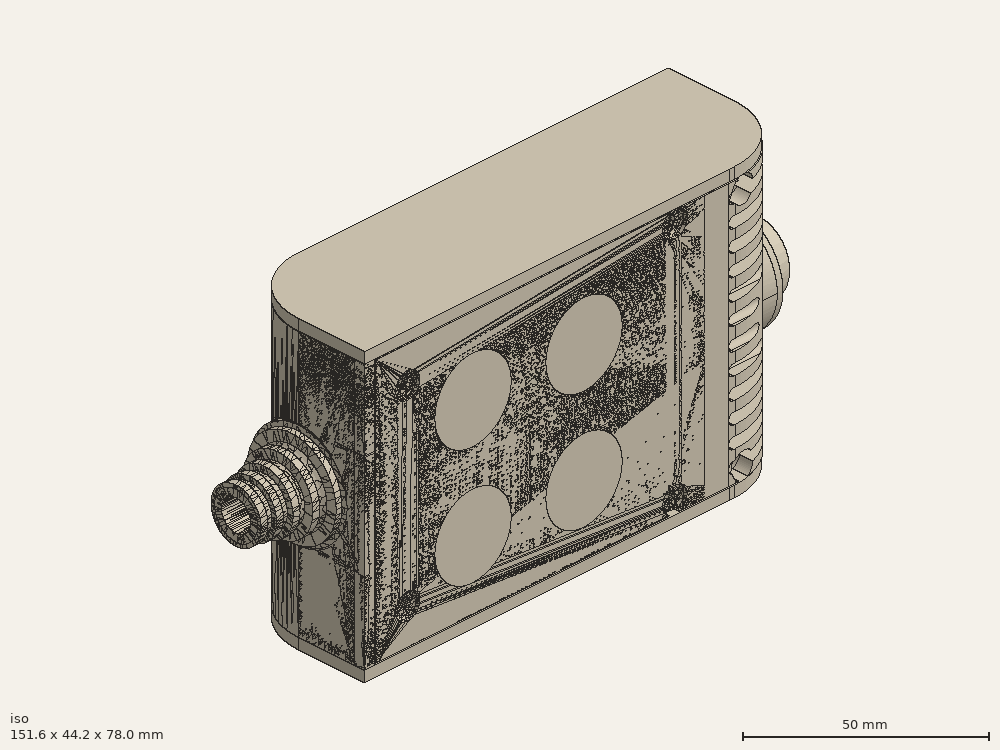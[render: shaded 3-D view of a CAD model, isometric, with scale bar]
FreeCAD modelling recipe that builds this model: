
FCSTD DOCUMENT  (FreeCAD 0.19R0.19.2)
Label: enclosure_190FCStd
License: All rights reserved
LicenseURL: http://en.wikipedia.org/wiki/All_rights_reserved
objects: Part::Revolution×152, Part::MultiFuse×146, Part::Feature×146, Sketcher::SketchObject×84, Part::Cut×70, Part::Cylinder×70, Part::Extrusion×67, Part::Fillet×58, Part::Box×36, App::MeasureDistance×4, PartDesign::Body×2, Image::ImagePlane×1
note: 831 computed .brp shape members not serialized (recipe doc carries the construction recipe); baked Part::Feature solids carry a one-line shape summary decoded from their .brp

FEATURE [Sketcher::SketchObject] Sketch  label="topSketch"
  FullyConstrained = true
  sketch-geometry (20):
    g0: LineSegment StartX=5.21097e-06 StartY=3 StartZ=0 EndX=5.21097e-06 EndY=19 EndZ=0
    g1: ArcOfCircle CenterX=19 CenterY=19 CenterZ=0 NormalX=0 NormalY=0 NormalZ=1 AngleXU=0 Radius=19 StartAngle=1.5708 EndAngle=3.14159
    g2: ArcOfCircle CenterX=19 CenterY=19 CenterZ=0 NormalX=0 NormalY=0 NormalZ=1 AngleXU=0 Radius=16 StartAngle=1.5708 EndAngle=3.14159
    g3: LineSegment StartX=114 StartY=35 StartZ=0 EndX=19 EndY=35 EndZ=0
    g4: LineSegment StartX=5.21097e-06 StartY=3 StartZ=0 EndX=5.21097e-06 EndY=0 EndZ=0
    g5: LineSegment StartX=3 StartY=0 StartZ=0 EndX=5.21097e-06 EndY=0 EndZ=0
    g6: LineSegment StartX=3 StartY=19 StartZ=0 EndX=3 EndY=0 EndZ=0
    g7: LineSegment StartX=19 StartY=38 StartZ=0 EndX=124 EndY=38 EndZ=0
    g8: Circle CenterX=119 CenterY=35 CenterZ=0 NormalX=0 NormalY=0 NormalZ=1 AngleXU=0 Radius=1
    g9: Circle CenterX=121 CenterY=35 CenterZ=0 NormalX=0 NormalY=0 NormalZ=1 AngleXU=0 Radius=1
    g10: Circle CenterX=121 CenterY=33 CenterZ=0 NormalX=0 NormalY=0 NormalZ=1 AngleXU=0 Radius=1
    g11: BSplineCurve PolesCount=3 KnotsCount=2 Degree=2 IsPeriodic=0
    g12: GeomPoint X=119 Y=35 Z=0
    g13: GeomPoint X=121 Y=33 Z=0
    g14: LineSegment StartX=119 StartY=35 StartZ=0 EndX=114 EndY=35 EndZ=0
    g15: ArcOfCircle CenterX=105 CenterY=19 CenterZ=0 NormalX=0 NormalY=0 NormalZ=1 AngleXU=0 Radius=19 StartAngle=5.7297 EndAngle=6.28319
    g16: ArcOfCircle CenterX=105 CenterY=19 CenterZ=0 NormalX=0 NormalY=0 NormalZ=1 AngleXU=0 Radius=16 StartAngle=5.60905 EndAngle=6.28319
    g17: LineSegment StartX=121 StartY=33 StartZ=0 EndX=121 EndY=19 EndZ=0
    g18: LineSegment StartX=124 StartY=38 StartZ=0 EndX=124 EndY=19 EndZ=0
    g19: LineSegment StartX=117.5 StartY=9.01251 StartZ=0 EndX=121.163 EndY=9.0125 EndZ=0
  constraints (46):
    c: Vertical(g0)
    c: Block(g0)
    c: Coincident(g1,g0)
    c: Block(g1)
    c: Coincident(g2,g1)
    c: Block(g2)
    c: Coincident(g3,g2)
    c: Horizontal(g3)
    c: Tangent(g3,g2)
    c: Coincident(g4,g0)
    c: Distance(g4) = 3
    c: Vertical(g4)
    c: Coincident(g5,g4)
    c: Horizontal(g5)
    c: Coincident(g6,g2)
    c: Coincident(g6,g5)
    c: Vertical(g6)
    c: Horizontal(g7)
    c: Distance(g7) = 105
    c: Coincident(g7,g1)
    c: Block(g3)
    c: Weight(g8) = 1
    c: Equal(g8,g9)
    c: Equal(g8,g10)
    c: InternalAlignment(g8,g11)
    c: InternalAlignment(g9,g11)
    c: InternalAlignment(g10,g11)
    c: InternalAlignment(g12,g11)
    c: InternalAlignment(g13,g11)
    c: Block(g11)
    c: Coincident(g14,g11)
    c: Coincident(g14,g3)
    c: Horizontal(g14)
    c: Block(g15)
    c: Coincident(g16,g15)
    c: Block(g16)
    c: Coincident(g17,g11)
    c: Coincident(g17,g16)
    c: Vertical(g17)
    c: Distance(g17) = 14
    c: Coincident(g18,g7)
    c: Coincident(g18,g15)
    c: Vertical(g18)
    c: Distance(g18) = 19
    c: Coincident(g19,g16)
    c: Coincident(g19,g15)
FEATURE [Sketcher::SketchObject] Sketch001  label="bottomSketch"
  FullyConstrained = true
  sketch-geometry (32):
    g0: LineSegment StartX=3.3 StartY=-6.03275e-07 StartZ=0 EndX=98 EndY=-6.03275e-07 EndZ=0
    g1: ArcOfCircle CenterX=98 CenterY=19 CenterZ=0 NormalX=0 NormalY=0 NormalZ=1 AngleXU=0 Radius=19 StartAngle=4.71239 EndAngle=5.71103
    g2: LineSegment StartX=6.3 StartY=8 StartZ=0 EndX=3.3 EndY=8 EndZ=0
    g3: LineSegment StartX=3.3 StartY=8 StartZ=0 EndX=3.3 EndY=-6.03275e-07 EndZ=0
    g4: ArcOfCircle CenterX=8.3 CenterY=5 CenterZ=0 NormalX=0 NormalY=0 NormalZ=1 AngleXU=0 Radius=2 StartAngle=3.14159 EndAngle=4.71239
    g5: LineSegment StartX=6.3 StartY=8 StartZ=0 EndX=6.3 EndY=5 EndZ=0
    g6: ArcOfCircle CenterX=98 CenterY=19 CenterZ=0 NormalX=0 NormalY=0 NormalZ=1 AngleXU=0 Radius=12.7 StartAngle=4.71239 EndAngle=6.28319
    g7: LineSegment StartX=94.7 StartY=3 StartZ=0 EndX=8.3 EndY=3 EndZ=0
    g8-g12: Circle x5 (B-spline internal-alignment scaffolding for g13; pole/knot coordinates omitted)
    g13: BSplineCurve PolesCount=5 KnotsCount=3 Degree=3 IsPeriodic=0
    g14: GeomPoint X=98 Y=6.3 Z=0
    g15: GeomPoint X=96.3938 Y=4.71946 Z=0
    g16: GeomPoint X=94.7 Y=3 Z=0
    g17-g23: Circle x7 (B-spline internal-alignment scaffolding for g24; pole/knot coordinates omitted)
    g24: BSplineCurve PolesCount=7 KnotsCount=5 Degree=3 IsPeriodic=0
    g25-g29: GeomPoint x5 (B-spline internal-alignment scaffolding for g24; pole/knot coordinates omitted)
    g30: ArcOfCircle CenterX=98 CenterY=19 CenterZ=0 NormalX=0 NormalY=0 NormalZ=1 AngleXU=0 Radius=15.7 StartAngle=5.81226 EndAngle=6.28319
    g31: LineSegment StartX=110.7 StartY=19 StartZ=0 EndX=113.7 EndY=19 EndZ=0
  constraints (41):
    c: Horizontal(g0)
    c: Coincident(g1,g0)
    c: Block(g1)
    c: Horizontal(g2)
    c: Distance(g2) = 3
    c: Coincident(g3,g2)
    c: Vertical(g3)
    c: Coincident(g3,g0)
    c: Block(g4)
    c: Block(g2)
    c: Coincident(g5,g2)
    c: Coincident(g5,g4)
    c: Vertical(g5)
    c: Coincident(g6,g1)
    c: Block(g6)
    c: Coincident(g7,g4)
    c: Horizontal(g7)
    c: Block(g0)
    c: Block(g7)
    c: Block(g3)
    c: Coincident(g13,g6)
    c: Weight(g8) = 1
    c: Equal(g8, g9-g12) x4
    c: Coincident(g13,g7)
    c: InternalAlignment(g8-g12 -> g13) x5
    c: InternalAlignment(g14,g13)
    c: InternalAlignment(g15,g13)
    c: InternalAlignment(g16,g13)
    c: Block(g13)
    c: Weight(g17) = 1
    c: Equal(g17, g18-g23) x6
    c: Coincident(g24,g1)
    c: InternalAlignment(g17-g23 -> g24) x7
    c: InternalAlignment(g25-g29 -> g24) x5
    c: Block(g24)
    c: Coincident(g30,g24)
    c: Coincident(g31,g6)
    c: Coincident(g31,g30)
    c: Horizontal(g31)
    c: Block(g31)
    c: Block(g30)
FEATURE [Part::Extrusion] Extrude  label="top"
  Base = -> Sketch
  Dir = (0,0,1)
  DirMode = 2
  FaceMakerClass = Part::FaceMakerBullseye
  LengthFwd = 72
  LengthRev = 0
  Solid = true
  Symmetric = false
FEATURE [Part::Extrusion] Extrude001  label="bottom"
  Base = -> Sketch001
  Dir = (0,0,1)
  DirMode = 2
  FaceMakerClass = Part::FaceMakerBullseye
  LengthFwd = 71.4
  LengthRev = 0
  Placement = pos=(0,0,0.3) rot=(0,0,1;0rad)
  Solid = true
  Symmetric = false
FEATURE [Sketcher::SketchObject] Sketch002  label="topSketch001"
  FullyConstrained = true
  sketch-geometry (8):
    g0: ArcOfCircle CenterX=19 CenterY=19.0975 CenterZ=0 NormalX=0 NormalY=0 NormalZ=1 AngleXU=0 Radius=18.9025 StartAngle=1.5708 EndAngle=3.14674
    g1: LineSegment StartX=0.0977805 StartY=19.0003 StartZ=0 EndX=0.0977805 EndY=0.000251602 EndZ=0
    g2: LineSegment StartX=19 StartY=38 StartZ=0 EndX=124 EndY=38 EndZ=0
    g3: LineSegment StartX=0.0977805 StartY=0.000251602 StartZ=0 EndX=105.098 EndY=0.000251602 EndZ=0
    g4: LineSegment StartX=124 StartY=38 StartZ=0 EndX=125.616 EndY=38 EndZ=0
    g5: LineSegment StartX=105.098 StartY=0.000251602 StartZ=0 EndX=106.713 EndY=0.000251602 EndZ=0
    g6: ArcOfCircle CenterX=106.616 CenterY=19 CenterZ=0 NormalX=0 NormalY=0 NormalZ=1 AngleXU=0 Radius=19 StartAngle=4.71754 EndAngle=6.28319
    g7: LineSegment StartX=125.616 StartY=38 StartZ=0 EndX=125.616 EndY=19 EndZ=0
  constraints (21):
    c: Block(g0)
    c: Coincident(g1,g0)
    c: Vertical(g1)
    c: Horizontal(g2)
    c: Distance(g2) = 105
    c: Coincident(g2,g0)
    c: Distance(g1) = 19
    c: Coincident(g3,g1)
    c: Horizontal(g3)
    c: Distance(g3) = 105
    c: Coincident(g4,g2)
    c: Horizontal(g4)
    c: Distance(g4) = 1.61553
    c: Horizontal(g5)
    c: Equal(g4,g5) = 1.61553
    c: Coincident(g5,g3)
    c: Block(g6)
    c: Coincident(g6,g5)
    c: Coincident(g7,g4)
    c: Coincident(g7,g6)
    c: Vertical(g7)
FEATURE [Part::Extrusion] Extrude002  label="sideA"
  Base = -> Sketch002
  Dir = (0,0,1)
  DirMode = 2
  FaceMakerClass = Part::FaceMakerBullseye
  LengthFwd = 3
  LengthRev = 0
  Placement = pos=(0,0,-3) rot=(0,0,1;0rad)
  Solid = true
  Symmetric = false
FEATURE [Sketcher::SketchObject] Sketch003  label="topSketch002"
  FullyConstrained = true
  sketch-geometry (6):
    g0: LineSegment StartX=19 StartY=38 StartZ=0 EndX=117 EndY=38 EndZ=0
    g1: ArcOfCircle CenterX=19 CenterY=19 CenterZ=0 NormalX=0 NormalY=0 NormalZ=1 AngleXU=0 Radius=19 StartAngle=1.5708 EndAngle=3.14159
    g2: LineSegment StartX=117 StartY=38 StartZ=0 EndX=117 EndY=19 EndZ=0
    g3: LineSegment StartX=98 StartY=1.0161e-12 StartZ=0 EndX=5.22862e-06 EndY=1.0161e-12 EndZ=0
    g4: LineSegment StartX=5.22862e-06 StartY=19 StartZ=0 EndX=5.22862e-06 EndY=1.0161e-12 EndZ=0
    g5: ArcOfCircle CenterX=98 CenterY=19 CenterZ=0 NormalX=0 NormalY=0 NormalZ=1 AngleXU=0 Radius=19 StartAngle=4.71239 EndAngle=6.28319
  constraints (16):
    c: Horizontal(g0)
    c: Distance(g0) = 98
    c: Coincident(g1,g0)
    c: Block(g1)
    c: Coincident(g2,g0)
    c: Vertical(g2)
    c: Distance(g2) = 19
    c: Horizontal(g3)
    c: Coincident(g4,g1)
    c: Vertical(g4)
    c: Coincident(g3,g4)
    c: Block(g3)
    c: Coincident(g5,g2)
    c: Coincident(g5,g3)
    c: Block(g0)
    c: Block(g5)
FEATURE [Sketcher::SketchObject] Sketch004
  FullyConstrained = true
  MapMode = 3
  Placement = pos=(0,0,0) rot=(1,0,0;1.5708rad)
  Support = -> [Extrude]
  sketch-geometry (8):
    g0: Circle CenterX=80.351 CenterY=-67.6202 CenterZ=0 NormalX=0 NormalY=0 NormalZ=1 AngleXU=0 Radius=2
    g1: Circle CenterX=80.351 CenterY=-67.6202 CenterZ=0 NormalX=0 NormalY=0 NormalZ=1 AngleXU=0 Radius=3
    g2: Circle CenterX=80.351 CenterY=-4.92017 CenterZ=0 NormalX=0 NormalY=0 NormalZ=1 AngleXU=0 Radius=2
    g3: Circle CenterX=80.351 CenterY=-4.92017 CenterZ=0 NormalX=0 NormalY=0 NormalZ=1 AngleXU=0 Radius=3
    g4: Circle CenterX=23.851 CenterY=-4.92017 CenterZ=0 NormalX=0 NormalY=0 NormalZ=1 AngleXU=0 Radius=2
    g5: Circle CenterX=23.851 CenterY=-4.92017 CenterZ=0 NormalX=0 NormalY=0 NormalZ=1 AngleXU=0 Radius=3
    g6: Circle CenterX=23.851 CenterY=-67.6202 CenterZ=0 NormalX=0 NormalY=0 NormalZ=1 AngleXU=0 Radius=2
    g7: Circle CenterX=23.851 CenterY=-67.6202 CenterZ=0 NormalX=0 NormalY=0 NormalZ=1 AngleXU=0 Radius=3
  constraints (8):
    c: Block(g3)
    c: Block(g2)
    c: Block(g1)
    c: Block(g0)
    c: Block(g6)
    c: Block(g7)
    c: Block(g4)
    c: Block(g5)
FEATURE [Part::Extrusion] Extrude004
  Base = -> Sketch004
  Dir = (0,-1,2e-16)
  DirMode = 2
  FaceMakerClass = Part::FaceMakerBullseye
  LengthFwd = 6
  LengthRev = 0
  Placement = pos=(0,9,0) rot=(0,0,1;0rad)
  Solid = true
  Symmetric = false
FEATURE [Sketcher::SketchObject] Sketch005
  FullyConstrained = true
  MapMode = 3
  Placement = pos=(0,0,0) rot=(1,0,0;1.5708rad)
  Support = -> [Extrude]
  sketch-geometry (8):
    g0: Circle CenterX=80.351 CenterY=-67.6202 CenterZ=0 NormalX=0 NormalY=0 NormalZ=1 AngleXU=0 Radius=3
    g1: Circle CenterX=80.351 CenterY=-4.92017 CenterZ=0 NormalX=0 NormalY=0 NormalZ=1 AngleXU=0 Radius=3
    g2: Circle CenterX=23.851 CenterY=-4.92017 CenterZ=0 NormalX=0 NormalY=0 NormalZ=1 AngleXU=0 Radius=3
    g3: Circle CenterX=23.851 CenterY=-67.6202 CenterZ=0 NormalX=0 NormalY=0 NormalZ=1 AngleXU=0 Radius=3
    g4: Circle CenterX=23.851 CenterY=-67.6202 CenterZ=0 NormalX=0 NormalY=0 NormalZ=1 AngleXU=0 Radius=5
    g5: Circle CenterX=80.351 CenterY=-67.6202 CenterZ=0 NormalX=0 NormalY=0 NormalZ=1 AngleXU=0 Radius=5
    g6: Circle CenterX=23.851 CenterY=-4.92017 CenterZ=0 NormalX=0 NormalY=0 NormalZ=1 AngleXU=0 Radius=5
    g7: Circle CenterX=80.351 CenterY=-4.92017 CenterZ=0 NormalX=0 NormalY=0 NormalZ=1 AngleXU=0 Radius=5
  constraints (8):
    c: Block(g1)
    c: Block(g0)
    c: Block(g3)
    c: Block(g2)
    c: Block(g5)
    c: Block(g4)
    c: Block(g6)
    c: Block(g7)
FEATURE [Part::Extrusion] Extrude005
  Base = -> Sketch005
  Dir = (0,-1,2e-16)
  DirMode = 2
  FaceMakerClass = Part::FaceMakerBullseye
  LengthFwd = 2
  LengthRev = 0
  Solid = true
  Symmetric = false
FEATURE [Sketcher::SketchObject] Sketch006
  FullyConstrained = true
  MapMode = 3
  Placement = pos=(0,0,0) rot=(1,0,0;1.5708rad)
  sketch-geometry (8):
    g0: Circle CenterX=80.351 CenterY=-67.6202 CenterZ=0 NormalX=0 NormalY=0 NormalZ=1 AngleXU=0 Radius=3
    g1: Circle CenterX=80.351 CenterY=-4.92017 CenterZ=0 NormalX=0 NormalY=0 NormalZ=1 AngleXU=0 Radius=3
    g2: Circle CenterX=23.851 CenterY=-4.92017 CenterZ=0 NormalX=0 NormalY=0 NormalZ=1 AngleXU=0 Radius=3
    g3: Circle CenterX=23.851 CenterY=-67.6202 CenterZ=0 NormalX=0 NormalY=0 NormalZ=1 AngleXU=0 Radius=3
    g4: Circle CenterX=23.851 CenterY=-67.6202 CenterZ=0 NormalX=0 NormalY=0 NormalZ=1 AngleXU=0 Radius=5
    g5: Circle CenterX=80.351 CenterY=-67.6202 CenterZ=0 NormalX=0 NormalY=0 NormalZ=1 AngleXU=0 Radius=5
    g6: Circle CenterX=23.851 CenterY=-4.92017 CenterZ=0 NormalX=0 NormalY=0 NormalZ=1 AngleXU=0 Radius=5
    g7: Circle CenterX=80.351 CenterY=-4.92017 CenterZ=0 NormalX=0 NormalY=0 NormalZ=1 AngleXU=0 Radius=5
  constraints (8):
    c: Block(g1)
    c: Block(g0)
    c: Block(g3)
    c: Block(g2)
    c: Block(g5)
    c: Block(g4)
    c: Block(g6)
    c: Block(g7)
FEATURE [Part::Extrusion] Extrude007
  Base = -> Sketch006
  Dir = (0,-1,2e-16)
  DirMode = 2
  FaceMakerClass = Part::FaceMakerBullseye
  LengthFwd = 2
  LengthRev = 0
  Solid = true
  Symmetric = false
FEATURE [Part::Fillet] Fillet
  Base = -> Extrude007
  Edges = 4 edges r=1.99: [Edge6,Edge12,Edge18,Edge24]
FEATURE [Part::Cut] Cut
  Base = -> Extrude005
  Placement = pos=(0,5,0) rot=(0,0,1;0rad)
  Tool = -> Fillet
FEATURE [Part::MultiFuse] Fusion  label="pCBScrews"
  Placement = pos=(-2.5,0,72.3) rot=(0,0,1;0rad)
  Shapes = -> [Extrude004,Cut]
FEATURE [App::MeasureDistance] Distance  label="Distance: 0.69 mm"
  Distance = 0.685967
  P1 = (24.0138,2.9647,0.3)
  P2 = (23.8901,3,-0.373787)
FEATURE [App::MeasureDistance] Distance001  label="Distance: 0.53 mm"
  Distance = 0.533607
  P1 = (80.2939,3,72.2334)
  P2 = (80.281,2.99661,71.7)
FEATURE [Part::Fillet] Fillet001
  Base = -> Extrude001
  Edges = 1 edges r=2.4: [Edge17]
FEATURE [Part::Fillet] Fillet002  label="bottom001"
  Base = -> Fillet001
  Edges = 1 edges r=2.4: [Edge36]
FEATURE [Part::Fillet] Fillet003  label="top001"
  Base = -> Extrude
  Edges = 1 edges r=2: [Edge1]
FEATURE [Sketcher::SketchObject] Sketch007
  FullyConstrained = true
  sketch-geometry (16):
    g0: LineSegment StartX=4 StartY=0 StartZ=0 EndX=4 EndY=2.4 EndZ=0
    g1: LineSegment StartX=4 StartY=2.4 StartZ=0 EndX=7 EndY=2.4 EndZ=0
    g2: LineSegment StartX=4 StartY=0 StartZ=0 EndX=5.7 EndY=0 EndZ=0
    g3: LineSegment StartX=5.7 StartY=0 StartZ=0 EndX=5.7 EndY=-5.6 EndZ=0
    g4-g8: Circle x5 (B-spline internal-alignment scaffolding for g9; pole/knot coordinates omitted)
    g9: BSplineCurve PolesCount=5 KnotsCount=3 Degree=3 IsPeriodic=0
    g10: GeomPoint X=7 Y=2.4 Z=0
    g11: GeomPoint X=10.4582 Y=-1.55472 Z=0
    g12: GeomPoint X=14 Y=-5.6 Z=0
    g13: LineSegment StartX=14 StartY=-5.6 StartZ=0 EndX=14 EndY=-14.1 EndZ=0
    g14: LineSegment StartX=14 StartY=-14.1 StartZ=0 EndX=6.5 EndY=-14.1 EndZ=0
    g15: LineSegment StartX=5.7 StartY=-5.6 StartZ=0 EndX=6.5 EndY=-14.1 EndZ=0
  constraints (28):
    c: Distance(g0) = 2.4
    c: Vertical(g0)
    c: Block(g0)
    c: Coincident(g1,g0)
    c: Horizontal(g1)
    c: Distance(g1) = 3
    c: Coincident(g2,g0)
    c: Horizontal(g2)
    c: Distance(g2) = 1.7
    c: Coincident(g3,g2)
    c: Vertical(g3)
    c: Distance(g3) = 5.6
    c: Coincident(g9,g1)
    c: Weight(g4) = 1
    c: Equal(g4, g5-g8) x4
    c: InternalAlignment(g4-g8 -> g9) x5
    c: InternalAlignment(g10,g9)
    c: InternalAlignment(g11,g9)
    c: InternalAlignment(g12,g9)
    c: Block(g9)
    c: Coincident(g13,g9)
    c: Vertical(g13)
    c: Distance(g13) = 8.5
    c: Coincident(g14,g13)
    c: Horizontal(g14)
    c: Distance(g14) = 7.5
    c: Coincident(g15,g3)
    c: Coincident(g15,g14)
FEATURE [Part::Feature] Face
  shape: bbox 10 x 16.5 x 2e-07 mm, 1 faces, 0 solids (baked)
FEATURE [Part::Revolution] Revolve  label="plugHousing"
  Angle = 360
  Axis = (0,1,0)
  Base = (0,0,0)
  FaceMakerClass = Part::FaceMakerBullseye
  Placement = pos=(0,0,36.15) rot=(0,0,1;0rad)
  Solid = false
  Source = -> Face
  Symmetric = false
FEATURE [Part::Feature] Face001
  shape: bbox 10 x 16.5 x 2e-07 mm, 1 faces, 0 solids (baked)
FEATURE [Part::Revolution] Revolve001  label="plugHousing001"
  Angle = 360
  Axis = (0,1,0)
  Base = (0,0,0)
  FaceMakerClass = Part::FaceMakerBullseye
  Placement = pos=(0,0,36.15) rot=(0,0,1;0rad)
  Solid = false
  Source = -> Face001
  Symmetric = false
FEATURE [Part::MultiFuse] Fusion001  label="plugHousing002"
  Placement = pos=(0,0,0) rot=(0,0,1;1.5708rad)
  Shapes = -> [Revolve001,Revolve]
FEATURE [Part::Feature] Face002
  shape: bbox 10 x 16.5 x 2e-07 mm, 1 faces, 0 solids (baked)
FEATURE [Part::Revolution] Revolve003  label="plugHousing005"
  Angle = 360
  Axis = (0,1,0)
  Base = (0,0,0)
  FaceMakerClass = Part::FaceMakerBullseye
  Placement = pos=(0,0,36.15) rot=(0,0,1;0rad)
  Solid = false
  Source = -> Face002
  Symmetric = false
FEATURE [Part::Feature] Face003
  shape: bbox 10 x 16.5 x 2e-07 mm, 1 faces, 0 solids (baked)
FEATURE [Part::Revolution] Revolve002  label="plugHousing003"
  Angle = 360
  Axis = (0,1,0)
  Base = (0,0,0)
  FaceMakerClass = Part::FaceMakerBullseye
  Placement = pos=(0,0,36.15) rot=(0,0,1;0rad)
  Solid = false
  Source = -> Face003
  Symmetric = false
FEATURE [Part::MultiFuse] Fusion002  label="plugHousing004"
  Placement = pos=(0,0,0) rot=(0,0,1;1.5708rad)
  Shapes = -> [Revolve002,Revolve003]
FEATURE [Part::MultiFuse] Fusion003  label="plugHousing006"
  Placement = pos=(0,19,0) rot=(0,0,1;3.14159rad)
  Shapes = -> [Fusion002,Fusion001]
FEATURE [Part::Feature] Face004
  shape: bbox 10 x 16.5 x 2e-07 mm, 1 faces, 0 solids (baked)
FEATURE [Part::Revolution] Revolve006  label="plugHousing010"
  Angle = 360
  Axis = (0,1,0)
  Base = (0,0,0)
  FaceMakerClass = Part::FaceMakerBullseye
  Placement = pos=(0,0,36.15) rot=(0,0,1;0rad)
  Solid = false
  Source = -> Face004
  Symmetric = false
FEATURE [Part::Feature] Face005
  shape: bbox 10 x 16.5 x 2e-07 mm, 1 faces, 0 solids (baked)
FEATURE [Part::Revolution] Revolve007  label="plugHousing011"
  Angle = 360
  Axis = (0,1,0)
  Base = (0,0,0)
  FaceMakerClass = Part::FaceMakerBullseye
  Placement = pos=(0,0,36.15) rot=(0,0,1;0rad)
  Solid = false
  Source = -> Face005
  Symmetric = false
FEATURE [Part::Feature] Face006
  shape: bbox 10 x 16.5 x 2e-07 mm, 1 faces, 0 solids (baked)
FEATURE [Part::Revolution] Revolve004  label="plugHousing007"
  Angle = 360
  Axis = (0,1,0)
  Base = (0,0,0)
  FaceMakerClass = Part::FaceMakerBullseye
  Placement = pos=(0,0,36.15) rot=(0,0,1;0rad)
  Solid = false
  Source = -> Face006
  Symmetric = false
FEATURE [Part::MultiFuse] Fusion004  label="plugHousing009"
  Placement = pos=(0,0,0) rot=(0,0,1;1.5708rad)
  Shapes = -> [Revolve004,Revolve007]
FEATURE [Part::Feature] Face007
  shape: bbox 10 x 16.5 x 2e-07 mm, 1 faces, 0 solids (baked)
FEATURE [Part::Revolution] Revolve005  label="plugHousing008"
  Angle = 360
  Axis = (0,1,0)
  Base = (0,0,0)
  FaceMakerClass = Part::FaceMakerBullseye
  Placement = pos=(0,0,36.15) rot=(0,0,1;0rad)
  Solid = false
  Source = -> Face007
  Symmetric = false
FEATURE [Part::MultiFuse] Fusion005  label="plugHousing012"
  Placement = pos=(0,0,0) rot=(0,0,1;1.5708rad)
  Shapes = -> [Revolve006,Revolve005]
FEATURE [Part::MultiFuse] Fusion006  label="plugHousing013"
  Placement = pos=(0,19,0) rot=(0,0,1;3.14159rad)
  Shapes = -> [Fusion005,Fusion004]
FEATURE [Part::MultiFuse] Fusion007  label="plugHousing014"
  Placement = pos=(122.621,0,-0.15) rot=(0,0,1;0rad)
  Shapes = -> [Fusion003,Fusion006]
FEATURE [Part::Cylinder] Cylinder002
  Angle = 360
  AttacherType = Attacher::AttachEngine3D
  Height = 20
  Placement = pos=(0,0,36.15) rot=(0,0,1;0rad)
  Radius = 4
FEATURE [Part::Cylinder] Cylinder003
  Angle = 360
  AttacherType = Attacher::AttachEngine3D
  Height = 10
  Placement = pos=(0,0,36.15) rot=(0,0,1;0rad)
  Radius = 4
FEATURE [Part::MultiFuse] Fusion009  label="removeToCreateHoleForPlugHousing"
  Placement = pos=(70,19,36.15) rot=(0,1,0;1.5708rad)
  Shapes = -> [Cylinder002,Cylinder003]
FEATURE [Part::Cylinder] Cylinder004
  Angle = 360
  AttacherType = Attacher::AttachEngine3D
  Height = 20
  Placement = pos=(0,0,36.15) rot=(0,0,1;0rad)
  Radius = 4
FEATURE [Part::Cylinder] Cylinder005
  Angle = 360
  AttacherType = Attacher::AttachEngine3D
  Height = 10
  Placement = pos=(0,0,36.15) rot=(0,0,1;0rad)
  Radius = 4
FEATURE [Part::MultiFuse] Fusion010  label="removeToCreateHoleForPlugHousing001"
  Placement = pos=(70,19,36.15) rot=(0,1,0;1.5708rad)
  Shapes = -> [Cylinder004,Cylinder005]
FEATURE [Part::Cut] Cut001
  Base = -> Fillet003
  Tool = -> Fusion010
FEATURE [Part::Cut] Cut002  label="Bottom"
  Base = -> Fillet002
  Tool = -> Fusion009
FEATURE [Part::Feature] Face008
  shape: bbox 10 x 16.5 x 2e-07 mm, 1 faces, 0 solids (baked)
FEATURE [Part::Revolution] Revolve011  label="plugHousing021"
  Angle = 360
  Axis = (0,1,0)
  Base = (0,0,0)
  FaceMakerClass = Part::FaceMakerBullseye
  Placement = pos=(0,0,36.15) rot=(0,0,1;0rad)
  Solid = false
  Source = -> Face008
  Symmetric = false
FEATURE [Part::Feature] Face009
  shape: bbox 10 x 16.5 x 2e-07 mm, 1 faces, 0 solids (baked)
FEATURE [Part::Revolution] Revolve012  label="plugHousing022"
  Angle = 360
  Axis = (0,1,0)
  Base = (0,0,0)
  FaceMakerClass = Part::FaceMakerBullseye
  Placement = pos=(0,0,36.15) rot=(0,0,1;0rad)
  Solid = false
  Source = -> Face009
  Symmetric = false
FEATURE [Part::Feature] Face010 .. Face013  x4 (patterned run collapsed; names and placements below)
  shape: bbox 10 x 16.5 x 2e-07 mm, 1 faces, 0 solids (baked)
FEATURE [Part::Revolution] Revolve015  label="plugHousing027"
  Angle = 360
  Axis = (0,1,0)
  Base = (0,0,0)
  FaceMakerClass = Part::FaceMakerBullseye
  Placement = pos=(0,0,36.15) rot=(0,0,1;0rad)
  Solid = false
  Source = -> Face013
  Symmetric = false
FEATURE [Part::Feature] Face014
  shape: bbox 10 x 16.5 x 2e-07 mm, 1 faces, 0 solids (baked)
FEATURE [Part::Feature] Face015
  shape: bbox 10 x 16.5 x 2e-07 mm, 1 faces, 0 solids (baked)
FEATURE [Part::Feature] Face016
  shape: bbox 10 x 16.5 x 2e-07 mm, 1 faces, 0 solids (baked)
FEATURE [Part::Revolution] Revolve019  label="plugHousing033"
  Angle = 360
  Axis = (0,1,0)
  Base = (0,0,0)
  FaceMakerClass = Part::FaceMakerBullseye
  Placement = pos=(0,0,36.15) rot=(0,0,1;0rad)
  Solid = false
  Source = -> Face016
  Symmetric = false
FEATURE [Part::Feature] Face017
  shape: bbox 10 x 16.5 x 2e-07 mm, 1 faces, 0 solids (baked)
FEATURE [Part::Revolution] Revolve020  label="plugHousing034"
  Angle = 360
  Axis = (0,1,0)
  Base = (0,0,0)
  FaceMakerClass = Part::FaceMakerBullseye
  Placement = pos=(0,0,36.15) rot=(0,0,1;0rad)
  Solid = false
  Source = -> Face017
  Symmetric = false
FEATURE [Part::Feature] Face018
  shape: bbox 10 x 16.5 x 2e-07 mm, 1 faces, 0 solids (baked)
FEATURE [Part::Revolution] Revolve016  label="plugHousing030"
  Angle = 360
  Axis = (0,1,0)
  Base = (0,0,0)
  FaceMakerClass = Part::FaceMakerBullseye
  Placement = pos=(0,0,36.15) rot=(0,0,1;0rad)
  Solid = false
  Source = -> Face018
  Symmetric = false
FEATURE [Part::MultiFuse] Fusion020  label="plugHousing038"
  Placement = pos=(0,0,0) rot=(0,0,1;1.5708rad)
  Shapes = -> [Revolve016,Revolve020]
FEATURE [Part::Feature] Face019
  shape: bbox 10 x 16.5 x 2e-07 mm, 1 faces, 0 solids (baked)
FEATURE [Part::Feature] Face020
  shape: bbox 10 x 16.5 x 2e-07 mm, 1 faces, 0 solids (baked)
FEATURE [Part::Revolution] Revolve017  label="plugHousing031"
  Angle = 360
  Axis = (0,1,0)
  Base = (0,0,0)
  FaceMakerClass = Part::FaceMakerBullseye
  Placement = pos=(0,0,36.15) rot=(0,0,1;0rad)
  Solid = false
  Source = -> Face020
  Symmetric = false
FEATURE [Part::MultiFuse] Fusion021  label="plugHousing039"
  Placement = pos=(0,0,0) rot=(0,0,1;1.5708rad)
  Shapes = -> [Revolve019,Revolve017]
FEATURE [Part::MultiFuse] Fusion023  label="plugHousing041"
  Placement = pos=(0,19,0) rot=(0,0,1;3.14159rad)
  Shapes = -> [Fusion021,Fusion020]
FEATURE [Part::Revolution] Revolve022  label="plugHousing043"
  Angle = 360
  Axis = (0,1,0)
  Base = (0,0,0)
  FaceMakerClass = Part::FaceMakerBullseye
  Placement = pos=(0,0,36.15) rot=(0,0,1;0rad)
  Solid = false
  Source = -> Face019
  Symmetric = false
FEATURE [Part::Feature] Face021
  shape: bbox 10 x 16.5 x 2e-07 mm, 1 faces, 0 solids (baked)
FEATURE [Part::Revolution] Revolve023  label="plugHousing044"
  Angle = 360
  Axis = (0,1,0)
  Base = (0,0,0)
  FaceMakerClass = Part::FaceMakerBullseye
  Placement = pos=(0,0,36.15) rot=(0,0,1;0rad)
  Solid = false
  Source = -> Face021
  Symmetric = false
FEATURE [Part::Feature] Face022
  shape: bbox 10 x 16.5 x 2e-07 mm, 1 faces, 0 solids (baked)
FEATURE [Part::Revolution] Revolve018  label="plugHousing032"
  Angle = 360
  Axis = (0,1,0)
  Base = (0,0,0)
  FaceMakerClass = Part::FaceMakerBullseye
  Placement = pos=(0,0,36.15) rot=(0,0,1;0rad)
  Solid = false
  Source = -> Face022
  Symmetric = false
FEATURE [Part::MultiFuse] Fusion022  label="plugHousing040"
  Placement = pos=(0,0,0) rot=(0,0,1;1.5708rad)
  Shapes = -> [Revolve018,Revolve023]
FEATURE [Part::Feature] Face023
  shape: bbox 10 x 16.5 x 2e-07 mm, 1 faces, 0 solids (baked)
FEATURE [Part::Revolution] Revolve021  label="plugHousing035"
  Angle = 360
  Axis = (0,1,0)
  Base = (0,0,0)
  FaceMakerClass = Part::FaceMakerBullseye
  Placement = pos=(0,0,36.15) rot=(0,0,1;0rad)
  Solid = false
  Source = -> Face023
  Symmetric = false
FEATURE [Part::MultiFuse] Fusion018  label="plugHousing036"
  Placement = pos=(0,0,0) rot=(0,0,1;1.5708rad)
  Shapes = -> [Revolve022,Revolve021]
FEATURE [Part::MultiFuse] Fusion019  label="plugHousing037"
  Placement = pos=(0,19,0) rot=(0,0,1;3.14159rad)
  Shapes = -> [Fusion018,Fusion022]
FEATURE [Part::MultiFuse] Fusion024  label="plugHousing042"
  Placement = pos=(122.621,0,-0.15) rot=(0,0,1;0rad)
  Shapes = -> [Fusion023,Fusion019]
FEATURE [Part::Cylinder] Cylinder006
  Angle = 360
  AttacherType = Attacher::AttachEngine3D
  Height = 20
  Placement = pos=(0,0,36.15) rot=(0,0,1;0rad)
  Radius = 14.3
FEATURE [Part::Cylinder] Cylinder007
  Angle = 360
  AttacherType = Attacher::AttachEngine3D
  Height = 10
  Placement = pos=(0,0,36.15) rot=(0,0,1;0rad)
  Radius = 4
FEATURE [Part::MultiFuse] Fusion026  label="removeToCreteHoleForPlugHousing"
  Placement = pos=(70,19,36) rot=(0,1,0;1.5708rad)
  Shapes = -> [Cylinder006,Cylinder007]
FEATURE [Part::Box] Box001  label="Cube001"
  AttacherType = Attacher::AttachEngine3D
  Height = 28
  Length = 3
  Placement = pos=(110.7,19,22) rot=(0,0,1;0rad)
  Width = 15.7
FEATURE [Part::Cut] Cut003  label="top002"
  Base = -> Cut001
  Tool = -> Fusion007
FEATURE [Part::Revolution] Revolve008  label="plugHousing015"
  Angle = 360
  Axis = (0,1,0)
  Base = (0,0,0)
  FaceMakerClass = Part::FaceMakerBullseye
  Placement = pos=(0,0,36.15) rot=(0,0,1;0rad)
  Solid = false
  Source = -> Face010
  Symmetric = false
FEATURE [Part::MultiFuse] Fusion013  label="plugHousing020"
  Placement = pos=(0,0,0) rot=(0,0,1;1.5708rad)
  Shapes = -> [Revolve008,Revolve012]
FEATURE [Part::Cut] Cut004  label="top003"
  Base = -> Cut003
  Placement = pos=(1,0,0) rot=(0,0,1;0rad)
  Tool = -> Fusion026
FEATURE [Part::Cylinder] Cylinder008
  Angle = 360
  AttacherType = Attacher::AttachEngine3D
  Height = 20
  Placement = pos=(0,0,36.15) rot=(0,0,1;0rad)
  Radius = 10.3
FEATURE [Part::Cylinder] Cylinder009
  Angle = 360
  AttacherType = Attacher::AttachEngine3D
  Height = 10
  Placement = pos=(0,0,36.15) rot=(0,0,1;0rad)
  Radius = 4
FEATURE [Part::MultiFuse] Fusion027  label="removeToCreteHoleForPlugHousing001"
  Placement = pos=(70,19,36) rot=(0,1,0;1.5708rad)
  Shapes = -> [Cylinder008,Cylinder009]
FEATURE [Part::Cut] Cut005  label="plugHousingTab"
  Base = -> Box001
  Tool = -> Fusion027
FEATURE [Part::MultiFuse] Fusion028  label="plugHousing045"
  Shapes = -> [Fusion024,Cut005]
FEATURE [Part::Box] Box002  label="Cube002"
  AttacherType = Attacher::AttachEngine3D
  Height = 28.8
  Length = 3
  Placement = pos=(107.3,28,21.6) rot=(0,0,1;0rad)
  Width = 7
FEATURE [Part::Box] Box003  label="Cube003"
  AttacherType = Attacher::AttachEngine3D
  Height = 3
  Length = 6.4
  Placement = pos=(107.3,28,18.6) rot=(0,0,1;0rad)
  Width = 7
FEATURE [Part::Box] Box004  label="Cube004"
  AttacherType = Attacher::AttachEngine3D
  Height = 3
  Length = 6.4
  Placement = pos=(107.3,28,50.4) rot=(0,0,1;0rad)
  Width = 7
FEATURE [Part::MultiFuse] Fusion029  label="plugHousingBracketHolder"
  Shapes = -> [Box004,Box002,Box003]
FEATURE [Part::Cylinder] Cylinder010
  Angle = 360
  AttacherType = Attacher::AttachEngine3D
  Height = 20
  Placement = pos=(0,0,36.15) rot=(0,0,1;0rad)
  Radius = 14.3
FEATURE [Part::Cylinder] Cylinder011
  Angle = 360
  AttacherType = Attacher::AttachEngine3D
  Height = 10
  Placement = pos=(0,0,36.15) rot=(0,0,1;0rad)
  Radius = 4
FEATURE [Part::MultiFuse] Fusion030  label="removeToCreteHoleForPlugHousing002"
  Placement = pos=(70,19,36) rot=(0,1,0;1.5708rad)
  Shapes = -> [Cylinder010,Cylinder011]
FEATURE [Part::Cut] Cut006  label="plugHousingBracketHolder001"
  Base = -> Fusion029
  Tool = -> Fusion030
FEATURE [Part::Cylinder] Cylinder012
  Angle = 360
  AttacherType = Attacher::AttachEngine3D
  Height = 20
  Placement = pos=(0,0,36.15) rot=(0,0,1;0rad)
  Radius = 7
FEATURE [Part::Cylinder] Cylinder013
  Angle = 360
  AttacherType = Attacher::AttachEngine3D
  Height = 10
  Placement = pos=(0,0,36.15) rot=(0,0,1;0rad)
  Radius = 4
FEATURE [Part::MultiFuse] Fusion032  label="removeToCreteHoleForPlugHousing003"
  Placement = pos=(70,19,36) rot=(0,1,0;1.5708rad)
  Shapes = -> [Cylinder012,Cylinder013]
FEATURE [Part::Cut] Cut007  label="bottom002"
  Base = -> Cut002
  Tool = -> Fusion032
FEATURE [Sketcher::SketchObject] Sketch008
  FullyConstrained = true
  sketch-geometry (54):
    g0: LineSegment StartX=-4.2 StartY=0 StartZ=0 EndX=-6.2 EndY=0 EndZ=0
    g1: LineSegment StartX=-14 StartY=-18 StartZ=0 EndX=-14 EndY=-26.5 EndZ=0
    g2: LineSegment StartX=-4.2 StartY=0 StartZ=0 EndX=-4.2 EndY=-13.4877 EndZ=0
    g3: Circle CenterX=-4.2 CenterY=-13.4877 CenterZ=0 NormalX=0 NormalY=0 NormalZ=1 AngleXU=0 Radius=1
    g4: Circle CenterX=-4.2 CenterY=-26.5 CenterZ=0 NormalX=0 NormalY=0 NormalZ=1 AngleXU=0 Radius=1
    g5: Circle CenterX=-8.2 CenterY=-26.5 CenterZ=0 NormalX=0 NormalY=0 NormalZ=1 AngleXU=0 Radius=1
    g6: BSplineCurve PolesCount=3 KnotsCount=2 Degree=2 IsPeriodic=0
    g7: GeomPoint X=-4.2 Y=-13.4877 Z=0
    g8: GeomPoint X=-8.2 Y=-26.5 Z=0
    g9: LineSegment StartX=-14 StartY=-26.5 StartZ=0 EndX=-8.2 EndY=-26.5 EndZ=0
    g10: LineSegment StartX=-10.15 StartY=-12 StartZ=0 EndX=-10.15 EndY=-14 EndZ=0
    g11: LineSegment StartX=-12.8401 StartY=-16 StartZ=0 EndX=-10.1571 EndY=-16 EndZ=0
    g12: LineSegment StartX=-10.15 StartY=-14 StartZ=0 EndX=-8.70761 EndY=-14 EndZ=0
    g13: LineSegment StartX=-12.8401 StartY=-16 StartZ=0 EndX=-12.8401 EndY=-17.6958 EndZ=0
    g14: LineSegment StartX=-10.15 StartY=-12 StartZ=0 EndX=-7.79258 EndY=-12 EndZ=0
    g15: Circle CenterX=-6.2215 CenterY=-2 CenterZ=0 NormalX=0 NormalY=0 NormalZ=1 AngleXU=0 Radius=1
    g16: Circle CenterX=-6.22762 CenterY=-2.58724 CenterZ=0 NormalX=0 NormalY=0 NormalZ=1 AngleXU=0 Radius=1
    g17: Circle CenterX=-6.32538 CenterY=-4 CenterZ=0 NormalX=0 NormalY=0 NormalZ=1 AngleXU=0 Radius=1
    g18: BSplineCurve PolesCount=3 KnotsCount=2 Degree=2 IsPeriodic=0
    g19: GeomPoint X=-6.2215 Y=-2 Z=0
    g20: GeomPoint X=-6.32538 Y=-4 Z=0
    g21: Circle CenterX=-6.48644 CenterY=-5.99526 CenterZ=0 NormalX=0 NormalY=0 NormalZ=1 AngleXU=0 Radius=1
    g22: Circle CenterX=-6.58486 CenterY=-6.99526 CenterZ=0 NormalX=0 NormalY=0 NormalZ=1 AngleXU=0 Radius=1
    g23: Circle CenterX=-6.77343 CenterY=-8 CenterZ=0 NormalX=0 NormalY=0 NormalZ=1 AngleXU=0 Radius=1
    g24: BSplineCurve PolesCount=3 KnotsCount=2 Degree=2 IsPeriodic=0
    g25: GeomPoint X=-6.48644 Y=-5.99526 Z=0
    g26: GeomPoint X=-6.77343 Y=-8 Z=0
    g27: Circle CenterX=-7.19003 CenterY=-10 CenterZ=0 NormalX=0 NormalY=0 NormalZ=1 AngleXU=0 Radius=1
    g28: Circle CenterX=-7.44407 CenterY=-11.0915 CenterZ=0 NormalX=0 NormalY=0 NormalZ=1 AngleXU=0 Radius=1
    g29: Circle CenterX=-7.79258 CenterY=-12 CenterZ=0 NormalX=0 NormalY=0 NormalZ=1 AngleXU=0 Radius=1
    g30: BSplineCurve PolesCount=3 KnotsCount=2 Degree=2 IsPeriodic=0
    g31: GeomPoint X=-7.19003 Y=-10 Z=0
    g32: GeomPoint X=-7.79258 Y=-12 Z=0
    g33: Circle CenterX=-8.70761 CenterY=-14 CenterZ=0 NormalX=0 NormalY=0 NormalZ=1 AngleXU=0 Radius=1
    g34: Circle CenterX=-9.33087 CenterY=-15.1837 CenterZ=0 NormalX=0 NormalY=0 NormalZ=1 AngleXU=0 Radius=1
    g35: Circle CenterX=-10.1571 CenterY=-16 CenterZ=0 NormalX=0 NormalY=0 NormalZ=1 AngleXU=0 Radius=1
    g36: BSplineCurve PolesCount=3 KnotsCount=2 Degree=2 IsPeriodic=0
    g37: GeomPoint X=-8.70761 Y=-14 Z=0
    g38: GeomPoint X=-10.1571 Y=-16 Z=0
    g39: Circle CenterX=-12.8401 CenterY=-17.6958 CenterZ=0 NormalX=0 NormalY=0 NormalZ=1 AngleXU=0 Radius=1
    g40: Circle CenterX=-13.3521 CenterY=-17.9027 CenterZ=0 NormalX=0 NormalY=0 NormalZ=1 AngleXU=0 Radius=1
    g41: Circle CenterX=-14 CenterY=-18 CenterZ=0 NormalX=0 NormalY=0 NormalZ=1 AngleXU=0 Radius=1
    g42: BSplineCurve PolesCount=3 KnotsCount=2 Degree=2 IsPeriodic=0
    g43: GeomPoint X=-12.8401 Y=-17.6958 Z=0
    g44: GeomPoint X=-14 Y=-18 Z=0
    g45: LineSegment StartX=-6.2 StartY=0 StartZ=0 EndX=-7.2 EndY=0 EndZ=0
    g46: LineSegment StartX=-7.2 StartY=0 StartZ=0 EndX=-7.2 EndY=-2 EndZ=0
    g47: LineSegment StartX=-7.2 StartY=-2 StartZ=0 EndX=-6.2215 EndY=-2 EndZ=0
    g48: LineSegment StartX=-6.32538 StartY=-4 StartZ=0 EndX=-7.65538 EndY=-4 EndZ=0
    g49: LineSegment StartX=-7.65538 StartY=-4 StartZ=0 EndX=-7.65538 EndY=-5.99526 EndZ=0
    g50: LineSegment StartX=-7.65538 StartY=-5.99526 StartZ=0 EndX=-6.48644 EndY=-5.99526 EndZ=0
    g51: LineSegment StartX=-6.77343 StartY=-8 StartZ=0 EndX=-8.43343 EndY=-8 EndZ=0
    g52: LineSegment StartX=-8.43343 StartY=-8 StartZ=0 EndX=-8.43343 EndY=-10 EndZ=0
    g53: LineSegment StartX=-8.43343 StartY=-10 StartZ=0 EndX=-7.19003 EndY=-10 EndZ=0
  constraints (112):
    c: Horizontal(g0)
    c: Distance(g0) = 2
    c: Block(g0)
    c: Vertical(g1)
    c: Coincident(g2,g0)
    c: Vertical(g2)
    c: Block(g2)
    c: Coincident(g6,g2)
    c: Weight(g3) = 1
    c: Equal(g3,g4)
    c: Equal(g3,g5)
    c: InternalAlignment(g3,g6)
    c: InternalAlignment(g4,g6)
    c: InternalAlignment(g5,g6)
    c: InternalAlignment(g7,g6)
    c: InternalAlignment(g8,g6)
    c: Block(g6)
    c: Coincident(g9,g1)
    c: Coincident(g9,g6)
    c: Horizontal(g9)
    c: Vertical(g10)
    c: Block(g10)
    c: Horizontal(g11)
    c: Block(g11)
    c: Coincident(g12,g10)
    c: Horizontal(g12)
    c: Block(g12)
    c: Coincident(g13,g11)
    c: Vertical(g13)
    c: Block(g13)
    c: Coincident(g14,g10)
    c: Horizontal(g14)
    c: Block(g14)
    c: Block(g9)
    c: Block(g1)
    c: Weight(g15) = 1
    c: Equal(g15,g16)
    c: Equal(g15,g17)
    c: InternalAlignment(g15,g18)
    c: InternalAlignment(g16,g18)
    c: InternalAlignment(g17,g18)
    c: InternalAlignment(g19,g18)
    c: InternalAlignment(g20,g18)
    c: Weight(g21) = 1
    c: Equal(g21,g22)
    c: Equal(g21,g23)
    c: InternalAlignment(g21,g24)
    c: InternalAlignment(g22,g24)
    c: InternalAlignment(g23,g24)
    c: InternalAlignment(g25,g24)
    c: InternalAlignment(g26,g24)
    c: Weight(g27) = 1
    c: Equal(g27,g28)
    c: Equal(g27,g29)
    c: Coincident(g30,g14)
    c: InternalAlignment(g27,g30)
    c: InternalAlignment(g28,g30)
    c: InternalAlignment(g29,g30)
    c: InternalAlignment(g31,g30)
    c: InternalAlignment(g32,g30)
    c: Coincident(g36,g12)
    c: Weight(g33) = 1
    c: Equal(g33,g34)
    c: Equal(g33,g35)
    c: Coincident(g36,g11)
    c: InternalAlignment(g33,g36)
    c: InternalAlignment(g34,g36)
    c: InternalAlignment(g35,g36)
    c: InternalAlignment(g37,g36)
    c: InternalAlignment(g38,g36)
    c: Coincident(g42,g13)
    c: Weight(g39) = 1
    c: Equal(g39,g40)
    c: Equal(g39,g41)
    c: Coincident(g42,g1)
    c: InternalAlignment(g39,g42)
    c: InternalAlignment(g40,g42)
    c: InternalAlignment(g41,g42)
    c: InternalAlignment(g43,g42)
    c: InternalAlignment(g44,g42)
    c: Block(g18)
    c: Block(g24)
    c: Block(g30)
    c: Block(g36)
    c: Block(g42)
    c: Horizontal(g45)
    c: Coincident(g45,g0)
    c: Vertical(g46)
    c: Coincident(g46,g45)
    c: Coincident(g47,g46)
    c: Coincident(g47,g18)
    c: Horizontal(g47)
    c: Block(g46)
    c: Coincident(g48,g18)
    c: Horizontal(g48)
    c: Distance(g48) = 1.33
    c: Vertical(g49)
    c: Coincident(g49,g48)
    c: Coincident(g50,g49)
    c: Coincident(g50,g24)
    c: Horizontal(g50)
    c: Tangent(g50,g22)
    c: Horizontal(g51)
    c: Coincident(g51,g24)
    c: Block(g51)
    c: Vertical(g52)
    c: Block(g52)
    c: Coincident(g52,g51)
    c: Coincident(g53,g52)
    c: Coincident(g53,g30)
    c: Horizontal(g53)
    c: Distance(g1) = 8.5
FEATURE [Part::Feature] Face024
  shape: bbox 9.8 x 26.5 x 2e-07 mm, 1 faces, 0 solids (baked)
FEATURE [Part::Revolution] Revolve024
  Angle = 360
  Axis = (0,1,0)
  Base = (0,0,0)
  FaceMakerClass = Part::FaceMakerBullseye
  Placement = pos=(0,0,0) rot=(0,0,1;1.5708rad)
  Solid = false
  Source = -> Face024
  Symmetric = false
FEATURE [Part::Feature] Face025
  shape: bbox 9.8 x 26.5 x 2e-07 mm, 1 faces, 0 solids (baked)
FEATURE [Part::Revolution] Revolve025
  Angle = 360
  Axis = (0,1,0)
  Base = (0,0,0)
  FaceMakerClass = Part::FaceMakerBullseye
  Placement = pos=(0,0,0) rot=(0,0,1;1.5708rad)
  Solid = false
  Source = -> Face025
  Symmetric = false
FEATURE [Part::MultiFuse] Fusion033
  Placement = pos=(-18,19,36) rot=(0,0,1;0rad)
  Shapes = -> [Revolve025,Revolve024]
FEATURE [Part::Cylinder] Cylinder014
  Angle = 360
  AttacherType = Attacher::AttachEngine3D
  Height = 20
  Placement = pos=(0,0,36.15) rot=(0,0,1;0rad)
  Radius = 14.3
FEATURE [Part::Cylinder] Cylinder015
  Angle = 360
  AttacherType = Attacher::AttachEngine3D
  Height = 10
  Placement = pos=(0,0,36.15) rot=(0,0,1;0rad)
  Radius = 4
FEATURE [Part::MultiFuse] Fusion034  label="removeToCreteHoleForPlugHousing004"
  Placement = pos=(-42,19,36) rot=(0,1,0;1.5708rad)
  Shapes = -> [Cylinder014,Cylinder015]
FEATURE [Part::Cut] Cut008  label="top004"
  Base = -> Cut004
  Placement = pos=(-1,0,0) rot=(0,0,1;0rad)
  Tool = -> Fusion034
FEATURE [Part::Box] Box005  label="Cube005"
  AttacherType = Attacher::AttachEngine3D
  Height = 28
  Length = 3
  Placement = pos=(110.7,19,22) rot=(0,0,1;0rad)
  Width = 15.7
FEATURE [Part::Cylinder] Cylinder016
  Angle = 360
  AttacherType = Attacher::AttachEngine3D
  Height = 10
  Placement = pos=(0,0,36.15) rot=(0,0,1;0rad)
  Radius = 4
FEATURE [Part::Cylinder] Cylinder017
  Angle = 360
  AttacherType = Attacher::AttachEngine3D
  Height = 20
  Placement = pos=(0,0,36.15) rot=(0,0,1;0rad)
  Radius = 10.3
FEATURE [Part::MultiFuse] Fusion035  label="removeToCreteHoleForPlugHousing005"
  Placement = pos=(70,19,36) rot=(0,1,0;1.5708rad)
  Shapes = -> [Cylinder017,Cylinder016]
FEATURE [Part::Cut] Cut009  label="plugHousingTab001"
  Base = -> Box005
  Placement = pos=(-107.4,-14,0) rot=(0,0,1;0rad)
  Tool = -> Fusion035
FEATURE [Part::Box] Box006  label="Cube006"
  AttacherType = Attacher::AttachEngine3D
  Height = 28
  Length = 3
  Placement = pos=(110.7,19,22) rot=(0,0,1;0rad)
  Width = 15.7
FEATURE [Part::Cylinder] Cylinder018
  Angle = 360
  AttacherType = Attacher::AttachEngine3D
  Height = 10
  Placement = pos=(0,0,36.15) rot=(0,0,1;0rad)
  Radius = 4
FEATURE [Part::Cylinder] Cylinder019
  Angle = 360
  AttacherType = Attacher::AttachEngine3D
  Height = 20
  Placement = pos=(0,0,36.15) rot=(0,0,1;0rad)
  Radius = 10.3
FEATURE [Part::MultiFuse] Fusion036  label="removeToCreteHoleForPlugHousing006"
  Placement = pos=(70,19,36) rot=(0,1,0;1.5708rad)
  Shapes = -> [Cylinder019,Cylinder018]
FEATURE [Part::Cut] Cut010  label="plugHousingTab002"
  Base = -> Box006
  Placement = pos=(-107.4,-14,0) rot=(0,0,1;0rad)
  Tool = -> Fusion036
FEATURE [Part::MultiFuse] Fusion037
  Placement = pos=(9.6,23,0) rot=(0,0,1;3.14159rad)
  Shapes = -> [Cut009,Cut010]
FEATURE [Part::Box] Box  label="Cube"
  AttacherType = Attacher::AttachEngine3D
  Height = 10
  Length = 3
  Placement = pos=(3.3,4,12) rot=(0,0,1;0rad)
  Width = 10
FEATURE [Part::Fillet] Fillet004
  Base = -> Fusion028
  Edges = 1 edges r=2: [Edge25]
FEATURE [Part::Fillet] Fillet005  label="plugHousing046"
  Base = -> Fillet004
  Edges = 1 edges r=2: [Edge8]
FEATURE [Part::Fillet] Fillet006
  Base = -> Box
  Edges = 1 edges r=2: [Edge11]
FEATURE [Part::Box] Box007  label="Cube007"
  AttacherType = Attacher::AttachEngine3D
  Height = 10
  Length = 3
  Placement = pos=(3.3,4,50) rot=(0,0,1;0rad)
  Width = 10
FEATURE [Part::Fillet] Fillet007
  Base = -> Box007
  Edges = 1 edges r=2: [Edge12]
FEATURE [Part::Box] Box008  label="Cube008"
  AttacherType = Attacher::AttachEngine3D
  Height = 28
  Length = 4
  Placement = pos=(5,0,22) rot=(0,0,1;0rad)
  Width = 10
FEATURE [Part::Fillet] Fillet008
  Base = -> Box008
  Edges = 1 edges r=1: [Edge7]
FEATURE [Part::Fillet] Fillet009
  Base = -> Fillet008
  Edges = 1 edges r=2: [Edge5]
FEATURE [Part::Fillet] Fillet010
  Base = -> Fillet009
  Edges = 1 edges r=2: [Edge2]
FEATURE [Sketcher::SketchObject] Sketch009  label="topSketch003"
  FullyConstrained = true
  sketch-geometry (4):
    g0: LineSegment StartX=16.8446 StartY=31.512 StartZ=0 EndX=16.3251 EndY=34.4666 EndZ=0
    g1: ArcOfCircle CenterX=19 CenterY=19.2524 CenterZ=0 NormalX=0 NormalY=0 NormalZ=1 AngleXU=0 Radius=15.4476 StartAngle=1.74483 EndAngle=2.72717
    g2: ArcOfCircle CenterX=19 CenterY=19.2524 CenterZ=0 NormalX=0 NormalY=0 NormalZ=1 AngleXU=0 Radius=12.4476 StartAngle=1.74483 EndAngle=2.73189
    g3: LineSegment StartX=4.86004 StartY=25.4725 StartZ=0 EndX=7.58253 EndY=24.2107 EndZ=0
  constraints (7):
    c: Block(g0)
    c: Coincident(g1,g0)
    c: Coincident(g2,g0)
    c: Coincident(g3,g1)
    c: Coincident(g3,g2)
    c: Block(g1)
    c: Block(g2)
FEATURE [Part::Extrusion] Extrude008
  Base = -> Sketch009
  Dir = (0,0,1)
  DirMode = 2
  FaceMakerClass = Part::FaceMakerBullseye
  LengthFwd = 10
  LengthRev = 0
  Placement = pos=(0,0,31) rot=(0,0,1;0rad)
  Solid = true
  Symmetric = false
FEATURE [Part::Cylinder] Cylinder020
  Angle = 360
  AttacherType = Attacher::AttachEngine3D
  Height = 20
  Placement = pos=(0,0,36.15) rot=(0,0,1;0rad)
  Radius = 8.2
FEATURE [Part::Cylinder] Cylinder021
  Angle = 360
  AttacherType = Attacher::AttachEngine3D
  Height = 10
  Placement = pos=(0,0,36.15) rot=(0,0,1;0rad)
  Radius = 4
FEATURE [Part::MultiFuse] Fusion038  label="removeToCreteHoleForPlugHousing007"
  Placement = pos=(-42,19,36) rot=(0,1,0;1.5708rad)
  Shapes = -> [Cylinder020,Cylinder021]
FEATURE [Part::Cut] Cut011
  Base = -> Extrude008
  Tool = -> Fusion038
FEATURE [Part::Fillet] Fillet011
  Base = -> Cut011
  Edges = 1 edges r=2: [Edge1]
FEATURE [Part::Fillet] Fillet012
  Base = -> Fillet011
  Edges = 1 edges r=2.5: [Edge1]
FEATURE [Part::Fillet] Fillet013
  Base = -> Fillet012
  Edges = 1 edges r=2.5: [Edge2]
FEATURE [Part::Box] Box010  label="Cube010"
  AttacherType = Attacher::AttachEngine3D
  Height = 16
  Length = 8
  Placement = pos=(12.7,31.52,28) rot=(0,0,1;0rad)
  Width = 4
FEATURE [Sketcher::SketchObject] Sketch010  label="topSketch004"
  FullyConstrained = true
  sketch-geometry (4):
    g0: LineSegment StartX=16.8446 StartY=31.512 StartZ=0 EndX=16.3251 EndY=34.4666 EndZ=0
    g1: ArcOfCircle CenterX=19 CenterY=19.2524 CenterZ=0 NormalX=0 NormalY=0 NormalZ=1 AngleXU=0 Radius=15.4476 StartAngle=1.74483 EndAngle=2.72717
    g2: ArcOfCircle CenterX=19 CenterY=19.2524 CenterZ=0 NormalX=0 NormalY=0 NormalZ=1 AngleXU=0 Radius=12.4476 StartAngle=1.74483 EndAngle=2.73189
    g3: LineSegment StartX=4.86004 StartY=25.4725 StartZ=0 EndX=7.58253 EndY=24.2107 EndZ=0
  constraints (7):
    c: Block(g0)
    c: Coincident(g1,g0)
    c: Coincident(g2,g0)
    c: Coincident(g3,g1)
    c: Coincident(g3,g2)
    c: Block(g1)
    c: Block(g2)
FEATURE [Part::Cylinder] Cylinder022
  Angle = 360
  AttacherType = Attacher::AttachEngine3D
  Height = 10
  Placement = pos=(0,0,36.15) rot=(0,0,1;0rad)
  Radius = 4
FEATURE [Sketcher::SketchObject] Sketch011  label="topSketch005"
  FullyConstrained = true
  sketch-geometry (4):
    g0: LineSegment StartX=16.8446 StartY=31.512 StartZ=0 EndX=16.3251 EndY=34.4666 EndZ=0
    g1: ArcOfCircle CenterX=19 CenterY=19.2524 CenterZ=0 NormalX=0 NormalY=0 NormalZ=1 AngleXU=0 Radius=15.4476 StartAngle=1.74483 EndAngle=2.72717
    g2: ArcOfCircle CenterX=19 CenterY=19.2524 CenterZ=0 NormalX=0 NormalY=0 NormalZ=1 AngleXU=0 Radius=12.4476 StartAngle=1.74483 EndAngle=2.73189
    g3: LineSegment StartX=4.86004 StartY=25.4725 StartZ=0 EndX=7.58253 EndY=24.2107 EndZ=0
  constraints (7):
    c: Block(g0)
    c: Coincident(g1,g0)
    c: Coincident(g2,g0)
    c: Coincident(g3,g1)
    c: Coincident(g3,g2)
    c: Block(g1)
    c: Block(g2)
FEATURE [Part::Extrusion] Extrude010
  Base = -> Sketch011
  Dir = (0,0,1)
  DirMode = 2
  FaceMakerClass = Part::FaceMakerBullseye
  LengthFwd = 10.6
  LengthRev = 0
  Placement = pos=(0,0,31) rot=(0,0,1;0rad)
  Solid = true
  Symmetric = false
FEATURE [Part::Cylinder] Cylinder023
  Angle = 360
  AttacherType = Attacher::AttachEngine3D
  Height = 20
  Placement = pos=(0,0,36.15) rot=(0,0,1;0rad)
  Radius = 8.2
FEATURE [Part::MultiFuse] Fusion039  label="removeToCreteHoleForPlugHousing008"
  Placement = pos=(-42,19,36) rot=(0,1,0;1.5708rad)
  Shapes = -> [Cylinder023,Cylinder022]
FEATURE [Part::Cut] Cut012
  Base = -> Extrude010
  Placement = pos=(0,0,-0.3) rot=(0,0,1;0rad)
  Tool = -> Fusion039
FEATURE [Part::Cut] Cut013
  Base = -> Box010
  Tool = -> Cut012
FEATURE [Part::Fillet] Fillet014
  Base = -> Cut013
  Edges = 1 edges r=0.7: [Edge13]
FEATURE [Part::Fillet] Fillet015
  Base = -> Fillet014
  Edges = 1 edges r=0.7: [Edge13]
FEATURE [Part::Fillet] Fillet016
  Base = -> Fillet015
  Edges = 1 edges r=0.7: [Edge16]
FEATURE [Part::Fillet] Fillet017
  Base = -> Fillet016
  Edges = 1 edges r=0.7: [Edge11]
FEATURE [Part::Fillet] Fillet018
  Base = -> Fillet017
  Edges = 1 edges r=0.7: [Edge10]
FEATURE [Part::Fillet] Fillet019
  Base = -> Fillet018
  Edges = 1 edges r=1.2: [Edge5]
FEATURE [Part::Fillet] Fillet020
  Base = -> Fillet019
  Edges = 1 edges r=1.2: [Edge12]
FEATURE [Part::Fillet] Fillet021
  Base = -> Fillet020
  Edges = 1 edges r=2: [Edge1]
  Placement = pos=(0.3,0,0) rot=(0,0,1;0rad)
FEATURE [Part::MultiFuse] Fusion040  label="top005"
  Shapes = -> [Cut008,Fillet021]
FEATURE [Part::MultiFuse] Fusion041  label="wireHolder"
  Shapes = -> [Fusion033,Fillet013]
FEATURE [Part::MultiFuse] Fusion042
  Shapes = -> [Fillet007,Fusion041]
FEATURE [Part::MultiFuse] Fusion043  label="wireHolder001"
  Shapes = -> [Fusion042,Fillet010]
FEATURE [Part::MultiFuse] Fusion044  label="wireHolder002"
  Shapes = -> [Fillet006,Fusion037,Fusion043]
FEATURE [Part::Feature] Face026
  shape: bbox 11 x 6 x 2e-07 mm, 1 faces, 0 solids (baked)
FEATURE [Part::Revolution] Revolve026
  Angle = 360
  Axis = (0,1,0)
  Base = (0,0,0)
  FaceMakerClass = Part::FaceMakerBullseye
  Placement = pos=(30.3,-1,19.7) rot=(0,0,1;0rad)
  Solid = false
  Source = -> Face026
  Symmetric = false
FEATURE [Sketcher::SketchObject] Sketch013  label="topSketch006"
  FullyConstrained = true
  sketch-geometry (13):
    g0: LineSegment StartX=117 StartY=19 StartZ=0 EndX=117 EndY=38 EndZ=0
    g1: ArcOfCircle CenterX=98 CenterY=19 CenterZ=0 NormalX=0 NormalY=0 NormalZ=1 AngleXU=0 Radius=19 StartAngle=5.7297 EndAngle=6.28319
    g2: LineSegment StartX=0 StartY=3 StartZ=0 EndX=0 EndY=19 EndZ=0
    g3: LineSegment StartX=19 StartY=38 StartZ=0 EndX=117 EndY=38 EndZ=0
    g4: ArcOfCircle CenterX=19 CenterY=19 CenterZ=0 NormalX=0 NormalY=0 NormalZ=1 AngleXU=0 Radius=19 StartAngle=1.5708 EndAngle=3.14159
    g5: ArcOfCircle CenterX=19 CenterY=19 CenterZ=0 NormalX=0 NormalY=0 NormalZ=1 AngleXU=0 Radius=16 StartAngle=1.5708 EndAngle=3.14159
    g6: ArcOfCircle CenterX=98 CenterY=19 CenterZ=0 NormalX=0 NormalY=0 NormalZ=1 AngleXU=0 Radius=16 StartAngle=5.60905 EndAngle=6.28319
    g7: LineSegment StartX=114 StartY=19 StartZ=0 EndX=114 EndY=35 EndZ=0
    g8: LineSegment StartX=110.5 StartY=9.01251 StartZ=0 EndX=114.163 EndY=9.01251 EndZ=0
    g9: LineSegment StartX=114 StartY=35 StartZ=0 EndX=19 EndY=35 EndZ=0
    g10: LineSegment StartX=0 StartY=3 StartZ=0 EndX=0 EndY=0 EndZ=0
    g11: LineSegment StartX=3 StartY=0 StartZ=0 EndX=0 EndY=0 EndZ=0
    g12: LineSegment StartX=3 StartY=19 StartZ=0 EndX=3 EndY=0 EndZ=0
  constraints (33):
    c: Vertical(g0)
    c: Distance(g0) = 19
    c: Block(g0)
    c: Coincident(g1,g0)
    c: Block(g1)
    c: Vertical(g2)
    c: Block(g2)
    c: Coincident(g3,g0)
    c: Horizontal(g3)
    c: Distance(g3) = 98
    c: Coincident(g4,g3)
    c: Coincident(g4,g2)
    c: Block(g4)
    c: Coincident(g5,g4)
    c: Coincident(g6,g1)
    c: Block(g6)
    c: Block(g5)
    c: Coincident(g7,g6)
    c: Vertical(g7)
    c: Coincident(g8,g6)
    c: Coincident(g8,g1)
    c: Coincident(g9,g7)
    c: Coincident(g9,g5)
    c: Horizontal(g9)
    c: Tangent(g9,g5)
    c: Coincident(g10,g2)
    c: Distance(g10) = 3
    c: Vertical(g10)
    c: Coincident(g11,g10)
    c: Horizontal(g11)
    c: Coincident(g12,g5)
    c: Coincident(g12,g11)
    c: Vertical(g12)
FEATURE [Part::Extrusion] Extrude011  label="top006"
  Base = -> Sketch013
  Dir = (0,0,1)
  DirMode = 2
  FaceMakerClass = Part::FaceMakerBullseye
  LengthFwd = 72
  LengthRev = 0
  Solid = true
  Symmetric = false
FEATURE [Sketcher::SketchObject] Sketch014
  FullyConstrained = true
  MapMode = 3
  Placement = pos=(0,0,0) rot=(1,0,0;1.5708rad)
  Support = -> [Extrude011]
  sketch-geometry (8):
    g0: Circle CenterX=80.351 CenterY=-67.6202 CenterZ=0 NormalX=0 NormalY=0 NormalZ=1 AngleXU=0 Radius=2
    g1: Circle CenterX=80.351 CenterY=-67.6202 CenterZ=0 NormalX=0 NormalY=0 NormalZ=1 AngleXU=0 Radius=3
    g2: Circle CenterX=80.351 CenterY=-4.92017 CenterZ=0 NormalX=0 NormalY=0 NormalZ=1 AngleXU=0 Radius=2
    g3: Circle CenterX=80.351 CenterY=-4.92017 CenterZ=0 NormalX=0 NormalY=0 NormalZ=1 AngleXU=0 Radius=3
    g4: Circle CenterX=23.851 CenterY=-4.92017 CenterZ=0 NormalX=0 NormalY=0 NormalZ=1 AngleXU=0 Radius=2
    g5: Circle CenterX=23.851 CenterY=-4.92017 CenterZ=0 NormalX=0 NormalY=0 NormalZ=1 AngleXU=0 Radius=3
    g6: Circle CenterX=23.851 CenterY=-67.6202 CenterZ=0 NormalX=0 NormalY=0 NormalZ=1 AngleXU=0 Radius=2
    g7: Circle CenterX=23.851 CenterY=-67.6202 CenterZ=0 NormalX=0 NormalY=0 NormalZ=1 AngleXU=0 Radius=3
  constraints (8):
    c: Block(g3)
    c: Block(g2)
    c: Block(g1)
    c: Block(g0)
    c: Block(g6)
    c: Block(g7)
    c: Block(g4)
    c: Block(g5)
FEATURE [Part::Feature] Face027
  shape: bbox 11 x 6 x 2e-07 mm, 1 faces, 0 solids (baked)
FEATURE [Part::Revolution] Revolve027
  Angle = 360
  Axis = (0,1,0)
  Base = (0,0,0)
  FaceMakerClass = Part::FaceMakerBullseye
  Placement = pos=(30.3,-1,51.7) rot=(0,0,1;0rad)
  Solid = false
  Source = -> Face027
  Symmetric = false
FEATURE [Part::Feature] Face028
  shape: bbox 11 x 6 x 2e-07 mm, 1 faces, 0 solids (baked)
FEATURE [Part::Revolution] Revolve028
  Angle = 360
  Axis = (0,1,0)
  Base = (0,0,0)
  FaceMakerClass = Part::FaceMakerBullseye
  Placement = pos=(62.3,-1,19.7) rot=(0,0,1;0rad)
  Solid = false
  Source = -> Face028
  Symmetric = false
FEATURE [Part::Feature] Face029
  shape: bbox 11 x 6 x 2e-07 mm, 1 faces, 0 solids (baked)
FEATURE [Part::Revolution] Revolve029
  Angle = 360
  Axis = (0,1,0)
  Base = (0,0,0)
  FaceMakerClass = Part::FaceMakerBullseye
  Placement = pos=(62.3,-1,51.7) rot=(0,0,1;0rad)
  Solid = false
  Source = -> Face029
  Symmetric = false
FEATURE [Part::Feature] Wire
  shape: bbox 11 x 5.2 x 2e-07 mm, 0 faces, 0 solids (baked)
FEATURE [Part::Revolution] Revolve030
  Angle = 360
  Axis = (0,1,0)
  Base = (0,0,0)
  FaceMakerClass = Part::FaceMakerBullseye
  Placement = pos=(30.3,38,19.7) rot=(0,0,1;0rad)
  Solid = true
  Source = -> Wire
  Symmetric = false
FEATURE [Part::Feature] Wire001
  shape: bbox 11 x 5.2 x 2e-07 mm, 0 faces, 0 solids (baked)
FEATURE [Part::Revolution] Revolve031
  Angle = 360
  Axis = (0,1,0)
  Base = (0,0,0)
  FaceMakerClass = Part::FaceMakerBullseye
  Placement = pos=(30.3,38,51.7) rot=(0,0,1;0rad)
  Solid = true
  Source = -> Wire001
  Symmetric = false
FEATURE [Part::Feature] Wire002
  shape: bbox 11 x 5.2 x 2e-07 mm, 0 faces, 0 solids (baked)
FEATURE [Part::Revolution] Revolve032
  Angle = 360
  Axis = (0,1,0)
  Base = (0,0,0)
  FaceMakerClass = Part::FaceMakerBullseye
  Placement = pos=(62.3,38,51.7) rot=(0,0,1;0rad)
  Solid = true
  Source = -> Wire002
  Symmetric = false
FEATURE [Part::Feature] Wire003
  shape: bbox 11 x 5.2 x 2e-07 mm, 0 faces, 0 solids (baked)
FEATURE [Part::Revolution] Revolve033
  Angle = 360
  Axis = (0,1,0)
  Base = (0,0,0)
  FaceMakerClass = Part::FaceMakerBullseye
  Placement = pos=(62.3,38,19.7) rot=(0,0,1;0rad)
  Solid = true
  Source = -> Wire003
  Symmetric = false
FEATURE [Part::MultiFuse] Fusion045  label="altRandScrewHousing"
  Shapes = -> [Revolve029,Revolve027,Revolve028,Revolve026]
FEATURE [Part::MultiFuse] Fusion046  label="fanScrewHousing"
  Shapes = -> [Revolve033,Revolve032,Revolve031,Revolve030]
FEATURE [Sketcher::SketchObject] Sketch015
  FullyConstrained = true
  sketch-geometry (17):
    g0: Circle CenterX=-3.5 CenterY=23.5 CenterZ=0 NormalX=0 NormalY=0 NormalZ=1 AngleXU=0 Radius=1
    g1: Circle CenterX=-1 CenterY=15.25 CenterZ=0 NormalX=0 NormalY=0 NormalZ=1 AngleXU=0 Radius=1
    g2: Circle CenterX=-3.5 CenterY=7 CenterZ=0 NormalX=0 NormalY=0 NormalZ=1 AngleXU=0 Radius=1
    g3: BSplineCurve PolesCount=3 KnotsCount=2 Degree=2 IsPeriodic=0
    g4: GeomPoint X=-3.5 Y=23.5 Z=0
    g5: GeomPoint X=-3.5 Y=7 Z=0
    g6: Circle CenterX=-4.8 CenterY=30.5 CenterZ=0 NormalX=0 NormalY=0 NormalZ=1 AngleXU=0 Radius=1
    g7: Circle CenterX=-3.5 CenterY=30.5 CenterZ=0 NormalX=0 NormalY=0 NormalZ=1 AngleXU=0 Radius=1
    g8: Circle CenterX=-3.5 CenterY=29.2 CenterZ=0 NormalX=0 NormalY=0 NormalZ=1 AngleXU=0 Radius=1
    g9: BSplineCurve PolesCount=3 KnotsCount=2 Degree=2 IsPeriodic=0
    g10: GeomPoint X=-4.8 Y=30.5 Z=0
    g11: GeomPoint X=-3.5 Y=29.2 Z=0
    g12: LineSegment StartX=-3.5 StartY=29.2 StartZ=0 EndX=-3.5 EndY=23.5 EndZ=0
    g13: LineSegment StartX=-4.8 StartY=30.5 StartZ=0 EndX=0 EndY=30.5 EndZ=0
    g14: LineSegment StartX=-3.5 StartY=0.3 StartZ=0 EndX=0 EndY=0.3 EndZ=0
    g15: LineSegment StartX=-3.5 StartY=0.3 StartZ=0 EndX=-3.5 EndY=7 EndZ=0
    g16: LineSegment StartX=0 StartY=0.3 StartZ=0 EndX=0 EndY=30.5 EndZ=0
  constraints (33):
    c: Weight(g0) = 1
    c: Equal(g0,g1)
    c: Equal(g0,g2)
    c: InternalAlignment(g0,g3)
    c: InternalAlignment(g1,g3)
    c: InternalAlignment(g2,g3)
    c: InternalAlignment(g4,g3)
    c: InternalAlignment(g5,g3)
    c: Block(g3)
    c: Weight(g6) = 1
    c: Equal(g6,g7)
    c: Equal(g6,g8)
    c: InternalAlignment(g6,g9)
    c: InternalAlignment(g7,g9)
    c: InternalAlignment(g8,g9)
    c: InternalAlignment(g10,g9)
    c: InternalAlignment(g11,g9)
    c: Block(g9)
    c: Coincident(g12,g9)
    c: Coincident(g12,g3)
    c: Vertical(g12)
    c: Coincident(g13,g9)
    c: Horizontal(g13)
    c: Distance(g13) = 4.8
    c: Horizontal(g14)
    c: Block(g14)
    c: Coincident(g15,g14)
    c: Coincident(g15,g3)
    c: Vertical(g15)
    c: Coincident(g16,g14)
    c: Coincident(g16,g13)
    c: Vertical(g16)
    c: Tangent(g16,g1)
FEATURE [Sketcher::SketchObject] Sketch016
  FullyConstrained = true
  sketch-geometry (16):
    g0: Circle CenterX=-3.5 CenterY=23.5 CenterZ=0 NormalX=0 NormalY=0 NormalZ=1 AngleXU=0 Radius=1
    g1: Circle CenterX=-1 CenterY=15.25 CenterZ=0 NormalX=0 NormalY=0 NormalZ=1 AngleXU=0 Radius=1
    g2: Circle CenterX=-3.5 CenterY=7 CenterZ=0 NormalX=0 NormalY=0 NormalZ=1 AngleXU=0 Radius=1
    g3: BSplineCurve PolesCount=3 KnotsCount=2 Degree=2 IsPeriodic=0
    g4: GeomPoint X=-3.5 Y=23.5 Z=0
    g5: GeomPoint X=-3.5 Y=7 Z=0
    g6: LineSegment StartX=-3.5 StartY=28.2 StartZ=0 EndX=-3.5 EndY=23.5 EndZ=0
    g7: LineSegment StartX=0 StartY=29.5 StartZ=0 EndX=0 EndY=30 EndZ=0
    g8: LineSegment StartX=-3.5 StartY=28.2 StartZ=0 EndX=-3.5 EndY=30 EndZ=0
    g9: LineSegment StartX=0 StartY=30 StartZ=0 EndX=0 EndY=30.5 EndZ=0
    g10: LineSegment StartX=0 StartY=30.5 StartZ=0 EndX=-3.5 EndY=30.5 EndZ=0
    g11: LineSegment StartX=-3.5 StartY=30.5 StartZ=0 EndX=-3.5 EndY=30 EndZ=0
    g12: LineSegment StartX=0 StartY=29.5 StartZ=0 EndX=0 EndY=5 EndZ=0
    g13: LineSegment StartX=-3.5 StartY=0.3 StartZ=0 EndX=-3.5 EndY=7 EndZ=0
    g14: LineSegment StartX=-3.5 StartY=0.3 StartZ=0 EndX=0 EndY=0.3 EndZ=0
    g15: LineSegment StartX=0 StartY=5 StartZ=0 EndX=0 EndY=0.3 EndZ=0
  constraints (39):
    c: Weight(g0) = 1
    c: Equal(g0,g1)
    c: Equal(g0,g2)
    c: InternalAlignment(g0,g3)
    c: InternalAlignment(g1,g3)
    c: InternalAlignment(g2,g3)
    c: InternalAlignment(g4,g3)
    c: InternalAlignment(g5,g3)
    c: Block(g3)
    c: Coincident(g6,g3)
    c: Vertical(g6)
    c: Vertical(g7)
    c: Distance(g7) = 0.5
    c: Coincident(g8,g6)
    c: Vertical(g8)
    c: Block(g6)
    c: Block(g7)
    c: Vertical(g9)
    c: Equal(g7,g9) = 0.5
    c: Block(g9)
    c: Coincident(g9,g7)
    c: Horizontal(g10)
    c: Coincident(g10,g9)
    c: Coincident(g11,g10)
    c: Coincident(g11,g8)
    c: Vertical(g11)
    c: Block(g11)
    c: Coincident(g12,g7)
    c: Vertical(g12)
    c: Coincident(g13,g3)
    c: Vertical(g13)
    c: Distance(g13) = 6.7
    c: Coincident(g14,g13)
    c: Horizontal(g14)
    c: Block(g14)
    c: Coincident(g15,g12)
    c: Coincident(g15,g14)
    c: Vertical(g15)
    c: Block(g15)
FEATURE [Sketcher::SketchObject] Sketch017
  FullyConstrained = true
  sketch-geometry (11):
    g0: LineSegment StartX=-3.5 StartY=1e-16 StartZ=0 EndX=-1.6 EndY=1e-16 EndZ=0
    g1: LineSegment StartX=-1.6 StartY=1e-16 StartZ=0 EndX=-1.6 EndY=1.5 EndZ=0
    g2: LineSegment StartX=-3.5 StartY=1.5 StartZ=0 EndX=-1.6 EndY=1.5 EndZ=0
    g3: LineSegment StartX=-3.5 StartY=1e-16 StartZ=0 EndX=-4.8 EndY=1e-16 EndZ=0
    g4: Circle CenterX=-3.5 CenterY=1.3 CenterZ=0 NormalX=0 NormalY=0 NormalZ=1 AngleXU=0 Radius=1
    g5: Circle CenterX=-3.5 CenterY=1e-16 CenterZ=0 NormalX=0 NormalY=0 NormalZ=1 AngleXU=0 Radius=1
    g6: Circle CenterX=-4.8 CenterY=1e-16 CenterZ=0 NormalX=0 NormalY=0 NormalZ=1 AngleXU=0 Radius=1
    g7: BSplineCurve PolesCount=3 KnotsCount=2 Degree=2 IsPeriodic=0
    g8: GeomPoint X=-3.5 Y=1.3 Z=0
    g9: GeomPoint X=-4.8 Y=1e-16 Z=0
    g10: LineSegment StartX=-3.5 StartY=1.3 StartZ=0 EndX=-3.5 EndY=1.5 EndZ=0
  constraints (24):
    c: Horizontal(g0)
    c: Distance(g0) = 1.9
    c: Block(g0)
    c: Coincident(g1,g0)
    c: Vertical(g1)
    c: Coincident(g2,g1)
    c: Horizontal(g2)
    c: Coincident(g3,g0)
    c: Horizontal(g3)
    c: Distance(g3) = 1.3
    c: Weight(g4) = 1
    c: Equal(g4,g5)
    c: Coincident(g5,g0)
    c: Equal(g4,g6)
    c: Coincident(g7,g3)
    c: InternalAlignment(g4,g7)
    c: InternalAlignment(g5,g7)
    c: InternalAlignment(g6,g7)
    c: InternalAlignment(g8,g7)
    c: InternalAlignment(g9,g7)
    c: Coincident(g10,g7)
    c: Coincident(g10,g2)
    c: Vertical(g10)
    c: Block(g10)
FEATURE [Part::Feature] Face035
  shape: bbox 3.2 x 1.5 x 2e-07 mm, 1 faces, 0 solids (baked)
FEATURE [Part::Revolution] Revolve039  label="backCaseScrewRetainer"
  Angle = 360
  Axis = (0,1,0)
  Base = (0,0,0)
  FaceMakerClass = Part::FaceMakerBullseye
  Placement = pos=(12.5,3,62) rot=(0,0,1;0rad)
  Solid = false
  Source = -> Face035
  Symmetric = false
FEATURE [Part::Feature] Face036
  shape: bbox 3.2 x 1.5 x 2e-07 mm, 1 faces, 0 solids (baked)
FEATURE [Part::Feature] Face039
  shape: bbox 4.8 x 30.2 x 2e-07 mm, 1 faces, 0 solids (baked)
FEATURE [Part::Revolution] Revolve043  label="frontCaseScrewPost002"
  Angle = 360
  Axis = (0,1,0)
  Base = (0,0,0)
  FaceMakerClass = Part::FaceMakerBullseye
  Placement = pos=(89.5,4.5,3.5) rot=(0,0,1;0rad)
  Solid = false
  Source = -> Face039
  Symmetric = false
FEATURE [Part::Feature] Face042
  shape: bbox 4.8 x 30.2 x 2e-07 mm, 1 faces, 0 solids (baked)
FEATURE [Part::Revolution] Revolve046  label="frontCaseScrewPost003"
  Angle = 360
  Axis = (0,1,0)
  Base = (0,0,0)
  FaceMakerClass = Part::FaceMakerBullseye
  Placement = pos=(89.5,4.5,68.5) rot=(0,0,1;0rad)
  Solid = false
  Source = -> Face042
  Symmetric = false
FEATURE [Part::Feature] Face043
  shape: bbox 3.2 x 1.5 x 2e-07 mm, 1 faces, 0 solids (baked)
FEATURE [Part::Revolution] Revolve047  label="frontCaseScrewRetainer002"
  Angle = 360
  Axis = (0,1,0)
  Base = (0,0,0)
  FaceMakerClass = Part::FaceMakerBullseye
  Placement = pos=(89.5,3,68.5) rot=(0,0,1;0rad)
  Solid = false
  Source = -> Face043
  Symmetric = false
FEATURE [Part::Feature] Face044
  shape: bbox 3.2 x 1.5 x 2e-07 mm, 1 faces, 0 solids (baked)
FEATURE [Part::Revolution] Revolve048  label="frontCaseScrewRetainer003"
  Angle = 360
  Axis = (0,1,0)
  Base = (0,0,0)
  FaceMakerClass = Part::FaceMakerBullseye
  Placement = pos=(89.5,3,3.5) rot=(0,0,1;0rad)
  Solid = false
  Source = -> Face044
  Symmetric = false
FEATURE [App::MeasureDistance] Distance002  label="Distance: 1.67 mm"
  Distance = 1.66921
  P1 = (99.2361,4.7524,71.7)
  P2 = (99.2347,6.42161,71.7)
FEATURE [Sketcher::SketchObject] Sketch018
  FullyConstrained = true
  sketch-geometry (7):
    g0: LineSegment StartX=0 StartY=0 StartZ=0 EndX=0 EndY=6 EndZ=0
    g1: Circle CenterX=0 CenterY=0 CenterZ=0 NormalX=0 NormalY=0 NormalZ=1 AngleXU=0 Radius=1
    g2: Circle CenterX=8 CenterY=6 CenterZ=0 NormalX=0 NormalY=0 NormalZ=1 AngleXU=0 Radius=1
    g3: BSplineCurve PolesCount=3 KnotsCount=2 Degree=2 IsPeriodic=0
    g4: GeomPoint X=0 Y=0 Z=0
    g5: GeomPoint X=8 Y=6 Z=0
    g6: LineSegment StartX=0 StartY=6 StartZ=0 EndX=8 EndY=6 EndZ=0
  constraints (14):
    c: Coincident(g0,g-1)
    c: Distance(g0) = 6
    c: Vertical(g0)
    c: Coincident(g3,g0)
    c: Weight(g1) = 1
    c: Equal(g1,g2)
    c: InternalAlignment(g1,g3)
    c: InternalAlignment(g2,g3)
    c: InternalAlignment(g4,g3)
    c: InternalAlignment(g5,g3)
    c: Block(g3)
    c: Coincident(g6,g0)
    c: Coincident(g6,g3)
    c: Horizontal(g6)
FEATURE [Part::Extrusion] Extrude012  label="caseScrewPillarBracket"
  Base = -> Sketch018
  Dir = (0,0,1)
  DirMode = 2
  FaceMakerClass = Part::FaceMakerBullseye
  LengthFwd = 2.4
  LengthRev = 0
  Placement = pos=(15.76,29,8.8) rot=(0,1,0;0rad)
  Solid = true
  Symmetric = false
FEATURE [Sketcher::SketchObject] Sketch019
  FullyConstrained = true
  sketch-geometry (7):
    g0: LineSegment StartX=0 StartY=0 StartZ=0 EndX=0 EndY=6 EndZ=0
    g1: Circle CenterX=0 CenterY=0 CenterZ=0 NormalX=0 NormalY=0 NormalZ=1 AngleXU=0 Radius=1
    g2: Circle CenterX=8 CenterY=6 CenterZ=0 NormalX=0 NormalY=0 NormalZ=1 AngleXU=0 Radius=1
    g3: BSplineCurve PolesCount=3 KnotsCount=2 Degree=2 IsPeriodic=0
    g4: GeomPoint X=0 Y=0 Z=0
    g5: GeomPoint X=8 Y=6 Z=0
    g6: LineSegment StartX=0 StartY=6 StartZ=0 EndX=8 EndY=6 EndZ=0
  constraints (14):
    c: Coincident(g0,g-1)
    c: Distance(g0) = 6
    c: Vertical(g0)
    c: Coincident(g3,g0)
    c: Weight(g1) = 1
    c: Equal(g1,g2)
    c: InternalAlignment(g1,g3)
    c: InternalAlignment(g2,g3)
    c: InternalAlignment(g4,g3)
    c: InternalAlignment(g5,g3)
    c: Block(g3)
    c: Coincident(g6,g0)
    c: Coincident(g6,g3)
    c: Horizontal(g6)
FEATURE [Part::Extrusion] Extrude013  label="caseScrewPillarBracket001"
  Base = -> Sketch019
  Dir = (0,0,1)
  DirMode = 2
  FaceMakerClass = Part::FaceMakerBullseye
  LengthFwd = 2.4
  LengthRev = 0
  Placement = pos=(15.76,29,60.8) rot=(0,0,1;0rad)
  Solid = true
  Symmetric = false
FEATURE [Sketcher::SketchObject] Sketch020
  FullyConstrained = true
  sketch-geometry (7):
    g0: LineSegment StartX=0 StartY=0 StartZ=0 EndX=0 EndY=6 EndZ=0
    g1: Circle CenterX=0 CenterY=0 CenterZ=0 NormalX=0 NormalY=0 NormalZ=1 AngleXU=0 Radius=1
    g2: Circle CenterX=8 CenterY=6 CenterZ=0 NormalX=0 NormalY=0 NormalZ=1 AngleXU=0 Radius=1
    g3: BSplineCurve PolesCount=3 KnotsCount=2 Degree=2 IsPeriodic=0
    g4: GeomPoint X=0 Y=0 Z=0
    g5: GeomPoint X=8 Y=6 Z=0
    g6: LineSegment StartX=0 StartY=6 StartZ=0 EndX=8 EndY=6 EndZ=0
  constraints (14):
    c: Coincident(g0,g-1)
    c: Distance(g0) = 6
    c: Vertical(g0)
    c: Coincident(g3,g0)
    c: Weight(g1) = 1
    c: Equal(g1,g2)
    c: InternalAlignment(g1,g3)
    c: InternalAlignment(g2,g3)
    c: InternalAlignment(g4,g3)
    c: InternalAlignment(g5,g3)
    c: Block(g3)
    c: Coincident(g6,g0)
    c: Coincident(g6,g3)
    c: Horizontal(g6)
FEATURE [Part::Extrusion] Extrude014  label="caseScrewPillarBracket002"
  Base = -> Sketch020
  Dir = (0,0,1)
  DirMode = 2
  FaceMakerClass = Part::FaceMakerBullseye
  LengthFwd = 2.4
  LengthRev = 0
  Placement = pos=(13.7,29,13.26) rot=(0,-1,0;1.5708rad)
  Solid = true
  Symmetric = false
FEATURE [Sketcher::SketchObject] Sketch021
  FullyConstrained = true
  sketch-geometry (7):
    g0: LineSegment StartX=0 StartY=0 StartZ=0 EndX=0 EndY=6 EndZ=0
    g1: Circle CenterX=0 CenterY=0 CenterZ=0 NormalX=0 NormalY=0 NormalZ=1 AngleXU=0 Radius=1
    g2: Circle CenterX=8 CenterY=6 CenterZ=0 NormalX=0 NormalY=0 NormalZ=1 AngleXU=0 Radius=1
    g3: BSplineCurve PolesCount=3 KnotsCount=2 Degree=2 IsPeriodic=0
    g4: GeomPoint X=0 Y=0 Z=0
    g5: GeomPoint X=8 Y=6 Z=0
    g6: LineSegment StartX=0 StartY=6 StartZ=0 EndX=8 EndY=6 EndZ=0
  constraints (14):
    c: Coincident(g0,g-1)
    c: Distance(g0) = 6
    c: Vertical(g0)
    c: Coincident(g3,g0)
    c: Weight(g1) = 1
    c: Equal(g1,g2)
    c: InternalAlignment(g1,g3)
    c: InternalAlignment(g2,g3)
    c: InternalAlignment(g4,g3)
    c: InternalAlignment(g5,g3)
    c: Block(g3)
    c: Coincident(g6,g0)
    c: Coincident(g6,g3)
    c: Horizontal(g6)
FEATURE [Part::Extrusion] Extrude015  label="caseScrewPillarBracket003"
  Base = -> Sketch021
  Dir = (0,0,1)
  DirMode = 2
  FaceMakerClass = Part::FaceMakerBullseye
  LengthFwd = 2.4
  LengthRev = 0
  Placement = pos=(11.3,29,58.74) rot=(0,1,0;1.5708rad)
  Solid = true
  Symmetric = false
FEATURE [Sketcher::SketchObject] Sketch022
  FullyConstrained = true
  sketch-geometry (7):
    g0: LineSegment StartX=0 StartY=0 StartZ=0 EndX=0 EndY=6 EndZ=0
    g1: Circle CenterX=0 CenterY=0 CenterZ=0 NormalX=0 NormalY=0 NormalZ=1 AngleXU=0 Radius=1
    g2: Circle CenterX=8 CenterY=6 CenterZ=0 NormalX=0 NormalY=0 NormalZ=1 AngleXU=0 Radius=1
    g3: BSplineCurve PolesCount=3 KnotsCount=2 Degree=2 IsPeriodic=0
    g4: GeomPoint X=0 Y=0 Z=0
    g5: GeomPoint X=8 Y=6 Z=0
    g6: LineSegment StartX=0 StartY=6 StartZ=0 EndX=8 EndY=6 EndZ=0
  constraints (14):
    c: Coincident(g0,g-1)
    c: Distance(g0) = 6
    c: Vertical(g0)
    c: Coincident(g3,g0)
    c: Weight(g1) = 1
    c: Equal(g1,g2)
    c: InternalAlignment(g1,g3)
    c: InternalAlignment(g2,g3)
    c: InternalAlignment(g4,g3)
    c: InternalAlignment(g5,g3)
    c: Block(g3)
    c: Coincident(g6,g0)
    c: Coincident(g6,g3)
    c: Horizontal(g6)
FEATURE [Part::Extrusion] Extrude016  label="caseScrewPillarBracket004"
  Base = -> Sketch022
  Dir = (0,0,1)
  DirMode = 2
  FaceMakerClass = Part::FaceMakerBullseye
  LengthFwd = 2.4
  LengthRev = 0
  Placement = pos=(88.3,29,65.23) rot=(0,1,0;1.5708rad)
  Solid = true
  Symmetric = false
FEATURE [Sketcher::SketchObject] Sketch023
  FullyConstrained = true
  sketch-geometry (7):
    g0: LineSegment StartX=0 StartY=0 StartZ=0 EndX=0 EndY=6 EndZ=0
    g1: Circle CenterX=0 CenterY=0 CenterZ=0 NormalX=0 NormalY=0 NormalZ=1 AngleXU=0 Radius=1
    g2: Circle CenterX=8 CenterY=6 CenterZ=0 NormalX=0 NormalY=0 NormalZ=1 AngleXU=0 Radius=1
    g3: BSplineCurve PolesCount=3 KnotsCount=2 Degree=2 IsPeriodic=0
    g4: GeomPoint X=0 Y=0 Z=0
    g5: GeomPoint X=8 Y=6 Z=0
    g6: LineSegment StartX=0 StartY=6 StartZ=0 EndX=8 EndY=6 EndZ=0
  constraints (14):
    c: Coincident(g0,g-1)
    c: Distance(g0) = 6
    c: Vertical(g0)
    c: Coincident(g3,g0)
    c: Weight(g1) = 1
    c: Equal(g1,g2)
    c: InternalAlignment(g1,g3)
    c: InternalAlignment(g2,g3)
    c: InternalAlignment(g4,g3)
    c: InternalAlignment(g5,g3)
    c: Block(g3)
    c: Coincident(g6,g0)
    c: Coincident(g6,g3)
    c: Horizontal(g6)
FEATURE [Part::Extrusion] Extrude017  label="caseScrewPillarBracket005"
  Base = -> Sketch023
  Dir = (0,0,1)
  DirMode = 2
  FaceMakerClass = Part::FaceMakerBullseye
  LengthFwd = 2.4
  LengthRev = 0
  Placement = pos=(90.7,29,6.77) rot=(0,-1,0;1.5708rad)
  Solid = true
  Symmetric = false
FEATURE [Sketcher::SketchObject] Sketch024
  FullyConstrained = true
  sketch-geometry (7):
    g0: LineSegment StartX=0 StartY=0 StartZ=0 EndX=0 EndY=6 EndZ=0
    g1: Circle CenterX=0 CenterY=0 CenterZ=0 NormalX=0 NormalY=0 NormalZ=1 AngleXU=0 Radius=1
    g2: Circle CenterX=8 CenterY=6 CenterZ=0 NormalX=0 NormalY=0 NormalZ=1 AngleXU=0 Radius=1
    g3: BSplineCurve PolesCount=3 KnotsCount=2 Degree=2 IsPeriodic=0
    g4: GeomPoint X=0 Y=0 Z=0
    g5: GeomPoint X=8 Y=6 Z=0
    g6: LineSegment StartX=0 StartY=6 StartZ=0 EndX=8 EndY=6 EndZ=0
  constraints (14):
    c: Coincident(g0,g-1)
    c: Distance(g0) = 6
    c: Vertical(g0)
    c: Coincident(g3,g0)
    c: Weight(g1) = 1
    c: Equal(g1,g2)
    c: InternalAlignment(g1,g3)
    c: InternalAlignment(g2,g3)
    c: InternalAlignment(g4,g3)
    c: InternalAlignment(g5,g3)
    c: Block(g3)
    c: Coincident(g6,g0)
    c: Coincident(g6,g3)
    c: Horizontal(g6)
FEATURE [Part::Extrusion] Extrude018  label="caseScrewPillarBracket006"
  Base = -> Sketch024
  Dir = (0,0,1)
  DirMode = 2
  FaceMakerClass = Part::FaceMakerBullseye
  LengthFwd = 2.4
  LengthRev = 0
  Placement = pos=(103.7,29,6.77) rot=(0,-1,0;1.5708rad)
  Solid = true
  Symmetric = false
FEATURE [Sketcher::SketchObject] Sketch025
  FullyConstrained = true
  sketch-geometry (7):
    g0: LineSegment StartX=0 StartY=0 StartZ=0 EndX=0 EndY=6 EndZ=0
    g1: Circle CenterX=0 CenterY=0 CenterZ=0 NormalX=0 NormalY=0 NormalZ=1 AngleXU=0 Radius=1
    g2: Circle CenterX=8 CenterY=6 CenterZ=0 NormalX=0 NormalY=0 NormalZ=1 AngleXU=0 Radius=1
    g3: BSplineCurve PolesCount=3 KnotsCount=2 Degree=2 IsPeriodic=0
    g4: GeomPoint X=0 Y=0 Z=0
    g5: GeomPoint X=8 Y=6 Z=0
    g6: LineSegment StartX=0 StartY=6 StartZ=0 EndX=8 EndY=6 EndZ=0
  constraints (14):
    c: Coincident(g0,g-1)
    c: Distance(g0) = 6
    c: Vertical(g0)
    c: Coincident(g3,g0)
    c: Weight(g1) = 1
    c: Equal(g1,g2)
    c: InternalAlignment(g1,g3)
    c: InternalAlignment(g2,g3)
    c: InternalAlignment(g4,g3)
    c: InternalAlignment(g5,g3)
    c: Block(g3)
    c: Coincident(g6,g0)
    c: Coincident(g6,g3)
    c: Horizontal(g6)
FEATURE [Part::Extrusion] Extrude019  label="caseScrewPillarBracket007"
  Base = -> Sketch025
  Dir = (0,0,1)
  DirMode = 2
  FaceMakerClass = Part::FaceMakerBullseye
  LengthFwd = 2.4
  LengthRev = 0
  Placement = pos=(101.3,29,65.23) rot=(0,1,0;1.5708rad)
  Solid = true
  Symmetric = false
FEATURE [Part::Box] Box011  label="frontCaseScrewPillarBracket"
  AttacherType = Attacher::AttachEngine3D
  Height = 2.4
  Length = 16
  Placement = pos=(87,28,2.3) rot=(0,0,1;0rad)
  Width = 7
FEATURE [Part::Box] Box012  label="frontCaseScrewPillarBracket001"
  AttacherType = Attacher::AttachEngine3D
  Height = 2.4
  Length = 16
  Placement = pos=(87,28,67.3) rot=(0,0,1;0rad)
  Width = 7
FEATURE [Sketcher::SketchObject] Sketch026
  FullyConstrained = true
  sketch-geometry (17):
    g0: Circle CenterX=-3.5 CenterY=23.5 CenterZ=0 NormalX=0 NormalY=0 NormalZ=1 AngleXU=0 Radius=1
    g1: Circle CenterX=-1 CenterY=15.25 CenterZ=0 NormalX=0 NormalY=0 NormalZ=1 AngleXU=0 Radius=1
    g2: Circle CenterX=-3.5 CenterY=7 CenterZ=0 NormalX=0 NormalY=0 NormalZ=1 AngleXU=0 Radius=1
    g3: BSplineCurve PolesCount=3 KnotsCount=2 Degree=2 IsPeriodic=0
    g4: GeomPoint X=-3.5 Y=23.5 Z=0
    g5: GeomPoint X=-3.5 Y=7 Z=0
    g6: Circle CenterX=-4.8 CenterY=30.5 CenterZ=0 NormalX=0 NormalY=0 NormalZ=1 AngleXU=0 Radius=1
    g7: Circle CenterX=-3.5 CenterY=30.5 CenterZ=0 NormalX=0 NormalY=0 NormalZ=1 AngleXU=0 Radius=1
    g8: Circle CenterX=-3.5 CenterY=29.2 CenterZ=0 NormalX=0 NormalY=0 NormalZ=1 AngleXU=0 Radius=1
    g9: BSplineCurve PolesCount=3 KnotsCount=2 Degree=2 IsPeriodic=0
    g10: GeomPoint X=-4.8 Y=30.5 Z=0
    g11: GeomPoint X=-3.5 Y=29.2 Z=0
    g12: LineSegment StartX=-3.5 StartY=29.2 StartZ=0 EndX=-3.5 EndY=23.5 EndZ=0
    g13: LineSegment StartX=-4.8 StartY=30.5 StartZ=0 EndX=0 EndY=30.5 EndZ=0
    g14: LineSegment StartX=-3.5 StartY=5 StartZ=0 EndX=-3.5 EndY=7 EndZ=0
    g15: LineSegment StartX=0 StartY=5 StartZ=0 EndX=0 EndY=30.5 EndZ=0
    g16: LineSegment StartX=-3.5 StartY=5 StartZ=0 EndX=0 EndY=5 EndZ=0
  constraints (33):
    c: Weight(g0) = 1
    c: Equal(g0,g1)
    c: Equal(g0,g2)
    c: InternalAlignment(g0,g3)
    c: InternalAlignment(g1,g3)
    c: InternalAlignment(g2,g3)
    c: InternalAlignment(g4,g3)
    c: InternalAlignment(g5,g3)
    c: Block(g3)
    c: Weight(g6) = 1
    c: Equal(g6,g7)
    c: Equal(g6,g8)
    c: InternalAlignment(g6,g9)
    c: InternalAlignment(g7,g9)
    c: InternalAlignment(g8,g9)
    c: InternalAlignment(g10,g9)
    c: InternalAlignment(g11,g9)
    c: Block(g9)
    c: Coincident(g12,g9)
    c: Coincident(g12,g3)
    c: Vertical(g12)
    c: Coincident(g13,g9)
    c: Horizontal(g13)
    c: Distance(g13) = 4.8
    c: Coincident(g14,g3)
    c: Vertical(g14)
    c: Coincident(g15,g13)
    c: Vertical(g15)
    c: Tangent(g15,g1)
    c: Distance(g14) = 2
    c: Coincident(g16,g14)
    c: Horizontal(g16)
    c: Coincident(g15,g16)
FEATURE [Part::Feature] Face050
  shape: bbox 4.8 x 25.5 x 2e-07 mm, 1 faces, 0 solids (baked)
FEATURE [Part::Revolution] Revolve054  label="moreFrontCaseScrewPost001"
  Angle = 360
  Axis = (0,1,0)
  Base = (0,0,0)
  FaceMakerClass = Part::FaceMakerBullseye
  Placement = pos=(102.5,4.5,3.5) rot=(0,0,1;0rad)
  Solid = false
  Source = -> Face050
  Symmetric = false
FEATURE [Part::Feature] Face051
  shape: bbox 4.8 x 25.5 x 2e-07 mm, 1 faces, 0 solids (baked)
FEATURE [Part::Revolution] Revolve055  label="moreFrontCaseScrewPost002"
  Angle = 360
  Axis = (0,1,0)
  Base = (0,0,0)
  FaceMakerClass = Part::FaceMakerBullseye
  Placement = pos=(102.5,4.5,68.5) rot=(0,0,1;0rad)
  Solid = false
  Source = -> Face051
  Symmetric = false
FEATURE [Sketcher::SketchObject] Sketch027
  FullyConstrained = true
  sketch-geometry (10):
    g0: LineSegment StartX=-1.6 StartY=4.7 StartZ=0 EndX=-1.6 EndY=1.7 EndZ=0
    g1: LineSegment StartX=-3.5 StartY=4.7 StartZ=0 EndX=-1.6 EndY=4.7 EndZ=0
    g2: LineSegment StartX=-1.6 StartY=1.7 StartZ=0 EndX=-1.6 EndY=1.5 EndZ=0
    g3: LineSegment StartX=-1.6 StartY=1.5 StartZ=0 EndX=-5.2 EndY=1.5 EndZ=0
    g4: Circle CenterX=-3.5 CenterY=4.7 CenterZ=0 NormalX=0 NormalY=0 NormalZ=1 AngleXU=0 Radius=1
    g5: Circle CenterX=-3.59627 CenterY=2.99743 CenterZ=0 NormalX=0 NormalY=0 NormalZ=1 AngleXU=0 Radius=1
    g6: Circle CenterX=-5.2 CenterY=1.5 CenterZ=0 NormalX=0 NormalY=0 NormalZ=1 AngleXU=0 Radius=1
    g7: BSplineCurve PolesCount=3 KnotsCount=2 Degree=2 IsPeriodic=0
    g8: GeomPoint X=-3.5 Y=4.7 Z=0
    g9: GeomPoint X=-5.2 Y=1.5 Z=0
  constraints (23):
    c: Vertical(g0)
    c: Distance(g0) = 3
    c: Coincident(g1,g0)
    c: Horizontal(g1)
    c: Block(g0)
    c: Block(g1)
    c: Coincident(g2,g0)
    c: Vertical(g2)
    c: Distance(g2) = 0.2
    c: Coincident(g3,g2)
    c: Horizontal(g3)
    c: Block(g3)
    c: Coincident(g7,g1)
    c: Weight(g4) = 1
    c: Equal(g4,g5)
    c: Equal(g4,g6)
    c: Coincident(g7,g3)
    c: InternalAlignment(g4,g7)
    c: InternalAlignment(g5,g7)
    c: InternalAlignment(g6,g7)
    c: InternalAlignment(g8,g7)
    c: InternalAlignment(g9,g7)
    c: Block(g7)
FEATURE [Sketcher::SketchObject] Sketch028
  FullyConstrained = true
  sketch-geometry (18):
    g0: LineSegment StartX=0 StartY=3e-16 StartZ=0 EndX=0 EndY=1.7 EndZ=0
    g1: LineSegment StartX=-3.5 StartY=0 StartZ=0 EndX=-3.5 EndY=0.9 EndZ=0
    g2: Circle CenterX=-2.7 CenterY=1.7 CenterZ=0 NormalX=0 NormalY=0 NormalZ=1 AngleXU=0 Radius=1
    g3: Circle CenterX=-3.5 CenterY=1.7 CenterZ=0 NormalX=0 NormalY=0 NormalZ=1 AngleXU=0 Radius=1
    g4: Circle CenterX=-3.5 CenterY=0.9 CenterZ=0 NormalX=0 NormalY=0 NormalZ=1 AngleXU=0 Radius=1
    g5: BSplineCurve PolesCount=3 KnotsCount=2 Degree=2 IsPeriodic=0
    g6: GeomPoint X=-2.7 Y=1.7 Z=0
    g7: GeomPoint X=-3.5 Y=0.9 Z=0
    g8: LineSegment StartX=-3.5 StartY=0 StartZ=0 EndX=-3.5 EndY=-7 EndZ=0
    g9: LineSegment StartX=0 StartY=3e-16 StartZ=0 EndX=0 EndY=-7 EndZ=0
    g10: LineSegment StartX=-3.5 StartY=-7 StartZ=0 EndX=0 EndY=-7 EndZ=0
    g11: LineSegment StartX=-2.7 StartY=1.7 StartZ=0 EndX=-1.6 EndY=1.7 EndZ=0
    g12: LineSegment StartX=0 StartY=1.7 StartZ=0 EndX=0 EndY=4.5 EndZ=0
    g13: LineSegment StartX=0 StartY=4.5 StartZ=0 EndX=0 EndY=10.8 EndZ=0
    g14: LineSegment StartX=0 StartY=10.8 StartZ=0 EndX=-2 EndY=10.8 EndZ=0
    g15: LineSegment StartX=-1.6 StartY=4.7 StartZ=0 EndX=-1.6 EndY=1.7 EndZ=0
    g16: LineSegment StartX=-1.6 StartY=4.7 StartZ=0 EndX=-2 EndY=4.7 EndZ=0
    g17: LineSegment StartX=-2 StartY=4.7 StartZ=0 EndX=-2 EndY=10.8 EndZ=0
  constraints (44):
    c: Vertical(g0)
    c: Vertical(g1)
    c: Distance(g1) = 0.9
    c: Block(g0)
    c: Distance(g0) = 1.7
    c: Weight(g2) = 1
    c: Equal(g2,g3)
    c: Equal(g2,g4)
    c: Coincident(g5,g1)
    c: InternalAlignment(g2,g5)
    c: InternalAlignment(g3,g5)
    c: InternalAlignment(g4,g5)
    c: InternalAlignment(g6,g5)
    c: InternalAlignment(g7,g5)
    c: Block(g5)
    c: Coincident(g8,g1)
    c: Vertical(g8)
    c: Distance(g8) = 7
    c: Vertical(g9)
    c: Equal(g8,g9) = 7
    c: Coincident(g9,g0)
    c: Coincident(g10,g8)
    c: Coincident(g10,g9)
    c: Horizontal(g10)
    c: Coincident(g11,g5)
    c: Horizontal(g11)
    c: Coincident(g12,g0)
    c: Vertical(g12)
    c: Distance(g12) = 2.8
    c: Coincident(g13,g12)
    c: Vertical(g13)
    c: Distance(g13) = 6.3
    c: Coincident(g14,g13)
    c: Horizontal(g14)
    c: Distance(g14) = 2
    c: Vertical(g15)
    c: Distance(g15) = 3
    c: Block(g11)
    c: Coincident(g15,g11)
    c: Coincident(g16,g15)
    c: Horizontal(g16)
    c: Coincident(g17,g16)
    c: Coincident(g17,g14)
    c: Vertical(g17)
FEATURE [Part::Revolution] Revolve040  label="backCaseScrewRetainer001"
  Angle = 360
  Axis = (0,1,0)
  Base = (0,0,0)
  FaceMakerClass = Part::FaceMakerBullseye
  Placement = pos=(12.5,3,10) rot=(0,0,1;0rad)
  Solid = false
  Source = -> Face036
  Symmetric = false
FEATURE [Part::Feature] Face055
  shape: bbox 3.5 x 30.2 x 2e-07 mm, 1 faces, 0 solids (baked)
FEATURE [Part::Revolution] Revolve059  label="backCaseScrewPost"
  Angle = 360
  Axis = (0,1,0)
  Base = (0,0,0)
  FaceMakerClass = Part::FaceMakerBullseye
  Placement = pos=(12.5,4.5,10) rot=(0,0,1;0rad)
  Solid = false
  Source = -> Face055
  Symmetric = false
FEATURE [Part::Feature] Face056
  shape: bbox 3.5 x 30.2 x 2e-07 mm, 1 faces, 0 solids (baked)
FEATURE [Part::Revolution] Revolve060  label="backCaseScrewPost001"
  Angle = 360
  Axis = (0,1,0)
  Base = (0,0,0)
  FaceMakerClass = Part::FaceMakerBullseye
  Placement = pos=(12.5,4.5,62) rot=(0,0,1;0rad)
  Solid = false
  Source = -> Face056
  Symmetric = false
FEATURE [Part::Feature] Face057
  shape: bbox 3.5 x 17.8 x 2e-07 mm, 1 faces, 0 solids (baked)
FEATURE [Part::Revolution] Revolve061  label="removeToCreateScrewAndThreadedInsertHole"
  Angle = 360
  Axis = (0,1,0)
  Base = (0,0,0)
  FaceMakerClass = Part::FaceMakerBullseye
  Placement = pos=(12.5,0,10) rot=(0,0,1;0rad)
  Solid = false
  Source = -> Face057
  Symmetric = false
FEATURE [Part::Feature] Face058
  shape: bbox 3.5 x 17.8 x 2e-07 mm, 1 faces, 0 solids (baked)
FEATURE [Part::Revolution] Revolve062  label="removeToCreateScrewAndThreadedInsertHole001"
  Angle = 360
  Axis = (0,1,0)
  Base = (0,0,0)
  FaceMakerClass = Part::FaceMakerBullseye
  Placement = pos=(12.5,0,62) rot=(0,0,1;0rad)
  Solid = false
  Source = -> Face058
  Symmetric = false
FEATURE [Part::Feature] Face059
  shape: bbox 3.5 x 17.8 x 2e-07 mm, 1 faces, 0 solids (baked)
FEATURE [Part::Revolution] Revolve063  label="removeToCreateScrewAndThreadedInsertHole002"
  Angle = 360
  Axis = (0,1,0)
  Base = (0,0,0)
  FaceMakerClass = Part::FaceMakerBullseye
  Placement = pos=(89.5,0,68.5) rot=(0,0,1;0rad)
  Solid = false
  Source = -> Face059
  Symmetric = false
FEATURE [Part::Feature] Face060
  shape: bbox 3.5 x 17.8 x 2e-07 mm, 1 faces, 0 solids (baked)
FEATURE [Part::Revolution] Revolve064  label="removeToCreateScrewAndThreadedInsertHole003"
  Angle = 360
  Axis = (0,1,0)
  Base = (0,0,0)
  FaceMakerClass = Part::FaceMakerBullseye
  Placement = pos=(89.5,0,3.5) rot=(0,0,1;0rad)
  Solid = false
  Source = -> Face060
  Symmetric = false
FEATURE [Part::Feature] Face061
  shape: bbox 3.5 x 17.8 x 2e-07 mm, 1 faces, 0 solids (baked)
FEATURE [Part::Revolution] Revolve065  label="removeToCreateScrewAndThreadedInsertHole004"
  Angle = 360
  Axis = (0,1,0)
  Base = (0,0,0)
  FaceMakerClass = Part::FaceMakerBullseye
  Placement = pos=(102.5,4.7,3.5) rot=(0,0,1;0rad)
  Solid = false
  Source = -> Face061
  Symmetric = false
FEATURE [Part::Feature] Face062
  shape: bbox 3.5 x 17.8 x 2e-07 mm, 1 faces, 0 solids (baked)
FEATURE [Part::Revolution] Revolve066  label="removeToCreateScrewAndThreadedInsertHole005"
  Angle = 360
  Axis = (0,1,0)
  Base = (0,0,0)
  FaceMakerClass = Part::FaceMakerBullseye
  Placement = pos=(102.5,4.7,68.5) rot=(0,0,1;0rad)
  Solid = false
  Source = -> Face062
  Symmetric = false
FEATURE [Part::MultiFuse] Fusion047  label="makeHoles"
  Shapes = -> [Revolve066,Revolve065,Revolve064,Revolve063,Revolve062,Revolve061]
FEATURE [Part::Feature] Face063
  shape: bbox 3.6 x 3.2 x 2e-07 mm, 1 faces, 0 solids (baked)
FEATURE [Part::Revolution] Revolve067  label="moreFrontCaseScrewRetainer002"
  Angle = 360
  Axis = (0,1,0)
  Base = (0,0,0)
  FaceMakerClass = Part::FaceMakerBullseye
  Placement = pos=(102.5,4.5,68.5) rot=(0,0,1;0rad)
  Solid = false
  Source = -> Face063
  Symmetric = false
FEATURE [Part::Feature] Face064
  shape: bbox 3.6 x 3.2 x 2e-07 mm, 1 faces, 0 solids (baked)
FEATURE [Part::Revolution] Revolve068  label="moreFrontCaseScrewRetainer003"
  Angle = 360
  Axis = (0,1,0)
  Base = (0,0,0)
  FaceMakerClass = Part::FaceMakerBullseye
  Placement = pos=(102.5,4.5,3.5) rot=(0,0,1;0rad)
  Solid = false
  Source = -> Face064
  Symmetric = false
FEATURE [Part::Feature] Face065
  shape: bbox 3.5 x 17.8 x 2e-07 mm, 1 faces, 0 solids (baked)
FEATURE [Part::Revolution] Revolve069  label="removeToCreateScrewAndThreadedInsertHole006"
  Angle = 360
  Axis = (0,1,0)
  Base = (0,0,0)
  FaceMakerClass = Part::FaceMakerBullseye
  Placement = pos=(12.5,0,10) rot=(0,0,1;0rad)
  Solid = false
  Source = -> Face065
  Symmetric = false
FEATURE [Part::Feature] Face066
  shape: bbox 3.5 x 17.8 x 2e-07 mm, 1 faces, 0 solids (baked)
FEATURE [Part::Revolution] Revolve070  label="removeToCreateScrewAndThreadedInsertHole007"
  Angle = 360
  Axis = (0,1,0)
  Base = (0,0,0)
  FaceMakerClass = Part::FaceMakerBullseye
  Placement = pos=(12.5,0,62) rot=(0,0,1;0rad)
  Solid = false
  Source = -> Face066
  Symmetric = false
FEATURE [Part::Feature] Face067
  shape: bbox 3.5 x 17.8 x 2e-07 mm, 1 faces, 0 solids (baked)
FEATURE [Part::Revolution] Revolve071  label="removeToCreateScrewAndThreadedInsertHole008"
  Angle = 360
  Axis = (0,1,0)
  Base = (0,0,0)
  FaceMakerClass = Part::FaceMakerBullseye
  Placement = pos=(89.5,0,68.5) rot=(0,0,1;0rad)
  Solid = false
  Source = -> Face067
  Symmetric = false
FEATURE [Part::Feature] Face068
  shape: bbox 3.5 x 17.8 x 2e-07 mm, 1 faces, 0 solids (baked)
FEATURE [Part::Revolution] Revolve072  label="removeToCreateScrewAndThreadedInsertHole009"
  Angle = 360
  Axis = (0,1,0)
  Base = (0,0,0)
  FaceMakerClass = Part::FaceMakerBullseye
  Placement = pos=(89.5,0,3.5) rot=(0,0,1;0rad)
  Solid = false
  Source = -> Face068
  Symmetric = false
FEATURE [Part::Feature] Face069
  shape: bbox 3.5 x 17.8 x 2e-07 mm, 1 faces, 0 solids (baked)
FEATURE [Part::Feature] Face070
  shape: bbox 3.5 x 17.8 x 2e-07 mm, 1 faces, 0 solids (baked)
FEATURE [Part::Revolution] Revolve073  label="removeToCreateScrewAndThreadedInsertHole010"
  Angle = 360
  Axis = (0,1,0)
  Base = (0,0,0)
  FaceMakerClass = Part::FaceMakerBullseye
  Placement = pos=(102.5,4.7,3.5) rot=(0,0,1;0rad)
  Solid = false
  Source = -> Face069
  Symmetric = false
FEATURE [Part::Revolution] Revolve074  label="removeToCreateScrewAndThreadedInsertHole011"
  Angle = 360
  Axis = (0,1,0)
  Base = (0,0,0)
  FaceMakerClass = Part::FaceMakerBullseye
  Placement = pos=(102.5,4.7,68.5) rot=(0,0,1;0rad)
  Solid = false
  Source = -> Face070
  Symmetric = false
FEATURE [Part::MultiFuse] Fusion048  label="makeHoles001"
  Shapes = -> [Revolve074,Revolve073,Revolve072,Revolve071,Revolve070,Revolve069]
FEATURE [Part::MultiFuse] Fusion049  label="caseScrewRetainers"
  Shapes = -> [Revolve067,Revolve068,Revolve048,Revolve047,Revolve039,Revolve040]
FEATURE [Part::Cut] Cut015  label="caseScrewRetainers001"
  Base = -> Fusion049
  Tool = -> Fusion048
FEATURE [Part::MultiFuse] Fusion050  label="casePillars"
  Shapes = -> [Revolve055,Revolve054,Revolve043,Revolve046,Revolve059,Revolve060]
FEATURE [Part::Feature] Face071 .. Face076  x6 (patterned run collapsed; names and placements below)
  shape: bbox 3.5 x 17.8 x 2e-07 mm, 1 faces, 0 solids (baked)
FEATURE [Part::Revolution] Revolve075  label="removeToCreateScrewAndThreadedInsertHole012"
  Angle = 360
  Axis = (0,1,0)
  Base = (0,0,0)
  FaceMakerClass = Part::FaceMakerBullseye
  Placement = pos=(12.5,0,10) rot=(0,0,1;0rad)
  Solid = false
  Source = -> Face071
  Symmetric = false
FEATURE [Part::Revolution] Revolve076  label="removeToCreateScrewAndThreadedInsertHole013"
  Angle = 360
  Axis = (0,1,0)
  Base = (0,0,0)
  FaceMakerClass = Part::FaceMakerBullseye
  Placement = pos=(12.5,0,62) rot=(0,0,1;0rad)
  Solid = false
  Source = -> Face072
  Symmetric = false
FEATURE [Part::Revolution] Revolve077  label="removeToCreateScrewAndThreadedInsertHole014"
  Angle = 360
  Axis = (0,1,0)
  Base = (0,0,0)
  FaceMakerClass = Part::FaceMakerBullseye
  Placement = pos=(89.5,0,68.5) rot=(0,0,1;0rad)
  Solid = false
  Source = -> Face073
  Symmetric = false
FEATURE [Part::Revolution] Revolve078  label="removeToCreateScrewAndThreadedInsertHole015"
  Angle = 360
  Axis = (0,1,0)
  Base = (0,0,0)
  FaceMakerClass = Part::FaceMakerBullseye
  Placement = pos=(89.5,0,3.5) rot=(0,0,1;0rad)
  Solid = false
  Source = -> Face074
  Symmetric = false
FEATURE [Part::Revolution] Revolve079  label="removeToCreateScrewAndThreadedInsertHole016"
  Angle = 360
  Axis = (0,1,0)
  Base = (0,0,0)
  FaceMakerClass = Part::FaceMakerBullseye
  Placement = pos=(102.5,4.7,3.5) rot=(0,0,1;0rad)
  Solid = false
  Source = -> Face075
  Symmetric = false
FEATURE [Part::Revolution] Revolve080  label="removeToCreateScrewAndThreadedInsertHole017"
  Angle = 360
  Axis = (0,1,0)
  Base = (0,0,0)
  FaceMakerClass = Part::FaceMakerBullseye
  Placement = pos=(102.5,4.7,68.5) rot=(0,0,1;0rad)
  Solid = false
  Source = -> Face076
  Symmetric = false
FEATURE [Part::MultiFuse] Fusion051  label="makeHoles002"
  Shapes = -> [Revolve080,Revolve079,Revolve078,Revolve077,Revolve076,Revolve075]
FEATURE [Part::Cut] Cut016  label="caesPillars"
  Base = -> Fusion050
  Tool = -> Fusion051
FEATURE [Part::Revolution] Revolve009  label="plugHousing016"
  Angle = 360
  Axis = (0,1,0)
  Base = (0,0,0)
  FaceMakerClass = Part::FaceMakerBullseye
  Placement = pos=(0,0,36.15) rot=(0,0,1;0rad)
  Solid = false
  Source = -> Face012
  Symmetric = false
FEATURE [Part::MultiFuse] Fusion014  label="plugHousing023"
  Placement = pos=(0,0,0) rot=(0,0,1;1.5708rad)
  Shapes = -> [Revolve011,Revolve009]
FEATURE [Part::Revolution] Revolve010  label="plugHousing017"
  Angle = 360
  Axis = (0,1,0)
  Base = (0,0,0)
  FaceMakerClass = Part::FaceMakerBullseye
  Placement = pos=(0,0,36.15) rot=(0,0,1;0rad)
  Solid = false
  Source = -> Face014
  Symmetric = false
FEATURE [Part::MultiFuse] Fusion015  label="plugHousing024"
  Placement = pos=(0,0,0) rot=(0,0,1;1.5708rad)
  Shapes = -> [Revolve010,Revolve015]
FEATURE [Part::Revolution] Revolve014  label="plugHousing026"
  Angle = 360
  Axis = (0,1,0)
  Base = (0,0,0)
  FaceMakerClass = Part::FaceMakerBullseye
  Placement = pos=(0,0,36.15) rot=(0,0,1;0rad)
  Solid = false
  Source = -> Face011
  Symmetric = false
FEATURE [Part::Revolution] Revolve013  label="plugHousing025"
  Angle = 360
  Axis = (0,1,0)
  Base = (0,0,0)
  FaceMakerClass = Part::FaceMakerBullseye
  Placement = pos=(0,0,36.15) rot=(0,0,1;0rad)
  Solid = false
  Source = -> Face015
  Symmetric = false
FEATURE [Part::MultiFuse] Fusion016  label="plugHousing028"
  Placement = pos=(0,19,0) rot=(0,0,1;3.14159rad)
  Shapes = -> [Fusion014,Fusion013]
FEATURE [Part::MultiFuse] Fusion011  label="plugHousing018"
  Placement = pos=(0,0,0) rot=(0,0,1;1.5708rad)
  Shapes = -> [Revolve014,Revolve013]
FEATURE [Part::MultiFuse] Fusion012  label="plugHousing019"
  Placement = pos=(0,19,0) rot=(0,0,1;3.14159rad)
  Shapes = -> [Fusion011,Fusion015]
FEATURE [Part::MultiFuse] Fusion017  label="plugHousing029"
  Placement = pos=(122.621,0,-0.15) rot=(0,0,1;0rad)
  Shapes = -> [Fusion016,Fusion012]
FEATURE [Part::MultiFuse] Fusion052  label="casePillarRetainers"
  Shapes = -> [Extrude012,Extrude013,Extrude014,Extrude015,Extrude016,Extrude017,Extrude018,Extrude019,Box011,Box012]
FEATURE [Part::Feature] Face077
  shape: bbox 3.5 x 17.8 x 2e-07 mm, 1 faces, 0 solids (baked)
FEATURE [Part::Revolution] Revolve081  label="removeToCreateScrewAndThreadedInsertHole018"
  Angle = 360
  Axis = (0,1,0)
  Base = (0,0,0)
  FaceMakerClass = Part::FaceMakerBullseye
  Placement = pos=(62.3,30.3,19.7) rot=(0,0,1;0rad)
  Solid = false
  Source = -> Face077
  Symmetric = false
FEATURE [Part::Feature] Face078
  shape: bbox 3.5 x 17.8 x 2e-07 mm, 1 faces, 0 solids (baked)
FEATURE [Part::Revolution] Revolve082  label="removeToCreateScrewAndThreadedInsertHole019"
  Angle = 360
  Axis = (0,1,0)
  Base = (0,0,0)
  FaceMakerClass = Part::FaceMakerBullseye
  Placement = pos=(62.3,30.3,51.7) rot=(0,0,1;0rad)
  Solid = false
  Source = -> Face078
  Symmetric = false
FEATURE [Part::Feature] Face079
  shape: bbox 3.5 x 17.8 x 2e-07 mm, 1 faces, 0 solids (baked)
FEATURE [Part::Revolution] Revolve083  label="removeToCreateScrewAndThreadedInsertHole020"
  Angle = 360
  Axis = (0,1,0)
  Base = (0,0,0)
  FaceMakerClass = Part::FaceMakerBullseye
  Placement = pos=(30.3,30.3,19.7) rot=(0,0,1;0rad)
  Solid = false
  Source = -> Face079
  Symmetric = false
FEATURE [Part::Feature] Face080
  shape: bbox 3.5 x 17.8 x 2e-07 mm, 1 faces, 0 solids (baked)
FEATURE [Part::Revolution] Revolve084  label="removeToCreateScrewAndThreadedInsertHole021"
  Angle = 360
  Axis = (0,1,0)
  Base = (0,0,0)
  FaceMakerClass = Part::FaceMakerBullseye
  Placement = pos=(30.3,30.3,51.7) rot=(0,0,1;0rad)
  Solid = false
  Source = -> Face080
  Symmetric = false
FEATURE [Part::MultiFuse] Fusion053  label="createThreadedInsertHolesForFan"
  Shapes = -> [Revolve081,Revolve082,Revolve083,Revolve084]
FEATURE [Part::Cut] Cut017  label="fanScrewHousing001"
  Base = -> Fusion046
  Tool = -> Fusion053
FEATURE [Part::Feature] Face081
  shape: bbox 3.5 x 17.8 x 2e-07 mm, 1 faces, 0 solids (baked)
FEATURE [Part::Revolution] Revolve085  label="removeToCreateScrewAndThreadedInsertHole022"
  Angle = 360
  Axis = (0,1,0)
  Base = (0,0,0)
  FaceMakerClass = Part::FaceMakerBullseye
  Placement = pos=(62.3,30.3,19.7) rot=(0,0,1;0rad)
  Solid = false
  Source = -> Face081
  Symmetric = false
FEATURE [Part::Feature] Face082
  shape: bbox 3.5 x 17.8 x 2e-07 mm, 1 faces, 0 solids (baked)
FEATURE [Part::Revolution] Revolve086  label="removeToCreateScrewAndThreadedInsertHole023"
  Angle = 360
  Axis = (0,1,0)
  Base = (0,0,0)
  FaceMakerClass = Part::FaceMakerBullseye
  Placement = pos=(62.3,30.3,51.7) rot=(0,0,1;0rad)
  Solid = false
  Source = -> Face082
  Symmetric = false
FEATURE [Part::Feature] Face083
  shape: bbox 3.5 x 17.8 x 2e-07 mm, 1 faces, 0 solids (baked)
FEATURE [Part::Revolution] Revolve087  label="removeToCreateScrewAndThreadedInsertHole024"
  Angle = 360
  Axis = (0,1,0)
  Base = (0,0,0)
  FaceMakerClass = Part::FaceMakerBullseye
  Placement = pos=(30.3,30.3,19.7) rot=(0,0,1;0rad)
  Solid = false
  Source = -> Face083
  Symmetric = false
FEATURE [Part::Feature] Face084
  shape: bbox 3.5 x 17.8 x 2e-07 mm, 1 faces, 0 solids (baked)
FEATURE [Part::Revolution] Revolve088  label="removeToCreateScrewAndThreadedInsertHole025"
  Angle = 360
  Axis = (0,1,0)
  Base = (0,0,0)
  FaceMakerClass = Part::FaceMakerBullseye
  Placement = pos=(30.3,30.3,51.7) rot=(0,0,1;0rad)
  Solid = false
  Source = -> Face084
  Symmetric = false
FEATURE [Part::MultiFuse] Fusion054  label="createThreadedInsertHolesForFan001"
  Shapes = -> [Revolve085,Revolve086,Revolve087,Revolve088]
FEATURE [Part::Cut] Cut018  label="top007"
  Base = -> Fusion040
  Tool = -> Fusion054
FEATURE [Sketcher::SketchObject] Sketch029
  FullyConstrained = false
  Placement = pos=(0,0,0) rot=(1,0,0;1.5708rad)
  sketch-geometry (24):
    g0: ArcOfCircle CenterX=-4 CenterY=-10.5 CenterZ=0 NormalX=0 NormalY=0 NormalZ=1 AngleXU=0 Radius=1.5 StartAngle=6e-16 EndAngle=3.14159
    g1: ArcOfCircle CenterX=-34.2 CenterY=-10.5 CenterZ=0 NormalX=0 NormalY=0 NormalZ=1 AngleXU=0 Radius=1.5 StartAngle=0 EndAngle=3.14159
    g2: ArcOfCircle CenterX=-34.2 CenterY=-27.7 CenterZ=0 NormalX=0 NormalY=0 NormalZ=1 AngleXU=0 Radius=1.5 StartAngle=3.14159 EndAngle=6.28319
    g3: ArcOfCircle CenterX=-4 CenterY=-27.7 CenterZ=0 NormalX=0 NormalY=0 NormalZ=1 AngleXU=0 Radius=1.5 StartAngle=3.1416 EndAngle=6.28319
    g4: ArcOfCircle CenterX=-10 CenterY=-4.3 CenterZ=0 NormalX=0 NormalY=0 NormalZ=1 AngleXU=0 Radius=1.5 StartAngle=2e-16 EndAngle=3.14159
    g5: ArcOfCircle CenterX=-16.1 CenterY=-1.8 CenterZ=0 NormalX=0 NormalY=0 NormalZ=1 AngleXU=0 Radius=1.5 StartAngle=5e-16 EndAngle=3.14159
    g6: ArcOfCircle CenterX=-22.1 CenterY=-1.8 CenterZ=0 NormalX=0 NormalY=0 NormalZ=1 AngleXU=0 Radius=1.5 StartAngle=5e-16 EndAngle=3.14159
    g7: ArcOfCircle CenterX=-28.2 CenterY=-4.3 CenterZ=0 NormalX=0 NormalY=0 NormalZ=1 AngleXU=0 Radius=1.5 StartAngle=2e-16 EndAngle=3.14159
    g8: ArcOfCircle CenterX=-10 CenterY=-33.9 CenterZ=0 NormalX=0 NormalY=0 NormalZ=1 AngleXU=0 Radius=1.5 StartAngle=3.14159 EndAngle=6.28319
    g9: ArcOfCircle CenterX=-16.1 CenterY=-36.4 CenterZ=0 NormalX=0 NormalY=0 NormalZ=1 AngleXU=0 Radius=1.5 StartAngle=3.14159 EndAngle=6.28319
    g10: ArcOfCircle CenterX=-22.1 CenterY=-36.4 CenterZ=0 NormalX=0 NormalY=0 NormalZ=1 AngleXU=0 Radius=1.5 StartAngle=3.14159 EndAngle=6.28319
    g11: ArcOfCircle CenterX=-28.2 CenterY=-33.9 CenterZ=0 NormalX=0 NormalY=0 NormalZ=1 AngleXU=0 Radius=1.5 StartAngle=3.14159 EndAngle=6.28319
    g12: LineSegment StartX=-35.7 StartY=-10.5 StartZ=0 EndX=-35.7 EndY=-27.7 EndZ=0
    g13: LineSegment StartX=-32.7 StartY=-10.5 StartZ=0 EndX=-32.7 EndY=-27.7 EndZ=0
    g14: LineSegment StartX=-29.7 StartY=-33.9 StartZ=0 EndX=-29.7 EndY=-4.3 EndZ=0
    g15: LineSegment StartX=-26.7 StartY=-33.9 StartZ=0 EndX=-26.7 EndY=-4.3 EndZ=0
    g16: LineSegment StartX=-2.5 StartY=-10.5 StartZ=0 EndX=-2.5 EndY=-27.7 EndZ=0
    g17: LineSegment StartX=-8.5 StartY=-4.3 StartZ=0 EndX=-8.5 EndY=-33.9 EndZ=0
    g18: LineSegment StartX=-5.5 StartY=-10.5 StartZ=0 EndX=-5.5 EndY=-27.7 EndZ=0
    g19: LineSegment StartX=-11.5 StartY=-4.3 StartZ=0 EndX=-11.5 EndY=-33.9 EndZ=0
    g20: LineSegment StartX=-14.6 StartY=-1.8 StartZ=0 EndX=-14.6 EndY=-36.4 EndZ=0
    g21: LineSegment StartX=-17.6 StartY=-1.8 StartZ=0 EndX=-17.6 EndY=-36.4 EndZ=0
    g22: LineSegment StartX=-20.6 StartY=-36.4 StartZ=0 EndX=-20.6 EndY=-1.8 EndZ=0
    g23: LineSegment StartX=-23.6 StartY=-1.8 StartZ=0 EndX=-23.6 EndY=-36.4 EndZ=0
  constraints (48):
    c: Block(g0)
    c: Block(g1)
    c: Block(g2)
    c: Block(g3)
    c: Block(g4)
    c: Block(g5)
    c: Block(g6)
    c: Block(g7)
    c: Block(g8)
    c: Block(g9)
    c: Block(g10)
    c: Block(g11)
    c: Coincident(g12,g1)
    c: Coincident(g12,g2)
    c: Vertical(g12)
    c: Coincident(g13,g1)
    c: Coincident(g13,g2)
    c: Vertical(g13)
    c: Coincident(g14,g11)
    c: Coincident(g14,g7)
    c: Vertical(g14)
    c: Coincident(g15,g11)
    c: Coincident(g15,g7)
    c: Vertical(g15)
    c: Coincident(g16,g0)
    c: Coincident(g16,g3)
    c: Vertical(g16)
    c: Coincident(g17,g4)
    c: Coincident(g17,g8)
    c: Vertical(g17)
    c: Coincident(g18,g0)
    c: Coincident(g18,g3)
    c: Vertical(g18)
    c: Coincident(g19,g4)
    c: Coincident(g19,g8)
    c: Vertical(g19)
    c: Coincident(g20,g5)
    c: Coincident(g20,g9)
    c: Vertical(g20)
    c: Coincident(g21,g5)
    c: Coincident(g21,g9)
    c: Vertical(g21)
    c: Coincident(g22,g10)
    c: Coincident(g22,g6)
    c: Vertical(g22)
    c: Coincident(g23,g6)
    c: Coincident(g23,g10)
    c: Vertical(g23)
FEATURE [Part::Extrusion] Extrude020  label="removeToCreateFanGrillHoles"
  Base = -> Sketch029
  Dir = (0,-1,6e-16)
  DirMode = 2
  FaceMakerClass = Part::FaceMakerBullseye
  LengthFwd = 10
  LengthRev = 0
  Placement = pos=(65.4,44,54.82) rot=(0,0,1;0rad)
  Solid = true
  Symmetric = false
FEATURE [Part::MultiFuse] Fusion055  label="top008"
  Shapes = -> [Cut017,Cut018]
FEATURE [Part::Cut] Cut019  label="top009"
  Base = -> Fusion055
  Tool = -> Extrude020
FEATURE [App::MeasureDistance] Distance003  label="Distance: 71.95 mm"
  Distance = 71.9513
  P1 = (117,38,72)
  P2 = (117,38,0.0487319)
FEATURE [Sketcher::SketchObject] Sketch030
  FullyConstrained = true
  Placement = pos=(117,19,0) rot=(0.57735,0.57735,0.57735;2.0944rad)
  sketch-geometry (48):
    g0: LineSegment StartX=-49.19 StartY=69.25 StartZ=0 EndX=-49.19 EndY=66.25 EndZ=0
    g1: LineSegment StartX=-49.19 StartY=63.5 StartZ=0 EndX=-49.19 EndY=60.5 EndZ=0
    g2: LineSegment StartX=-49.19 StartY=57.75 StartZ=0 EndX=-49.19 EndY=54.75 EndZ=0
    g3: LineSegment StartX=-49.19 StartY=52 StartZ=0 EndX=-49.19 EndY=49 EndZ=0
    g4: LineSegment StartX=-49.19 StartY=46.25 StartZ=0 EndX=-49.19 EndY=43.25 EndZ=0
    g5: LineSegment StartX=-49.19 StartY=40.5 StartZ=0 EndX=-49.19 EndY=37.5 EndZ=0
    g6: LineSegment StartX=-49.19 StartY=34.5 StartZ=0 EndX=-49.19 EndY=31.5 EndZ=0
    g7: LineSegment StartX=-49.19 StartY=28.75 StartZ=0 EndX=-49.19 EndY=25.75 EndZ=0
    g8: LineSegment StartX=-49.19 StartY=23 StartZ=0 EndX=-49.19 EndY=20 EndZ=0
    g9: LineSegment StartX=-49.19 StartY=17.25 StartZ=0 EndX=-49.19 EndY=14.25 EndZ=0
    g10: LineSegment StartX=-49.19 StartY=11.5 StartZ=0 EndX=-49.19 EndY=8.5 EndZ=0
    g11: LineSegment StartX=-49.19 StartY=5.75 StartZ=0 EndX=-49.19 EndY=2.75 EndZ=0
    g12: ArcOfCircle CenterX=-1.5 CenterY=67.75 CenterZ=0 NormalX=0 NormalY=0 NormalZ=1 AngleXU=0 Radius=1.5 StartAngle=4.71239 EndAngle=7.85398
    g13: ArcOfCircle CenterX=-1.5 CenterY=62 CenterZ=0 NormalX=0 NormalY=0 NormalZ=1 AngleXU=0 Radius=1.5 StartAngle=4.71239 EndAngle=7.85398
    g14: ArcOfCircle CenterX=-1.5 CenterY=56.25 CenterZ=0 NormalX=0 NormalY=0 NormalZ=1 AngleXU=0 Radius=1.5 StartAngle=4.71239 EndAngle=7.85398
    g15: ArcOfCircle CenterX=-11.49 CenterY=50.5 CenterZ=0 NormalX=0 NormalY=0 NormalZ=1 AngleXU=0 Radius=1.5 StartAngle=4.71239 EndAngle=7.85398
    g16: ArcOfCircle CenterX=-16.28 CenterY=44.75 CenterZ=0 NormalX=0 NormalY=0 NormalZ=1 AngleXU=0 Radius=1.5 StartAngle=4.71239 EndAngle=7.85398
    g17: ArcOfCircle CenterX=-18.2337 CenterY=39 CenterZ=0 NormalX=0 NormalY=0 NormalZ=1 AngleXU=0 Radius=1.5 StartAngle=4.71485 EndAngle=7.85398
    g18: ArcOfCircle CenterX=-16.2837 CenterY=27.25 CenterZ=0 NormalX=0 NormalY=0 NormalZ=1 AngleXU=0 Radius=1.5 StartAngle=4.71485 EndAngle=7.85398
    g19: ArcOfCircle CenterX=-18.2337 CenterY=33 CenterZ=0 NormalX=0 NormalY=0 NormalZ=1 AngleXU=0 Radius=1.5 StartAngle=4.71485 EndAngle=7.85398
    g20: ArcOfCircle CenterX=-11.49 CenterY=21.5 CenterZ=0 NormalX=0 NormalY=0 NormalZ=1 AngleXU=0 Radius=1.5 StartAngle=4.71239 EndAngle=7.85398
    g21: ArcOfCircle CenterX=-1.5 CenterY=4.25 CenterZ=0 NormalX=0 NormalY=0 NormalZ=1 AngleXU=0 Radius=1.5 StartAngle=4.71239 EndAngle=7.85398
    g22: ArcOfCircle CenterX=-1.5 CenterY=10 CenterZ=0 NormalX=0 NormalY=0 NormalZ=1 AngleXU=0 Radius=1.5 StartAngle=4.71239 EndAngle=7.85398
    g23: ArcOfCircle CenterX=-1.5 CenterY=15.75 CenterZ=0 NormalX=0 NormalY=0 NormalZ=1 AngleXU=0 Radius=1.5 StartAngle=4.71239 EndAngle=7.85398
    g24: LineSegment StartX=-49.19 StartY=69.25 StartZ=0 EndX=-1.5 EndY=69.25 EndZ=0
    g25: LineSegment StartX=-49.19 StartY=66.25 StartZ=0 EndX=-1.5 EndY=66.25 EndZ=0
    g26: LineSegment StartX=-49.19 StartY=63.5 StartZ=0 EndX=-1.5 EndY=63.5 EndZ=0
    g27: LineSegment StartX=-49.19 StartY=60.5 StartZ=0 EndX=-1.5 EndY=60.5 EndZ=0
    g28: LineSegment StartX=-49.19 StartY=57.75 StartZ=0 EndX=-1.5 EndY=57.75 EndZ=0
    g29: LineSegment StartX=-49.19 StartY=54.75 StartZ=0 EndX=-1.5 EndY=54.75 EndZ=0
    g30: LineSegment StartX=-49.19 StartY=52 StartZ=0 EndX=-11.49 EndY=52 EndZ=0
    g31: LineSegment StartX=-49.19 StartY=49 StartZ=0 EndX=-11.49 EndY=49 EndZ=0
    g32: LineSegment StartX=-49.19 StartY=46.25 StartZ=0 EndX=-16.28 EndY=46.25 EndZ=0
    g33: LineSegment StartX=-49.19 StartY=43.25 StartZ=0 EndX=-16.28 EndY=43.25 EndZ=0
    g34: LineSegment StartX=-49.19 StartY=40.5 StartZ=0 EndX=-18.2337 EndY=40.5 EndZ=0
    g35: LineSegment StartX=-49.19 StartY=37.5 StartZ=0 EndX=-18.23 EndY=37.5 EndZ=0
    g36: LineSegment StartX=-49.19 StartY=34.5 StartZ=0 EndX=-18.2337 EndY=34.5 EndZ=0
    g37: LineSegment StartX=-49.19 StartY=31.5 StartZ=0 EndX=-18.23 EndY=31.5 EndZ=0
    g38: LineSegment StartX=-49.19 StartY=28.75 StartZ=0 EndX=-16.2837 EndY=28.75 EndZ=0
    g39: LineSegment StartX=-49.19 StartY=25.75 StartZ=0 EndX=-16.28 EndY=25.75 EndZ=0
    g40: LineSegment StartX=-49.19 StartY=23 StartZ=0 EndX=-11.49 EndY=23 EndZ=0
    g41: LineSegment StartX=-49.19 StartY=20 StartZ=0 EndX=-11.49 EndY=20 EndZ=0
    g42: LineSegment StartX=-49.19 StartY=17.25 StartZ=0 EndX=-1.5 EndY=17.25 EndZ=0
    g43: LineSegment StartX=-49.19 StartY=14.25 StartZ=0 EndX=-1.5 EndY=14.25 EndZ=0
    g44: LineSegment StartX=-49.19 StartY=11.5 StartZ=0 EndX=-1.5 EndY=11.5 EndZ=0
    g45: LineSegment StartX=-49.19 StartY=8.5 StartZ=0 EndX=-1.5 EndY=8.5 EndZ=0
    g46: LineSegment StartX=-49.19 StartY=5.75 StartZ=0 EndX=-1.5 EndY=5.75 EndZ=0
    g47: LineSegment StartX=-49.19 StartY=2.75 StartZ=0 EndX=-1.5 EndY=2.75 EndZ=0
  constraints (120):
    c: Vertical(g0)
    c: Distance(g0) = 3
    c: Block(g0)
    c: Vertical(g1)
    c: Distance(g1) = 3
    c: Vertical(g2)
    c: Equal(g0,g2) = 3
    c: Block(g2)
    c: Vertical(g3)
    c: Equal(g1,g3) = 3
    c: Vertical(g4)
    c: Equal(g0,g4) = 3
    c: Block(g4)
    c: Vertical(g5)
    c: Equal(g1,g5) = 3
    c: Vertical(g6)
    c: Equal(g0,g6) = 3
    c: Block(g6)
    c: Vertical(g7)
    c: Equal(g1,g7) = 3
    c: Vertical(g8)
    c: Equal(g0,g8) = 3
    c: Block(g8)
    c: Vertical(g9)
    c: Equal(g1,g9) = 3
    c: Vertical(g10)
    c: Equal(g0,g10) = 3
    c: Block(g10)
    c: Vertical(g11)
    c: Equal(g1,g11) = 3
    c: Block(g12)
    c: Block(g13)
    c: Block(g14)
    c: Block(g15)
    c: Block(g16)
    c: Block(g17)
    c: Block(g18)
    c: Block(g19)
    c: Block(g20)
    c: Block(g21)
    c: Block(g22)
    c: Block(g23)
    c: Block(g11)
    c: Block(g9)
    c: Block(g7)
    c: Block(g5)
    c: Block(g3)
    c: Block(g1)
    c: Coincident(g24,g0)
    c: Coincident(g24,g12)
    c: Horizontal(g24)
    c: Coincident(g25,g0)
    c: Coincident(g25,g12)
    c: Horizontal(g25)
    c: Coincident(g26,g1)
    c: Coincident(g26,g13)
    c: Horizontal(g26)
    c: Coincident(g27,g1)
    c: Coincident(g27,g13)
    c: Horizontal(g27)
    c: Coincident(g28,g2)
    c: Coincident(g28,g14)
    c: Horizontal(g28)
    c: Coincident(g29,g2)
    c: Coincident(g29,g14)
    c: Horizontal(g29)
    c: Coincident(g30,g3)
    c: Coincident(g30,g15)
    c: Horizontal(g30)
    c: Coincident(g31,g3)
    c: Coincident(g31,g15)
    c: Horizontal(g31)
    c: Coincident(g32,g4)
    c: Coincident(g32,g16)
    c: Horizontal(g32)
    c: Coincident(g33,g4)
    c: Coincident(g33,g16)
    c: Horizontal(g33)
    c: Coincident(g34,g5)
    c: Coincident(g34,g17)
    c: Horizontal(g34)
    c: Coincident(g35,g5)
    c: Coincident(g35,g17)
    c: Horizontal(g35)
    c: Coincident(g36,g6)
    c: Coincident(g36,g19)
    c: Horizontal(g36)
    c: Coincident(g37,g6)
    c: Coincident(g37,g19)
    c: Horizontal(g37)
    c: Coincident(g38,g7)
    c: Coincident(g38,g18)
    c: Horizontal(g38)
    c: Coincident(g39,g7)
    c: Coincident(g39,g18)
    c: Horizontal(g39)
    c: Coincident(g40,g8)
    c: Coincident(g40,g20)
    c: Horizontal(g40)
    c: Coincident(g41,g8)
    c: Coincident(g41,g20)
    c: Horizontal(g41)
    c: Coincident(g42,g9)
    c: Coincident(g42,g23)
    c: Horizontal(g42)
    c: Coincident(g43,g9)
    c: Coincident(g43,g23)
    c: Horizontal(g43)
    c: Coincident(g44,g10)
    c: Coincident(g44,g22)
    c: Horizontal(g44)
    c: Coincident(g45,g10)
    c: Coincident(g45,g22)
    c: Horizontal(g45)
    c: Coincident(g46,g11)
    c: Coincident(g46,g21)
    c: Horizontal(g46)
    c: Coincident(g47,g11)
    c: Coincident(g47,g21)
    c: Horizontal(g47)
FEATURE [Sketcher::SketchObject] Sketch031
  FullyConstrained = true
  Placement = pos=(117,19,0) rot=(0.57735,0.57735,0.57735;2.0944rad)
  sketch-geometry (24):
    g0: ArcOfCircle CenterX=-49.19 CenterY=67.75 CenterZ=0 NormalX=0 NormalY=0 NormalZ=1 AngleXU=0 Radius=1.5 StartAngle=1.5708 EndAngle=4.71239
    g1: ArcOfCircle CenterX=-49.19 CenterY=62 CenterZ=0 NormalX=0 NormalY=0 NormalZ=1 AngleXU=0 Radius=1.5 StartAngle=1.5708 EndAngle=4.71239
    g2: ArcOfCircle CenterX=-49.19 CenterY=56.25 CenterZ=0 NormalX=0 NormalY=0 NormalZ=1 AngleXU=0 Radius=1.5 StartAngle=1.5708 EndAngle=4.71239
    g3: ArcOfCircle CenterX=-49.19 CenterY=50.5 CenterZ=0 NormalX=0 NormalY=0 NormalZ=1 AngleXU=0 Radius=1.5 StartAngle=1.5708 EndAngle=4.71239
    g4: ArcOfCircle CenterX=-49.19 CenterY=44.75 CenterZ=0 NormalX=0 NormalY=0 NormalZ=1 AngleXU=0 Radius=1.5 StartAngle=1.5708 EndAngle=4.71239
    g5: ArcOfCircle CenterX=-49.19 CenterY=39 CenterZ=0 NormalX=0 NormalY=0 NormalZ=1 AngleXU=0 Radius=1.5 StartAngle=1.5708 EndAngle=4.71239
    g6: ArcOfCircle CenterX=-49.19 CenterY=33 CenterZ=0 NormalX=0 NormalY=0 NormalZ=1 AngleXU=0 Radius=1.5 StartAngle=1.5708 EndAngle=4.71239
    g7: ArcOfCircle CenterX=-49.19 CenterY=27.25 CenterZ=0 NormalX=0 NormalY=0 NormalZ=1 AngleXU=0 Radius=1.5 StartAngle=1.5708 EndAngle=4.71239
    g8: ArcOfCircle CenterX=-49.19 CenterY=21.5 CenterZ=0 NormalX=0 NormalY=0 NormalZ=1 AngleXU=0 Radius=1.5 StartAngle=1.5708 EndAngle=4.71239
    g9: ArcOfCircle CenterX=-49.19 CenterY=15.75 CenterZ=0 NormalX=0 NormalY=0 NormalZ=1 AngleXU=0 Radius=1.5 StartAngle=1.5708 EndAngle=4.71239
    g10: ArcOfCircle CenterX=-49.19 CenterY=10 CenterZ=0 NormalX=0 NormalY=0 NormalZ=1 AngleXU=0 Radius=1.5 StartAngle=1.5708 EndAngle=4.71239
    g11: ArcOfCircle CenterX=-49.19 CenterY=4.25 CenterZ=0 NormalX=0 NormalY=0 NormalZ=1 AngleXU=0 Radius=1.5 StartAngle=1.5708 EndAngle=4.71239
    g12: LineSegment StartX=-49.19 StartY=69.25 StartZ=0 EndX=-49.19 EndY=66.25 EndZ=0
    g13: LineSegment StartX=-49.19 StartY=63.5 StartZ=0 EndX=-49.19 EndY=60.5 EndZ=0
    g14: LineSegment StartX=-49.19 StartY=57.75 StartZ=0 EndX=-49.19 EndY=54.75 EndZ=0
    g15: LineSegment StartX=-49.19 StartY=52 StartZ=0 EndX=-49.19 EndY=49 EndZ=0
    g16: LineSegment StartX=-49.19 StartY=46.25 StartZ=0 EndX=-49.19 EndY=43.25 EndZ=0
    g17: LineSegment StartX=-49.19 StartY=40.5 StartZ=0 EndX=-49.19 EndY=37.5 EndZ=0
    g18: LineSegment StartX=-49.19 StartY=34.5 StartZ=0 EndX=-49.19 EndY=31.5 EndZ=0
    g19: LineSegment StartX=-49.19 StartY=28.75 StartZ=0 EndX=-49.19 EndY=25.75 EndZ=0
    g20: LineSegment StartX=-49.19 StartY=23 StartZ=0 EndX=-49.19 EndY=20 EndZ=0
    g21: LineSegment StartX=-49.19 StartY=17.25 StartZ=0 EndX=-49.19 EndY=14.25 EndZ=0
    g22: LineSegment StartX=-49.19 StartY=11.5 StartZ=0 EndX=-49.19 EndY=8.5 EndZ=0
    g23: LineSegment StartX=-49.19 StartY=5.75 StartZ=0 EndX=-49.19 EndY=2.75 EndZ=0
  constraints (48):
    c: Block(g0)
    c: Block(g1)
    c: Block(g2)
    c: Block(g3)
    c: Block(g4)
    c: Block(g5)
    c: Block(g6)
    c: Block(g7)
    c: Block(g8)
    c: Block(g9)
    c: Block(g10)
    c: Block(g11)
    c: Coincident(g12,g0)
    c: Coincident(g12,g0)
    c: Vertical(g12)
    c: Vertical(g13)
    c: Coincident(g13,g1)
    c: Vertical(g14)
    c: Coincident(g14,g2)
    c: Vertical(g15)
    c: Coincident(g15,g3)
    c: Vertical(g16)
    c: Coincident(g16,g4)
    c: Vertical(g17)
    c: Coincident(g17,g5)
    c: Vertical(g18)
    c: Coincident(g18,g6)
    c: Vertical(g19)
    c: Coincident(g19,g7)
    c: Vertical(g20)
    c: Coincident(g20,g8)
    c: Vertical(g21)
    c: Coincident(g21,g9)
    c: Vertical(g22)
    c: Coincident(g22,g10)
    c: Vertical(g23)
    c: Coincident(g23,g11)
    c: Block(g23)
    c: Block(g22)
    c: Block(g21)
    c: Block(g20)
    c: Block(g13)
    c: Block(g14)
    c: Block(g15)
    c: Block(g16)
    c: Block(g17)
    c: Block(g18)
    c: Block(g19)
FEATURE [Part::Extrusion] Extrude022
  Base = -> Sketch030
  Dir = (1,-2e-16,2e-16)
  DirMode = 2
  FaceMakerClass = Part::FaceMakerBullseye
  LengthFwd = 19
  LengthRev = 0
  Placement = pos=(-19,0,0) rot=(0,0,1;0rad)
  Solid = true
  Symmetric = false
FEATURE [Part::Fillet] Fillet022
  Base = -> Extrude022
  Edges = 24 edges r=1.49: [Edge6,Edge11,Edge18,Edge23,Edge30,Edge35,Edge42,Edge47,Edge54,Edge59,Edge66,Edge71,Edge78,Edge83,Edge90,Edge95,Edge102,Edge107,Edge114,Edge119,Edge126,Edge131,Edge138,Edge143]
FEATURE [Part::Cut] Cut020  label="top010"
  Base = -> Cut019
  Tool = -> Fillet022
FEATURE [Sketcher::SketchObject] Sketch032
  FullyConstrained = true
  Placement = pos=(117,19,0) rot=(0.57735,0.57735,0.57735;2.0944rad)
  sketch-geometry (48):
    g0: LineSegment StartX=-49.19 StartY=69.25 StartZ=0 EndX=-49.19 EndY=66.25 EndZ=0
    g1: LineSegment StartX=-49.19 StartY=63.5 StartZ=0 EndX=-49.19 EndY=60.5 EndZ=0
    g2: LineSegment StartX=-49.19 StartY=57.75 StartZ=0 EndX=-49.19 EndY=54.75 EndZ=0
    g3: LineSegment StartX=-49.19 StartY=52 StartZ=0 EndX=-49.19 EndY=49 EndZ=0
    g4: LineSegment StartX=-49.19 StartY=46.25 StartZ=0 EndX=-49.19 EndY=43.25 EndZ=0
    g5: LineSegment StartX=-49.19 StartY=40.5 StartZ=0 EndX=-49.19 EndY=37.5 EndZ=0
    g6: LineSegment StartX=-49.19 StartY=34.5 StartZ=0 EndX=-49.19 EndY=31.5 EndZ=0
    g7: LineSegment StartX=-49.19 StartY=28.75 StartZ=0 EndX=-49.19 EndY=25.75 EndZ=0
    g8: LineSegment StartX=-49.19 StartY=23 StartZ=0 EndX=-49.19 EndY=20 EndZ=0
    g9: LineSegment StartX=-49.19 StartY=17.25 StartZ=0 EndX=-49.19 EndY=14.25 EndZ=0
    g10: LineSegment StartX=-49.19 StartY=11.5 StartZ=0 EndX=-49.19 EndY=8.5 EndZ=0
    g11: LineSegment StartX=-49.19 StartY=5.75 StartZ=0 EndX=-49.19 EndY=2.75 EndZ=0
    g12: ArcOfCircle CenterX=-1.5 CenterY=67.75 CenterZ=0 NormalX=0 NormalY=0 NormalZ=1 AngleXU=0 Radius=1.5 StartAngle=4.71239 EndAngle=7.85398
    g13: ArcOfCircle CenterX=-1.5 CenterY=62 CenterZ=0 NormalX=0 NormalY=0 NormalZ=1 AngleXU=0 Radius=1.5 StartAngle=4.71239 EndAngle=7.85398
    g14: ArcOfCircle CenterX=-1.5 CenterY=56.25 CenterZ=0 NormalX=0 NormalY=0 NormalZ=1 AngleXU=0 Radius=1.5 StartAngle=4.71239 EndAngle=7.85398
    g15: ArcOfCircle CenterX=-11.49 CenterY=50.5 CenterZ=0 NormalX=0 NormalY=0 NormalZ=1 AngleXU=0 Radius=1.5 StartAngle=4.71239 EndAngle=7.85398
    g16: ArcOfCircle CenterX=-16.28 CenterY=44.75 CenterZ=0 NormalX=0 NormalY=0 NormalZ=1 AngleXU=0 Radius=1.5 StartAngle=4.71239 EndAngle=7.85398
    g17: ArcOfCircle CenterX=-18.2337 CenterY=39 CenterZ=0 NormalX=0 NormalY=0 NormalZ=1 AngleXU=0 Radius=1.5 StartAngle=4.71485 EndAngle=7.85398
    g18: ArcOfCircle CenterX=-16.2837 CenterY=27.25 CenterZ=0 NormalX=0 NormalY=0 NormalZ=1 AngleXU=0 Radius=1.5 StartAngle=4.71485 EndAngle=7.85398
    g19: ArcOfCircle CenterX=-18.2337 CenterY=33 CenterZ=0 NormalX=0 NormalY=0 NormalZ=1 AngleXU=0 Radius=1.5 StartAngle=4.71485 EndAngle=7.85398
    g20: ArcOfCircle CenterX=-11.49 CenterY=21.5 CenterZ=0 NormalX=0 NormalY=0 NormalZ=1 AngleXU=0 Radius=1.5 StartAngle=4.71239 EndAngle=7.85398
    g21: ArcOfCircle CenterX=-1.5 CenterY=4.25 CenterZ=0 NormalX=0 NormalY=0 NormalZ=1 AngleXU=0 Radius=1.5 StartAngle=4.71239 EndAngle=7.85398
    g22: ArcOfCircle CenterX=-1.5 CenterY=10 CenterZ=0 NormalX=0 NormalY=0 NormalZ=1 AngleXU=0 Radius=1.5 StartAngle=4.71239 EndAngle=7.85398
    g23: ArcOfCircle CenterX=-1.5 CenterY=15.75 CenterZ=0 NormalX=0 NormalY=0 NormalZ=1 AngleXU=0 Radius=1.5 StartAngle=4.71239 EndAngle=7.85398
    g24: LineSegment StartX=-49.19 StartY=69.25 StartZ=0 EndX=-1.5 EndY=69.25 EndZ=0
    g25: LineSegment StartX=-49.19 StartY=66.25 StartZ=0 EndX=-1.5 EndY=66.25 EndZ=0
    g26: LineSegment StartX=-49.19 StartY=63.5 StartZ=0 EndX=-1.5 EndY=63.5 EndZ=0
    g27: LineSegment StartX=-49.19 StartY=60.5 StartZ=0 EndX=-1.5 EndY=60.5 EndZ=0
    g28: LineSegment StartX=-49.19 StartY=57.75 StartZ=0 EndX=-1.5 EndY=57.75 EndZ=0
    g29: LineSegment StartX=-49.19 StartY=54.75 StartZ=0 EndX=-1.5 EndY=54.75 EndZ=0
    g30: LineSegment StartX=-49.19 StartY=52 StartZ=0 EndX=-11.49 EndY=52 EndZ=0
    g31: LineSegment StartX=-49.19 StartY=49 StartZ=0 EndX=-11.49 EndY=49 EndZ=0
    g32: LineSegment StartX=-49.19 StartY=46.25 StartZ=0 EndX=-16.28 EndY=46.25 EndZ=0
    g33: LineSegment StartX=-49.19 StartY=43.25 StartZ=0 EndX=-16.28 EndY=43.25 EndZ=0
    g34: LineSegment StartX=-49.19 StartY=40.5 StartZ=0 EndX=-18.2337 EndY=40.5 EndZ=0
    g35: LineSegment StartX=-49.19 StartY=37.5 StartZ=0 EndX=-18.23 EndY=37.5 EndZ=0
    g36: LineSegment StartX=-49.19 StartY=34.5 StartZ=0 EndX=-18.2337 EndY=34.5 EndZ=0
    g37: LineSegment StartX=-49.19 StartY=31.5 StartZ=0 EndX=-18.23 EndY=31.5 EndZ=0
    g38: LineSegment StartX=-49.19 StartY=28.75 StartZ=0 EndX=-16.2837 EndY=28.75 EndZ=0
    g39: LineSegment StartX=-49.19 StartY=25.75 StartZ=0 EndX=-16.28 EndY=25.75 EndZ=0
    g40: LineSegment StartX=-49.19 StartY=23 StartZ=0 EndX=-11.49 EndY=23 EndZ=0
    g41: LineSegment StartX=-49.19 StartY=20 StartZ=0 EndX=-11.49 EndY=20 EndZ=0
    g42: LineSegment StartX=-49.19 StartY=17.25 StartZ=0 EndX=-1.5 EndY=17.25 EndZ=0
    g43: LineSegment StartX=-49.19 StartY=14.25 StartZ=0 EndX=-1.5 EndY=14.25 EndZ=0
    g44: LineSegment StartX=-49.19 StartY=11.5 StartZ=0 EndX=-1.5 EndY=11.5 EndZ=0
    g45: LineSegment StartX=-49.19 StartY=8.5 StartZ=0 EndX=-1.5 EndY=8.5 EndZ=0
    g46: LineSegment StartX=-49.19 StartY=5.75 StartZ=0 EndX=-1.5 EndY=5.75 EndZ=0
    g47: LineSegment StartX=-49.19 StartY=2.75 StartZ=0 EndX=-1.5 EndY=2.75 EndZ=0
  constraints (120):
    c: Vertical(g0)
    c: Distance(g0) = 3
    c: Block(g0)
    c: Vertical(g1)
    c: Distance(g1) = 3
    c: Vertical(g2)
    c: Equal(g0,g2) = 3
    c: Block(g2)
    c: Vertical(g3)
    c: Equal(g1,g3) = 3
    c: Vertical(g4)
    c: Equal(g0,g4) = 3
    c: Block(g4)
    c: Vertical(g5)
    c: Equal(g1,g5) = 3
    c: Vertical(g6)
    c: Equal(g0,g6) = 3
    c: Block(g6)
    c: Vertical(g7)
    c: Equal(g1,g7) = 3
    c: Vertical(g8)
    c: Equal(g0,g8) = 3
    c: Block(g8)
    c: Vertical(g9)
    c: Equal(g1,g9) = 3
    c: Vertical(g10)
    c: Equal(g0,g10) = 3
    c: Block(g10)
    c: Vertical(g11)
    c: Equal(g1,g11) = 3
    c: Block(g12)
    c: Block(g13)
    c: Block(g14)
    c: Block(g15)
    c: Block(g16)
    c: Block(g17)
    c: Block(g18)
    c: Block(g19)
    c: Block(g20)
    c: Block(g21)
    c: Block(g22)
    c: Block(g23)
    c: Block(g11)
    c: Block(g9)
    c: Block(g7)
    c: Block(g5)
    c: Block(g3)
    c: Block(g1)
    c: Coincident(g24,g0)
    c: Coincident(g24,g12)
    c: Horizontal(g24)
    c: Coincident(g25,g0)
    c: Coincident(g25,g12)
    c: Horizontal(g25)
    c: Coincident(g26,g1)
    c: Coincident(g26,g13)
    c: Horizontal(g26)
    c: Coincident(g27,g1)
    c: Coincident(g27,g13)
    c: Horizontal(g27)
    c: Coincident(g28,g2)
    c: Coincident(g28,g14)
    c: Horizontal(g28)
    c: Coincident(g29,g2)
    c: Coincident(g29,g14)
    c: Horizontal(g29)
    c: Coincident(g30,g3)
    c: Coincident(g30,g15)
    c: Horizontal(g30)
    c: Coincident(g31,g3)
    c: Coincident(g31,g15)
    c: Horizontal(g31)
    c: Coincident(g32,g4)
    c: Coincident(g32,g16)
    c: Horizontal(g32)
    c: Coincident(g33,g4)
    c: Coincident(g33,g16)
    c: Horizontal(g33)
    c: Coincident(g34,g5)
    c: Coincident(g34,g17)
    c: Horizontal(g34)
    c: Coincident(g35,g5)
    c: Coincident(g35,g17)
    c: Horizontal(g35)
    c: Coincident(g36,g6)
    c: Coincident(g36,g19)
    c: Horizontal(g36)
    c: Coincident(g37,g6)
    c: Coincident(g37,g19)
    c: Horizontal(g37)
    c: Coincident(g38,g7)
    c: Coincident(g38,g18)
    c: Horizontal(g38)
    c: Coincident(g39,g7)
    c: Coincident(g39,g18)
    c: Horizontal(g39)
    c: Coincident(g40,g8)
    c: Coincident(g40,g20)
    c: Horizontal(g40)
    c: Coincident(g41,g8)
    c: Coincident(g41,g20)
    c: Horizontal(g41)
    c: Coincident(g42,g9)
    c: Coincident(g42,g23)
    c: Horizontal(g42)
    c: Coincident(g43,g9)
    c: Coincident(g43,g23)
    c: Horizontal(g43)
    c: Coincident(g44,g10)
    c: Coincident(g44,g22)
    c: Horizontal(g44)
    c: Coincident(g45,g10)
    c: Coincident(g45,g22)
    c: Horizontal(g45)
    c: Coincident(g46,g11)
    c: Coincident(g46,g21)
    c: Horizontal(g46)
    c: Coincident(g47,g11)
    c: Coincident(g47,g21)
    c: Horizontal(g47)
FEATURE [Part::Extrusion] Extrude023
  Base = -> Sketch032
  Dir = (1,-2e-16,2e-16)
  DirMode = 2
  FaceMakerClass = Part::FaceMakerBullseye
  LengthFwd = 19
  LengthRev = 0
  Placement = pos=(-19,0,0) rot=(0,0,1;0rad)
  Solid = true
  Symmetric = false
FEATURE [Part::Fillet] Fillet023
  Base = -> Extrude023
  Edges = <same value as first occurrence — deduplicated (x6 in doc)>
  Placement = pos=(0,0.05,0) rot=(0,0,1;0rad)
FEATURE [Part::Cut] Cut014  label="bottom003"
  Base = -> Cut007
  Tool = -> Fusion047
FEATURE [Part::Cut] Cut021  label="bottom004"
  Base = -> Cut014
  Tool = -> Fillet023
FEATURE [Sketcher::SketchObject] Sketch033
  FullyConstrained = true
  Placement = pos=(117,19,0) rot=(0.57735,0.57735,0.57735;2.0944rad)
  sketch-geometry (8):
    g0: LineSegment StartX=-49.19 StartY=69.25 StartZ=0 EndX=-49.19 EndY=66.25 EndZ=0
    g1: LineSegment StartX=-49.19 StartY=5.75 StartZ=0 EndX=-49.19 EndY=2.75 EndZ=0
    g2: ArcOfCircle CenterX=-1.5 CenterY=67.75 CenterZ=0 NormalX=0 NormalY=0 NormalZ=1 AngleXU=0 Radius=1.5 StartAngle=4.71239 EndAngle=7.85398
    g3: ArcOfCircle CenterX=-1.5 CenterY=4.25 CenterZ=0 NormalX=0 NormalY=0 NormalZ=1 AngleXU=0 Radius=1.5 StartAngle=4.71239 EndAngle=7.85398
    g4: LineSegment StartX=-49.19 StartY=69.25 StartZ=0 EndX=-1.5 EndY=69.25 EndZ=0
    g5: LineSegment StartX=-49.19 StartY=66.25 StartZ=0 EndX=-1.5 EndY=66.25 EndZ=0
    g6: LineSegment StartX=-49.19 StartY=5.75 StartZ=0 EndX=-1.5 EndY=5.75 EndZ=0
    g7: LineSegment StartX=-49.19 StartY=2.75 StartZ=0 EndX=-1.5 EndY=2.75 EndZ=0
  constraints (19):
    c: Vertical(g0)
    c: Distance(g0) = 3
    c: Block(g0)
    c: Vertical(g1)
    c: Block(g2)
    c: Block(g3)
    c: Block(g1)
    c: Coincident(g4,g0)
    c: Coincident(g4,g2)
    c: Horizontal(g4)
    c: Coincident(g5,g0)
    c: Coincident(g5,g2)
    c: Horizontal(g5)
    c: Coincident(g6,g1)
    c: Coincident(g6,g3)
    c: Horizontal(g6)
    c: Coincident(g7,g1)
    c: Coincident(g7,g3)
    c: Horizontal(g7)
FEATURE [Sketcher::SketchObject] Sketch034
  FullyConstrained = true
  Placement = pos=(117,19,0) rot=(0.57735,0.57735,0.57735;2.0944rad)
  sketch-geometry (8):
    g0: LineSegment StartX=-49.19 StartY=63.5 StartZ=0 EndX=-49.19 EndY=60.5 EndZ=0
    g1: LineSegment StartX=-49.19 StartY=11.5 StartZ=0 EndX=-49.19 EndY=8.5 EndZ=0
    g2: ArcOfCircle CenterX=-1.5 CenterY=62 CenterZ=0 NormalX=0 NormalY=0 NormalZ=1 AngleXU=0 Radius=1.5 StartAngle=4.71239 EndAngle=7.85398
    g3: ArcOfCircle CenterX=-1.5 CenterY=10 CenterZ=0 NormalX=0 NormalY=0 NormalZ=1 AngleXU=0 Radius=1.5 StartAngle=4.71239 EndAngle=7.85398
    g4: LineSegment StartX=-49.19 StartY=63.5 StartZ=0 EndX=-1.5 EndY=63.5 EndZ=0
    g5: LineSegment StartX=-49.19 StartY=60.5 StartZ=0 EndX=-1.5 EndY=60.5 EndZ=0
    g6: LineSegment StartX=-49.19 StartY=11.5 StartZ=0 EndX=-1.5 EndY=11.5 EndZ=0
    g7: LineSegment StartX=-49.19 StartY=8.5 StartZ=0 EndX=-1.5 EndY=8.5 EndZ=0
  constraints (19):
    c: Vertical(g0)
    c: Distance(g0) = 3
    c: Vertical(g1)
    c: Block(g1)
    c: Block(g2)
    c: Block(g3)
    c: Block(g0)
    c: Coincident(g4,g0)
    c: Coincident(g4,g2)
    c: Horizontal(g4)
    c: Coincident(g5,g0)
    c: Coincident(g5,g2)
    c: Horizontal(g5)
    c: Coincident(g6,g1)
    c: Coincident(g6,g3)
    c: Horizontal(g6)
    c: Coincident(g7,g1)
    c: Coincident(g7,g3)
    c: Horizontal(g7)
FEATURE [Part::Extrusion] Extrude024
  Base = -> Sketch033
  Dir = (1,0,0)
  DirMode = 2
  FaceMakerClass = Part::FaceMakerBullseye
  LengthFwd = 10
  LengthRev = 0
  Solid = true
  Symmetric = false
FEATURE [Part::Extrusion] Extrude025
  Base = -> Sketch034
  Dir = (1,0,0)
  DirMode = 2
  FaceMakerClass = Part::FaceMakerBullseye
  LengthFwd = 10
  LengthRev = 0
  Solid = true
  Symmetric = false
FEATURE [Part::Fillet] Fillet024  label="removeFromtMoreFrontCaseScrewRetainers"
  Base = -> Extrude024
  Edges = 4 edges r=1.49: [Edge6,Edge11,Edge18,Edge23]
  Placement = pos=(-11,0,0) rot=(0,0,1;0rad)
FEATURE [Part::Fillet] Fillet025  label="removeFromtMoreFrontCaseScrewRetainers001"
  Base = -> Extrude025
  Edges = 4 edges r=1.49: [Edge6,Edge11,Edge18,Edge23]
  Placement = pos=(-19,0,0) rot=(0,0,1;0rad)
FEATURE [Part::Cut] Cut022
  Base = -> Cut015
  Tool = -> Fillet025
FEATURE [Part::Cut] Cut023  label="screwRetainers"
  Base = -> Cut022
  Tool = -> Fillet024
FEATURE [Part::MultiFuse] Fusion056  label="bottom005"
  Shapes = -> [Fusion044,Cut021]
FEATURE [Part::MultiFuse] Fusion057  label="casePillars001"
  Shapes = -> [Cut016,Fusion052]
FEATURE [Part::MultiFuse] Fusion058  label="bottom006"
  Shapes = -> [Fusion056,Cut023]
FEATURE [Part::MultiFuse] Fusion059  label="bottom007"
  Shapes = -> [Fusion058,Fillet005]
FEATURE [Part::MultiFuse] Fusion060  label="bottom008"
  Shapes = -> [Fusion059,Fusion]
FEATURE [Part::MultiFuse] Fusion061  label="top011"
  Shapes = -> [Cut006,Cut020]
FEATURE [Part::MultiFuse] Fusion062  label="top012"
  Shapes = -> [Fusion057,Fusion061]
FEATURE [Sketcher::SketchObject] Sketch035  label="topSketch007"
  FullyConstrained = true
  sketch-geometry (6):
    g0: LineSegment StartX=19 StartY=38 StartZ=0 EndX=117 EndY=38 EndZ=0
    g1: ArcOfCircle CenterX=19 CenterY=19 CenterZ=0 NormalX=0 NormalY=0 NormalZ=1 AngleXU=0 Radius=19 StartAngle=1.5708 EndAngle=3.14159
    g2: LineSegment StartX=117 StartY=38 StartZ=0 EndX=117 EndY=19 EndZ=0
    g3: LineSegment StartX=98 StartY=1.0161e-12 StartZ=0 EndX=5.22862e-06 EndY=1.0161e-12 EndZ=0
    g4: LineSegment StartX=5.22862e-06 StartY=19 StartZ=0 EndX=5.22862e-06 EndY=1.0161e-12 EndZ=0
    g5: ArcOfCircle CenterX=98 CenterY=19 CenterZ=0 NormalX=0 NormalY=0 NormalZ=1 AngleXU=0 Radius=19 StartAngle=4.71239 EndAngle=6.28319
  constraints (16):
    c: Horizontal(g0)
    c: Distance(g0) = 98
    c: Coincident(g1,g0)
    c: Block(g1)
    c: Coincident(g2,g0)
    c: Vertical(g2)
    c: Distance(g2) = 19
    c: Horizontal(g3)
    c: Coincident(g4,g1)
    c: Vertical(g4)
    c: Coincident(g3,g4)
    c: Block(g3)
    c: Coincident(g5,g2)
    c: Coincident(g5,g3)
    c: Block(g0)
    c: Block(g5)
FEATURE [Part::Extrusion] Extrude026  label="sideA001"
  Base = -> Sketch035
  Dir = (0,0,1)
  DirMode = 2
  FaceMakerClass = Part::FaceMakerBullseye
  LengthFwd = 3
  LengthRev = 0
  Placement = pos=(0,0,-2.7) rot=(0,0,1;0rad)
  Solid = true
  Symmetric = false
FEATURE [Sketcher::SketchObject] Sketch036  label="topSketch008"
  FullyConstrained = true
  sketch-geometry (6):
    g0: LineSegment StartX=19 StartY=38 StartZ=0 EndX=117 EndY=38 EndZ=0
    g1: ArcOfCircle CenterX=19 CenterY=19 CenterZ=0 NormalX=0 NormalY=0 NormalZ=1 AngleXU=0 Radius=19 StartAngle=1.5708 EndAngle=3.14159
    g2: LineSegment StartX=117 StartY=38 StartZ=0 EndX=117 EndY=19 EndZ=0
    g3: LineSegment StartX=98 StartY=1.0161e-12 StartZ=0 EndX=5.22862e-06 EndY=1.0161e-12 EndZ=0
    g4: LineSegment StartX=5.22862e-06 StartY=19 StartZ=0 EndX=5.22862e-06 EndY=1.0161e-12 EndZ=0
    g5: ArcOfCircle CenterX=98 CenterY=19 CenterZ=0 NormalX=0 NormalY=0 NormalZ=1 AngleXU=0 Radius=19 StartAngle=4.71239 EndAngle=6.28319
  constraints (16):
    c: Horizontal(g0)
    c: Distance(g0) = 98
    c: Coincident(g1,g0)
    c: Block(g1)
    c: Coincident(g2,g0)
    c: Vertical(g2)
    c: Distance(g2) = 19
    c: Horizontal(g3)
    c: Coincident(g4,g1)
    c: Vertical(g4)
    c: Coincident(g3,g4)
    c: Block(g3)
    c: Coincident(g5,g2)
    c: Coincident(g5,g3)
    c: Block(g0)
    c: Block(g5)
FEATURE [Part::Extrusion] Extrude027  label="sideB001"
  Base = -> Sketch036
  Dir = (0,0,1)
  DirMode = 2
  FaceMakerClass = Part::FaceMakerBullseye
  LengthFwd = 3
  LengthRev = 0
  Placement = pos=(0,0,71.7) rot=(0,0,1;0rad)
  Solid = true
  Symmetric = false
FEATURE [Part::MultiFuse] Fusion064  label="removeFromBottom"
  Shapes = -> [Extrude026,Extrude027]
FEATURE [Part::Cut] Cut024  label="bottom009"
  Base = -> Fusion060
  Tool = -> Fusion064
FEATURE [Sketcher::SketchObject] Sketch037  label="topSketch009"
  FullyConstrained = true
  sketch-geometry (8):
    g0: ArcOfCircle CenterX=19 CenterY=19.1201 CenterZ=0 NormalX=0 NormalY=0 NormalZ=1 AngleXU=0 Radius=18.8799 StartAngle=1.5708 EndAngle=3.14793
    g1: LineSegment StartX=0.120501 StartY=19.0004 StartZ=0 EndX=0.120501 EndY=0.000382114 EndZ=0
    g2: LineSegment StartX=19 StartY=38 StartZ=0 EndX=124 EndY=38 EndZ=0
    g3: LineSegment StartX=0.120501 StartY=0.000382114 StartZ=0 EndX=105.121 EndY=0.000382114 EndZ=0
    g4: LineSegment StartX=124 StartY=38 StartZ=0 EndX=125.616 EndY=38 EndZ=0
    g5: LineSegment StartX=105.121 StartY=0.000382114 StartZ=0 EndX=106.736 EndY=0.000382114 EndZ=0
    g6: ArcOfCircle CenterX=106.616 CenterY=19 CenterZ=0 NormalX=0 NormalY=0 NormalZ=1 AngleXU=0 Radius=19 StartAngle=4.71873 EndAngle=6.28319
    g7: LineSegment StartX=125.616 StartY=38 StartZ=0 EndX=125.616 EndY=19 EndZ=0
  constraints (21):
    c: Block(g0)
    c: Coincident(g1,g0)
    c: Vertical(g1)
    c: Horizontal(g2)
    c: Distance(g2) = 105
    c: Coincident(g2,g0)
    c: Distance(g1) = 19
    c: Coincident(g3,g1)
    c: Horizontal(g3)
    c: Distance(g3) = 105
    c: Coincident(g4,g2)
    c: Horizontal(g4)
    c: Distance(g4) = 1.61553
    c: Horizontal(g5)
    c: Equal(g4,g5) = 1.61553
    c: Coincident(g5,g3)
    c: Block(g6)
    c: Coincident(g6,g5)
    c: Coincident(g7,g4)
    c: Coincident(g7,g6)
    c: Vertical(g7)
FEATURE [Part::Extrusion] Extrude028  label="sideB"
  Base = -> Sketch037
  Dir = (0,0,1)
  DirMode = 2
  FaceMakerClass = Part::FaceMakerBullseye
  LengthFwd = 3
  LengthRev = 0
  Placement = pos=(0,0,72) rot=(0,0,1;0rad)
  Solid = true
  Symmetric = false
FEATURE [Sketcher::SketchObject] Sketch038  label="topSketch010"
  FullyConstrained = true
  sketch-geometry (22):
    g0: LineSegment StartX=5.21097e-06 StartY=3 StartZ=0 EndX=5.21097e-06 EndY=19 EndZ=0
    g1: ArcOfCircle CenterX=19 CenterY=19 CenterZ=0 NormalX=0 NormalY=0 NormalZ=1 AngleXU=0 Radius=19 StartAngle=1.5708 EndAngle=3.14159
    g2: ArcOfCircle CenterX=19 CenterY=19 CenterZ=0 NormalX=0 NormalY=0 NormalZ=1 AngleXU=0 Radius=16 StartAngle=1.5708 EndAngle=3.14159
    g3: LineSegment StartX=114 StartY=35 StartZ=0 EndX=19 EndY=35 EndZ=0
    g4: LineSegment StartX=5.21097e-06 StartY=3 StartZ=0 EndX=5.21097e-06 EndY=0 EndZ=0
    g5: LineSegment StartX=3 StartY=0 StartZ=0 EndX=5.21097e-06 EndY=0 EndZ=0
    g6: LineSegment StartX=3 StartY=19 StartZ=0 EndX=3 EndY=0 EndZ=0
    g7: LineSegment StartX=19 StartY=38 StartZ=0 EndX=124 EndY=38 EndZ=0
    g8: Circle CenterX=119 CenterY=35 CenterZ=0 NormalX=0 NormalY=0 NormalZ=1 AngleXU=0 Radius=1
    g9: Circle CenterX=121 CenterY=35 CenterZ=0 NormalX=0 NormalY=0 NormalZ=1 AngleXU=0 Radius=1
    g10: Circle CenterX=121 CenterY=33 CenterZ=0 NormalX=0 NormalY=0 NormalZ=1 AngleXU=0 Radius=1
    g11: BSplineCurve PolesCount=3 KnotsCount=2 Degree=2 IsPeriodic=0
    g12: GeomPoint X=119 Y=35 Z=0
    g13: GeomPoint X=121 Y=33 Z=0
    g14: LineSegment StartX=119 StartY=35 StartZ=0 EndX=114 EndY=35 EndZ=0
    g15: ArcOfCircle CenterX=105 CenterY=19 CenterZ=0 NormalX=0 NormalY=0 NormalZ=1 AngleXU=0 Radius=16 StartAngle=5.60905 EndAngle=6.28319
    g16: LineSegment StartX=121 StartY=33 StartZ=0 EndX=121 EndY=19 EndZ=0
    g17: LineSegment StartX=117.5 StartY=9.01251 StartZ=0 EndX=121.163 EndY=9.0125 EndZ=0
    g18: ArcOfCircle CenterX=105 CenterY=19 CenterZ=0 NormalX=0 NormalY=0 NormalZ=1 AngleXU=0 Radius=20.6155 StartAngle=5.7297 EndAngle=6.28319
    g19: LineSegment StartX=121.163 StartY=9.0125 StartZ=0 EndX=122.538 EndY=8.16329 EndZ=0
    g20: LineSegment StartX=124 StartY=38 StartZ=0 EndX=125.616 EndY=38 EndZ=0
    g21: LineSegment StartX=125.616 StartY=19 StartZ=0 EndX=125.616 EndY=38 EndZ=0
  constraints (49):
    c: Vertical(g0)
    c: Block(g0)
    c: Coincident(g1,g0)
    c: Block(g1)
    c: Coincident(g2,g1)
    c: Block(g2)
    c: Coincident(g3,g2)
    c: Horizontal(g3)
    c: Tangent(g3,g2)
    c: Coincident(g4,g0)
    c: Distance(g4) = 3
    c: Vertical(g4)
    c: Coincident(g5,g4)
    c: Horizontal(g5)
    c: Coincident(g6,g2)
    c: Coincident(g6,g5)
    c: Vertical(g6)
    c: Horizontal(g7)
    c: Distance(g7) = 105
    c: Coincident(g7,g1)
    c: Block(g3)
    c: Weight(g8) = 1
    c: Equal(g8,g9)
    c: Equal(g8,g10)
    c: InternalAlignment(g8,g11)
    c: InternalAlignment(g9,g11)
    c: InternalAlignment(g10,g11)
    c: InternalAlignment(g12,g11)
    c: InternalAlignment(g13,g11)
    c: Block(g11)
    c: Coincident(g14,g11)
    c: Coincident(g14,g3)
    c: Horizontal(g14)
    c: Block(g15)
    c: Coincident(g16,g11)
    c: Coincident(g16,g15)
    c: Vertical(g16)
    c: Distance(g16) = 14
    c: Coincident(g17,g15)
    c: Block(g18)
    c: Coincident(g19,g18)
    c: Coincident(g20,g7)
    c: Horizontal(g20)
    c: Vertical(g21)
    c: Coincident(g20,g21)
    c: Block(g20)
    c: Block(g21)
    c: Block(g19)
    c: Block(g17)
FEATURE [Part::Extrusion] Extrude029
  Base = -> Sketch038
  Dir = (0,0,1)
  DirMode = 2
  FaceMakerClass = Part::FaceMakerBullseye
  LengthFwd = 72
  LengthRev = 0
  Solid = true
  Symmetric = false
FEATURE [Part::Feature] Face085
  shape: bbox 4.8 x 25.5 x 2e-07 mm, 1 faces, 0 solids (baked)
FEATURE [Part::Revolution] Revolve089  label="moreFrontCaseScrewPost003"
  Angle = 360
  Axis = (0,1,0)
  Base = (0,0,0)
  FaceMakerClass = Part::FaceMakerBullseye
  Placement = pos=(109.5,4.5,3.5) rot=(0,0,1;0rad)
  Solid = false
  Source = -> Face085
  Symmetric = false
FEATURE [Part::Feature] Face086
  shape: bbox 4.8 x 25.5 x 2e-07 mm, 1 faces, 0 solids (baked)
FEATURE [Part::Revolution] Revolve090  label="moreFrontCaseScrewPost004"
  Angle = 360
  Axis = (0,1,0)
  Base = (0,0,0)
  FaceMakerClass = Part::FaceMakerBullseye
  Placement = pos=(109.5,4.5,68.5) rot=(0,0,1;0rad)
  Solid = false
  Source = -> Face086
  Symmetric = false
FEATURE [Part::Fillet] Fillet026  label="top013"
  Base = -> Extrude029
  Edges = 1 edges r=2: [Edge35]
FEATURE [Sketcher::SketchObject] Sketch039
  FullyConstrained = true
  sketch-geometry (7):
    g0: LineSegment StartX=0 StartY=0 StartZ=0 EndX=0 EndY=6 EndZ=0
    g1: Circle CenterX=0 CenterY=0 CenterZ=0 NormalX=0 NormalY=0 NormalZ=1 AngleXU=0 Radius=1
    g2: Circle CenterX=8 CenterY=6 CenterZ=0 NormalX=0 NormalY=0 NormalZ=1 AngleXU=0 Radius=1
    g3: BSplineCurve PolesCount=3 KnotsCount=2 Degree=2 IsPeriodic=0
    g4: GeomPoint X=0 Y=0 Z=0
    g5: GeomPoint X=8 Y=6 Z=0
    g6: LineSegment StartX=0 StartY=6 StartZ=0 EndX=8 EndY=6 EndZ=0
  constraints (14):
    c: Coincident(g0,g-1)
    c: Distance(g0) = 6
    c: Vertical(g0)
    c: Coincident(g3,g0)
    c: Weight(g1) = 1
    c: Equal(g1,g2)
    c: InternalAlignment(g1,g3)
    c: InternalAlignment(g2,g3)
    c: InternalAlignment(g4,g3)
    c: InternalAlignment(g5,g3)
    c: Block(g3)
    c: Coincident(g6,g0)
    c: Coincident(g6,g3)
    c: Horizontal(g6)
FEATURE [Sketcher::SketchObject] Sketch040
  FullyConstrained = true
  sketch-geometry (7):
    g0: LineSegment StartX=0 StartY=0 StartZ=0 EndX=0 EndY=6 EndZ=0
    g1: Circle CenterX=0 CenterY=0 CenterZ=0 NormalX=0 NormalY=0 NormalZ=1 AngleXU=0 Radius=1
    g2: Circle CenterX=8 CenterY=6 CenterZ=0 NormalX=0 NormalY=0 NormalZ=1 AngleXU=0 Radius=1
    g3: BSplineCurve PolesCount=3 KnotsCount=2 Degree=2 IsPeriodic=0
    g4: GeomPoint X=0 Y=0 Z=0
    g5: GeomPoint X=8 Y=6 Z=0
    g6: LineSegment StartX=0 StartY=6 StartZ=0 EndX=8 EndY=6 EndZ=0
  constraints (14):
    c: Coincident(g0,g-1)
    c: Distance(g0) = 6
    c: Vertical(g0)
    c: Coincident(g3,g0)
    c: Weight(g1) = 1
    c: Equal(g1,g2)
    c: InternalAlignment(g1,g3)
    c: InternalAlignment(g2,g3)
    c: InternalAlignment(g4,g3)
    c: InternalAlignment(g5,g3)
    c: Block(g3)
    c: Coincident(g6,g0)
    c: Coincident(g6,g3)
    c: Horizontal(g6)
FEATURE [Sketcher::SketchObject] Sketch041
  FullyConstrained = true
  sketch-geometry (7):
    g0: LineSegment StartX=0 StartY=0 StartZ=0 EndX=0 EndY=6 EndZ=0
    g1: Circle CenterX=0 CenterY=0 CenterZ=0 NormalX=0 NormalY=0 NormalZ=1 AngleXU=0 Radius=1
    g2: Circle CenterX=8 CenterY=6 CenterZ=0 NormalX=0 NormalY=0 NormalZ=1 AngleXU=0 Radius=1
    g3: BSplineCurve PolesCount=3 KnotsCount=2 Degree=2 IsPeriodic=0
    g4: GeomPoint X=0 Y=0 Z=0
    g5: GeomPoint X=8 Y=6 Z=0
    g6: LineSegment StartX=0 StartY=6 StartZ=0 EndX=8 EndY=6 EndZ=0
  constraints (14):
    c: Coincident(g0,g-1)
    c: Distance(g0) = 6
    c: Vertical(g0)
    c: Coincident(g3,g0)
    c: Weight(g1) = 1
    c: Equal(g1,g2)
    c: InternalAlignment(g1,g3)
    c: InternalAlignment(g2,g3)
    c: InternalAlignment(g4,g3)
    c: InternalAlignment(g5,g3)
    c: Block(g3)
    c: Coincident(g6,g0)
    c: Coincident(g6,g3)
    c: Horizontal(g6)
FEATURE [Sketcher::SketchObject] Sketch042
  FullyConstrained = true
  sketch-geometry (7):
    g0: LineSegment StartX=0 StartY=0 StartZ=0 EndX=0 EndY=6 EndZ=0
    g1: Circle CenterX=0 CenterY=0 CenterZ=0 NormalX=0 NormalY=0 NormalZ=1 AngleXU=0 Radius=1
    g2: Circle CenterX=8 CenterY=6 CenterZ=0 NormalX=0 NormalY=0 NormalZ=1 AngleXU=0 Radius=1
    g3: BSplineCurve PolesCount=3 KnotsCount=2 Degree=2 IsPeriodic=0
    g4: GeomPoint X=0 Y=0 Z=0
    g5: GeomPoint X=8 Y=6 Z=0
    g6: LineSegment StartX=0 StartY=6 StartZ=0 EndX=8 EndY=6 EndZ=0
  constraints (14):
    c: Coincident(g0,g-1)
    c: Distance(g0) = 6
    c: Vertical(g0)
    c: Coincident(g3,g0)
    c: Weight(g1) = 1
    c: Equal(g1,g2)
    c: InternalAlignment(g1,g3)
    c: InternalAlignment(g2,g3)
    c: InternalAlignment(g4,g3)
    c: InternalAlignment(g5,g3)
    c: Block(g3)
    c: Coincident(g6,g0)
    c: Coincident(g6,g3)
    c: Horizontal(g6)
FEATURE [Part::Extrusion] Extrude030  label="caseScrewPillarBracket008"
  Base = -> Sketch039
  Dir = (0,0,1)
  DirMode = 2
  FaceMakerClass = Part::FaceMakerBullseye
  LengthFwd = 2.4
  LengthRev = 0
  Placement = pos=(15.76,29,8.8) rot=(0,1,0;0rad)
  Solid = true
  Symmetric = false
FEATURE [Part::Extrusion] Extrude031  label="caseScrewPillarBracket009"
  Base = -> Sketch040
  Dir = (0,0,1)
  DirMode = 2
  FaceMakerClass = Part::FaceMakerBullseye
  LengthFwd = 2.4
  LengthRev = 0
  Placement = pos=(15.76,29,60.8) rot=(0,0,1;0rad)
  Solid = true
  Symmetric = false
FEATURE [Part::Extrusion] Extrude032  label="caseScrewPillarBracket010"
  Base = -> Sketch041
  Dir = (0,0,1)
  DirMode = 2
  FaceMakerClass = Part::FaceMakerBullseye
  LengthFwd = 2.4
  LengthRev = 0
  Placement = pos=(13.7,29,13.26) rot=(0,-1,0;1.5708rad)
  Solid = true
  Symmetric = false
FEATURE [Part::Extrusion] Extrude033  label="caseScrewPillarBracket011"
  Base = -> Sketch042
  Dir = (0,0,1)
  DirMode = 2
  FaceMakerClass = Part::FaceMakerBullseye
  LengthFwd = 2.4
  LengthRev = 0
  Placement = pos=(11.3,29,58.74) rot=(0,1,0;1.5708rad)
  Solid = true
  Symmetric = false
FEATURE [Sketcher::SketchObject] Sketch043
  FullyConstrained = true
  sketch-geometry (7):
    g0: LineSegment StartX=0 StartY=0 StartZ=0 EndX=0 EndY=6 EndZ=0
    g1: Circle CenterX=0 CenterY=0 CenterZ=0 NormalX=0 NormalY=0 NormalZ=1 AngleXU=0 Radius=1
    g2: Circle CenterX=8 CenterY=6 CenterZ=0 NormalX=0 NormalY=0 NormalZ=1 AngleXU=0 Radius=1
    g3: BSplineCurve PolesCount=3 KnotsCount=2 Degree=2 IsPeriodic=0
    g4: GeomPoint X=0 Y=0 Z=0
    g5: GeomPoint X=8 Y=6 Z=0
    g6: LineSegment StartX=0 StartY=6 StartZ=0 EndX=8 EndY=6 EndZ=0
  constraints (14):
    c: Coincident(g0,g-1)
    c: Distance(g0) = 6
    c: Vertical(g0)
    c: Coincident(g3,g0)
    c: Weight(g1) = 1
    c: Equal(g1,g2)
    c: InternalAlignment(g1,g3)
    c: InternalAlignment(g2,g3)
    c: InternalAlignment(g4,g3)
    c: InternalAlignment(g5,g3)
    c: Block(g3)
    c: Coincident(g6,g0)
    c: Coincident(g6,g3)
    c: Horizontal(g6)
FEATURE [Part::Extrusion] Extrude034  label="caseScrewPillarBracket012"
  Base = -> Sketch043
  Dir = (0,0,1)
  DirMode = 2
  FaceMakerClass = Part::FaceMakerBullseye
  LengthFwd = 2.4
  LengthRev = 0
  Placement = pos=(88.3,29,65.23) rot=(0,1,0;1.5708rad)
  Solid = true
  Symmetric = false
FEATURE [Sketcher::SketchObject] Sketch044
  FullyConstrained = true
  sketch-geometry (7):
    g0: LineSegment StartX=0 StartY=0 StartZ=0 EndX=0 EndY=6 EndZ=0
    g1: Circle CenterX=0 CenterY=0 CenterZ=0 NormalX=0 NormalY=0 NormalZ=1 AngleXU=0 Radius=1
    g2: Circle CenterX=8 CenterY=6 CenterZ=0 NormalX=0 NormalY=0 NormalZ=1 AngleXU=0 Radius=1
    g3: BSplineCurve PolesCount=3 KnotsCount=2 Degree=2 IsPeriodic=0
    g4: GeomPoint X=0 Y=0 Z=0
    g5: GeomPoint X=8 Y=6 Z=0
    g6: LineSegment StartX=0 StartY=6 StartZ=0 EndX=8 EndY=6 EndZ=0
  constraints (14):
    c: Coincident(g0,g-1)
    c: Distance(g0) = 6
    c: Vertical(g0)
    c: Coincident(g3,g0)
    c: Weight(g1) = 1
    c: Equal(g1,g2)
    c: InternalAlignment(g1,g3)
    c: InternalAlignment(g2,g3)
    c: InternalAlignment(g4,g3)
    c: InternalAlignment(g5,g3)
    c: Block(g3)
    c: Coincident(g6,g0)
    c: Coincident(g6,g3)
    c: Horizontal(g6)
FEATURE [Part::Extrusion] Extrude035  label="caseScrewPillarBracket013"
  Base = -> Sketch044
  Dir = (0,0,1)
  DirMode = 2
  FaceMakerClass = Part::FaceMakerBullseye
  LengthFwd = 2.4
  LengthRev = 0
  Placement = pos=(90.7,29,6.77) rot=(0,-1,0;1.5708rad)
  Solid = true
  Symmetric = false
FEATURE [Sketcher::SketchObject] Sketch045
  FullyConstrained = true
  sketch-geometry (7):
    g0: LineSegment StartX=0 StartY=0 StartZ=0 EndX=0 EndY=6 EndZ=0
    g1: Circle CenterX=0 CenterY=0 CenterZ=0 NormalX=0 NormalY=0 NormalZ=1 AngleXU=0 Radius=1
    g2: Circle CenterX=8 CenterY=6 CenterZ=0 NormalX=0 NormalY=0 NormalZ=1 AngleXU=0 Radius=1
    g3: BSplineCurve PolesCount=3 KnotsCount=2 Degree=2 IsPeriodic=0
    g4: GeomPoint X=0 Y=0 Z=0
    g5: GeomPoint X=8 Y=6 Z=0
    g6: LineSegment StartX=0 StartY=6 StartZ=0 EndX=8 EndY=6 EndZ=0
  constraints (14):
    c: Coincident(g0,g-1)
    c: Distance(g0) = 6
    c: Vertical(g0)
    c: Coincident(g3,g0)
    c: Weight(g1) = 1
    c: Equal(g1,g2)
    c: InternalAlignment(g1,g3)
    c: InternalAlignment(g2,g3)
    c: InternalAlignment(g4,g3)
    c: InternalAlignment(g5,g3)
    c: Block(g3)
    c: Coincident(g6,g0)
    c: Coincident(g6,g3)
    c: Horizontal(g6)
FEATURE [Sketcher::SketchObject] Sketch046
  FullyConstrained = true
  sketch-geometry (7):
    g0: LineSegment StartX=0 StartY=0 StartZ=0 EndX=0 EndY=6 EndZ=0
    g1: Circle CenterX=0 CenterY=0 CenterZ=0 NormalX=0 NormalY=0 NormalZ=1 AngleXU=0 Radius=1
    g2: Circle CenterX=8 CenterY=6 CenterZ=0 NormalX=0 NormalY=0 NormalZ=1 AngleXU=0 Radius=1
    g3: BSplineCurve PolesCount=3 KnotsCount=2 Degree=2 IsPeriodic=0
    g4: GeomPoint X=0 Y=0 Z=0
    g5: GeomPoint X=8 Y=6 Z=0
    g6: LineSegment StartX=0 StartY=6 StartZ=0 EndX=8 EndY=6 EndZ=0
  constraints (14):
    c: Coincident(g0,g-1)
    c: Distance(g0) = 6
    c: Vertical(g0)
    c: Coincident(g3,g0)
    c: Weight(g1) = 1
    c: Equal(g1,g2)
    c: InternalAlignment(g1,g3)
    c: InternalAlignment(g2,g3)
    c: InternalAlignment(g4,g3)
    c: InternalAlignment(g5,g3)
    c: Block(g3)
    c: Coincident(g6,g0)
    c: Coincident(g6,g3)
    c: Horizontal(g6)
FEATURE [Part::Extrusion] Extrude036  label="caseScrewPillarBracket014"
  Base = -> Sketch045
  Dir = (0,0,1)
  DirMode = 2
  FaceMakerClass = Part::FaceMakerBullseye
  LengthFwd = 2.4
  LengthRev = 0
  Placement = pos=(110.7,29,6.77) rot=(0,-1,0;1.5708rad)
  Solid = true
  Symmetric = false
FEATURE [Part::Extrusion] Extrude037  label="caseScrewPillarBracket015"
  Base = -> Sketch046
  Dir = (0,0,1)
  DirMode = 2
  FaceMakerClass = Part::FaceMakerBullseye
  LengthFwd = 2.4
  LengthRev = 0
  Placement = pos=(108.3,29,65.23) rot=(0,1,0;1.5708rad)
  Solid = true
  Symmetric = false
FEATURE [Part::Box] Box013  label="frontCaseScrewPillarBracket002"
  AttacherType = Attacher::AttachEngine3D
  Height = 2.4
  Length = 22
  Placement = pos=(87,28,2.3) rot=(0,0,1;0rad)
  Width = 7
FEATURE [Part::Box] Box014  label="frontCaseScrewPillarBracket003"
  AttacherType = Attacher::AttachEngine3D
  Height = 2.4
  Length = 22
  Placement = pos=(87,28,67.3) rot=(0,0,1;0rad)
  Width = 7
FEATURE [Part::Feature] Face087
  shape: bbox 4.8 x 30.2 x 2e-07 mm, 1 faces, 0 solids (baked)
FEATURE [Part::Revolution] Revolve091  label="frontCaseScrewPost004"
  Angle = 360
  Axis = (0,1,0)
  Base = (0,0,0)
  FaceMakerClass = Part::FaceMakerBullseye
  Placement = pos=(89.5,4.5,3.5) rot=(0,0,1;0rad)
  Solid = false
  Source = -> Face087
  Symmetric = false
FEATURE [Part::Feature] Face088
  shape: bbox 4.8 x 30.2 x 2e-07 mm, 1 faces, 0 solids (baked)
FEATURE [Part::Revolution] Revolve092  label="frontCaseScrewPost005"
  Angle = 360
  Axis = (0,1,0)
  Base = (0,0,0)
  FaceMakerClass = Part::FaceMakerBullseye
  Placement = pos=(89.5,4.5,68.5) rot=(0,0,1;0rad)
  Solid = false
  Source = -> Face088
  Symmetric = false
FEATURE [Part::Feature] Face089
  shape: bbox 3.5 x 30.2 x 2e-07 mm, 1 faces, 0 solids (baked)
FEATURE [Part::Revolution] Revolve093  label="backCaseScrewPost002"
  Angle = 360
  Axis = (0,1,0)
  Base = (0,0,0)
  FaceMakerClass = Part::FaceMakerBullseye
  Placement = pos=(12.5,4.5,10) rot=(0,0,1;0rad)
  Solid = false
  Source = -> Face089
  Symmetric = false
FEATURE [Part::Feature] Face090
  shape: bbox 3.5 x 30.2 x 2e-07 mm, 1 faces, 0 solids (baked)
FEATURE [Part::Revolution] Revolve094  label="backCaseScrewPost003"
  Angle = 360
  Axis = (0,1,0)
  Base = (0,0,0)
  FaceMakerClass = Part::FaceMakerBullseye
  Placement = pos=(12.5,4.5,62) rot=(0,0,1;0rad)
  Solid = false
  Source = -> Face090
  Symmetric = false
FEATURE [Part::Box] Box015  label="Cube011"
  AttacherType = Attacher::AttachEngine3D
  Height = 28.8
  Length = 3
  Placement = pos=(107.3,28,21.6) rot=(0,0,1;0rad)
  Width = 7
FEATURE [Part::Box] Box016  label="Cube012"
  AttacherType = Attacher::AttachEngine3D
  Height = 3
  Length = 7.4
  Placement = pos=(107.3,28,18.6) rot=(0,0,1;0rad)
  Width = 7
FEATURE [Part::Box] Box017  label="Cube013"
  AttacherType = Attacher::AttachEngine3D
  Height = 3
  Length = 7.4
  Placement = pos=(107.3,28,50.4) rot=(0,0,1;0rad)
  Width = 7
FEATURE [Part::Cylinder] Cylinder024
  Angle = 360
  AttacherType = Attacher::AttachEngine3D
  Height = 20
  Placement = pos=(0,0,36.15) rot=(0,0,1;0rad)
  Radius = 14.3
FEATURE [Part::Cylinder] Cylinder025
  Angle = 360
  AttacherType = Attacher::AttachEngine3D
  Height = 10
  Placement = pos=(0,0,36.15) rot=(0,0,1;0rad)
  Radius = 4
FEATURE [Part::MultiFuse] Fusion066  label="removeToCreteHoleForPlugHousing009"
  Placement = pos=(70,19,36) rot=(0,1,0;1.5708rad)
  Shapes = -> [Cylinder024,Cylinder025]
FEATURE [Part::MultiFuse] Fusion065  label="plugHousingBracketHolder002"
  Shapes = -> [Box017,Box015,Box016]
FEATURE [Part::Cut] Cut025  label="plugHousingBracketHolder003"
  Base = -> Fusion065
  Placement = pos=(7,0,0) rot=(0,0,1;0rad)
  Tool = -> Fusion066
FEATURE [Sketcher::SketchObject] Sketch047
  FullyConstrained = false
  Placement = pos=(0,0,0) rot=(1,0,0;1.5708rad)
  sketch-geometry (24):
    g0: ArcOfCircle CenterX=-4 CenterY=-10.5 CenterZ=0 NormalX=0 NormalY=0 NormalZ=1 AngleXU=0 Radius=1.5 StartAngle=6e-16 EndAngle=3.14159
    g1: ArcOfCircle CenterX=-34.2 CenterY=-10.5 CenterZ=0 NormalX=0 NormalY=0 NormalZ=1 AngleXU=0 Radius=1.5 StartAngle=0 EndAngle=3.14159
    g2: ArcOfCircle CenterX=-34.2 CenterY=-27.7 CenterZ=0 NormalX=0 NormalY=0 NormalZ=1 AngleXU=0 Radius=1.5 StartAngle=3.14159 EndAngle=6.28319
    g3: ArcOfCircle CenterX=-4 CenterY=-27.7 CenterZ=0 NormalX=0 NormalY=0 NormalZ=1 AngleXU=0 Radius=1.5 StartAngle=3.1416 EndAngle=6.28319
    g4: ArcOfCircle CenterX=-10 CenterY=-4.3 CenterZ=0 NormalX=0 NormalY=0 NormalZ=1 AngleXU=0 Radius=1.5 StartAngle=2e-16 EndAngle=3.14159
    g5: ArcOfCircle CenterX=-16.1 CenterY=-1.8 CenterZ=0 NormalX=0 NormalY=0 NormalZ=1 AngleXU=0 Radius=1.5 StartAngle=5e-16 EndAngle=3.14159
    g6: ArcOfCircle CenterX=-22.1 CenterY=-1.8 CenterZ=0 NormalX=0 NormalY=0 NormalZ=1 AngleXU=0 Radius=1.5 StartAngle=5e-16 EndAngle=3.14159
    g7: ArcOfCircle CenterX=-28.2 CenterY=-4.3 CenterZ=0 NormalX=0 NormalY=0 NormalZ=1 AngleXU=0 Radius=1.5 StartAngle=2e-16 EndAngle=3.14159
    g8: ArcOfCircle CenterX=-10 CenterY=-33.9 CenterZ=0 NormalX=0 NormalY=0 NormalZ=1 AngleXU=0 Radius=1.5 StartAngle=3.14159 EndAngle=6.28319
    g9: ArcOfCircle CenterX=-16.1 CenterY=-36.4 CenterZ=0 NormalX=0 NormalY=0 NormalZ=1 AngleXU=0 Radius=1.5 StartAngle=3.14159 EndAngle=6.28319
    g10: ArcOfCircle CenterX=-22.1 CenterY=-36.4 CenterZ=0 NormalX=0 NormalY=0 NormalZ=1 AngleXU=0 Radius=1.5 StartAngle=3.14159 EndAngle=6.28319
    g11: ArcOfCircle CenterX=-28.2 CenterY=-33.9 CenterZ=0 NormalX=0 NormalY=0 NormalZ=1 AngleXU=0 Radius=1.5 StartAngle=3.14159 EndAngle=6.28319
    g12: LineSegment StartX=-35.7 StartY=-10.5 StartZ=0 EndX=-35.7 EndY=-27.7 EndZ=0
    g13: LineSegment StartX=-32.7 StartY=-10.5 StartZ=0 EndX=-32.7 EndY=-27.7 EndZ=0
    g14: LineSegment StartX=-29.7 StartY=-33.9 StartZ=0 EndX=-29.7 EndY=-4.3 EndZ=0
    g15: LineSegment StartX=-26.7 StartY=-33.9 StartZ=0 EndX=-26.7 EndY=-4.3 EndZ=0
    g16: LineSegment StartX=-2.5 StartY=-10.5 StartZ=0 EndX=-2.5 EndY=-27.7 EndZ=0
    g17: LineSegment StartX=-8.5 StartY=-4.3 StartZ=0 EndX=-8.5 EndY=-33.9 EndZ=0
    g18: LineSegment StartX=-5.5 StartY=-10.5 StartZ=0 EndX=-5.5 EndY=-27.7 EndZ=0
    g19: LineSegment StartX=-11.5 StartY=-4.3 StartZ=0 EndX=-11.5 EndY=-33.9 EndZ=0
    g20: LineSegment StartX=-14.6 StartY=-1.8 StartZ=0 EndX=-14.6 EndY=-36.4 EndZ=0
    g21: LineSegment StartX=-17.6 StartY=-1.8 StartZ=0 EndX=-17.6 EndY=-36.4 EndZ=0
    g22: LineSegment StartX=-20.6 StartY=-36.4 StartZ=0 EndX=-20.6 EndY=-1.8 EndZ=0
    g23: LineSegment StartX=-23.6 StartY=-1.8 StartZ=0 EndX=-23.6 EndY=-36.4 EndZ=0
  constraints (48):
    c: Block(g0)
    c: Block(g1)
    c: Block(g2)
    c: Block(g3)
    c: Block(g4)
    c: Block(g5)
    c: Block(g6)
    c: Block(g7)
    c: Block(g8)
    c: Block(g9)
    c: Block(g10)
    c: Block(g11)
    c: Coincident(g12,g1)
    c: Coincident(g12,g2)
    c: Vertical(g12)
    c: Coincident(g13,g1)
    c: Coincident(g13,g2)
    c: Vertical(g13)
    c: Coincident(g14,g11)
    c: Coincident(g14,g7)
    c: Vertical(g14)
    c: Coincident(g15,g11)
    c: Coincident(g15,g7)
    c: Vertical(g15)
    c: Coincident(g16,g0)
    c: Coincident(g16,g3)
    c: Vertical(g16)
    c: Coincident(g17,g4)
    c: Coincident(g17,g8)
    c: Vertical(g17)
    c: Coincident(g18,g0)
    c: Coincident(g18,g3)
    c: Vertical(g18)
    c: Coincident(g19,g4)
    c: Coincident(g19,g8)
    c: Vertical(g19)
    c: Coincident(g20,g5)
    c: Coincident(g20,g9)
    c: Vertical(g20)
    c: Coincident(g21,g5)
    c: Coincident(g21,g9)
    c: Vertical(g21)
    c: Coincident(g22,g10)
    c: Coincident(g22,g6)
    c: Vertical(g22)
    c: Coincident(g23,g6)
    c: Coincident(g23,g10)
    c: Vertical(g23)
FEATURE [Part::Extrusion] Extrude038  label="removeToCreateFanGrillHoles001"
  Base = -> Sketch047
  Dir = (0,-1,6e-16)
  DirMode = 2
  FaceMakerClass = Part::FaceMakerBullseye
  LengthFwd = 10
  LengthRev = 0
  Placement = pos=(65.4,44,54.82) rot=(0,0,1;0rad)
  Solid = true
  Symmetric = false
FEATURE [Part::Feature] Wire004
  shape: bbox 11 x 5.2 x 2e-07 mm, 0 faces, 0 solids (baked)
FEATURE [Part::Revolution] Revolve095
  Angle = 360
  Axis = (0,1,0)
  Base = (0,0,0)
  FaceMakerClass = Part::FaceMakerBullseye
  Placement = pos=(30.3,38,19.7) rot=(0,0,1;0rad)
  Solid = true
  Source = -> Wire004
  Symmetric = false
FEATURE [Part::Feature] Wire005
  shape: bbox 11 x 5.2 x 2e-07 mm, 0 faces, 0 solids (baked)
FEATURE [Part::Revolution] Revolve096
  Angle = 360
  Axis = (0,1,0)
  Base = (0,0,0)
  FaceMakerClass = Part::FaceMakerBullseye
  Placement = pos=(30.3,38,51.7) rot=(0,0,1;0rad)
  Solid = true
  Source = -> Wire005
  Symmetric = false
FEATURE [Part::Feature] Wire006
  shape: bbox 11 x 5.2 x 2e-07 mm, 0 faces, 0 solids (baked)
FEATURE [Part::Revolution] Revolve097
  Angle = 360
  Axis = (0,1,0)
  Base = (0,0,0)
  FaceMakerClass = Part::FaceMakerBullseye
  Placement = pos=(62.3,38,51.7) rot=(0,0,1;0rad)
  Solid = true
  Source = -> Wire006
  Symmetric = false
FEATURE [Part::Feature] Wire007
  shape: bbox 11 x 5.2 x 2e-07 mm, 0 faces, 0 solids (baked)
FEATURE [Part::Revolution] Revolve098
  Angle = 360
  Axis = (0,1,0)
  Base = (0,0,0)
  FaceMakerClass = Part::FaceMakerBullseye
  Placement = pos=(62.3,38,19.7) rot=(0,0,1;0rad)
  Solid = true
  Source = -> Wire007
  Symmetric = false
FEATURE [Part::MultiFuse] Fusion067  label="fanScrewHousing002"
  Shapes = -> [Revolve098,Revolve097,Revolve096,Revolve095]
FEATURE [Part::Feature] Face091 .. Face094  x4 (patterned run collapsed; names and placements below)
  shape: bbox 3.5 x 17.8 x 2e-07 mm, 1 faces, 0 solids (baked)
FEATURE [Part::Revolution] Revolve099  label="removeToCreateScrewAndThreadedInsertHole026"
  Angle = 360
  Axis = (0,1,0)
  Base = (0,0,0)
  FaceMakerClass = Part::FaceMakerBullseye
  Placement = pos=(62.3,30.3,19.7) rot=(0,0,1;0rad)
  Solid = false
  Source = -> Face091
  Symmetric = false
FEATURE [Part::Revolution] Revolve100  label="removeToCreateScrewAndThreadedInsertHole027"
  Angle = 360
  Axis = (0,1,0)
  Base = (0,0,0)
  FaceMakerClass = Part::FaceMakerBullseye
  Placement = pos=(62.3,30.3,51.7) rot=(0,0,1;0rad)
  Solid = false
  Source = -> Face092
  Symmetric = false
FEATURE [Part::Revolution] Revolve101  label="removeToCreateScrewAndThreadedInsertHole028"
  Angle = 360
  Axis = (0,1,0)
  Base = (0,0,0)
  FaceMakerClass = Part::FaceMakerBullseye
  Placement = pos=(30.3,30.3,19.7) rot=(0,0,1;0rad)
  Solid = false
  Source = -> Face093
  Symmetric = false
FEATURE [Part::Revolution] Revolve102  label="removeToCreateScrewAndThreadedInsertHole029"
  Angle = 360
  Axis = (0,1,0)
  Base = (0,0,0)
  FaceMakerClass = Part::FaceMakerBullseye
  Placement = pos=(30.3,30.3,51.7) rot=(0,0,1;0rad)
  Solid = false
  Source = -> Face094
  Symmetric = false
FEATURE [Part::MultiFuse] Fusion068  label="createThreadedInsertHolesForFan002"
  Shapes = -> [Revolve099,Revolve100,Revolve101,Revolve102]
FEATURE [Part::Cut] Cut026  label="fanScrewHousing003"
  Base = -> Fusion067
  Tool = -> Fusion068
FEATURE [Sketcher::SketchObject] Sketch048
  FullyConstrained = false
  Placement = pos=(0,0,0) rot=(1,0,0;1.5708rad)
  sketch-geometry (24):
    g0: ArcOfCircle CenterX=-4 CenterY=-10.5 CenterZ=0 NormalX=0 NormalY=0 NormalZ=1 AngleXU=0 Radius=1.5 StartAngle=6e-16 EndAngle=3.14159
    g1: ArcOfCircle CenterX=-34.2 CenterY=-10.5 CenterZ=0 NormalX=0 NormalY=0 NormalZ=1 AngleXU=0 Radius=1.5 StartAngle=0 EndAngle=3.14159
    g2: ArcOfCircle CenterX=-34.2 CenterY=-27.7 CenterZ=0 NormalX=0 NormalY=0 NormalZ=1 AngleXU=0 Radius=1.5 StartAngle=3.14159 EndAngle=6.28319
    g3: ArcOfCircle CenterX=-4 CenterY=-27.7 CenterZ=0 NormalX=0 NormalY=0 NormalZ=1 AngleXU=0 Radius=1.5 StartAngle=3.1416 EndAngle=6.28319
    g4: ArcOfCircle CenterX=-10 CenterY=-4.3 CenterZ=0 NormalX=0 NormalY=0 NormalZ=1 AngleXU=0 Radius=1.5 StartAngle=2e-16 EndAngle=3.14159
    g5: ArcOfCircle CenterX=-16.1 CenterY=-1.8 CenterZ=0 NormalX=0 NormalY=0 NormalZ=1 AngleXU=0 Radius=1.5 StartAngle=5e-16 EndAngle=3.14159
    g6: ArcOfCircle CenterX=-22.1 CenterY=-1.8 CenterZ=0 NormalX=0 NormalY=0 NormalZ=1 AngleXU=0 Radius=1.5 StartAngle=5e-16 EndAngle=3.14159
    g7: ArcOfCircle CenterX=-28.2 CenterY=-4.3 CenterZ=0 NormalX=0 NormalY=0 NormalZ=1 AngleXU=0 Radius=1.5 StartAngle=2e-16 EndAngle=3.14159
    g8: ArcOfCircle CenterX=-10 CenterY=-33.9 CenterZ=0 NormalX=0 NormalY=0 NormalZ=1 AngleXU=0 Radius=1.5 StartAngle=3.14159 EndAngle=6.28319
    g9: ArcOfCircle CenterX=-16.1 CenterY=-36.4 CenterZ=0 NormalX=0 NormalY=0 NormalZ=1 AngleXU=0 Radius=1.5 StartAngle=3.14159 EndAngle=6.28319
    g10: ArcOfCircle CenterX=-22.1 CenterY=-36.4 CenterZ=0 NormalX=0 NormalY=0 NormalZ=1 AngleXU=0 Radius=1.5 StartAngle=3.14159 EndAngle=6.28319
    g11: ArcOfCircle CenterX=-28.2 CenterY=-33.9 CenterZ=0 NormalX=0 NormalY=0 NormalZ=1 AngleXU=0 Radius=1.5 StartAngle=3.14159 EndAngle=6.28319
    g12: LineSegment StartX=-35.7 StartY=-10.5 StartZ=0 EndX=-35.7 EndY=-27.7 EndZ=0
    g13: LineSegment StartX=-32.7 StartY=-10.5 StartZ=0 EndX=-32.7 EndY=-27.7 EndZ=0
    g14: LineSegment StartX=-29.7 StartY=-33.9 StartZ=0 EndX=-29.7 EndY=-4.3 EndZ=0
    g15: LineSegment StartX=-26.7 StartY=-33.9 StartZ=0 EndX=-26.7 EndY=-4.3 EndZ=0
    g16: LineSegment StartX=-2.5 StartY=-10.5 StartZ=0 EndX=-2.5 EndY=-27.7 EndZ=0
    g17: LineSegment StartX=-8.5 StartY=-4.3 StartZ=0 EndX=-8.5 EndY=-33.9 EndZ=0
    g18: LineSegment StartX=-5.5 StartY=-10.5 StartZ=0 EndX=-5.5 EndY=-27.7 EndZ=0
    g19: LineSegment StartX=-11.5 StartY=-4.3 StartZ=0 EndX=-11.5 EndY=-33.9 EndZ=0
    g20: LineSegment StartX=-14.6 StartY=-1.8 StartZ=0 EndX=-14.6 EndY=-36.4 EndZ=0
    g21: LineSegment StartX=-17.6 StartY=-1.8 StartZ=0 EndX=-17.6 EndY=-36.4 EndZ=0
    g22: LineSegment StartX=-20.6 StartY=-36.4 StartZ=0 EndX=-20.6 EndY=-1.8 EndZ=0
    g23: LineSegment StartX=-23.6 StartY=-1.8 StartZ=0 EndX=-23.6 EndY=-36.4 EndZ=0
  constraints (48):
    c: Block(g0)
    c: Block(g1)
    c: Block(g2)
    c: Block(g3)
    c: Block(g4)
    c: Block(g5)
    c: Block(g6)
    c: Block(g7)
    c: Block(g8)
    c: Block(g9)
    c: Block(g10)
    c: Block(g11)
    c: Coincident(g12,g1)
    c: Coincident(g12,g2)
    c: Vertical(g12)
    c: Coincident(g13,g1)
    c: Coincident(g13,g2)
    c: Vertical(g13)
    c: Coincident(g14,g11)
    c: Coincident(g14,g7)
    c: Vertical(g14)
    c: Coincident(g15,g11)
    c: Coincident(g15,g7)
    c: Vertical(g15)
    c: Coincident(g16,g0)
    c: Coincident(g16,g3)
    c: Vertical(g16)
    c: Coincident(g17,g4)
    c: Coincident(g17,g8)
    c: Vertical(g17)
    c: Coincident(g18,g0)
    c: Coincident(g18,g3)
    c: Vertical(g18)
    c: Coincident(g19,g4)
    c: Coincident(g19,g8)
    c: Vertical(g19)
    c: Coincident(g20,g5)
    c: Coincident(g20,g9)
    c: Vertical(g20)
    c: Coincident(g21,g5)
    c: Coincident(g21,g9)
    c: Vertical(g21)
    c: Coincident(g22,g10)
    c: Coincident(g22,g6)
    c: Vertical(g22)
    c: Coincident(g23,g6)
    c: Coincident(g23,g10)
    c: Vertical(g23)
FEATURE [Part::Extrusion] Extrude039  label="removeToCreateFanGrillHoles002"
  Base = -> Sketch048
  Dir = (0,-1,6e-16)
  DirMode = 2
  FaceMakerClass = Part::FaceMakerBullseye
  LengthFwd = 10
  LengthRev = 0
  Placement = pos=(65.4,44,54.82) rot=(0,0,1;0rad)
  Solid = true
  Symmetric = false
FEATURE [Part::Cut] Cut027  label="fanScrewHousing004"
  Base = -> Cut026
  Tool = -> Extrude038
FEATURE [Part::Cut] Cut028  label="top014"
  Base = -> Fillet026
  Tool = -> Extrude039
FEATURE [Part::Feature] Face095 .. Face098  x4 (patterned run collapsed; names and placements below)
  shape: bbox 3.5 x 17.8 x 2e-07 mm, 1 faces, 0 solids (baked)
FEATURE [Part::Revolution] Revolve103  label="removeToCreateScrewAndThreadedInsertHole030"
  Angle = 360
  Axis = (0,1,0)
  Base = (0,0,0)
  FaceMakerClass = Part::FaceMakerBullseye
  Placement = pos=(62.3,30.3,19.7) rot=(0,0,1;0rad)
  Solid = false
  Source = -> Face095
  Symmetric = false
FEATURE [Part::Revolution] Revolve104  label="removeToCreateScrewAndThreadedInsertHole031"
  Angle = 360
  Axis = (0,1,0)
  Base = (0,0,0)
  FaceMakerClass = Part::FaceMakerBullseye
  Placement = pos=(62.3,30.3,51.7) rot=(0,0,1;0rad)
  Solid = false
  Source = -> Face096
  Symmetric = false
FEATURE [Part::Revolution] Revolve105  label="removeToCreateScrewAndThreadedInsertHole032"
  Angle = 360
  Axis = (0,1,0)
  Base = (0,0,0)
  FaceMakerClass = Part::FaceMakerBullseye
  Placement = pos=(30.3,30.3,19.7) rot=(0,0,1;0rad)
  Solid = false
  Source = -> Face097
  Symmetric = false
FEATURE [Part::Revolution] Revolve106  label="removeToCreateScrewAndThreadedInsertHole033"
  Angle = 360
  Axis = (0,1,0)
  Base = (0,0,0)
  FaceMakerClass = Part::FaceMakerBullseye
  Placement = pos=(30.3,30.3,51.7) rot=(0,0,1;0rad)
  Solid = false
  Source = -> Face098
  Symmetric = false
FEATURE [Part::MultiFuse] Fusion069  label="createThreadedInsertHolesForFan003"
  Shapes = -> [Revolve103,Revolve104,Revolve105,Revolve106]
FEATURE [Part::Cut] Cut029  label="top015"
  Base = -> Cut028
  Tool = -> Fusion054
FEATURE [Part::Cut] Cut030  label="fanScrewHousing005"
  Base = -> Cut027
  Tool = -> Fusion069
FEATURE [Part::Cylinder] Cylinder026  label="removeToCreteHoleForPlugHousing010"
  Angle = 360
  AttacherType = Attacher::AttachEngine3D
  Height = 20
  Placement = pos=(-2,19,36) rot=(0,1,0;1.5708rad)
  Radius = 14.3
FEATURE [Part::Box] Box018  label="removeToCreteHoleForPlugHousing011"
  AttacherType = Attacher::AttachEngine3D
  Height = 28.6
  Length = 10
  Placement = pos=(-2,0,21.7) rot=(0,0,1;0rad)
  Width = 19
FEATURE [Part::Box] Box019  label="wireHolderBottomCaseBit"
  AttacherType = Attacher::AttachEngine3D
  Height = 28
  Length = 3
  Placement = pos=(0,0,22) rot=(0,0,1;0rad)
  Width = 21
FEATURE [Part::Cylinder] Cylinder027  label="removeToCreteHoleForPlugHousing012"
  Angle = 360
  AttacherType = Attacher::AttachEngine3D
  Height = 20
  Placement = pos=(-2,19,36) rot=(0,1,0;1.5708rad)
  Radius = 14.3
FEATURE [Part::Cut] Cut031  label="wireHolderBottomCaseBit001"
  Base = -> Box019
  Tool = -> Cylinder027
FEATURE [Part::MultiFuse] Fusion070  label="removeToCreteHoleForPlugHousing013"
  Shapes = -> [Box018,Cylinder026]
FEATURE [Part::Cut] Cut032  label="top016"
  Base = -> Cut029
  Tool = -> Fusion070
FEATURE [Part::Cylinder] Cylinder028
  Angle = 360
  AttacherType = Attacher::AttachEngine3D
  Height = 20
  Placement = pos=(0,0,36.15) rot=(0,0,1;0rad)
  Radius = 14.3
FEATURE [Part::Cylinder] Cylinder029
  Angle = 360
  AttacherType = Attacher::AttachEngine3D
  Height = 10
  Placement = pos=(0,0,36.15) rot=(0,0,1;0rad)
  Radius = 4
FEATURE [Part::MultiFuse] Fusion071  label="removeToCreteHoleForPlugHousing014"
  Placement = pos=(70,19,36) rot=(0,1,0;1.5708rad)
  Shapes = -> [Cylinder028,Cylinder029]
FEATURE [Sketcher::SketchObject] Sketch049  label="topSketch011"
  FullyConstrained = true
  sketch-geometry (4):
    g0: ArcOfCircle CenterX=105 CenterY=19 CenterZ=0 NormalX=0 NormalY=0 NormalZ=1 AngleXU=0 Radius=20.6155 StartAngle=5.54125 EndAngle=6.28319
    g1: ArcOfCircle CenterX=105 CenterY=19 CenterZ=0 NormalX=0 NormalY=0 NormalZ=1 AngleXU=0 Radius=13 StartAngle=5.54125 EndAngle=6.28319
    g2: LineSegment StartX=118 StartY=19 StartZ=0 EndX=125.616 EndY=19 EndZ=0
    g3: LineSegment StartX=114.583 StartY=10.2157 StartZ=0 EndX=120.197 EndY=5.06982 EndZ=0
  constraints (7):
    c: Block(g0)
    c: Block(g1)
    c: Coincident(g2,g1)
    c: Coincident(g2,g0)
    c: Horizontal(g2)
    c: Coincident(g3,g1)
    c: Coincident(g3,g0)
FEATURE [Part::Box] Box020  label="removeToCreteHoleForPlugHousing015"
  AttacherType = Attacher::AttachEngine3D
  Height = 28.6
  Length = 20
  Placement = pos=(106.15,0,21.7) rot=(0,0,1;0rad)
  Width = 19
FEATURE [Part::MultiFuse] Fusion072  label="removeToCreteHoleForPlugHousing016"
  Shapes = -> [Box020,Fusion071]
FEATURE [Part::Cut] Cut033  label="removeToCreteHoleForPlugHousing017"
  Base = -> Cut032
  Tool = -> Fusion072
FEATURE [Part::Cylinder] Cylinder030
  Angle = 360
  AttacherType = Attacher::AttachEngine3D
  Height = 20
  Placement = pos=(0,0,36.15) rot=(0,0,1;0rad)
  Radius = 14.3
FEATURE [Part::Cylinder] Cylinder031
  Angle = 360
  AttacherType = Attacher::AttachEngine3D
  Height = 10
  Placement = pos=(0,0,36.15) rot=(0,0,1;0rad)
  Radius = 4
FEATURE [Part::Box] Box021  label="removeToCreteHoleForPlugHousing019"
  AttacherType = Attacher::AttachEngine3D
  Height = 28.6
  Length = 20
  Placement = pos=(106.15,0,21.7) rot=(0,0,1;0rad)
  Width = 19
FEATURE [Part::MultiFuse] Fusion074  label="removeToCreteHoleForPlugHousing020"
  Placement = pos=(70,19,36) rot=(0,1,0;1.5708rad)
  Shapes = -> [Cylinder030,Cylinder031]
FEATURE [Part::MultiFuse] Fusion073  label="removeToCreteHoleForPlugHousing018"
  Placement = pos=(0,0,28.3) rot=(0,0,1;0rad)
  Shapes = -> [Box021,Fusion074]
FEATURE [Part::Cylinder] Cylinder032
  Angle = 360
  AttacherType = Attacher::AttachEngine3D
  Height = 20
  Placement = pos=(0,0,36.15) rot=(0,0,1;0rad)
  Radius = 14.3
FEATURE [Part::Cylinder] Cylinder033
  Angle = 360
  AttacherType = Attacher::AttachEngine3D
  Height = 10
  Placement = pos=(0,0,36.15) rot=(0,0,1;0rad)
  Radius = 4
FEATURE [Part::Box] Box022  label="removeToCreteHoleForPlugHousing021"
  AttacherType = Attacher::AttachEngine3D
  Height = 28.6
  Length = 20
  Placement = pos=(106.15,0,21.7) rot=(0,0,1;0rad)
  Width = 19
FEATURE [Part::MultiFuse] Fusion076  label="removeToCreteHoleForPlugHousing023"
  Placement = pos=(70,19,36) rot=(0,1,0;1.5708rad)
  Shapes = -> [Cylinder032,Cylinder033]
FEATURE [Part::MultiFuse] Fusion075  label="removeToCreteHoleForPlugHousing022"
  Placement = pos=(0,0,-28.3) rot=(0,0,1;0rad)
  Shapes = -> [Box022,Fusion076]
FEATURE [Part::MultiFuse] Fusion077  label="removeToCreatePlugHousingBottomBit"
  Shapes = -> [Fusion075,Fusion073]
FEATURE [Part::Cylinder] Cylinder034
  Angle = 360
  AttacherType = Attacher::AttachEngine3D
  Height = 20
  Placement = pos=(0,0,36.15) rot=(0,0,1;0rad)
  Radius = 14
FEATURE [Part::Cylinder] Cylinder035
  Angle = 360
  AttacherType = Attacher::AttachEngine3D
  Height = 10
  Placement = pos=(0,0,36.15) rot=(0,0,1;0rad)
  Radius = 4
FEATURE [Part::MultiFuse] Fusion078  label="removeToCreteHoleForPlugHousing024"
  Placement = pos=(70,19,36) rot=(0,1,0;1.5708rad)
  Shapes = -> [Cylinder034,Cylinder035]
FEATURE [Part::MultiFuse] Fusion079  label="removeToCreatePlugHousingBottomBit001"
  Shapes = -> [Fusion078,Fusion077]
FEATURE [Part::Extrusion] Extrude040  label="bottomPlugHousingBit"
  Base = -> Sketch049
  Dir = (0,0,1)
  DirMode = 2
  FaceMakerClass = Part::FaceMakerBullseye
  LengthFwd = 72
  LengthRev = 0
  Solid = true
  Symmetric = false
FEATURE [Part::Cut] Cut034  label="bottomPlugHousingBit001"
  Base = -> Extrude040
  Placement = pos=(-0.09,0,0) rot=(0,0,1;0rad)
  Tool = -> Fusion079
FEATURE [Part::Box] Box023  label="Cube014"
  AttacherType = Attacher::AttachEngine3D
  Height = 16
  Length = 8
  Placement = pos=(12.7,31.52,28) rot=(0,0,1;0rad)
  Width = 4
FEATURE [Part::Cylinder] Cylinder036
  Angle = 360
  AttacherType = Attacher::AttachEngine3D
  Height = 10
  Placement = pos=(0,0,36.15) rot=(0,0,1;0rad)
  Radius = 4
FEATURE [Part::Cylinder] Cylinder037
  Angle = 360
  AttacherType = Attacher::AttachEngine3D
  Height = 20
  Placement = pos=(0,0,36.15) rot=(0,0,1;0rad)
  Radius = 8.2
FEATURE [Part::MultiFuse] Fusion080  label="removeToCreteHoleForPlugHousing025"
  Placement = pos=(-42,19,36) rot=(0,1,0;1.5708rad)
  Shapes = -> [Cylinder037,Cylinder036]
FEATURE [Sketcher::SketchObject] Sketch050  label="topSketch012"
  FullyConstrained = true
  sketch-geometry (4):
    g0: LineSegment StartX=16.8446 StartY=31.512 StartZ=0 EndX=16.3251 EndY=34.4666 EndZ=0
    g1: ArcOfCircle CenterX=19 CenterY=19.2524 CenterZ=0 NormalX=0 NormalY=0 NormalZ=1 AngleXU=0 Radius=15.4476 StartAngle=1.74483 EndAngle=2.72717
    g2: ArcOfCircle CenterX=19 CenterY=19.2524 CenterZ=0 NormalX=0 NormalY=0 NormalZ=1 AngleXU=0 Radius=12.4476 StartAngle=1.74483 EndAngle=2.73189
    g3: LineSegment StartX=4.86004 StartY=25.4725 StartZ=0 EndX=7.58253 EndY=24.2107 EndZ=0
  constraints (7):
    c: Block(g0)
    c: Coincident(g1,g0)
    c: Coincident(g2,g0)
    c: Coincident(g3,g1)
    c: Coincident(g3,g2)
    c: Block(g1)
    c: Block(g2)
FEATURE [Part::Extrusion] Extrude041
  Base = -> Sketch050
  Dir = (0,0,1)
  DirMode = 2
  FaceMakerClass = Part::FaceMakerBullseye
  LengthFwd = 10.6
  LengthRev = 0
  Placement = pos=(0,0,31) rot=(0,0,1;0rad)
  Solid = true
  Symmetric = false
FEATURE [Part::Cut] Cut035
  Base = -> Extrude041
  Placement = pos=(0,0,-0.3) rot=(0,0,1;0rad)
  Tool = -> Fusion080
FEATURE [Part::Cut] Cut036
  Base = -> Box023
  Tool = -> Cut035
FEATURE [Part::Fillet] Fillet027
  Base = -> Cut036
  Edges = 1 edges r=0.7: [Edge13]
FEATURE [Part::Fillet] Fillet028
  Base = -> Fillet027
  Edges = 1 edges r=0.7: [Edge13]
FEATURE [Part::Fillet] Fillet029
  Base = -> Fillet028
  Edges = 1 edges r=0.7: [Edge16]
FEATURE [Part::Fillet] Fillet030
  Base = -> Fillet029
  Edges = 1 edges r=0.7: [Edge11]
FEATURE [Part::Fillet] Fillet031
  Base = -> Fillet030
  Edges = 1 edges r=0.7: [Edge10]
FEATURE [Part::Fillet] Fillet032
  Base = -> Fillet031
  Edges = 1 edges r=1.2: [Edge5]
FEATURE [Part::Fillet] Fillet033
  Base = -> Fillet032
  Edges = 1 edges r=1.2: [Edge12]
FEATURE [Part::Fillet] Fillet034  label="wireHousingRetainer"
  Base = -> Fillet033
  Edges = 1 edges r=2: [Edge1]
  Placement = pos=(0.3,0,0) rot=(0,0,1;0rad)
FEATURE [Part::Feature] Face099
  shape: bbox 3.5 x 17.8 x 2e-07 mm, 1 faces, 0 solids (baked)
FEATURE [Part::Revolution] Revolve107  label="removeToCreateScrewAndThreadedInsertHole034"
  Angle = 360
  Axis = (0,1,0)
  Base = (0,0,0)
  FaceMakerClass = Part::FaceMakerBullseye
  Placement = pos=(12.5,0,10) rot=(0,0,1;0rad)
  Solid = false
  Source = -> Face099
  Symmetric = false
FEATURE [Part::Feature] Face100
  shape: bbox 3.5 x 17.8 x 2e-07 mm, 1 faces, 0 solids (baked)
FEATURE [Part::Revolution] Revolve108  label="removeToCreateScrewAndThreadedInsertHole035"
  Angle = 360
  Axis = (0,1,0)
  Base = (0,0,0)
  FaceMakerClass = Part::FaceMakerBullseye
  Placement = pos=(12.5,0,62) rot=(0,0,1;0rad)
  Solid = false
  Source = -> Face100
  Symmetric = false
FEATURE [Part::Feature] Face101
  shape: bbox 3.5 x 17.8 x 2e-07 mm, 1 faces, 0 solids (baked)
FEATURE [Part::Revolution] Revolve109  label="removeToCreateScrewAndThreadedInsertHole036"
  Angle = 360
  Axis = (0,1,0)
  Base = (0,0,0)
  FaceMakerClass = Part::FaceMakerBullseye
  Placement = pos=(89.5,0,68.5) rot=(0,0,1;0rad)
  Solid = false
  Source = -> Face101
  Symmetric = false
FEATURE [Part::Feature] Face102
  shape: bbox 3.5 x 17.8 x 2e-07 mm, 1 faces, 0 solids (baked)
FEATURE [Part::Revolution] Revolve110  label="removeToCreateScrewAndThreadedInsertHole037"
  Angle = 360
  Axis = (0,1,0)
  Base = (0,0,0)
  FaceMakerClass = Part::FaceMakerBullseye
  Placement = pos=(89.5,0,3.5) rot=(0,0,1;0rad)
  Solid = false
  Source = -> Face102
  Symmetric = false
FEATURE [Part::Feature] Face103
  shape: bbox 3.5 x 17.8 x 2e-07 mm, 1 faces, 0 solids (baked)
FEATURE [Part::Revolution] Revolve111  label="removeToCreateScrewAndThreadedInsertHole038"
  Angle = 360
  Axis = (0,1,0)
  Base = (0,0,0)
  FaceMakerClass = Part::FaceMakerBullseye
  Placement = pos=(109.5,4.7,3.5) rot=(0,0,1;0rad)
  Solid = false
  Source = -> Face103
  Symmetric = false
FEATURE [Part::Feature] Face104
  shape: bbox 3.5 x 17.8 x 2e-07 mm, 1 faces, 0 solids (baked)
FEATURE [Part::Revolution] Revolve112  label="removeToCreateScrewAndThreadedInsertHole039"
  Angle = 360
  Axis = (0,1,0)
  Base = (0,0,0)
  FaceMakerClass = Part::FaceMakerBullseye
  Placement = pos=(109.5,4.7,68.5) rot=(0,0,1;0rad)
  Solid = false
  Source = -> Face104
  Symmetric = false
FEATURE [Part::MultiFuse] Fusion081  label="removeToCreateScrewAndThreadedInsertHole040"
  Shapes = -> [Revolve107,Revolve108,Revolve109,Revolve110,Revolve111,Revolve112]
FEATURE [Part::MultiFuse] Fusion082  label="casePillars002"
  Shapes = -> [Revolve094,Revolve092,Revolve090,Revolve089,Revolve091,Revolve093]
FEATURE [Part::Cut] Cut037  label="casePillars003"
  Base = -> Fusion082
  Tool = -> Fusion081
FEATURE [Sketcher::SketchObject] Sketch051
  FullyConstrained = true
  Placement = pos=(117,19,0) rot=(0.57735,0.57735,0.57735;2.0944rad)
  sketch-geometry (48):
    g0: LineSegment StartX=-49.19 StartY=69.25 StartZ=0 EndX=-49.19 EndY=66.25 EndZ=0
    g1: LineSegment StartX=-49.19 StartY=63.5 StartZ=0 EndX=-49.19 EndY=60.5 EndZ=0
    g2: LineSegment StartX=-49.19 StartY=57.75 StartZ=0 EndX=-49.19 EndY=54.75 EndZ=0
    g3: LineSegment StartX=-49.19 StartY=52 StartZ=0 EndX=-49.19 EndY=49 EndZ=0
    g4: LineSegment StartX=-49.19 StartY=46.25 StartZ=0 EndX=-49.19 EndY=43.25 EndZ=0
    g5: LineSegment StartX=-49.19 StartY=40.5 StartZ=0 EndX=-49.19 EndY=37.5 EndZ=0
    g6: LineSegment StartX=-49.19 StartY=34.5 StartZ=0 EndX=-49.19 EndY=31.5 EndZ=0
    g7: LineSegment StartX=-49.19 StartY=28.75 StartZ=0 EndX=-49.19 EndY=25.75 EndZ=0
    g8: LineSegment StartX=-49.19 StartY=23 StartZ=0 EndX=-49.19 EndY=20 EndZ=0
    g9: LineSegment StartX=-49.19 StartY=17.25 StartZ=0 EndX=-49.19 EndY=14.25 EndZ=0
    g10: LineSegment StartX=-49.19 StartY=11.5 StartZ=0 EndX=-49.19 EndY=8.5 EndZ=0
    g11: LineSegment StartX=-49.19 StartY=5.75 StartZ=0 EndX=-49.19 EndY=2.75 EndZ=0
    g12: ArcOfCircle CenterX=-1.5 CenterY=67.75 CenterZ=0 NormalX=0 NormalY=0 NormalZ=1 AngleXU=0 Radius=1.5 StartAngle=4.71239 EndAngle=7.85398
    g13: ArcOfCircle CenterX=-1.5 CenterY=62 CenterZ=0 NormalX=0 NormalY=0 NormalZ=1 AngleXU=0 Radius=1.5 StartAngle=4.71239 EndAngle=7.85398
    g14: ArcOfCircle CenterX=-1.5 CenterY=56.25 CenterZ=0 NormalX=0 NormalY=0 NormalZ=1 AngleXU=0 Radius=1.5 StartAngle=4.71239 EndAngle=7.85398
    g15: ArcOfCircle CenterX=-11.49 CenterY=50.5 CenterZ=0 NormalX=0 NormalY=0 NormalZ=1 AngleXU=0 Radius=1.5 StartAngle=4.71239 EndAngle=7.85398
    g16: ArcOfCircle CenterX=-16.28 CenterY=44.75 CenterZ=0 NormalX=0 NormalY=0 NormalZ=1 AngleXU=0 Radius=1.5 StartAngle=4.71239 EndAngle=7.85398
    g17: ArcOfCircle CenterX=-18.2337 CenterY=39 CenterZ=0 NormalX=0 NormalY=0 NormalZ=1 AngleXU=0 Radius=1.5 StartAngle=4.71485 EndAngle=7.85398
    g18: ArcOfCircle CenterX=-16.2837 CenterY=27.25 CenterZ=0 NormalX=0 NormalY=0 NormalZ=1 AngleXU=0 Radius=1.5 StartAngle=4.71485 EndAngle=7.85398
    g19: ArcOfCircle CenterX=-18.2337 CenterY=33 CenterZ=0 NormalX=0 NormalY=0 NormalZ=1 AngleXU=0 Radius=1.5 StartAngle=4.71485 EndAngle=7.85398
    g20: ArcOfCircle CenterX=-11.49 CenterY=21.5 CenterZ=0 NormalX=0 NormalY=0 NormalZ=1 AngleXU=0 Radius=1.5 StartAngle=4.71239 EndAngle=7.85398
    g21: ArcOfCircle CenterX=-1.5 CenterY=4.25 CenterZ=0 NormalX=0 NormalY=0 NormalZ=1 AngleXU=0 Radius=1.5 StartAngle=4.71239 EndAngle=7.85398
    g22: ArcOfCircle CenterX=-1.5 CenterY=10 CenterZ=0 NormalX=0 NormalY=0 NormalZ=1 AngleXU=0 Radius=1.5 StartAngle=4.71239 EndAngle=7.85398
    g23: ArcOfCircle CenterX=-1.5 CenterY=15.75 CenterZ=0 NormalX=0 NormalY=0 NormalZ=1 AngleXU=0 Radius=1.5 StartAngle=4.71239 EndAngle=7.85398
    g24: LineSegment StartX=-49.19 StartY=69.25 StartZ=0 EndX=-1.5 EndY=69.25 EndZ=0
    g25: LineSegment StartX=-49.19 StartY=66.25 StartZ=0 EndX=-1.5 EndY=66.25 EndZ=0
    g26: LineSegment StartX=-49.19 StartY=63.5 StartZ=0 EndX=-1.5 EndY=63.5 EndZ=0
    g27: LineSegment StartX=-49.19 StartY=60.5 StartZ=0 EndX=-1.5 EndY=60.5 EndZ=0
    g28: LineSegment StartX=-49.19 StartY=57.75 StartZ=0 EndX=-1.5 EndY=57.75 EndZ=0
    g29: LineSegment StartX=-49.19 StartY=54.75 StartZ=0 EndX=-1.5 EndY=54.75 EndZ=0
    g30: LineSegment StartX=-49.19 StartY=52 StartZ=0 EndX=-11.49 EndY=52 EndZ=0
    g31: LineSegment StartX=-49.19 StartY=49 StartZ=0 EndX=-11.49 EndY=49 EndZ=0
    g32: LineSegment StartX=-49.19 StartY=46.25 StartZ=0 EndX=-16.28 EndY=46.25 EndZ=0
    g33: LineSegment StartX=-49.19 StartY=43.25 StartZ=0 EndX=-16.28 EndY=43.25 EndZ=0
    g34: LineSegment StartX=-49.19 StartY=40.5 StartZ=0 EndX=-18.2337 EndY=40.5 EndZ=0
    g35: LineSegment StartX=-49.19 StartY=37.5 StartZ=0 EndX=-18.23 EndY=37.5 EndZ=0
    g36: LineSegment StartX=-49.19 StartY=34.5 StartZ=0 EndX=-18.2337 EndY=34.5 EndZ=0
    g37: LineSegment StartX=-49.19 StartY=31.5 StartZ=0 EndX=-18.23 EndY=31.5 EndZ=0
    g38: LineSegment StartX=-49.19 StartY=28.75 StartZ=0 EndX=-16.2837 EndY=28.75 EndZ=0
    g39: LineSegment StartX=-49.19 StartY=25.75 StartZ=0 EndX=-16.28 EndY=25.75 EndZ=0
    g40: LineSegment StartX=-49.19 StartY=23 StartZ=0 EndX=-11.49 EndY=23 EndZ=0
    g41: LineSegment StartX=-49.19 StartY=20 StartZ=0 EndX=-11.49 EndY=20 EndZ=0
    g42: LineSegment StartX=-49.19 StartY=17.25 StartZ=0 EndX=-1.5 EndY=17.25 EndZ=0
    g43: LineSegment StartX=-49.19 StartY=14.25 StartZ=0 EndX=-1.5 EndY=14.25 EndZ=0
    g44: LineSegment StartX=-49.19 StartY=11.5 StartZ=0 EndX=-1.5 EndY=11.5 EndZ=0
    g45: LineSegment StartX=-49.19 StartY=8.5 StartZ=0 EndX=-1.5 EndY=8.5 EndZ=0
    g46: LineSegment StartX=-49.19 StartY=5.75 StartZ=0 EndX=-1.5 EndY=5.75 EndZ=0
    g47: LineSegment StartX=-49.19 StartY=2.75 StartZ=0 EndX=-1.5 EndY=2.75 EndZ=0
  constraints (120):
    c: Vertical(g0)
    c: Distance(g0) = 3
    c: Block(g0)
    c: Vertical(g1)
    c: Distance(g1) = 3
    c: Vertical(g2)
    c: Equal(g0,g2) = 3
    c: Block(g2)
    c: Vertical(g3)
    c: Equal(g1,g3) = 3
    c: Vertical(g4)
    c: Equal(g0,g4) = 3
    c: Block(g4)
    c: Vertical(g5)
    c: Equal(g1,g5) = 3
    c: Vertical(g6)
    c: Equal(g0,g6) = 3
    c: Block(g6)
    c: Vertical(g7)
    c: Equal(g1,g7) = 3
    c: Vertical(g8)
    c: Equal(g0,g8) = 3
    c: Block(g8)
    c: Vertical(g9)
    c: Equal(g1,g9) = 3
    c: Vertical(g10)
    c: Equal(g0,g10) = 3
    c: Block(g10)
    c: Vertical(g11)
    c: Equal(g1,g11) = 3
    c: Block(g12)
    c: Block(g13)
    c: Block(g14)
    c: Block(g15)
    c: Block(g16)
    c: Block(g17)
    c: Block(g18)
    c: Block(g19)
    c: Block(g20)
    c: Block(g21)
    c: Block(g22)
    c: Block(g23)
    c: Block(g11)
    c: Block(g9)
    c: Block(g7)
    c: Block(g5)
    c: Block(g3)
    c: Block(g1)
    c: Coincident(g24,g0)
    c: Coincident(g24,g12)
    c: Horizontal(g24)
    c: Coincident(g25,g0)
    c: Coincident(g25,g12)
    c: Horizontal(g25)
    c: Coincident(g26,g1)
    c: Coincident(g26,g13)
    c: Horizontal(g26)
    c: Coincident(g27,g1)
    c: Coincident(g27,g13)
    c: Horizontal(g27)
    c: Coincident(g28,g2)
    c: Coincident(g28,g14)
    c: Horizontal(g28)
    c: Coincident(g29,g2)
    c: Coincident(g29,g14)
    c: Horizontal(g29)
    c: Coincident(g30,g3)
    c: Coincident(g30,g15)
    c: Horizontal(g30)
    c: Coincident(g31,g3)
    c: Coincident(g31,g15)
    c: Horizontal(g31)
    c: Coincident(g32,g4)
    c: Coincident(g32,g16)
    c: Horizontal(g32)
    c: Coincident(g33,g4)
    c: Coincident(g33,g16)
    c: Horizontal(g33)
    c: Coincident(g34,g5)
    c: Coincident(g34,g17)
    c: Horizontal(g34)
    c: Coincident(g35,g5)
    c: Coincident(g35,g17)
    c: Horizontal(g35)
    c: Coincident(g36,g6)
    c: Coincident(g36,g19)
    c: Horizontal(g36)
    c: Coincident(g37,g6)
    c: Coincident(g37,g19)
    c: Horizontal(g37)
    c: Coincident(g38,g7)
    c: Coincident(g38,g18)
    c: Horizontal(g38)
    c: Coincident(g39,g7)
    c: Coincident(g39,g18)
    c: Horizontal(g39)
    c: Coincident(g40,g8)
    c: Coincident(g40,g20)
    c: Horizontal(g40)
    c: Coincident(g41,g8)
    c: Coincident(g41,g20)
    c: Horizontal(g41)
    c: Coincident(g42,g9)
    c: Coincident(g42,g23)
    c: Horizontal(g42)
    c: Coincident(g43,g9)
    c: Coincident(g43,g23)
    c: Horizontal(g43)
    c: Coincident(g44,g10)
    c: Coincident(g44,g22)
    c: Horizontal(g44)
    c: Coincident(g45,g10)
    c: Coincident(g45,g22)
    c: Horizontal(g45)
    c: Coincident(g46,g11)
    c: Coincident(g46,g21)
    c: Horizontal(g46)
    c: Coincident(g47,g11)
    c: Coincident(g47,g21)
    c: Horizontal(g47)
FEATURE [Part::Extrusion] Extrude042
  Base = -> Sketch051
  Dir = (1,-2e-16,2e-16)
  DirMode = 2
  FaceMakerClass = Part::FaceMakerBullseye
  LengthFwd = 19
  LengthRev = 0
  Placement = pos=(-19,0,0) rot=(0,0,1;0rad)
  Solid = true
  Symmetric = false
FEATURE [Part::Fillet] Fillet035  label="removeToCreateVentalationHoles"
  Base = -> Extrude042
  Edges = <same value as first occurrence — deduplicated (x6 in doc)>
  Placement = pos=(7,0,0) rot=(0,0,1;0rad)
FEATURE [Part::Cut] Cut038  label="top017"
  Base = -> Cut033
  Tool = -> Fillet035
FEATURE [Sketcher::SketchObject] Sketch052  label="bottomSketch001"
  FullyConstrained = true
  sketch-geometry (45):
    g0: LineSegment StartX=6.29999 StartY=8 StartZ=0 EndX=3.29999 EndY=8 EndZ=0
    g1: LineSegment StartX=3.29999 StartY=8 StartZ=0 EndX=3.29999 EndY=-6.03275e-07 EndZ=0
    g2: ArcOfCircle CenterX=8.29999 CenterY=5 CenterZ=0 NormalX=0 NormalY=0 NormalZ=1 AngleXU=0 Radius=2 StartAngle=3.14159 EndAngle=4.71239
    g3: LineSegment StartX=6.29999 StartY=8 StartZ=0 EndX=6.29999 EndY=5 EndZ=0
    g4: ArcOfCircle CenterX=105 CenterY=19 CenterZ=0 NormalX=0 NormalY=0 NormalZ=1 AngleXU=0 Radius=12.7 StartAngle=4.71239 EndAngle=5.94289
    g5-g11: Circle x7 (B-spline internal-alignment scaffolding for g12; pole/knot coordinates omitted)
    g12: BSplineCurve PolesCount=7 KnotsCount=5 Degree=3 IsPeriodic=0
    g13-g17: GeomPoint x5 (B-spline internal-alignment scaffolding for g12; pole/knot coordinates omitted)
    g18: ArcOfCircle CenterX=105 CenterY=19 CenterZ=0 NormalX=0 NormalY=0 NormalZ=1 AngleXU=0 Radius=15.7 StartAngle=5.81226 EndAngle=6.28319
    g19: BSplineCurve PolesCount=5 KnotsCount=3 Degree=3 IsPeriodic=0
    g20: LineSegment StartX=8.29999 StartY=3 StartZ=0 EndX=101.7 EndY=3 EndZ=0
    g21: LineSegment StartX=3.29999 StartY=-6.03275e-07 StartZ=0 EndX=105 EndY=-6.03275e-07 EndZ=0
    g22: LineSegment StartX=120.974 StartY=8.71251 StartZ=0 EndX=122.332 EndY=7.83778 EndZ=0
    g23: LineSegment StartX=105 StartY=-6.03274e-07 StartZ=0 EndX=113 EndY=-6.03274e-07 EndZ=0
    g24: ArcOfCircle CenterX=105 CenterY=19 CenterZ=0 NormalX=0 NormalY=0 NormalZ=1 AngleXU=0 Radius=20.6155 StartAngle=5.11091 EndAngle=5.71103
    g25: ArcOfCircle CenterX=117.7 CenterY=19 CenterZ=0 NormalX=0 NormalY=0 NormalZ=1 AngleXU=0 Radius=3 StartAngle=1.2e-15 EndAngle=2.10468
    g26: Circle CenterX=116.345 CenterY=16.3232 CenterZ=0 NormalX=0 NormalY=0 NormalZ=1 AngleXU=0 Radius=1
    g27: Circle CenterX=117.24 CenterY=15.7584 CenterZ=0 NormalX=0 NormalY=0 NormalZ=1 AngleXU=0 Radius=1
    g28: Circle CenterX=116.972 CenterY=14.7612 CenterZ=0 NormalX=0 NormalY=0 NormalZ=1 AngleXU=0 Radius=1
    g29: BSplineCurve PolesCount=3 KnotsCount=2 Degree=2 IsPeriodic=0
    g30: GeomPoint X=116.345 Y=16.3232 Z=0
    g31: GeomPoint X=116.972 Y=14.7612 Z=0
    g32: Circle CenterX=115.828 CenterY=17.157 CenterZ=0 NormalX=0 NormalY=0 NormalZ=1 AngleXU=0 Radius=1
    g33: Circle CenterX=115.841 CenterY=16.639 CenterZ=0 NormalX=0 NormalY=0 NormalZ=1 AngleXU=0 Radius=1
    g34: Circle CenterX=116.345 CenterY=16.3232 CenterZ=0 NormalX=0 NormalY=0 NormalZ=1 AngleXU=0 Radius=1
    g35: BSplineCurve PolesCount=3 KnotsCount=2 Degree=2 IsPeriodic=0
    g36: GeomPoint X=115.828 Y=17.157 Z=0
    g37: GeomPoint X=116.345 Y=16.3232 Z=0
    g38: LineSegment StartX=115.828 StartY=17.157 StartZ=0 EndX=115.828 EndY=20.8307 EndZ=0
    g39: Circle CenterX=115.828 CenterY=20.8307 CenterZ=0 NormalX=0 NormalY=0 NormalZ=1 AngleXU=0 Radius=1
    g40: Circle CenterX=115.831 CenterY=21.3396 CenterZ=0 NormalX=0 NormalY=0 NormalZ=1 AngleXU=0 Radius=1
    g41: Circle CenterX=116.173 CenterY=21.5825 CenterZ=0 NormalX=0 NormalY=0 NormalZ=1 AngleXU=0 Radius=1
    g42: BSplineCurve PolesCount=3 KnotsCount=2 Degree=2 IsPeriodic=0
    g43: GeomPoint X=115.828 Y=20.8307 Z=0
    g44: GeomPoint X=116.173 Y=21.5825 Z=0
  constraints (70):
    c: Horizontal(g0)
    c: Distance(g0) = 3
    c: Coincident(g1,g0)
    c: Vertical(g1)
    c: Block(g2)
    c: Block(g0)
    c: Coincident(g3,g0)
    c: Coincident(g3,g2)
    c: Vertical(g3)
    c: Block(g1)
    c: Block(g4)
    c: Coincident(g19,g4)
    c: Block(g19)
    c: Equal(g5, g6-g11) x6
    c: InternalAlignment(g5-g11 -> g12) x7
    c: InternalAlignment(g13-g17 -> g12) x5
    c: Block(g12)
    c: Coincident(g18,g12)
    c: Block(g18)
    c: Coincident(g20,g2)
    c: Coincident(g20,g19)
    c: Horizontal(g20)
    c: Distance(g20) = 93.4
    c: Coincident(g21,g1)
    c: Horizontal(g21)
    c: Distance(g21) = 101.7
    c: Horizontal(g23)
    c: Distance(g23) = 8
    c: Coincident(g24,g23)
    c: Block(g23)
    c: Coincident(g22,g24)
    c: Block(g24)
    c: Block(g22)
    c: Distance(g22) = 1.61553
    c: Coincident(g25,g18)
    c: Block(g25)
    c: Weight(g26) = 1
    c: Equal(g26,g27)
    c: Equal(g26,g28)
    c: Coincident(g29,g4)
    c: InternalAlignment(g26,g29)
    c: InternalAlignment(g27,g29)
    c: InternalAlignment(g28,g29)
    c: InternalAlignment(g30,g29)
    c: InternalAlignment(g31,g29)
    c: Block(g29)
    c: Weight(g32) = 1
    c: Equal(g32,g33)
    c: Equal(g32,g34)
    c: Coincident(g35,g29)
    c: InternalAlignment(g32,g35)
    c: InternalAlignment(g33,g35)
    c: InternalAlignment(g34,g35)
    c: InternalAlignment(g36,g35)
    c: InternalAlignment(g37,g35)
    c: Block(g35)
    c: Coincident(g38,g35)
    c: Vertical(g38)
    c: Block(g38)
    c: Coincident(g42,g38)
    c: Weight(g39) = 1
    c: Equal(g39,g40)
    c: Equal(g39,g41)
    c: Coincident(g42,g25)
    c: InternalAlignment(g39,g42)
    c: InternalAlignment(g40,g42)
    c: InternalAlignment(g41,g42)
    c: InternalAlignment(g43,g42)
    c: InternalAlignment(g44,g42)
    c: Block(g42)
FEATURE [Part::Extrusion] Extrude043  label="bottom010"
  Base = -> Sketch052
  Dir = (0,0,1)
  DirMode = 2
  FaceMakerClass = Part::FaceMakerBullseye
  LengthFwd = 71.4
  LengthRev = 0
  Placement = pos=(0,0,0.3) rot=(0,0,1;0rad)
  Solid = true
  Symmetric = false
FEATURE [Sketcher::SketchObject] Sketch053  label="topSketch013"
  FullyConstrained = true
  sketch-geometry (22):
    g0: LineSegment StartX=5.21097e-06 StartY=3 StartZ=0 EndX=5.21097e-06 EndY=19 EndZ=0
    g1: ArcOfCircle CenterX=19 CenterY=19 CenterZ=0 NormalX=0 NormalY=0 NormalZ=1 AngleXU=0 Radius=19 StartAngle=1.5708 EndAngle=3.14159
    g2: ArcOfCircle CenterX=19 CenterY=19 CenterZ=0 NormalX=0 NormalY=0 NormalZ=1 AngleXU=0 Radius=16 StartAngle=1.5708 EndAngle=3.14159
    g3: LineSegment StartX=114 StartY=35 StartZ=0 EndX=19 EndY=35 EndZ=0
    g4: LineSegment StartX=5.21097e-06 StartY=3 StartZ=0 EndX=5.21097e-06 EndY=0 EndZ=0
    g5: LineSegment StartX=3 StartY=0 StartZ=0 EndX=5.21097e-06 EndY=0 EndZ=0
    g6: LineSegment StartX=3 StartY=19 StartZ=0 EndX=3 EndY=0 EndZ=0
    g7: LineSegment StartX=19 StartY=38 StartZ=0 EndX=124 EndY=38 EndZ=0
    g8: Circle CenterX=119 CenterY=35 CenterZ=0 NormalX=0 NormalY=0 NormalZ=1 AngleXU=0 Radius=1
    g9: Circle CenterX=121 CenterY=35 CenterZ=0 NormalX=0 NormalY=0 NormalZ=1 AngleXU=0 Radius=1
    g10: Circle CenterX=121 CenterY=33 CenterZ=0 NormalX=0 NormalY=0 NormalZ=1 AngleXU=0 Radius=1
    g11: BSplineCurve PolesCount=3 KnotsCount=2 Degree=2 IsPeriodic=0
    g12: GeomPoint X=119 Y=35 Z=0
    g13: GeomPoint X=121 Y=33 Z=0
    g14: LineSegment StartX=119 StartY=35 StartZ=0 EndX=114 EndY=35 EndZ=0
    g15: ArcOfCircle CenterX=105 CenterY=19 CenterZ=0 NormalX=0 NormalY=0 NormalZ=1 AngleXU=0 Radius=16 StartAngle=5.60905 EndAngle=6.28319
    g16: LineSegment StartX=121 StartY=33 StartZ=0 EndX=121 EndY=19 EndZ=0
    g17: LineSegment StartX=117.5 StartY=9.01251 StartZ=0 EndX=121.163 EndY=9.0125 EndZ=0
    g18: ArcOfCircle CenterX=105 CenterY=19 CenterZ=0 NormalX=0 NormalY=0 NormalZ=1 AngleXU=0 Radius=20.6155 StartAngle=5.7297 EndAngle=6.28319
    g19: LineSegment StartX=121.163 StartY=9.0125 StartZ=0 EndX=122.538 EndY=8.16329 EndZ=0
    g20: LineSegment StartX=124 StartY=38 StartZ=0 EndX=125.616 EndY=38 EndZ=0
    g21: LineSegment StartX=125.616 StartY=19 StartZ=0 EndX=125.616 EndY=38 EndZ=0
  constraints (50):
    c: Vertical(g0)
    c: Block(g0)
    c: Coincident(g1,g0)
    c: Block(g1)
    c: Coincident(g2,g1)
    c: Block(g2)
    c: Coincident(g3,g2)
    c: Horizontal(g3)
    c: Tangent(g3,g2)
    c: Coincident(g4,g0)
    c: Distance(g4) = 3
    c: Vertical(g4)
    c: Coincident(g5,g4)
    c: Horizontal(g5)
    c: Coincident(g6,g2)
    c: Coincident(g6,g5)
    c: Vertical(g6)
    c: Horizontal(g7)
    c: Distance(g7) = 105
    c: Coincident(g7,g1)
    c: Block(g3)
    c: Weight(g8) = 1
    c: Equal(g8,g9)
    c: Equal(g8,g10)
    c: InternalAlignment(g8,g11)
    c: InternalAlignment(g9,g11)
    c: InternalAlignment(g10,g11)
    c: InternalAlignment(g12,g11)
    c: InternalAlignment(g13,g11)
    c: Block(g11)
    c: Coincident(g14,g11)
    c: Coincident(g14,g3)
    c: Horizontal(g14)
    c: Block(g15)
    c: Coincident(g16,g11)
    c: Coincident(g16,g15)
    c: Vertical(g16)
    c: Distance(g16) = 14
    c: Coincident(g17,g15)
    c: Block(g18)
    c: Coincident(g19,g18)
    c: Coincident(g20,g7)
    c: Horizontal(g20)
    c: Vertical(g21)
    c: Coincident(g20,g21)
    c: Block(g20)
    c: Block(g21)
    c: Block(g19)
    c: Block(g17)
    c: Distance(g20) = 1.61553
FEATURE [Part::Extrusion] Extrude044
  Base = -> Sketch053
  Dir = (0,0,1)
  DirMode = 2
  FaceMakerClass = Part::FaceMakerBullseye
  LengthFwd = 72
  LengthRev = 0
  Solid = true
  Symmetric = false
FEATURE [Part::Fillet] Fillet036  label="top018"
  Base = -> Extrude044
  Edges = 1 edges r=2: [Edge41]
FEATURE [Sketcher::SketchObject] Sketch054
  FullyConstrained = false
  Placement = pos=(0,0,0) rot=(1,0,0;1.5708rad)
  sketch-geometry (24):
    g0: ArcOfCircle CenterX=-4 CenterY=-10.5 CenterZ=0 NormalX=0 NormalY=0 NormalZ=1 AngleXU=0 Radius=1.5 StartAngle=6e-16 EndAngle=3.14159
    g1: ArcOfCircle CenterX=-34.2 CenterY=-10.5 CenterZ=0 NormalX=0 NormalY=0 NormalZ=1 AngleXU=0 Radius=1.5 StartAngle=0 EndAngle=3.14159
    g2: ArcOfCircle CenterX=-34.2 CenterY=-27.7 CenterZ=0 NormalX=0 NormalY=0 NormalZ=1 AngleXU=0 Radius=1.5 StartAngle=3.14159 EndAngle=6.28319
    g3: ArcOfCircle CenterX=-4 CenterY=-27.7 CenterZ=0 NormalX=0 NormalY=0 NormalZ=1 AngleXU=0 Radius=1.5 StartAngle=3.1416 EndAngle=6.28319
    g4: ArcOfCircle CenterX=-10 CenterY=-4.3 CenterZ=0 NormalX=0 NormalY=0 NormalZ=1 AngleXU=0 Radius=1.5 StartAngle=2e-16 EndAngle=3.14159
    g5: ArcOfCircle CenterX=-16.1 CenterY=-1.8 CenterZ=0 NormalX=0 NormalY=0 NormalZ=1 AngleXU=0 Radius=1.5 StartAngle=5e-16 EndAngle=3.14159
    g6: ArcOfCircle CenterX=-22.1 CenterY=-1.8 CenterZ=0 NormalX=0 NormalY=0 NormalZ=1 AngleXU=0 Radius=1.5 StartAngle=5e-16 EndAngle=3.14159
    g7: ArcOfCircle CenterX=-28.2 CenterY=-4.3 CenterZ=0 NormalX=0 NormalY=0 NormalZ=1 AngleXU=0 Radius=1.5 StartAngle=2e-16 EndAngle=3.14159
    g8: ArcOfCircle CenterX=-10 CenterY=-33.9 CenterZ=0 NormalX=0 NormalY=0 NormalZ=1 AngleXU=0 Radius=1.5 StartAngle=3.14159 EndAngle=6.28319
    g9: ArcOfCircle CenterX=-16.1 CenterY=-36.4 CenterZ=0 NormalX=0 NormalY=0 NormalZ=1 AngleXU=0 Radius=1.5 StartAngle=3.14159 EndAngle=6.28319
    g10: ArcOfCircle CenterX=-22.1 CenterY=-36.4 CenterZ=0 NormalX=0 NormalY=0 NormalZ=1 AngleXU=0 Radius=1.5 StartAngle=3.14159 EndAngle=6.28319
    g11: ArcOfCircle CenterX=-28.2 CenterY=-33.9 CenterZ=0 NormalX=0 NormalY=0 NormalZ=1 AngleXU=0 Radius=1.5 StartAngle=3.14159 EndAngle=6.28319
    g12: LineSegment StartX=-35.7 StartY=-10.5 StartZ=0 EndX=-35.7 EndY=-27.7 EndZ=0
    g13: LineSegment StartX=-32.7 StartY=-10.5 StartZ=0 EndX=-32.7 EndY=-27.7 EndZ=0
    g14: LineSegment StartX=-29.7 StartY=-33.9 StartZ=0 EndX=-29.7 EndY=-4.3 EndZ=0
    g15: LineSegment StartX=-26.7 StartY=-33.9 StartZ=0 EndX=-26.7 EndY=-4.3 EndZ=0
    g16: LineSegment StartX=-2.5 StartY=-10.5 StartZ=0 EndX=-2.5 EndY=-27.7 EndZ=0
    g17: LineSegment StartX=-8.5 StartY=-4.3 StartZ=0 EndX=-8.5 EndY=-33.9 EndZ=0
    g18: LineSegment StartX=-5.5 StartY=-10.5 StartZ=0 EndX=-5.5 EndY=-27.7 EndZ=0
    g19: LineSegment StartX=-11.5 StartY=-4.3 StartZ=0 EndX=-11.5 EndY=-33.9 EndZ=0
    g20: LineSegment StartX=-14.6 StartY=-1.8 StartZ=0 EndX=-14.6 EndY=-36.4 EndZ=0
    g21: LineSegment StartX=-17.6 StartY=-1.8 StartZ=0 EndX=-17.6 EndY=-36.4 EndZ=0
    g22: LineSegment StartX=-20.6 StartY=-36.4 StartZ=0 EndX=-20.6 EndY=-1.8 EndZ=0
    g23: LineSegment StartX=-23.6 StartY=-1.8 StartZ=0 EndX=-23.6 EndY=-36.4 EndZ=0
  constraints (48):
    c: Block(g0)
    c: Block(g1)
    c: Block(g2)
    c: Block(g3)
    c: Block(g4)
    c: Block(g5)
    c: Block(g6)
    c: Block(g7)
    c: Block(g8)
    c: Block(g9)
    c: Block(g10)
    c: Block(g11)
    c: Coincident(g12,g1)
    c: Coincident(g12,g2)
    c: Vertical(g12)
    c: Coincident(g13,g1)
    c: Coincident(g13,g2)
    c: Vertical(g13)
    c: Coincident(g14,g11)
    c: Coincident(g14,g7)
    c: Vertical(g14)
    c: Coincident(g15,g11)
    c: Coincident(g15,g7)
    c: Vertical(g15)
    c: Coincident(g16,g0)
    c: Coincident(g16,g3)
    c: Vertical(g16)
    c: Coincident(g17,g4)
    c: Coincident(g17,g8)
    c: Vertical(g17)
    c: Coincident(g18,g0)
    c: Coincident(g18,g3)
    c: Vertical(g18)
    c: Coincident(g19,g4)
    c: Coincident(g19,g8)
    c: Vertical(g19)
    c: Coincident(g20,g5)
    c: Coincident(g20,g9)
    c: Vertical(g20)
    c: Coincident(g21,g5)
    c: Coincident(g21,g9)
    c: Vertical(g21)
    c: Coincident(g22,g10)
    c: Coincident(g22,g6)
    c: Vertical(g22)
    c: Coincident(g23,g6)
    c: Coincident(g23,g10)
    c: Vertical(g23)
FEATURE [Part::Extrusion] Extrude045  label="removeToCreateFanGrillHoles003"
  Base = -> Sketch054
  Dir = (0,-1,6e-16)
  DirMode = 2
  FaceMakerClass = Part::FaceMakerBullseye
  LengthFwd = 10
  LengthRev = 0
  Placement = pos=(65.4,44,54.82) rot=(0,0,1;0rad)
  Solid = true
  Symmetric = false
FEATURE [Part::Feature] Face105 .. Face108  x4 (patterned run collapsed; names and placements below)
  shape: bbox 3.5 x 17.8 x 2e-07 mm, 1 faces, 0 solids (baked)
FEATURE [Part::Revolution] Revolve113  label="removeToCreateScrewAndThreadedInsertHole041"
  Angle = 360
  Axis = (0,1,0)
  Base = (0,0,0)
  FaceMakerClass = Part::FaceMakerBullseye
  Placement = pos=(62.3,30.3,19.7) rot=(0,0,1;0rad)
  Solid = false
  Source = -> Face105
  Symmetric = false
FEATURE [Part::Revolution] Revolve114  label="removeToCreateScrewAndThreadedInsertHole042"
  Angle = 360
  Axis = (0,1,0)
  Base = (0,0,0)
  FaceMakerClass = Part::FaceMakerBullseye
  Placement = pos=(62.3,30.3,51.7) rot=(0,0,1;0rad)
  Solid = false
  Source = -> Face106
  Symmetric = false
FEATURE [Part::Revolution] Revolve115  label="removeToCreateScrewAndThreadedInsertHole043"
  Angle = 360
  Axis = (0,1,0)
  Base = (0,0,0)
  FaceMakerClass = Part::FaceMakerBullseye
  Placement = pos=(30.3,30.3,19.7) rot=(0,0,1;0rad)
  Solid = false
  Source = -> Face107
  Symmetric = false
FEATURE [Part::Revolution] Revolve116  label="removeToCreateScrewAndThreadedInsertHole044"
  Angle = 360
  Axis = (0,1,0)
  Base = (0,0,0)
  FaceMakerClass = Part::FaceMakerBullseye
  Placement = pos=(30.3,30.3,51.7) rot=(0,0,1;0rad)
  Solid = false
  Source = -> Face108
  Symmetric = false
FEATURE [Part::MultiFuse] Fusion083  label="createThreadedInsertHolesForFan004"
  Shapes = -> [Revolve113,Revolve114,Revolve115,Revolve116]
FEATURE [Part::Box] Box024  label="removeToCreteHoleForPlugHousing026"
  AttacherType = Attacher::AttachEngine3D
  Height = 28.6
  Length = 10
  Placement = pos=(-2,0,21.7) rot=(0,0,1;0rad)
  Width = 19
FEATURE [Part::Cylinder] Cylinder038  label="removeToCreteHoleForPlugHousing027"
  Angle = 360
  AttacherType = Attacher::AttachEngine3D
  Height = 20
  Placement = pos=(-2,19,36) rot=(0,1,0;1.5708rad)
  Radius = 14.3
FEATURE [Part::MultiFuse] Fusion084  label="removeToCreteHoleForPlugHousing028"
  Shapes = -> [Box024,Cylinder038]
FEATURE [Part::Cylinder] Cylinder039
  Angle = 360
  AttacherType = Attacher::AttachEngine3D
  Height = 20
  Placement = pos=(0,0,36.15) rot=(0,0,1;0rad)
  Radius = 14.3
FEATURE [Part::Cylinder] Cylinder040
  Angle = 360
  AttacherType = Attacher::AttachEngine3D
  Height = 10
  Placement = pos=(0,0,36.15) rot=(0,0,1;0rad)
  Radius = 4
FEATURE [Part::Box] Box025  label="removeToCreteHoleForPlugHousing030"
  AttacherType = Attacher::AttachEngine3D
  Height = 28.6
  Length = 20
  Placement = pos=(106.15,0,21.7) rot=(0,0,1;0rad)
  Width = 19
FEATURE [Part::MultiFuse] Fusion086  label="removeToCreteHoleForPlugHousing031"
  Placement = pos=(70,19,36) rot=(0,1,0;1.5708rad)
  Shapes = -> [Cylinder039,Cylinder040]
FEATURE [Part::MultiFuse] Fusion085  label="removeToCreteHoleForPlugHousing029"
  Shapes = -> [Box025,Fusion086]
FEATURE [Sketcher::SketchObject] Sketch055
  FullyConstrained = true
  Placement = pos=(117,19,0) rot=(0.57735,0.57735,0.57735;2.0944rad)
  sketch-geometry (48):
    g0: LineSegment StartX=-49.19 StartY=69.25 StartZ=0 EndX=-49.19 EndY=66.25 EndZ=0
    g1: LineSegment StartX=-49.19 StartY=63.5 StartZ=0 EndX=-49.19 EndY=60.5 EndZ=0
    g2: LineSegment StartX=-49.19 StartY=57.75 StartZ=0 EndX=-49.19 EndY=54.75 EndZ=0
    g3: LineSegment StartX=-49.19 StartY=52 StartZ=0 EndX=-49.19 EndY=49 EndZ=0
    g4: LineSegment StartX=-49.19 StartY=46.25 StartZ=0 EndX=-49.19 EndY=43.25 EndZ=0
    g5: LineSegment StartX=-49.19 StartY=40.5 StartZ=0 EndX=-49.19 EndY=37.5 EndZ=0
    g6: LineSegment StartX=-49.19 StartY=34.5 StartZ=0 EndX=-49.19 EndY=31.5 EndZ=0
    g7: LineSegment StartX=-49.19 StartY=28.75 StartZ=0 EndX=-49.19 EndY=25.75 EndZ=0
    g8: LineSegment StartX=-49.19 StartY=23 StartZ=0 EndX=-49.19 EndY=20 EndZ=0
    g9: LineSegment StartX=-49.19 StartY=17.25 StartZ=0 EndX=-49.19 EndY=14.25 EndZ=0
    g10: LineSegment StartX=-49.19 StartY=11.5 StartZ=0 EndX=-49.19 EndY=8.5 EndZ=0
    g11: LineSegment StartX=-49.19 StartY=5.75 StartZ=0 EndX=-49.19 EndY=2.75 EndZ=0
    g12: ArcOfCircle CenterX=-1.5 CenterY=67.75 CenterZ=0 NormalX=0 NormalY=0 NormalZ=1 AngleXU=0 Radius=1.5 StartAngle=4.71239 EndAngle=7.85398
    g13: ArcOfCircle CenterX=-1.5 CenterY=62 CenterZ=0 NormalX=0 NormalY=0 NormalZ=1 AngleXU=0 Radius=1.5 StartAngle=4.71239 EndAngle=7.85398
    g14: ArcOfCircle CenterX=-1.5 CenterY=56.25 CenterZ=0 NormalX=0 NormalY=0 NormalZ=1 AngleXU=0 Radius=1.5 StartAngle=4.71239 EndAngle=7.85398
    g15: ArcOfCircle CenterX=-11.49 CenterY=50.5 CenterZ=0 NormalX=0 NormalY=0 NormalZ=1 AngleXU=0 Radius=1.5 StartAngle=4.71239 EndAngle=7.85398
    g16: ArcOfCircle CenterX=-16.28 CenterY=44.75 CenterZ=0 NormalX=0 NormalY=0 NormalZ=1 AngleXU=0 Radius=1.5 StartAngle=4.71239 EndAngle=7.85398
    g17: ArcOfCircle CenterX=-18.2337 CenterY=39 CenterZ=0 NormalX=0 NormalY=0 NormalZ=1 AngleXU=0 Radius=1.5 StartAngle=4.71485 EndAngle=7.85398
    g18: ArcOfCircle CenterX=-16.2837 CenterY=27.25 CenterZ=0 NormalX=0 NormalY=0 NormalZ=1 AngleXU=0 Radius=1.5 StartAngle=4.71485 EndAngle=7.85398
    g19: ArcOfCircle CenterX=-18.2337 CenterY=33 CenterZ=0 NormalX=0 NormalY=0 NormalZ=1 AngleXU=0 Radius=1.5 StartAngle=4.71485 EndAngle=7.85398
    g20: ArcOfCircle CenterX=-11.49 CenterY=21.5 CenterZ=0 NormalX=0 NormalY=0 NormalZ=1 AngleXU=0 Radius=1.5 StartAngle=4.71239 EndAngle=7.85398
    g21: ArcOfCircle CenterX=-1.5 CenterY=4.25 CenterZ=0 NormalX=0 NormalY=0 NormalZ=1 AngleXU=0 Radius=1.5 StartAngle=4.71239 EndAngle=7.85398
    g22: ArcOfCircle CenterX=-1.5 CenterY=10 CenterZ=0 NormalX=0 NormalY=0 NormalZ=1 AngleXU=0 Radius=1.5 StartAngle=4.71239 EndAngle=7.85398
    g23: ArcOfCircle CenterX=-1.5 CenterY=15.75 CenterZ=0 NormalX=0 NormalY=0 NormalZ=1 AngleXU=0 Radius=1.5 StartAngle=4.71239 EndAngle=7.85398
    g24: LineSegment StartX=-49.19 StartY=69.25 StartZ=0 EndX=-1.5 EndY=69.25 EndZ=0
    g25: LineSegment StartX=-49.19 StartY=66.25 StartZ=0 EndX=-1.5 EndY=66.25 EndZ=0
    g26: LineSegment StartX=-49.19 StartY=63.5 StartZ=0 EndX=-1.5 EndY=63.5 EndZ=0
    g27: LineSegment StartX=-49.19 StartY=60.5 StartZ=0 EndX=-1.5 EndY=60.5 EndZ=0
    g28: LineSegment StartX=-49.19 StartY=57.75 StartZ=0 EndX=-1.5 EndY=57.75 EndZ=0
    g29: LineSegment StartX=-49.19 StartY=54.75 StartZ=0 EndX=-1.5 EndY=54.75 EndZ=0
    g30: LineSegment StartX=-49.19 StartY=52 StartZ=0 EndX=-11.49 EndY=52 EndZ=0
    g31: LineSegment StartX=-49.19 StartY=49 StartZ=0 EndX=-11.49 EndY=49 EndZ=0
    g32: LineSegment StartX=-49.19 StartY=46.25 StartZ=0 EndX=-16.28 EndY=46.25 EndZ=0
    g33: LineSegment StartX=-49.19 StartY=43.25 StartZ=0 EndX=-16.28 EndY=43.25 EndZ=0
    g34: LineSegment StartX=-49.19 StartY=40.5 StartZ=0 EndX=-18.2337 EndY=40.5 EndZ=0
    g35: LineSegment StartX=-49.19 StartY=37.5 StartZ=0 EndX=-18.23 EndY=37.5 EndZ=0
    g36: LineSegment StartX=-49.19 StartY=34.5 StartZ=0 EndX=-18.2337 EndY=34.5 EndZ=0
    g37: LineSegment StartX=-49.19 StartY=31.5 StartZ=0 EndX=-18.23 EndY=31.5 EndZ=0
    g38: LineSegment StartX=-49.19 StartY=28.75 StartZ=0 EndX=-16.2837 EndY=28.75 EndZ=0
    g39: LineSegment StartX=-49.19 StartY=25.75 StartZ=0 EndX=-16.28 EndY=25.75 EndZ=0
    g40: LineSegment StartX=-49.19 StartY=23 StartZ=0 EndX=-11.49 EndY=23 EndZ=0
    g41: LineSegment StartX=-49.19 StartY=20 StartZ=0 EndX=-11.49 EndY=20 EndZ=0
    g42: LineSegment StartX=-49.19 StartY=17.25 StartZ=0 EndX=-1.5 EndY=17.25 EndZ=0
    g43: LineSegment StartX=-49.19 StartY=14.25 StartZ=0 EndX=-1.5 EndY=14.25 EndZ=0
    g44: LineSegment StartX=-49.19 StartY=11.5 StartZ=0 EndX=-1.5 EndY=11.5 EndZ=0
    g45: LineSegment StartX=-49.19 StartY=8.5 StartZ=0 EndX=-1.5 EndY=8.5 EndZ=0
    g46: LineSegment StartX=-49.19 StartY=5.75 StartZ=0 EndX=-1.5 EndY=5.75 EndZ=0
    g47: LineSegment StartX=-49.19 StartY=2.75 StartZ=0 EndX=-1.5 EndY=2.75 EndZ=0
  constraints (120):
    c: Vertical(g0)
    c: Distance(g0) = 3
    c: Block(g0)
    c: Vertical(g1)
    c: Distance(g1) = 3
    c: Vertical(g2)
    c: Equal(g0,g2) = 3
    c: Block(g2)
    c: Vertical(g3)
    c: Equal(g1,g3) = 3
    c: Vertical(g4)
    c: Equal(g0,g4) = 3
    c: Block(g4)
    c: Vertical(g5)
    c: Equal(g1,g5) = 3
    c: Vertical(g6)
    c: Equal(g0,g6) = 3
    c: Block(g6)
    c: Vertical(g7)
    c: Equal(g1,g7) = 3
    c: Vertical(g8)
    c: Equal(g0,g8) = 3
    c: Block(g8)
    c: Vertical(g9)
    c: Equal(g1,g9) = 3
    c: Vertical(g10)
    c: Equal(g0,g10) = 3
    c: Block(g10)
    c: Vertical(g11)
    c: Equal(g1,g11) = 3
    c: Block(g12)
    c: Block(g13)
    c: Block(g14)
    c: Block(g15)
    c: Block(g16)
    c: Block(g17)
    c: Block(g18)
    c: Block(g19)
    c: Block(g20)
    c: Block(g21)
    c: Block(g22)
    c: Block(g23)
    c: Block(g11)
    c: Block(g9)
    c: Block(g7)
    c: Block(g5)
    c: Block(g3)
    c: Block(g1)
    c: Coincident(g24,g0)
    c: Coincident(g24,g12)
    c: Horizontal(g24)
    c: Coincident(g25,g0)
    c: Coincident(g25,g12)
    c: Horizontal(g25)
    c: Coincident(g26,g1)
    c: Coincident(g26,g13)
    c: Horizontal(g26)
    c: Coincident(g27,g1)
    c: Coincident(g27,g13)
    c: Horizontal(g27)
    c: Coincident(g28,g2)
    c: Coincident(g28,g14)
    c: Horizontal(g28)
    c: Coincident(g29,g2)
    c: Coincident(g29,g14)
    c: Horizontal(g29)
    c: Coincident(g30,g3)
    c: Coincident(g30,g15)
    c: Horizontal(g30)
    c: Coincident(g31,g3)
    c: Coincident(g31,g15)
    c: Horizontal(g31)
    c: Coincident(g32,g4)
    c: Coincident(g32,g16)
    c: Horizontal(g32)
    c: Coincident(g33,g4)
    c: Coincident(g33,g16)
    c: Horizontal(g33)
    c: Coincident(g34,g5)
    c: Coincident(g34,g17)
    c: Horizontal(g34)
    c: Coincident(g35,g5)
    c: Coincident(g35,g17)
    c: Horizontal(g35)
    c: Coincident(g36,g6)
    c: Coincident(g36,g19)
    c: Horizontal(g36)
    c: Coincident(g37,g6)
    c: Coincident(g37,g19)
    c: Horizontal(g37)
    c: Coincident(g38,g7)
    c: Coincident(g38,g18)
    c: Horizontal(g38)
    c: Coincident(g39,g7)
    c: Coincident(g39,g18)
    c: Horizontal(g39)
    c: Coincident(g40,g8)
    c: Coincident(g40,g20)
    c: Horizontal(g40)
    c: Coincident(g41,g8)
    c: Coincident(g41,g20)
    c: Horizontal(g41)
    c: Coincident(g42,g9)
    c: Coincident(g42,g23)
    c: Horizontal(g42)
    c: Coincident(g43,g9)
    c: Coincident(g43,g23)
    c: Horizontal(g43)
    c: Coincident(g44,g10)
    c: Coincident(g44,g22)
    c: Horizontal(g44)
    c: Coincident(g45,g10)
    c: Coincident(g45,g22)
    c: Horizontal(g45)
    c: Coincident(g46,g11)
    c: Coincident(g46,g21)
    c: Horizontal(g46)
    c: Coincident(g47,g11)
    c: Coincident(g47,g21)
    c: Horizontal(g47)
FEATURE [Part::Extrusion] Extrude046
  Base = -> Sketch055
  Dir = (1,0,0)
  DirMode = 2
  FaceMakerClass = Part::FaceMakerBullseye
  LengthFwd = 23
  LengthRev = 0
  Placement = pos=(-19,0,0) rot=(0,0,1;0rad)
  Solid = true
  Symmetric = false
FEATURE [Part::Fillet] Fillet038  label="removeToCreateVentalationHoles001"
  Base = -> Extrude046
  Edges = <same value as first occurrence — deduplicated (x6 in doc)>
  Placement = pos=(7,0,0) rot=(0,0,1;0rad)
FEATURE [Sketcher::SketchObject] Sketch056  label="topSketch014"
  FullyConstrained = true
  sketch-geometry (22):
    g0: LineSegment StartX=5.21097e-06 StartY=3 StartZ=0 EndX=5.21097e-06 EndY=19 EndZ=0
    g1: ArcOfCircle CenterX=19 CenterY=19 CenterZ=0 NormalX=0 NormalY=0 NormalZ=1 AngleXU=0 Radius=19 StartAngle=1.5708 EndAngle=3.14159
    g2: ArcOfCircle CenterX=19 CenterY=19 CenterZ=0 NormalX=0 NormalY=0 NormalZ=1 AngleXU=0 Radius=16 StartAngle=1.5708 EndAngle=3.14159
    g3: LineSegment StartX=114 StartY=35 StartZ=0 EndX=19 EndY=35 EndZ=0
    g4: LineSegment StartX=5.21097e-06 StartY=3 StartZ=0 EndX=5.21097e-06 EndY=0 EndZ=0
    g5: LineSegment StartX=3 StartY=0 StartZ=0 EndX=5.21097e-06 EndY=0 EndZ=0
    g6: LineSegment StartX=3 StartY=19 StartZ=0 EndX=3 EndY=0 EndZ=0
    g7: LineSegment StartX=19 StartY=38 StartZ=0 EndX=124 EndY=38 EndZ=0
    g8: Circle CenterX=119 CenterY=35 CenterZ=0 NormalX=0 NormalY=0 NormalZ=1 AngleXU=0 Radius=1
    g9: Circle CenterX=121 CenterY=35 CenterZ=0 NormalX=0 NormalY=0 NormalZ=1 AngleXU=0 Radius=1
    g10: Circle CenterX=121 CenterY=33 CenterZ=0 NormalX=0 NormalY=0 NormalZ=1 AngleXU=0 Radius=1
    g11: BSplineCurve PolesCount=3 KnotsCount=2 Degree=2 IsPeriodic=0
    g12: GeomPoint X=119 Y=35 Z=0
    g13: GeomPoint X=121 Y=33 Z=0
    g14: LineSegment StartX=119 StartY=35 StartZ=0 EndX=114 EndY=35 EndZ=0
    g15: ArcOfCircle CenterX=105 CenterY=19 CenterZ=0 NormalX=0 NormalY=0 NormalZ=1 AngleXU=0 Radius=16 StartAngle=5.60905 EndAngle=6.28319
    g16: LineSegment StartX=121 StartY=33 StartZ=0 EndX=121 EndY=19 EndZ=0
    g17: LineSegment StartX=117.5 StartY=9.01251 StartZ=0 EndX=121.163 EndY=9.0125 EndZ=0
    g18: ArcOfCircle CenterX=105 CenterY=19 CenterZ=0 NormalX=0 NormalY=0 NormalZ=1 AngleXU=0 Radius=20.6155 StartAngle=5.7297 EndAngle=6.28319
    g19: LineSegment StartX=121.163 StartY=9.0125 StartZ=0 EndX=122.538 EndY=8.16329 EndZ=0
    g20: LineSegment StartX=124 StartY=38 StartZ=0 EndX=125.616 EndY=38 EndZ=0
    g21: LineSegment StartX=125.616 StartY=19 StartZ=0 EndX=125.616 EndY=38 EndZ=0
  constraints (49):
    c: Vertical(g0)
    c: Block(g0)
    c: Coincident(g1,g0)
    c: Block(g1)
    c: Coincident(g2,g1)
    c: Block(g2)
    c: Coincident(g3,g2)
    c: Horizontal(g3)
    c: Tangent(g3,g2)
    c: Coincident(g4,g0)
    c: Distance(g4) = 3
    c: Vertical(g4)
    c: Coincident(g5,g4)
    c: Horizontal(g5)
    c: Coincident(g6,g2)
    c: Coincident(g6,g5)
    c: Vertical(g6)
    c: Horizontal(g7)
    c: Distance(g7) = 105
    c: Coincident(g7,g1)
    c: Block(g3)
    c: Weight(g8) = 1
    c: Equal(g8,g9)
    c: Equal(g8,g10)
    c: InternalAlignment(g8,g11)
    c: InternalAlignment(g9,g11)
    c: InternalAlignment(g10,g11)
    c: InternalAlignment(g12,g11)
    c: InternalAlignment(g13,g11)
    c: Block(g11)
    c: Coincident(g14,g11)
    c: Coincident(g14,g3)
    c: Horizontal(g14)
    c: Block(g15)
    c: Coincident(g16,g11)
    c: Coincident(g16,g15)
    c: Vertical(g16)
    c: Distance(g16) = 14
    c: Coincident(g17,g15)
    c: Block(g18)
    c: Coincident(g19,g18)
    c: Coincident(g20,g7)
    c: Horizontal(g20)
    c: Vertical(g21)
    c: Coincident(g20,g21)
    c: Block(g20)
    c: Block(g21)
    c: Block(g19)
    c: Block(g17)
FEATURE [Part::Box] Box026  label="removeToCreteHoleForPlugHousing032"
  AttacherType = Attacher::AttachEngine3D
  Height = 28.6
  Length = 10
  Placement = pos=(-2,0,21.7) rot=(0,0,1;0rad)
  Width = 19
FEATURE [Part::Feature] Face109 .. Face112  x4 (patterned run collapsed; names and placements below)
  shape: bbox 3.5 x 17.8 x 2e-07 mm, 1 faces, 0 solids (baked)
FEATURE [Part::Revolution] Revolve117  label="removeToCreateScrewAndThreadedInsertHole045"
  Angle = 360
  Axis = (0,1,0)
  Base = (0,0,0)
  FaceMakerClass = Part::FaceMakerBullseye
  Placement = pos=(62.3,30.3,19.7) rot=(0,0,1;0rad)
  Solid = false
  Source = -> Face109
  Symmetric = false
FEATURE [Part::Revolution] Revolve118  label="removeToCreateScrewAndThreadedInsertHole046"
  Angle = 360
  Axis = (0,1,0)
  Base = (0,0,0)
  FaceMakerClass = Part::FaceMakerBullseye
  Placement = pos=(62.3,30.3,51.7) rot=(0,0,1;0rad)
  Solid = false
  Source = -> Face110
  Symmetric = false
FEATURE [Part::Revolution] Revolve119  label="removeToCreateScrewAndThreadedInsertHole047"
  Angle = 360
  Axis = (0,1,0)
  Base = (0,0,0)
  FaceMakerClass = Part::FaceMakerBullseye
  Placement = pos=(30.3,30.3,19.7) rot=(0,0,1;0rad)
  Solid = false
  Source = -> Face111
  Symmetric = false
FEATURE [Part::Revolution] Revolve120  label="removeToCreateScrewAndThreadedInsertHole048"
  Angle = 360
  Axis = (0,1,0)
  Base = (0,0,0)
  FaceMakerClass = Part::FaceMakerBullseye
  Placement = pos=(30.3,30.3,51.7) rot=(0,0,1;0rad)
  Solid = false
  Source = -> Face112
  Symmetric = false
FEATURE [Part::MultiFuse] Fusion087  label="createThreadedInsertHolesForFan005"
  Shapes = -> [Revolve117,Revolve118,Revolve119,Revolve120]
FEATURE [Part::Extrusion] Extrude047
  Base = -> Sketch056
  Dir = (0,0,1)
  DirMode = 2
  FaceMakerClass = Part::FaceMakerBullseye
  LengthFwd = 72
  LengthRev = 0
  Solid = true
  Symmetric = false
FEATURE [Part::Fillet] Fillet039  label="top019"
  Base = -> Extrude047
  Edges = 1 edges r=2: [Edge35]
FEATURE [Sketcher::SketchObject] Sketch057
  FullyConstrained = false
  Placement = pos=(0,0,0) rot=(1,0,0;1.5708rad)
  sketch-geometry (24):
    g0: ArcOfCircle CenterX=-4 CenterY=-10.5 CenterZ=0 NormalX=0 NormalY=0 NormalZ=1 AngleXU=0 Radius=1.5 StartAngle=6e-16 EndAngle=3.14159
    g1: ArcOfCircle CenterX=-34.2 CenterY=-10.5 CenterZ=0 NormalX=0 NormalY=0 NormalZ=1 AngleXU=0 Radius=1.5 StartAngle=0 EndAngle=3.14159
    g2: ArcOfCircle CenterX=-34.2 CenterY=-27.7 CenterZ=0 NormalX=0 NormalY=0 NormalZ=1 AngleXU=0 Radius=1.5 StartAngle=3.14159 EndAngle=6.28319
    g3: ArcOfCircle CenterX=-4 CenterY=-27.7 CenterZ=0 NormalX=0 NormalY=0 NormalZ=1 AngleXU=0 Radius=1.5 StartAngle=3.1416 EndAngle=6.28319
    g4: ArcOfCircle CenterX=-10 CenterY=-4.3 CenterZ=0 NormalX=0 NormalY=0 NormalZ=1 AngleXU=0 Radius=1.5 StartAngle=2e-16 EndAngle=3.14159
    g5: ArcOfCircle CenterX=-16.1 CenterY=-1.8 CenterZ=0 NormalX=0 NormalY=0 NormalZ=1 AngleXU=0 Radius=1.5 StartAngle=5e-16 EndAngle=3.14159
    g6: ArcOfCircle CenterX=-22.1 CenterY=-1.8 CenterZ=0 NormalX=0 NormalY=0 NormalZ=1 AngleXU=0 Radius=1.5 StartAngle=5e-16 EndAngle=3.14159
    g7: ArcOfCircle CenterX=-28.2 CenterY=-4.3 CenterZ=0 NormalX=0 NormalY=0 NormalZ=1 AngleXU=0 Radius=1.5 StartAngle=2e-16 EndAngle=3.14159
    g8: ArcOfCircle CenterX=-10 CenterY=-33.9 CenterZ=0 NormalX=0 NormalY=0 NormalZ=1 AngleXU=0 Radius=1.5 StartAngle=3.14159 EndAngle=6.28319
    g9: ArcOfCircle CenterX=-16.1 CenterY=-36.4 CenterZ=0 NormalX=0 NormalY=0 NormalZ=1 AngleXU=0 Radius=1.5 StartAngle=3.14159 EndAngle=6.28319
    g10: ArcOfCircle CenterX=-22.1 CenterY=-36.4 CenterZ=0 NormalX=0 NormalY=0 NormalZ=1 AngleXU=0 Radius=1.5 StartAngle=3.14159 EndAngle=6.28319
    g11: ArcOfCircle CenterX=-28.2 CenterY=-33.9 CenterZ=0 NormalX=0 NormalY=0 NormalZ=1 AngleXU=0 Radius=1.5 StartAngle=3.14159 EndAngle=6.28319
    g12: LineSegment StartX=-35.7 StartY=-10.5 StartZ=0 EndX=-35.7 EndY=-27.7 EndZ=0
    g13: LineSegment StartX=-32.7 StartY=-10.5 StartZ=0 EndX=-32.7 EndY=-27.7 EndZ=0
    g14: LineSegment StartX=-29.7 StartY=-33.9 StartZ=0 EndX=-29.7 EndY=-4.3 EndZ=0
    g15: LineSegment StartX=-26.7 StartY=-33.9 StartZ=0 EndX=-26.7 EndY=-4.3 EndZ=0
    g16: LineSegment StartX=-2.5 StartY=-10.5 StartZ=0 EndX=-2.5 EndY=-27.7 EndZ=0
    g17: LineSegment StartX=-8.5 StartY=-4.3 StartZ=0 EndX=-8.5 EndY=-33.9 EndZ=0
    g18: LineSegment StartX=-5.5 StartY=-10.5 StartZ=0 EndX=-5.5 EndY=-27.7 EndZ=0
    g19: LineSegment StartX=-11.5 StartY=-4.3 StartZ=0 EndX=-11.5 EndY=-33.9 EndZ=0
    g20: LineSegment StartX=-14.6 StartY=-1.8 StartZ=0 EndX=-14.6 EndY=-36.4 EndZ=0
    g21: LineSegment StartX=-17.6 StartY=-1.8 StartZ=0 EndX=-17.6 EndY=-36.4 EndZ=0
    g22: LineSegment StartX=-20.6 StartY=-36.4 StartZ=0 EndX=-20.6 EndY=-1.8 EndZ=0
    g23: LineSegment StartX=-23.6 StartY=-1.8 StartZ=0 EndX=-23.6 EndY=-36.4 EndZ=0
  constraints (48):
    c: Block(g0)
    c: Block(g1)
    c: Block(g2)
    c: Block(g3)
    c: Block(g4)
    c: Block(g5)
    c: Block(g6)
    c: Block(g7)
    c: Block(g8)
    c: Block(g9)
    c: Block(g10)
    c: Block(g11)
    c: Coincident(g12,g1)
    c: Coincident(g12,g2)
    c: Vertical(g12)
    c: Coincident(g13,g1)
    c: Coincident(g13,g2)
    c: Vertical(g13)
    c: Coincident(g14,g11)
    c: Coincident(g14,g7)
    c: Vertical(g14)
    c: Coincident(g15,g11)
    c: Coincident(g15,g7)
    c: Vertical(g15)
    c: Coincident(g16,g0)
    c: Coincident(g16,g3)
    c: Vertical(g16)
    c: Coincident(g17,g4)
    c: Coincident(g17,g8)
    c: Vertical(g17)
    c: Coincident(g18,g0)
    c: Coincident(g18,g3)
    c: Vertical(g18)
    c: Coincident(g19,g4)
    c: Coincident(g19,g8)
    c: Vertical(g19)
    c: Coincident(g20,g5)
    c: Coincident(g20,g9)
    c: Vertical(g20)
    c: Coincident(g21,g5)
    c: Coincident(g21,g9)
    c: Vertical(g21)
    c: Coincident(g22,g10)
    c: Coincident(g22,g6)
    c: Vertical(g22)
    c: Coincident(g23,g6)
    c: Coincident(g23,g10)
    c: Vertical(g23)
FEATURE [Part::Extrusion] Extrude048  label="removeToCreateFanGrillHoles004"
  Base = -> Sketch057
  Dir = (0,-1,6e-16)
  DirMode = 2
  FaceMakerClass = Part::FaceMakerBullseye
  LengthFwd = 10
  LengthRev = 0
  Placement = pos=(65.4,44,54.82) rot=(0,0,1;0rad)
  Solid = true
  Symmetric = false
FEATURE [Part::Cut] Cut040  label="top021"
  Base = -> Fillet039
  Tool = -> Extrude048
FEATURE [Part::Cylinder] Cylinder041  label="removeToCreteHoleForPlugHousing034"
  Angle = 360
  AttacherType = Attacher::AttachEngine3D
  Height = 20
  Placement = pos=(-2,19,36) rot=(0,1,0;1.5708rad)
  Radius = 14.3
FEATURE [Part::MultiFuse] Fusion089  label="removeToCreteHoleForPlugHousing035"
  Shapes = -> [Box026,Cylinder041]
FEATURE [Part::Cylinder] Cylinder042
  Angle = 360
  AttacherType = Attacher::AttachEngine3D
  Height = 20
  Placement = pos=(0,0,36.15) rot=(0,0,1;0rad)
  Radius = 14.3
FEATURE [Part::Cylinder] Cylinder043
  Angle = 360
  AttacherType = Attacher::AttachEngine3D
  Height = 10
  Placement = pos=(0,0,36.15) rot=(0,0,1;0rad)
  Radius = 4
FEATURE [Part::Box] Box027  label="removeToCreteHoleForPlugHousing036"
  AttacherType = Attacher::AttachEngine3D
  Height = 28.6
  Length = 20
  Placement = pos=(106.15,0,21.7) rot=(0,0,1;0rad)
  Width = 19
FEATURE [Part::Cut] Cut041  label="top022"
  Base = -> Cut040
  Tool = -> Fusion087
FEATURE [Part::Cut] Cut039  label="top020"
  Base = -> Cut041
  Tool = -> Fusion089
FEATURE [Part::MultiFuse] Fusion090  label="removeToCreteHoleForPlugHousing037"
  Placement = pos=(70,19,36) rot=(0,1,0;1.5708rad)
  Shapes = -> [Cylinder042,Cylinder043]
FEATURE [Part::MultiFuse] Fusion088  label="removeToCreteHoleForPlugHousing033"
  Shapes = -> [Box027,Fusion090]
FEATURE [Part::Cut] Cut042  label="removeToCreteHoleForPlugHousing038"
  Base = -> Cut039
  Tool = -> Fusion088
FEATURE [Part::MultiFuse] Fusion091  label="removeFromTop"
  Shapes = -> [Fillet038,Fusion085,Fusion084,Fusion083,Extrude045]
FEATURE [Part::Cut] Cut043  label="REAL TOP ====="
  Base = -> Fillet036
  Tool = -> Fusion091
FEATURE [Part::MultiFuse] Fusion092  label="caseScrewPillarBracket016"
  Shapes = -> [Extrude030,Extrude031,Extrude032,Extrude033,Extrude034,Extrude035,Extrude036,Extrude037,Box013,Box014]
FEATURE [Sketcher::SketchObject] Sketch058  label="topSketch015"
  FullyConstrained = true
  sketch-geometry (20):
    g0: LineSegment StartX=5.21097e-06 StartY=3 StartZ=0 EndX=5.21097e-06 EndY=19 EndZ=0
    g1: ArcOfCircle CenterX=19 CenterY=19 CenterZ=0 NormalX=0 NormalY=0 NormalZ=1 AngleXU=0 Radius=19 StartAngle=1.5708 EndAngle=3.14159
    g2: ArcOfCircle CenterX=19 CenterY=19 CenterZ=0 NormalX=0 NormalY=0 NormalZ=1 AngleXU=0 Radius=16 StartAngle=1.5708 EndAngle=3.14159
    g3: LineSegment StartX=114 StartY=35 StartZ=0 EndX=19 EndY=35 EndZ=0
    g4: LineSegment StartX=5.21097e-06 StartY=3 StartZ=0 EndX=5.21097e-06 EndY=0 EndZ=0
    g5: LineSegment StartX=3 StartY=0 StartZ=0 EndX=5.21097e-06 EndY=0 EndZ=0
    g6: LineSegment StartX=3 StartY=19 StartZ=0 EndX=3 EndY=0 EndZ=0
    g7: LineSegment StartX=19 StartY=38 StartZ=0 EndX=124 EndY=38 EndZ=0
    g8: Circle CenterX=119 CenterY=35 CenterZ=0 NormalX=0 NormalY=0 NormalZ=1 AngleXU=0 Radius=1
    g9: Circle CenterX=121 CenterY=35 CenterZ=0 NormalX=0 NormalY=0 NormalZ=1 AngleXU=0 Radius=1
    g10: Circle CenterX=121 CenterY=33 CenterZ=0 NormalX=0 NormalY=0 NormalZ=1 AngleXU=0 Radius=1
    g11: BSplineCurve PolesCount=3 KnotsCount=2 Degree=2 IsPeriodic=0
    g12: GeomPoint X=119 Y=35 Z=0
    g13: GeomPoint X=121 Y=33 Z=0
    g14: LineSegment StartX=119 StartY=35 StartZ=0 EndX=114 EndY=35 EndZ=0
    g15: ArcOfCircle CenterX=105 CenterY=19 CenterZ=0 NormalX=0 NormalY=0 NormalZ=1 AngleXU=0 Radius=19 StartAngle=5.7297 EndAngle=6.28319
    g16: ArcOfCircle CenterX=105 CenterY=19 CenterZ=0 NormalX=0 NormalY=0 NormalZ=1 AngleXU=0 Radius=16 StartAngle=5.60905 EndAngle=6.28319
    g17: LineSegment StartX=121 StartY=33 StartZ=0 EndX=121 EndY=19 EndZ=0
    g18: LineSegment StartX=124 StartY=38 StartZ=0 EndX=124 EndY=19 EndZ=0
    g19: LineSegment StartX=117.5 StartY=9.01251 StartZ=0 EndX=121.163 EndY=9.0125 EndZ=0
  constraints (46):
    c: Vertical(g0)
    c: Block(g0)
    c: Coincident(g1,g0)
    c: Block(g1)
    c: Coincident(g2,g1)
    c: Block(g2)
    c: Coincident(g3,g2)
    c: Horizontal(g3)
    c: Tangent(g3,g2)
    c: Coincident(g4,g0)
    c: Distance(g4) = 3
    c: Vertical(g4)
    c: Coincident(g5,g4)
    c: Horizontal(g5)
    c: Coincident(g6,g2)
    c: Coincident(g6,g5)
    c: Vertical(g6)
    c: Horizontal(g7)
    c: Distance(g7) = 105
    c: Coincident(g7,g1)
    c: Block(g3)
    c: Weight(g8) = 1
    c: Equal(g8,g9)
    c: Equal(g8,g10)
    c: InternalAlignment(g8,g11)
    c: InternalAlignment(g9,g11)
    c: InternalAlignment(g10,g11)
    c: InternalAlignment(g12,g11)
    c: InternalAlignment(g13,g11)
    c: Block(g11)
    c: Coincident(g14,g11)
    c: Coincident(g14,g3)
    c: Horizontal(g14)
    c: Block(g15)
    c: Coincident(g16,g15)
    c: Block(g16)
    c: Coincident(g17,g11)
    c: Coincident(g17,g16)
    c: Vertical(g17)
    c: Distance(g17) = 14
    c: Coincident(g18,g7)
    c: Coincident(g18,g15)
    c: Vertical(g18)
    c: Distance(g18) = 19
    c: Coincident(g19,g16)
    c: Coincident(g19,g15)
FEATURE [Part::Extrusion] Extrude049  label="top023"
  Base = -> Sketch058
  Dir = (0,0,1)
  DirMode = 2
  FaceMakerClass = Part::FaceMakerBullseye
  LengthFwd = 72
  LengthRev = 0
  Solid = true
  Symmetric = false
FEATURE [Sketcher::SketchObject] Sketch059
  FullyConstrained = true
  MapMode = 3
  Placement = pos=(0,0,0) rot=(1,0,0;1.5708rad)
  Support = -> [Extrude049]
  sketch-geometry (8):
    g0: Circle CenterX=80.351 CenterY=-67.6202 CenterZ=0 NormalX=0 NormalY=0 NormalZ=1 AngleXU=0 Radius=2
    g1: Circle CenterX=80.351 CenterY=-67.6202 CenterZ=0 NormalX=0 NormalY=0 NormalZ=1 AngleXU=0 Radius=3
    g2: Circle CenterX=80.351 CenterY=-4.92017 CenterZ=0 NormalX=0 NormalY=0 NormalZ=1 AngleXU=0 Radius=2
    g3: Circle CenterX=80.351 CenterY=-4.92017 CenterZ=0 NormalX=0 NormalY=0 NormalZ=1 AngleXU=0 Radius=3
    g4: Circle CenterX=23.851 CenterY=-4.92017 CenterZ=0 NormalX=0 NormalY=0 NormalZ=1 AngleXU=0 Radius=2
    g5: Circle CenterX=23.851 CenterY=-4.92017 CenterZ=0 NormalX=0 NormalY=0 NormalZ=1 AngleXU=0 Radius=3
    g6: Circle CenterX=23.851 CenterY=-67.6202 CenterZ=0 NormalX=0 NormalY=0 NormalZ=1 AngleXU=0 Radius=2
    g7: Circle CenterX=23.851 CenterY=-67.6202 CenterZ=0 NormalX=0 NormalY=0 NormalZ=1 AngleXU=0 Radius=3
  constraints (8):
    c: Block(g3)
    c: Block(g2)
    c: Block(g1)
    c: Block(g0)
    c: Block(g6)
    c: Block(g7)
    c: Block(g4)
    c: Block(g5)
FEATURE [Sketcher::SketchObject] Sketch060
  FullyConstrained = true
  MapMode = 3
  Placement = pos=(0,0,0) rot=(1,0,0;1.5708rad)
  Support = -> [Extrude049]
  sketch-geometry (8):
    g0: Circle CenterX=80.351 CenterY=-67.6202 CenterZ=0 NormalX=0 NormalY=0 NormalZ=1 AngleXU=0 Radius=3
    g1: Circle CenterX=80.351 CenterY=-4.92017 CenterZ=0 NormalX=0 NormalY=0 NormalZ=1 AngleXU=0 Radius=3
    g2: Circle CenterX=23.851 CenterY=-4.92017 CenterZ=0 NormalX=0 NormalY=0 NormalZ=1 AngleXU=0 Radius=3
    g3: Circle CenterX=23.851 CenterY=-67.6202 CenterZ=0 NormalX=0 NormalY=0 NormalZ=1 AngleXU=0 Radius=3
    g4: Circle CenterX=23.851 CenterY=-67.6202 CenterZ=0 NormalX=0 NormalY=0 NormalZ=1 AngleXU=0 Radius=5
    g5: Circle CenterX=80.351 CenterY=-67.6202 CenterZ=0 NormalX=0 NormalY=0 NormalZ=1 AngleXU=0 Radius=5
    g6: Circle CenterX=23.851 CenterY=-4.92017 CenterZ=0 NormalX=0 NormalY=0 NormalZ=1 AngleXU=0 Radius=5
    g7: Circle CenterX=80.351 CenterY=-4.92017 CenterZ=0 NormalX=0 NormalY=0 NormalZ=1 AngleXU=0 Radius=5
  constraints (8):
    c: Block(g1)
    c: Block(g0)
    c: Block(g3)
    c: Block(g2)
    c: Block(g5)
    c: Block(g4)
    c: Block(g6)
    c: Block(g7)
FEATURE [Sketcher::SketchObject] Sketch061
  FullyConstrained = true
  MapMode = 3
  Placement = pos=(0,0,0) rot=(1,0,0;1.5708rad)
  sketch-geometry (8):
    g0: Circle CenterX=80.351 CenterY=-67.6202 CenterZ=0 NormalX=0 NormalY=0 NormalZ=1 AngleXU=0 Radius=3
    g1: Circle CenterX=80.351 CenterY=-4.92017 CenterZ=0 NormalX=0 NormalY=0 NormalZ=1 AngleXU=0 Radius=3
    g2: Circle CenterX=23.851 CenterY=-4.92017 CenterZ=0 NormalX=0 NormalY=0 NormalZ=1 AngleXU=0 Radius=3
    g3: Circle CenterX=23.851 CenterY=-67.6202 CenterZ=0 NormalX=0 NormalY=0 NormalZ=1 AngleXU=0 Radius=3
    g4: Circle CenterX=23.851 CenterY=-67.6202 CenterZ=0 NormalX=0 NormalY=0 NormalZ=1 AngleXU=0 Radius=5
    g5: Circle CenterX=80.351 CenterY=-67.6202 CenterZ=0 NormalX=0 NormalY=0 NormalZ=1 AngleXU=0 Radius=5
    g6: Circle CenterX=23.851 CenterY=-4.92017 CenterZ=0 NormalX=0 NormalY=0 NormalZ=1 AngleXU=0 Radius=5
    g7: Circle CenterX=80.351 CenterY=-4.92017 CenterZ=0 NormalX=0 NormalY=0 NormalZ=1 AngleXU=0 Radius=5
  constraints (8):
    c: Block(g1)
    c: Block(g0)
    c: Block(g3)
    c: Block(g2)
    c: Block(g5)
    c: Block(g4)
    c: Block(g6)
    c: Block(g7)
FEATURE [Sketcher::SketchObject] Sketch062  label="topSketch016"
  FullyConstrained = true
  sketch-geometry (20):
    g0: LineSegment StartX=5.21097e-06 StartY=3 StartZ=0 EndX=5.21097e-06 EndY=19 EndZ=0
    g1: ArcOfCircle CenterX=19 CenterY=19 CenterZ=0 NormalX=0 NormalY=0 NormalZ=1 AngleXU=0 Radius=19 StartAngle=1.5708 EndAngle=3.14159
    g2: ArcOfCircle CenterX=19 CenterY=19 CenterZ=0 NormalX=0 NormalY=0 NormalZ=1 AngleXU=0 Radius=16 StartAngle=1.5708 EndAngle=3.14159
    g3: LineSegment StartX=114 StartY=35 StartZ=0 EndX=19 EndY=35 EndZ=0
    g4: LineSegment StartX=5.21097e-06 StartY=3 StartZ=0 EndX=5.21097e-06 EndY=0 EndZ=0
    g5: LineSegment StartX=3 StartY=0 StartZ=0 EndX=5.21097e-06 EndY=0 EndZ=0
    g6: LineSegment StartX=3 StartY=19 StartZ=0 EndX=3 EndY=0 EndZ=0
    g7: LineSegment StartX=19 StartY=38 StartZ=0 EndX=124 EndY=38 EndZ=0
    g8: Circle CenterX=119 CenterY=35 CenterZ=0 NormalX=0 NormalY=0 NormalZ=1 AngleXU=0 Radius=1
    g9: Circle CenterX=121 CenterY=35 CenterZ=0 NormalX=0 NormalY=0 NormalZ=1 AngleXU=0 Radius=1
    g10: Circle CenterX=121 CenterY=33 CenterZ=0 NormalX=0 NormalY=0 NormalZ=1 AngleXU=0 Radius=1
    g11: BSplineCurve PolesCount=3 KnotsCount=2 Degree=2 IsPeriodic=0
    g12: GeomPoint X=119 Y=35 Z=0
    g13: GeomPoint X=121 Y=33 Z=0
    g14: LineSegment StartX=119 StartY=35 StartZ=0 EndX=114 EndY=35 EndZ=0
    g15: ArcOfCircle CenterX=105 CenterY=19 CenterZ=0 NormalX=0 NormalY=0 NormalZ=1 AngleXU=0 Radius=19 StartAngle=5.7297 EndAngle=6.28319
    g16: ArcOfCircle CenterX=105 CenterY=19 CenterZ=0 NormalX=0 NormalY=0 NormalZ=1 AngleXU=0 Radius=16 StartAngle=5.60905 EndAngle=6.28319
    g17: LineSegment StartX=121 StartY=33 StartZ=0 EndX=121 EndY=19 EndZ=0
    g18: LineSegment StartX=124 StartY=38 StartZ=0 EndX=124 EndY=19 EndZ=0
    g19: LineSegment StartX=117.5 StartY=9.01251 StartZ=0 EndX=121.163 EndY=9.0125 EndZ=0
  constraints (46):
    c: Vertical(g0)
    c: Block(g0)
    c: Coincident(g1,g0)
    c: Block(g1)
    c: Coincident(g2,g1)
    c: Block(g2)
    c: Coincident(g3,g2)
    c: Horizontal(g3)
    c: Tangent(g3,g2)
    c: Coincident(g4,g0)
    c: Distance(g4) = 3
    c: Vertical(g4)
    c: Coincident(g5,g4)
    c: Horizontal(g5)
    c: Coincident(g6,g2)
    c: Coincident(g6,g5)
    c: Vertical(g6)
    c: Horizontal(g7)
    c: Distance(g7) = 105
    c: Coincident(g7,g1)
    c: Block(g3)
    c: Weight(g8) = 1
    c: Equal(g8,g9)
    c: Equal(g8,g10)
    c: InternalAlignment(g8,g11)
    c: InternalAlignment(g9,g11)
    c: InternalAlignment(g10,g11)
    c: InternalAlignment(g12,g11)
    c: InternalAlignment(g13,g11)
    c: Block(g11)
    c: Coincident(g14,g11)
    c: Coincident(g14,g3)
    c: Horizontal(g14)
    c: Block(g15)
    c: Coincident(g16,g15)
    c: Block(g16)
    c: Coincident(g17,g11)
    c: Coincident(g17,g16)
    c: Vertical(g17)
    c: Distance(g17) = 14
    c: Coincident(g18,g7)
    c: Coincident(g18,g15)
    c: Vertical(g18)
    c: Distance(g18) = 19
    c: Coincident(g19,g16)
    c: Coincident(g19,g15)
FEATURE [Part::Extrusion] Extrude053  label="top024"
  Base = -> Sketch062
  Dir = (0,0,1)
  DirMode = 2
  FaceMakerClass = Part::FaceMakerBullseye
  LengthFwd = 72
  LengthRev = 0
  Solid = true
  Symmetric = false
FEATURE [Sketcher::SketchObject] Sketch063
  FullyConstrained = true
  MapMode = 3
  Placement = pos=(0,0,0) rot=(1,0,0;1.5708rad)
  Support = -> [Extrude053]
  sketch-geometry (8):
    g0: Circle CenterX=80.351 CenterY=-67.6202 CenterZ=0 NormalX=0 NormalY=0 NormalZ=1 AngleXU=0 Radius=2
    g1: Circle CenterX=80.351 CenterY=-67.6202 CenterZ=0 NormalX=0 NormalY=0 NormalZ=1 AngleXU=0 Radius=3
    g2: Circle CenterX=80.351 CenterY=-4.92017 CenterZ=0 NormalX=0 NormalY=0 NormalZ=1 AngleXU=0 Radius=2
    g3: Circle CenterX=80.351 CenterY=-4.92017 CenterZ=0 NormalX=0 NormalY=0 NormalZ=1 AngleXU=0 Radius=3
    g4: Circle CenterX=23.851 CenterY=-4.92017 CenterZ=0 NormalX=0 NormalY=0 NormalZ=1 AngleXU=0 Radius=2
    g5: Circle CenterX=23.851 CenterY=-4.92017 CenterZ=0 NormalX=0 NormalY=0 NormalZ=1 AngleXU=0 Radius=3
    g6: Circle CenterX=23.851 CenterY=-67.6202 CenterZ=0 NormalX=0 NormalY=0 NormalZ=1 AngleXU=0 Radius=2
    g7: Circle CenterX=23.851 CenterY=-67.6202 CenterZ=0 NormalX=0 NormalY=0 NormalZ=1 AngleXU=0 Radius=3
  constraints (8):
    c: Block(g3)
    c: Block(g2)
    c: Block(g1)
    c: Block(g0)
    c: Block(g6)
    c: Block(g7)
    c: Block(g4)
    c: Block(g5)
FEATURE [Part::Extrusion] Extrude054
  Base = -> Sketch063
  Dir = (0,-1,2e-16)
  DirMode = 2
  FaceMakerClass = Part::FaceMakerBullseye
  LengthFwd = 6
  LengthRev = 0
  Placement = pos=(0,9,0) rot=(0,0,1;0rad)
  Solid = true
  Symmetric = false
FEATURE [Sketcher::SketchObject] Sketch064  label="topSketch017"
  FullyConstrained = true
  sketch-geometry (20):
    g0: LineSegment StartX=5.21097e-06 StartY=3 StartZ=0 EndX=5.21097e-06 EndY=19 EndZ=0
    g1: ArcOfCircle CenterX=19 CenterY=19 CenterZ=0 NormalX=0 NormalY=0 NormalZ=1 AngleXU=0 Radius=19 StartAngle=1.5708 EndAngle=3.14159
    g2: ArcOfCircle CenterX=19 CenterY=19 CenterZ=0 NormalX=0 NormalY=0 NormalZ=1 AngleXU=0 Radius=16 StartAngle=1.5708 EndAngle=3.14159
    g3: LineSegment StartX=114 StartY=35 StartZ=0 EndX=19 EndY=35 EndZ=0
    g4: LineSegment StartX=5.21097e-06 StartY=3 StartZ=0 EndX=5.21097e-06 EndY=0 EndZ=0
    g5: LineSegment StartX=3 StartY=0 StartZ=0 EndX=5.21097e-06 EndY=0 EndZ=0
    g6: LineSegment StartX=3 StartY=19 StartZ=0 EndX=3 EndY=0 EndZ=0
    g7: LineSegment StartX=19 StartY=38 StartZ=0 EndX=124 EndY=38 EndZ=0
    g8: Circle CenterX=119 CenterY=35 CenterZ=0 NormalX=0 NormalY=0 NormalZ=1 AngleXU=0 Radius=1
    g9: Circle CenterX=121 CenterY=35 CenterZ=0 NormalX=0 NormalY=0 NormalZ=1 AngleXU=0 Radius=1
    g10: Circle CenterX=121 CenterY=33 CenterZ=0 NormalX=0 NormalY=0 NormalZ=1 AngleXU=0 Radius=1
    g11: BSplineCurve PolesCount=3 KnotsCount=2 Degree=2 IsPeriodic=0
    g12: GeomPoint X=119 Y=35 Z=0
    g13: GeomPoint X=121 Y=33 Z=0
    g14: LineSegment StartX=119 StartY=35 StartZ=0 EndX=114 EndY=35 EndZ=0
    g15: ArcOfCircle CenterX=105 CenterY=19 CenterZ=0 NormalX=0 NormalY=0 NormalZ=1 AngleXU=0 Radius=19 StartAngle=5.7297 EndAngle=6.28319
    g16: ArcOfCircle CenterX=105 CenterY=19 CenterZ=0 NormalX=0 NormalY=0 NormalZ=1 AngleXU=0 Radius=16 StartAngle=5.60905 EndAngle=6.28319
    g17: LineSegment StartX=121 StartY=33 StartZ=0 EndX=121 EndY=19 EndZ=0
    g18: LineSegment StartX=124 StartY=38 StartZ=0 EndX=124 EndY=19 EndZ=0
    g19: LineSegment StartX=117.5 StartY=9.01251 StartZ=0 EndX=121.163 EndY=9.0125 EndZ=0
  constraints (46):
    c: Vertical(g0)
    c: Block(g0)
    c: Coincident(g1,g0)
    c: Block(g1)
    c: Coincident(g2,g1)
    c: Block(g2)
    c: Coincident(g3,g2)
    c: Horizontal(g3)
    c: Tangent(g3,g2)
    c: Coincident(g4,g0)
    c: Distance(g4) = 3
    c: Vertical(g4)
    c: Coincident(g5,g4)
    c: Horizontal(g5)
    c: Coincident(g6,g2)
    c: Coincident(g6,g5)
    c: Vertical(g6)
    c: Horizontal(g7)
    c: Distance(g7) = 105
    c: Coincident(g7,g1)
    c: Block(g3)
    c: Weight(g8) = 1
    c: Equal(g8,g9)
    c: Equal(g8,g10)
    c: InternalAlignment(g8,g11)
    c: InternalAlignment(g9,g11)
    c: InternalAlignment(g10,g11)
    c: InternalAlignment(g12,g11)
    c: InternalAlignment(g13,g11)
    c: Block(g11)
    c: Coincident(g14,g11)
    c: Coincident(g14,g3)
    c: Horizontal(g14)
    c: Block(g15)
    c: Coincident(g16,g15)
    c: Block(g16)
    c: Coincident(g17,g11)
    c: Coincident(g17,g16)
    c: Vertical(g17)
    c: Distance(g17) = 14
    c: Coincident(g18,g7)
    c: Coincident(g18,g15)
    c: Vertical(g18)
    c: Distance(g18) = 19
    c: Coincident(g19,g16)
    c: Coincident(g19,g15)
FEATURE [Sketcher::SketchObject] Sketch065
  FullyConstrained = true
  MapMode = 3
  Placement = pos=(0,0,0) rot=(1,0,0;1.5708rad)
  sketch-geometry (8):
    g0: Circle CenterX=80.351 CenterY=-67.6202 CenterZ=0 NormalX=0 NormalY=0 NormalZ=1 AngleXU=0 Radius=3
    g1: Circle CenterX=80.351 CenterY=-4.92017 CenterZ=0 NormalX=0 NormalY=0 NormalZ=1 AngleXU=0 Radius=3
    g2: Circle CenterX=23.851 CenterY=-4.92017 CenterZ=0 NormalX=0 NormalY=0 NormalZ=1 AngleXU=0 Radius=3
    g3: Circle CenterX=23.851 CenterY=-67.6202 CenterZ=0 NormalX=0 NormalY=0 NormalZ=1 AngleXU=0 Radius=3
    g4: Circle CenterX=23.851 CenterY=-67.6202 CenterZ=0 NormalX=0 NormalY=0 NormalZ=1 AngleXU=0 Radius=5
    g5: Circle CenterX=80.351 CenterY=-67.6202 CenterZ=0 NormalX=0 NormalY=0 NormalZ=1 AngleXU=0 Radius=5
    g6: Circle CenterX=23.851 CenterY=-4.92017 CenterZ=0 NormalX=0 NormalY=0 NormalZ=1 AngleXU=0 Radius=5
    g7: Circle CenterX=80.351 CenterY=-4.92017 CenterZ=0 NormalX=0 NormalY=0 NormalZ=1 AngleXU=0 Radius=5
  constraints (8):
    c: Block(g1)
    c: Block(g0)
    c: Block(g3)
    c: Block(g2)
    c: Block(g5)
    c: Block(g4)
    c: Block(g6)
    c: Block(g7)
FEATURE [Part::Extrusion] Extrude056
  Base = -> Sketch065
  Dir = (0,-1,2e-16)
  DirMode = 2
  FaceMakerClass = Part::FaceMakerBullseye
  LengthFwd = 2
  LengthRev = 0
  Solid = true
  Symmetric = false
FEATURE [Part::Extrusion] Extrude057  label="top025"
  Base = -> Sketch064
  Dir = (0,0,1)
  DirMode = 2
  FaceMakerClass = Part::FaceMakerBullseye
  LengthFwd = 72
  LengthRev = 0
  Solid = true
  Symmetric = false
FEATURE [Sketcher::SketchObject] Sketch066
  FullyConstrained = true
  MapMode = 3
  Placement = pos=(0,0,0) rot=(1,0,0;1.5708rad)
  Support = -> [Extrude057]
  sketch-geometry (8):
    g0: Circle CenterX=80.351 CenterY=-67.6202 CenterZ=0 NormalX=0 NormalY=0 NormalZ=1 AngleXU=0 Radius=3
    g1: Circle CenterX=80.351 CenterY=-4.92017 CenterZ=0 NormalX=0 NormalY=0 NormalZ=1 AngleXU=0 Radius=3
    g2: Circle CenterX=23.851 CenterY=-4.92017 CenterZ=0 NormalX=0 NormalY=0 NormalZ=1 AngleXU=0 Radius=3
    g3: Circle CenterX=23.851 CenterY=-67.6202 CenterZ=0 NormalX=0 NormalY=0 NormalZ=1 AngleXU=0 Radius=3
    g4: Circle CenterX=23.851 CenterY=-67.6202 CenterZ=0 NormalX=0 NormalY=0 NormalZ=1 AngleXU=0 Radius=5
    g5: Circle CenterX=80.351 CenterY=-67.6202 CenterZ=0 NormalX=0 NormalY=0 NormalZ=1 AngleXU=0 Radius=5
    g6: Circle CenterX=23.851 CenterY=-4.92017 CenterZ=0 NormalX=0 NormalY=0 NormalZ=1 AngleXU=0 Radius=5
    g7: Circle CenterX=80.351 CenterY=-4.92017 CenterZ=0 NormalX=0 NormalY=0 NormalZ=1 AngleXU=0 Radius=5
  constraints (8):
    c: Block(g1)
    c: Block(g0)
    c: Block(g3)
    c: Block(g2)
    c: Block(g5)
    c: Block(g4)
    c: Block(g6)
    c: Block(g7)
FEATURE [Part::Extrusion] Extrude055
  Base = -> Sketch066
  Dir = (0,-1,2e-16)
  DirMode = 2
  FaceMakerClass = Part::FaceMakerBullseye
  LengthFwd = 2
  LengthRev = 0
  Solid = true
  Symmetric = false
FEATURE [Part::Fillet] Fillet041
  Base = -> Extrude056
  Edges = 4 edges r=1.99: [Edge6,Edge12,Edge18,Edge24]
FEATURE [Part::Cut] Cut045
  Base = -> Extrude055
  Placement = pos=(0,6,0) rot=(0,0,1;0rad)
  Tool = -> Fillet041
FEATURE [Part::MultiFuse] Fusion095  label="pcbScrewPillars"
  Placement = pos=(-3.2,-1,72.3) rot=(0,0,1;0rad)
  Shapes = -> [Cut045,Extrude054]
FEATURE [Part::Feature] Face113
  shape: bbox 3.2 x 1.5 x 2e-07 mm, 1 faces, 0 solids (baked)
FEATURE [Part::Revolution] Revolve121  label="backCaseScrewRetainer002"
  Angle = 360
  Axis = (0,1,0)
  Base = (0,0,0)
  FaceMakerClass = Part::FaceMakerBullseye
  Placement = pos=(12.5,3,62) rot=(0,0,1;0rad)
  Solid = false
  Source = -> Face113
  Symmetric = false
FEATURE [Part::Feature] Face114
  shape: bbox 3.2 x 1.5 x 2e-07 mm, 1 faces, 0 solids (baked)
FEATURE [Part::Feature] Face115
  shape: bbox 3.2 x 1.5 x 2e-07 mm, 1 faces, 0 solids (baked)
FEATURE [Part::Feature] Face116
  shape: bbox 3.2 x 1.5 x 2e-07 mm, 1 faces, 0 solids (baked)
FEATURE [Part::Revolution] Revolve122  label="frontCaseScrewRetainer004"
  Angle = 360
  Axis = (0,1,0)
  Base = (0,0,0)
  FaceMakerClass = Part::FaceMakerBullseye
  Placement = pos=(89.5,3,68.5) rot=(0,0,1;0rad)
  Solid = false
  Source = -> Face115
  Symmetric = false
FEATURE [Part::Revolution] Revolve123  label="frontCaseScrewRetainer005"
  Angle = 360
  Axis = (0,1,0)
  Base = (0,0,0)
  FaceMakerClass = Part::FaceMakerBullseye
  Placement = pos=(89.5,3,3.5) rot=(0,0,1;0rad)
  Solid = false
  Source = -> Face116
  Symmetric = false
FEATURE [Part::Revolution] Revolve124  label="backCaseScrewRetainer003"
  Angle = 360
  Axis = (0,1,0)
  Base = (0,0,0)
  FaceMakerClass = Part::FaceMakerBullseye
  Placement = pos=(12.5,3,10) rot=(0,0,1;0rad)
  Solid = false
  Source = -> Face114
  Symmetric = false
FEATURE [Part::Feature] Face117
  shape: bbox 3.6 x 3.2 x 2e-07 mm, 1 faces, 0 solids (baked)
FEATURE [Part::Revolution] Revolve125  label="moreFrontCaseScrewRetainer004"
  Angle = 360
  Axis = (0,1,0)
  Base = (0,0,0)
  FaceMakerClass = Part::FaceMakerBullseye
  Placement = pos=(109.5,4.5,68.5) rot=(0,0,1;0rad)
  Solid = false
  Source = -> Face117
  Symmetric = false
FEATURE [Part::Feature] Face118
  shape: bbox 3.6 x 3.2 x 2e-07 mm, 1 faces, 0 solids (baked)
FEATURE [Part::Revolution] Revolve126  label="moreFrontCaseScrewRetainer005"
  Angle = 360
  Axis = (0,1,0)
  Base = (0,0,0)
  FaceMakerClass = Part::FaceMakerBullseye
  Placement = pos=(109.5,4.5,3.5) rot=(0,0,1;0rad)
  Solid = false
  Source = -> Face118
  Symmetric = false
FEATURE [Part::MultiFuse] Fusion096  label="screwRetainers001"
  Shapes = -> [Revolve126,Revolve125,Revolve124,Revolve123,Revolve122,Revolve121]
FEATURE [Part::Feature] Face119
  shape: bbox 10 x 16.5 x 2e-07 mm, 1 faces, 0 solids (baked)
FEATURE [Part::Revolution] Revolve130  label="plugHousing050"
  Angle = 360
  Axis = (0,1,0)
  Base = (0,0,0)
  FaceMakerClass = Part::FaceMakerBullseye
  Placement = pos=(0,0,36.15) rot=(0,0,1;0rad)
  Solid = false
  Source = -> Face119
  Symmetric = false
FEATURE [Part::Feature] Face120
  shape: bbox 10 x 16.5 x 2e-07 mm, 1 faces, 0 solids (baked)
FEATURE [Part::Feature] Face121
  shape: bbox 10 x 16.5 x 2e-07 mm, 1 faces, 0 solids (baked)
FEATURE [Part::Revolution] Revolve127  label="plugHousing047"
  Angle = 360
  Axis = (0,1,0)
  Base = (0,0,0)
  FaceMakerClass = Part::FaceMakerBullseye
  Placement = pos=(0,0,36.15) rot=(0,0,1;0rad)
  Solid = false
  Source = -> Face121
  Symmetric = false
FEATURE [Part::Feature] Face122
  shape: bbox 10 x 16.5 x 2e-07 mm, 1 faces, 0 solids (baked)
FEATURE [Part::Feature] Face123
  shape: bbox 10 x 16.5 x 2e-07 mm, 1 faces, 0 solids (baked)
FEATURE [Part::Revolution] Revolve128  label="plugHousing048"
  Angle = 360
  Axis = (0,1,0)
  Base = (0,0,0)
  FaceMakerClass = Part::FaceMakerBullseye
  Placement = pos=(0,0,36.15) rot=(0,0,1;0rad)
  Solid = false
  Source = -> Face123
  Symmetric = false
FEATURE [Part::MultiFuse] Fusion100  label="plugHousing054"
  Placement = pos=(0,0,0) rot=(0,0,1;1.5708rad)
  Shapes = -> [Revolve130,Revolve128]
FEATURE [Part::Feature] Face124
  shape: bbox 10 x 16.5 x 2e-07 mm, 1 faces, 0 solids (baked)
FEATURE [Part::Feature] Face125
  shape: bbox 10 x 16.5 x 2e-07 mm, 1 faces, 0 solids (baked)
FEATURE [Part::Revolution] Revolve129  label="plugHousing049"
  Angle = 360
  Axis = (0,1,0)
  Base = (0,0,0)
  FaceMakerClass = Part::FaceMakerBullseye
  Placement = pos=(0,0,36.15) rot=(0,0,1;0rad)
  Solid = false
  Source = -> Face125
  Symmetric = false
FEATURE [Part::Feature] Face126
  shape: bbox 10 x 16.5 x 2e-07 mm, 1 faces, 0 solids (baked)
FEATURE [Part::Revolution] Revolve131  label="plugHousing058"
  Angle = 360
  Axis = (0,1,0)
  Base = (0,0,0)
  FaceMakerClass = Part::FaceMakerBullseye
  Placement = pos=(0,0,36.15) rot=(0,0,1;0rad)
  Solid = false
  Source = -> Face120
  Symmetric = false
FEATURE [Part::MultiFuse] Fusion099  label="plugHousing053"
  Placement = pos=(0,0,0) rot=(0,0,1;1.5708rad)
  Shapes = -> [Revolve127,Revolve131]
FEATURE [Part::MultiFuse] Fusion102  label="plugHousing056"
  Placement = pos=(0,19,0) rot=(0,0,1;3.14159rad)
  Shapes = -> [Fusion100,Fusion099]
FEATURE [Part::Revolution] Revolve132  label="plugHousing059"
  Angle = 360
  Axis = (0,1,0)
  Base = (0,0,0)
  FaceMakerClass = Part::FaceMakerBullseye
  Placement = pos=(0,0,36.15) rot=(0,0,1;0rad)
  Solid = false
  Source = -> Face126
  Symmetric = false
FEATURE [Part::Revolution] Revolve133  label="plugHousing060"
  Angle = 360
  Axis = (0,1,0)
  Base = (0,0,0)
  FaceMakerClass = Part::FaceMakerBullseye
  Placement = pos=(0,0,36.15) rot=(0,0,1;0rad)
  Solid = false
  Source = -> Face122
  Symmetric = false
FEATURE [Part::MultiFuse] Fusion097  label="plugHousing051"
  Placement = pos=(0,0,0) rot=(0,0,1;1.5708rad)
  Shapes = -> [Revolve133,Revolve132]
FEATURE [Part::Revolution] Revolve134  label="plugHousing061"
  Angle = 360
  Axis = (0,1,0)
  Base = (0,0,0)
  FaceMakerClass = Part::FaceMakerBullseye
  Placement = pos=(0,0,36.15) rot=(0,0,1;0rad)
  Solid = false
  Source = -> Face124
  Symmetric = false
FEATURE [Part::MultiFuse] Fusion101  label="plugHousing055"
  Placement = pos=(0,0,0) rot=(0,0,1;1.5708rad)
  Shapes = -> [Revolve129,Revolve134]
FEATURE [Part::MultiFuse] Fusion098  label="plugHousing052"
  Placement = pos=(0,19,0) rot=(0,0,1;3.14159rad)
  Shapes = -> [Fusion097,Fusion101]
FEATURE [Part::MultiFuse] Fusion103  label="plugHousing057"
  Placement = pos=(122.621,0,-0.15) rot=(0,0,1;0rad)
  Shapes = -> [Fusion102,Fusion098]
FEATURE [Part::Box] Box028  label="Cube015"
  AttacherType = Attacher::AttachEngine3D
  Height = 28
  Length = 3
  Placement = pos=(110.7,19,22) rot=(0,0,1;0rad)
  Width = 15.7
FEATURE [Part::Cylinder] Cylinder044
  Angle = 360
  AttacherType = Attacher::AttachEngine3D
  Height = 20
  Placement = pos=(0,0,36.15) rot=(0,0,1;0rad)
  Radius = 10.3
FEATURE [Part::Cylinder] Cylinder045
  Angle = 360
  AttacherType = Attacher::AttachEngine3D
  Height = 10
  Placement = pos=(0,0,36.15) rot=(0,0,1;0rad)
  Radius = 4
FEATURE [Part::MultiFuse] Fusion104  label="removeToCreteHoleForPlugHousing040"
  Placement = pos=(70,19,36) rot=(0,1,0;1.5708rad)
  Shapes = -> [Cylinder044,Cylinder045]
FEATURE [Part::Cut] Cut046  label="plugHousingTab003"
  Base = -> Box028
  Tool = -> Fusion104
FEATURE [Part::MultiFuse] Fusion105  label="plugHousing062"
  Shapes = -> [Fusion103,Cut046]
FEATURE [Part::Fillet] Fillet042
  Base = -> Fusion105
  Edges = 1 edges r=2: [Edge25]
FEATURE [Part::Fillet] Fillet043  label="plugHousing063"
  Base = -> Fillet042
  Edges = 1 edges r=2: [Edge8]
  Placement = pos=(7,0,0) rot=(0,0,1;0rad)
FEATURE [Part::Feature] Face127
  shape: bbox 10 x 16.5 x 2e-07 mm, 1 faces, 0 solids (baked)
FEATURE [Part::Feature] Face128
  shape: bbox 10 x 16.5 x 2e-07 mm, 1 faces, 0 solids (baked)
FEATURE [Part::Revolution] Revolve137  label="plugHousing070"
  Angle = 360
  Axis = (0,1,0)
  Base = (0,0,0)
  FaceMakerClass = Part::FaceMakerBullseye
  Placement = pos=(0,0,36.15) rot=(0,0,1;0rad)
  Solid = false
  Source = -> Face127
  Symmetric = false
FEATURE [Part::Revolution] Revolve140  label="plugHousing073"
  Angle = 360
  Axis = (0,1,0)
  Base = (0,0,0)
  FaceMakerClass = Part::FaceMakerBullseye
  Placement = pos=(0,0,36.15) rot=(0,0,1;0rad)
  Solid = false
  Source = -> Face128
  Symmetric = false
FEATURE [Part::Feature] Face129
  shape: bbox 10 x 16.5 x 2e-07 mm, 1 faces, 0 solids (baked)
FEATURE [Part::Revolution] Revolve138  label="plugHousing071"
  Angle = 360
  Axis = (0,1,0)
  Base = (0,0,0)
  FaceMakerClass = Part::FaceMakerBullseye
  Placement = pos=(0,0,36.15) rot=(0,0,1;0rad)
  Solid = false
  Source = -> Face129
  Symmetric = false
FEATURE [Part::Feature] Face130
  shape: bbox 10 x 16.5 x 2e-07 mm, 1 faces, 0 solids (baked)
FEATURE [Part::Revolution] Revolve139  label="plugHousing072"
  Angle = 360
  Axis = (0,1,0)
  Base = (0,0,0)
  FaceMakerClass = Part::FaceMakerBullseye
  Placement = pos=(0,0,36.15) rot=(0,0,1;0rad)
  Solid = false
  Source = -> Face130
  Symmetric = false
FEATURE [Part::Feature] Face131
  shape: bbox 10 x 16.5 x 2e-07 mm, 1 faces, 0 solids (baked)
FEATURE [Part::Revolution] Revolve135  label="plugHousing068"
  Angle = 360
  Axis = (0,1,0)
  Base = (0,0,0)
  FaceMakerClass = Part::FaceMakerBullseye
  Placement = pos=(0,0,36.15) rot=(0,0,1;0rad)
  Solid = false
  Source = -> Face131
  Symmetric = false
FEATURE [Part::MultiFuse] Fusion112  label="plugHousing078"
  Placement = pos=(0,0,0) rot=(0,0,1;1.5708rad)
  Shapes = -> [Revolve135,Revolve139]
FEATURE [Part::Feature] Face132
  shape: bbox 10 x 16.5 x 2e-07 mm, 1 faces, 0 solids (baked)
FEATURE [Part::Revolution] Revolve141  label="plugHousing074"
  Angle = 360
  Axis = (0,1,0)
  Base = (0,0,0)
  FaceMakerClass = Part::FaceMakerBullseye
  Placement = pos=(0,0,36.15) rot=(0,0,1;0rad)
  Solid = false
  Source = -> Face132
  Symmetric = false
FEATURE [Part::MultiFuse] Fusion110  label="plugHousing076"
  Placement = pos=(0,0,0) rot=(0,0,1;1.5708rad)
  Shapes = -> [Revolve141,Revolve140]
FEATURE [Part::Feature] Face133
  shape: bbox 10 x 16.5 x 2e-07 mm, 1 faces, 0 solids (baked)
FEATURE [Part::Revolution] Revolve136  label="plugHousing069"
  Angle = 360
  Axis = (0,1,0)
  Base = (0,0,0)
  FaceMakerClass = Part::FaceMakerBullseye
  Placement = pos=(0,0,36.15) rot=(0,0,1;0rad)
  Solid = false
  Source = -> Face133
  Symmetric = false
FEATURE [Part::MultiFuse] Fusion106  label="plugHousing064"
  Placement = pos=(0,0,0) rot=(0,0,1;1.5708rad)
  Shapes = -> [Revolve138,Revolve136]
FEATURE [Part::MultiFuse] Fusion108  label="plugHousing066"
  Placement = pos=(0,19,0) rot=(0,0,1;3.14159rad)
  Shapes = -> [Fusion106,Fusion112]
FEATURE [Part::Feature] Face134
  shape: bbox 10 x 16.5 x 2e-07 mm, 1 faces, 0 solids (baked)
FEATURE [Part::Revolution] Revolve142  label="plugHousing075"
  Angle = 360
  Axis = (0,1,0)
  Base = (0,0,0)
  FaceMakerClass = Part::FaceMakerBullseye
  Placement = pos=(0,0,36.15) rot=(0,0,1;0rad)
  Solid = false
  Source = -> Face134
  Symmetric = false
FEATURE [Part::MultiFuse] Fusion107  label="plugHousing065"
  Placement = pos=(0,0,0) rot=(0,0,1;1.5708rad)
  Shapes = -> [Revolve137,Revolve142]
FEATURE [Part::MultiFuse] Fusion111  label="plugHousing077"
  Placement = pos=(0,19,0) rot=(0,0,1;3.14159rad)
  Shapes = -> [Fusion110,Fusion107]
FEATURE [Part::MultiFuse] Fusion109  label="plugHousing067"
  Placement = pos=(131.236,0,-0.15) rot=(0,0,1;0rad)
  Shapes = -> [Fusion108,Fusion111]
FEATURE [Part::MultiFuse] Fusion113  label="plugHousing079"
  Shapes = -> [Fillet043,Fusion109]
FEATURE [Part::Feature] Face135
  shape: bbox 3.5 x 17.8 x 2e-07 mm, 1 faces, 0 solids (baked)
FEATURE [Part::Revolution] Revolve143  label="removeToCreateScrewAndThreadedInsertHole049"
  Angle = 360
  Axis = (0,1,0)
  Base = (0,0,0)
  FaceMakerClass = Part::FaceMakerBullseye
  Placement = pos=(12.5,0,10) rot=(0,0,1;0rad)
  Solid = false
  Source = -> Face135
  Symmetric = false
FEATURE [Part::Feature] Face136
  shape: bbox 3.5 x 17.8 x 2e-07 mm, 1 faces, 0 solids (baked)
FEATURE [Part::Revolution] Revolve144  label="removeToCreateScrewAndThreadedInsertHole050"
  Angle = 360
  Axis = (0,1,0)
  Base = (0,0,0)
  FaceMakerClass = Part::FaceMakerBullseye
  Placement = pos=(12.5,0,62) rot=(0,0,1;0rad)
  Solid = false
  Source = -> Face136
  Symmetric = false
FEATURE [Part::Feature] Face137
  shape: bbox 3.5 x 17.8 x 2e-07 mm, 1 faces, 0 solids (baked)
FEATURE [Part::Revolution] Revolve145  label="removeToCreateScrewAndThreadedInsertHole051"
  Angle = 360
  Axis = (0,1,0)
  Base = (0,0,0)
  FaceMakerClass = Part::FaceMakerBullseye
  Placement = pos=(89.5,0,68.5) rot=(0,0,1;0rad)
  Solid = false
  Source = -> Face137
  Symmetric = false
FEATURE [Part::Feature] Face138
  shape: bbox 3.5 x 17.8 x 2e-07 mm, 1 faces, 0 solids (baked)
FEATURE [Part::Revolution] Revolve146  label="removeToCreateScrewAndThreadedInsertHole052"
  Angle = 360
  Axis = (0,1,0)
  Base = (0,0,0)
  FaceMakerClass = Part::FaceMakerBullseye
  Placement = pos=(89.5,0,3.5) rot=(0,0,1;0rad)
  Solid = false
  Source = -> Face138
  Symmetric = false
FEATURE [Part::Feature] Face139
  shape: bbox 3.5 x 17.8 x 2e-07 mm, 1 faces, 0 solids (baked)
FEATURE [Part::Revolution] Revolve147  label="removeToCreateScrewAndThreadedInsertHole053"
  Angle = 360
  Axis = (0,1,0)
  Base = (0,0,0)
  FaceMakerClass = Part::FaceMakerBullseye
  Placement = pos=(109.5,4.7,3.5) rot=(0,0,1;0rad)
  Solid = false
  Source = -> Face139
  Symmetric = false
FEATURE [Part::Feature] Face140
  shape: bbox 3.5 x 17.8 x 2e-07 mm, 1 faces, 0 solids (baked)
FEATURE [Part::Revolution] Revolve148  label="removeToCreateScrewAndThreadedInsertHole054"
  Angle = 360
  Axis = (0,1,0)
  Base = (0,0,0)
  FaceMakerClass = Part::FaceMakerBullseye
  Placement = pos=(109.5,4.7,68.5) rot=(0,0,1;0rad)
  Solid = false
  Source = -> Face140
  Symmetric = false
FEATURE [Part::MultiFuse] Fusion114  label="removeToCreateScrewAndThreadedInsertHole055"
  Shapes = -> [Revolve148,Revolve147,Revolve146,Revolve145,Revolve144,Revolve143]
FEATURE [Part::Cut] Cut047  label="casePillars004"
  Base = -> Cut037
  Tool = -> Fusion114
FEATURE [Part::Feature] Face141
  shape: bbox 3.5 x 17.8 x 2e-07 mm, 1 faces, 0 solids (baked)
FEATURE [Part::Feature] Face142
  shape: bbox 3.5 x 17.8 x 2e-07 mm, 1 faces, 0 solids (baked)
FEATURE [Part::Feature] Face143
  shape: bbox 3.5 x 17.8 x 2e-07 mm, 1 faces, 0 solids (baked)
FEATURE [Part::Revolution] Revolve149  label="removeToCreateScrewAndThreadedInsertHole057"
  Angle = 360
  Axis = (0,1,0)
  Base = (0,0,0)
  FaceMakerClass = Part::FaceMakerBullseye
  Placement = pos=(12.5,0,10) rot=(0,0,1;0rad)
  Solid = false
  Source = -> Face141
  Symmetric = false
FEATURE [Part::Feature] Face144
  shape: bbox 3.5 x 17.8 x 2e-07 mm, 1 faces, 0 solids (baked)
FEATURE [Part::Feature] Face145
  shape: bbox 3.5 x 17.8 x 2e-07 mm, 1 faces, 0 solids (baked)
FEATURE [Part::Feature] Face146
  shape: bbox 3.5 x 17.8 x 2e-07 mm, 1 faces, 0 solids (baked)
FEATURE [Part::Revolution] Revolve150  label="removeToCreateScrewAndThreadedInsertHole058"
  Angle = 360
  Axis = (0,1,0)
  Base = (0,0,0)
  FaceMakerClass = Part::FaceMakerBullseye
  Placement = pos=(12.5,0,62) rot=(0,0,1;0rad)
  Solid = false
  Source = -> Face146
  Symmetric = false
FEATURE [Part::Revolution] Revolve151  label="removeToCreateScrewAndThreadedInsertHole059"
  Angle = 360
  Axis = (0,1,0)
  Base = (0,0,0)
  FaceMakerClass = Part::FaceMakerBullseye
  Placement = pos=(89.5,0,68.5) rot=(0,0,1;0rad)
  Solid = false
  Source = -> Face143
  Symmetric = false
FEATURE [Part::Revolution] Revolve152  label="removeToCreateScrewAndThreadedInsertHole060"
  Angle = 360
  Axis = (0,1,0)
  Base = (0,0,0)
  FaceMakerClass = Part::FaceMakerBullseye
  Placement = pos=(89.5,0,3.5) rot=(0,0,1;0rad)
  Solid = false
  Source = -> Face142
  Symmetric = false
FEATURE [Part::Revolution] Revolve153  label="removeToCreateScrewAndThreadedInsertHole061"
  Angle = 360
  Axis = (0,1,0)
  Base = (0,0,0)
  FaceMakerClass = Part::FaceMakerBullseye
  Placement = pos=(109.5,4.7,3.5) rot=(0,0,1;0rad)
  Solid = false
  Source = -> Face145
  Symmetric = false
FEATURE [Part::Revolution] Revolve154  label="removeToCreateScrewAndThreadedInsertHole062"
  Angle = 360
  Axis = (0,1,0)
  Base = (0,0,0)
  FaceMakerClass = Part::FaceMakerBullseye
  Placement = pos=(109.5,4.7,68.5) rot=(0,0,1;0rad)
  Solid = false
  Source = -> Face144
  Symmetric = false
FEATURE [Part::MultiFuse] Fusion115  label="removeToCreateScrewAndThreadedInsertHole056"
  Shapes = -> [Revolve154,Revolve153,Revolve152,Revolve151,Revolve150,Revolve149]
FEATURE [Part::Feature] Face147
  shape: bbox 9.8 x 26.5 x 2e-07 mm, 1 faces, 0 solids (baked)
FEATURE [Part::Revolution] Revolve155
  Angle = 360
  Axis = (0,1,0)
  Base = (0,0,0)
  FaceMakerClass = Part::FaceMakerBullseye
  Placement = pos=(0,0,0) rot=(0,0,1;1.5708rad)
  Solid = false
  Source = -> Face147
  Symmetric = false
FEATURE [Part::Feature] Face148
  shape: bbox 9.8 x 26.5 x 2e-07 mm, 1 faces, 0 solids (baked)
FEATURE [Part::Revolution] Revolve156
  Angle = 360
  Axis = (0,1,0)
  Base = (0,0,0)
  FaceMakerClass = Part::FaceMakerBullseye
  Placement = pos=(0,0,0) rot=(0,0,1;1.5708rad)
  Solid = false
  Source = -> Face148
  Symmetric = false
FEATURE [Part::MultiFuse] Fusion116
  Placement = pos=(-18,19,36) rot=(0,0,1;0rad)
  Shapes = -> [Revolve156,Revolve155]
FEATURE [Part::Box] Box029  label="Cube016"
  AttacherType = Attacher::AttachEngine3D
  Height = 28
  Length = 3
  Placement = pos=(110.7,19,22) rot=(0,0,1;0rad)
  Width = 15.7
FEATURE [Part::Cylinder] Cylinder046
  Angle = 360
  AttacherType = Attacher::AttachEngine3D
  Height = 10
  Placement = pos=(0,0,36.15) rot=(0,0,1;0rad)
  Radius = 4
FEATURE [Part::Cylinder] Cylinder047
  Angle = 360
  AttacherType = Attacher::AttachEngine3D
  Height = 20
  Placement = pos=(0,0,36.15) rot=(0,0,1;0rad)
  Radius = 10.3
FEATURE [Part::MultiFuse] Fusion117  label="removeToCreteHoleForPlugHousing041"
  Placement = pos=(70,19,36) rot=(0,1,0;1.5708rad)
  Shapes = -> [Cylinder047,Cylinder046]
FEATURE [Part::Cut] Cut049  label="plugHousingTab004"
  Base = -> Box029
  Placement = pos=(-107.4,-14,0) rot=(0,0,1;0rad)
  Tool = -> Fusion117
FEATURE [Part::Box] Box030  label="Cube017"
  AttacherType = Attacher::AttachEngine3D
  Height = 28
  Length = 3
  Placement = pos=(110.7,19,22) rot=(0,0,1;0rad)
  Width = 15.7
FEATURE [Part::Cylinder] Cylinder048
  Angle = 360
  AttacherType = Attacher::AttachEngine3D
  Height = 10
  Placement = pos=(0,0,36.15) rot=(0,0,1;0rad)
  Radius = 4
FEATURE [Part::Cylinder] Cylinder049
  Angle = 360
  AttacherType = Attacher::AttachEngine3D
  Height = 20
  Placement = pos=(0,0,36.15) rot=(0,0,1;0rad)
  Radius = 10.3
FEATURE [Part::MultiFuse] Fusion118  label="removeToCreteHoleForPlugHousing042"
  Placement = pos=(70,19,36) rot=(0,1,0;1.5708rad)
  Shapes = -> [Cylinder049,Cylinder048]
FEATURE [Part::Cut] Cut050  label="plugHousingTab005"
  Base = -> Box030
  Placement = pos=(-107.4,-14,0) rot=(0,0,1;0rad)
  Tool = -> Fusion118
FEATURE [Part::MultiFuse] Fusion119
  Placement = pos=(9.6,23,0) rot=(0,0,1;3.14159rad)
  Shapes = -> [Cut049,Cut050]
FEATURE [Part::Box] Box031  label="Cube018"
  AttacherType = Attacher::AttachEngine3D
  Height = 10
  Length = 3
  Placement = pos=(3.3,4,12) rot=(0,0,1;0rad)
  Width = 10
FEATURE [Part::Fillet] Fillet044
  Base = -> Box031
  Edges = 1 edges r=2: [Edge11]
FEATURE [Part::Box] Box032  label="Cube019"
  AttacherType = Attacher::AttachEngine3D
  Height = 10
  Length = 3
  Placement = pos=(3.3,4,50) rot=(0,0,1;0rad)
  Width = 10
FEATURE [Part::Fillet] Fillet045
  Base = -> Box032
  Edges = 1 edges r=2: [Edge12]
FEATURE [Part::Box] Box033  label="Cube020"
  AttacherType = Attacher::AttachEngine3D
  Height = 28
  Length = 4
  Placement = pos=(5,0,22) rot=(0,0,1;0rad)
  Width = 10
FEATURE [Part::Fillet] Fillet046
  Base = -> Box033
  Edges = 1 edges r=1: [Edge7]
FEATURE [Part::Fillet] Fillet047
  Base = -> Fillet046
  Edges = 1 edges r=2: [Edge5]
FEATURE [Part::Fillet] Fillet048
  Base = -> Fillet047
  Edges = 1 edges r=2: [Edge2]
FEATURE [Part::Cylinder] Cylinder050
  Angle = 360
  AttacherType = Attacher::AttachEngine3D
  Height = 20
  Placement = pos=(0,0,36.15) rot=(0,0,1;0rad)
  Radius = 8.2
FEATURE [Part::Cylinder] Cylinder051
  Angle = 360
  AttacherType = Attacher::AttachEngine3D
  Height = 10
  Placement = pos=(0,0,36.15) rot=(0,0,1;0rad)
  Radius = 4
FEATURE [Part::MultiFuse] Fusion120  label="removeToCreteHoleForPlugHousing043"
  Placement = pos=(-42,19,36) rot=(0,1,0;1.5708rad)
  Shapes = -> [Cylinder050,Cylinder051]
FEATURE [Sketcher::SketchObject] Sketch067  label="topSketch018"
  FullyConstrained = true
  sketch-geometry (4):
    g0: LineSegment StartX=16.8446 StartY=31.512 StartZ=0 EndX=16.3251 EndY=34.4666 EndZ=0
    g1: ArcOfCircle CenterX=19 CenterY=19.2524 CenterZ=0 NormalX=0 NormalY=0 NormalZ=1 AngleXU=0 Radius=15.4476 StartAngle=1.74483 EndAngle=2.72717
    g2: ArcOfCircle CenterX=19 CenterY=19.2524 CenterZ=0 NormalX=0 NormalY=0 NormalZ=1 AngleXU=0 Radius=12.4476 StartAngle=1.74483 EndAngle=2.73189
    g3: LineSegment StartX=4.86004 StartY=25.4725 StartZ=0 EndX=7.58253 EndY=24.2107 EndZ=0
  constraints (7):
    c: Block(g0)
    c: Coincident(g1,g0)
    c: Coincident(g2,g0)
    c: Coincident(g3,g1)
    c: Coincident(g3,g2)
    c: Block(g1)
    c: Block(g2)
FEATURE [Part::Extrusion] Extrude058
  Base = -> Sketch067
  Dir = (0,0,1)
  DirMode = 2
  FaceMakerClass = Part::FaceMakerBullseye
  LengthFwd = 10
  LengthRev = 0
  Placement = pos=(0,0,31) rot=(0,0,1;0rad)
  Solid = true
  Symmetric = false
FEATURE [Part::Cut] Cut051
  Base = -> Extrude058
  Tool = -> Fusion120
FEATURE [Part::Fillet] Fillet049
  Base = -> Cut051
  Edges = 1 edges r=2: [Edge1]
FEATURE [Part::Fillet] Fillet050
  Base = -> Fillet049
  Edges = 1 edges r=2.5: [Edge1]
FEATURE [Part::Fillet] Fillet051
  Base = -> Fillet050
  Edges = 1 edges r=2.5: [Edge2]
FEATURE [Part::MultiFuse] Fusion121  label="wireHolder003"
  Shapes = -> [Fusion116,Fillet051]
FEATURE [Part::MultiFuse] Fusion122
  Shapes = -> [Fillet045,Fusion121]
FEATURE [Part::MultiFuse] Fusion123  label="wireHolder004"
  Shapes = -> [Fusion122,Fillet048]
FEATURE [Part::MultiFuse] Fusion124  label="wireHolder005"
  Shapes = -> [Fillet044,Fusion119,Fusion123]
FEATURE [Sketcher::SketchObject] Sketch068  label="topSketch019"
  FullyConstrained = true
  sketch-geometry (6):
    g0: LineSegment StartX=19 StartY=38 StartZ=0 EndX=117 EndY=38 EndZ=0
    g1: ArcOfCircle CenterX=19 CenterY=19 CenterZ=0 NormalX=0 NormalY=0 NormalZ=1 AngleXU=0 Radius=19 StartAngle=1.5708 EndAngle=3.14159
    g2: LineSegment StartX=117 StartY=38 StartZ=0 EndX=117 EndY=19 EndZ=0
    g3: LineSegment StartX=98 StartY=1.0161e-12 StartZ=0 EndX=5.22862e-06 EndY=1.0161e-12 EndZ=0
    g4: LineSegment StartX=5.22862e-06 StartY=19 StartZ=0 EndX=5.22862e-06 EndY=1.0161e-12 EndZ=0
    g5: ArcOfCircle CenterX=98 CenterY=19 CenterZ=0 NormalX=0 NormalY=0 NormalZ=1 AngleXU=0 Radius=19 StartAngle=4.71239 EndAngle=6.28319
  constraints (16):
    c: Horizontal(g0)
    c: Distance(g0) = 98
    c: Coincident(g1,g0)
    c: Block(g1)
    c: Coincident(g2,g0)
    c: Vertical(g2)
    c: Distance(g2) = 19
    c: Horizontal(g3)
    c: Coincident(g4,g1)
    c: Vertical(g4)
    c: Coincident(g3,g4)
    c: Block(g3)
    c: Coincident(g5,g2)
    c: Coincident(g5,g3)
    c: Block(g0)
    c: Block(g5)
FEATURE [Part::Extrusion] Extrude059  label="sideA002"
  Base = -> Sketch068
  Dir = (0,0,1)
  DirMode = 2
  FaceMakerClass = Part::FaceMakerBullseye
  LengthFwd = 3
  LengthRev = 0
  Placement = pos=(0,0,-2.7) rot=(0,0,1;0rad)
  Solid = true
  Symmetric = false
FEATURE [Sketcher::SketchObject] Sketch069  label="topSketch020"
  FullyConstrained = true
  sketch-geometry (6):
    g0: LineSegment StartX=19 StartY=38 StartZ=0 EndX=117 EndY=38 EndZ=0
    g1: ArcOfCircle CenterX=19 CenterY=19 CenterZ=0 NormalX=0 NormalY=0 NormalZ=1 AngleXU=0 Radius=19 StartAngle=1.5708 EndAngle=3.14159
    g2: LineSegment StartX=117 StartY=38 StartZ=0 EndX=117 EndY=19 EndZ=0
    g3: LineSegment StartX=98 StartY=1.0161e-12 StartZ=0 EndX=5.22862e-06 EndY=1.0161e-12 EndZ=0
    g4: LineSegment StartX=5.22862e-06 StartY=19 StartZ=0 EndX=5.22862e-06 EndY=1.0161e-12 EndZ=0
    g5: ArcOfCircle CenterX=98 CenterY=19 CenterZ=0 NormalX=0 NormalY=0 NormalZ=1 AngleXU=0 Radius=19 StartAngle=4.71239 EndAngle=6.28319
  constraints (16):
    c: Horizontal(g0)
    c: Distance(g0) = 98
    c: Coincident(g1,g0)
    c: Block(g1)
    c: Coincident(g2,g0)
    c: Vertical(g2)
    c: Distance(g2) = 19
    c: Horizontal(g3)
    c: Coincident(g4,g1)
    c: Vertical(g4)
    c: Coincident(g3,g4)
    c: Block(g3)
    c: Coincident(g5,g2)
    c: Coincident(g5,g3)
    c: Block(g0)
    c: Block(g5)
FEATURE [Part::Extrusion] Extrude060  label="sideB002"
  Base = -> Sketch069
  Dir = (0,0,1)
  DirMode = 2
  FaceMakerClass = Part::FaceMakerBullseye
  LengthFwd = 3
  LengthRev = 0
  Placement = pos=(0,0,71.7) rot=(0,0,1;0rad)
  Solid = true
  Symmetric = false
FEATURE [Part::MultiFuse] Fusion127  label="removeFromBottom001"
  Placement = pos=(2,0,0) rot=(0,0,1;0rad)
  Shapes = -> [Extrude059,Extrude060]
FEATURE [Part::Cylinder] Cylinder052
  Angle = 360
  AttacherType = Attacher::AttachEngine3D
  Height = 20
  Placement = pos=(0,0,36.15) rot=(0,0,1;0rad)
  Radius = 14
FEATURE [Part::Cylinder] Cylinder053
  Angle = 360
  AttacherType = Attacher::AttachEngine3D
  Height = 10
  Placement = pos=(0,0,36.15) rot=(0,0,1;0rad)
  Radius = 4
FEATURE [Part::MultiFuse] Fusion128  label="removeToCreteHoleForPlugHousing044"
  Placement = pos=(70,19,36) rot=(0,1,0;1.5708rad)
  Shapes = -> [Cylinder052,Cylinder053]
FEATURE [Part::Cut] Cut052  label="bottom011"
  Base = -> Extrude043
  Tool = -> Fusion128
FEATURE [Part::Cut] Cut054  label="bottom012"
  Base = -> Cut052
  Tool = -> Fusion115
FEATURE [Sketcher::SketchObject] Sketch070
  FullyConstrained = true
  Placement = pos=(117,19,0) rot=(0.57735,0.57735,0.57735;2.0944rad)
  sketch-geometry (48):
    g0: LineSegment StartX=-49.19 StartY=69.25 StartZ=0 EndX=-49.19 EndY=66.25 EndZ=0
    g1: LineSegment StartX=-49.19 StartY=63.5 StartZ=0 EndX=-49.19 EndY=60.5 EndZ=0
    g2: LineSegment StartX=-49.19 StartY=57.75 StartZ=0 EndX=-49.19 EndY=54.75 EndZ=0
    g3: LineSegment StartX=-49.19 StartY=52 StartZ=0 EndX=-49.19 EndY=49 EndZ=0
    g4: LineSegment StartX=-49.19 StartY=46.25 StartZ=0 EndX=-49.19 EndY=43.25 EndZ=0
    g5: LineSegment StartX=-49.19 StartY=40.5 StartZ=0 EndX=-49.19 EndY=37.5 EndZ=0
    g6: LineSegment StartX=-49.19 StartY=34.5 StartZ=0 EndX=-49.19 EndY=31.5 EndZ=0
    g7: LineSegment StartX=-49.19 StartY=28.75 StartZ=0 EndX=-49.19 EndY=25.75 EndZ=0
    g8: LineSegment StartX=-49.19 StartY=23 StartZ=0 EndX=-49.19 EndY=20 EndZ=0
    g9: LineSegment StartX=-49.19 StartY=17.25 StartZ=0 EndX=-49.19 EndY=14.25 EndZ=0
    g10: LineSegment StartX=-49.19 StartY=11.5 StartZ=0 EndX=-49.19 EndY=8.5 EndZ=0
    g11: LineSegment StartX=-49.19 StartY=5.75 StartZ=0 EndX=-49.19 EndY=2.75 EndZ=0
    g12: ArcOfCircle CenterX=-1.5 CenterY=67.75 CenterZ=0 NormalX=0 NormalY=0 NormalZ=1 AngleXU=0 Radius=1.5 StartAngle=4.71239 EndAngle=7.85398
    g13: ArcOfCircle CenterX=-1.5 CenterY=62 CenterZ=0 NormalX=0 NormalY=0 NormalZ=1 AngleXU=0 Radius=1.5 StartAngle=4.71239 EndAngle=7.85398
    g14: ArcOfCircle CenterX=-1.5 CenterY=56.25 CenterZ=0 NormalX=0 NormalY=0 NormalZ=1 AngleXU=0 Radius=1.5 StartAngle=4.71239 EndAngle=7.85398
    g15: ArcOfCircle CenterX=-11.49 CenterY=50.5 CenterZ=0 NormalX=0 NormalY=0 NormalZ=1 AngleXU=0 Radius=1.5 StartAngle=4.71239 EndAngle=7.85398
    g16: ArcOfCircle CenterX=-16.28 CenterY=44.75 CenterZ=0 NormalX=0 NormalY=0 NormalZ=1 AngleXU=0 Radius=1.5 StartAngle=4.71239 EndAngle=7.85398
    g17: ArcOfCircle CenterX=-18.2337 CenterY=39 CenterZ=0 NormalX=0 NormalY=0 NormalZ=1 AngleXU=0 Radius=1.5 StartAngle=4.71485 EndAngle=7.85398
    g18: ArcOfCircle CenterX=-16.2837 CenterY=27.25 CenterZ=0 NormalX=0 NormalY=0 NormalZ=1 AngleXU=0 Radius=1.5 StartAngle=4.71485 EndAngle=7.85398
    g19: ArcOfCircle CenterX=-18.2337 CenterY=33 CenterZ=0 NormalX=0 NormalY=0 NormalZ=1 AngleXU=0 Radius=1.5 StartAngle=4.71485 EndAngle=7.85398
    g20: ArcOfCircle CenterX=-11.49 CenterY=21.5 CenterZ=0 NormalX=0 NormalY=0 NormalZ=1 AngleXU=0 Radius=1.5 StartAngle=4.71239 EndAngle=7.85398
    g21: ArcOfCircle CenterX=-1.5 CenterY=4.25 CenterZ=0 NormalX=0 NormalY=0 NormalZ=1 AngleXU=0 Radius=1.5 StartAngle=4.71239 EndAngle=7.85398
    g22: ArcOfCircle CenterX=-1.5 CenterY=10 CenterZ=0 NormalX=0 NormalY=0 NormalZ=1 AngleXU=0 Radius=1.5 StartAngle=4.71239 EndAngle=7.85398
    g23: ArcOfCircle CenterX=-1.5 CenterY=15.75 CenterZ=0 NormalX=0 NormalY=0 NormalZ=1 AngleXU=0 Radius=1.5 StartAngle=4.71239 EndAngle=7.85398
    g24: LineSegment StartX=-49.19 StartY=69.25 StartZ=0 EndX=-1.5 EndY=69.25 EndZ=0
    g25: LineSegment StartX=-49.19 StartY=66.25 StartZ=0 EndX=-1.5 EndY=66.25 EndZ=0
    g26: LineSegment StartX=-49.19 StartY=63.5 StartZ=0 EndX=-1.5 EndY=63.5 EndZ=0
    g27: LineSegment StartX=-49.19 StartY=60.5 StartZ=0 EndX=-1.5 EndY=60.5 EndZ=0
    g28: LineSegment StartX=-49.19 StartY=57.75 StartZ=0 EndX=-1.5 EndY=57.75 EndZ=0
    g29: LineSegment StartX=-49.19 StartY=54.75 StartZ=0 EndX=-1.5 EndY=54.75 EndZ=0
    g30: LineSegment StartX=-49.19 StartY=52 StartZ=0 EndX=-11.49 EndY=52 EndZ=0
    g31: LineSegment StartX=-49.19 StartY=49 StartZ=0 EndX=-11.49 EndY=49 EndZ=0
    g32: LineSegment StartX=-49.19 StartY=46.25 StartZ=0 EndX=-16.28 EndY=46.25 EndZ=0
    g33: LineSegment StartX=-49.19 StartY=43.25 StartZ=0 EndX=-16.28 EndY=43.25 EndZ=0
    g34: LineSegment StartX=-49.19 StartY=40.5 StartZ=0 EndX=-18.2337 EndY=40.5 EndZ=0
    g35: LineSegment StartX=-49.19 StartY=37.5 StartZ=0 EndX=-18.23 EndY=37.5 EndZ=0
    g36: LineSegment StartX=-49.19 StartY=34.5 StartZ=0 EndX=-18.2337 EndY=34.5 EndZ=0
    g37: LineSegment StartX=-49.19 StartY=31.5 StartZ=0 EndX=-18.23 EndY=31.5 EndZ=0
    g38: LineSegment StartX=-49.19 StartY=28.75 StartZ=0 EndX=-16.2837 EndY=28.75 EndZ=0
    g39: LineSegment StartX=-49.19 StartY=25.75 StartZ=0 EndX=-16.28 EndY=25.75 EndZ=0
    g40: LineSegment StartX=-49.19 StartY=23 StartZ=0 EndX=-11.49 EndY=23 EndZ=0
    g41: LineSegment StartX=-49.19 StartY=20 StartZ=0 EndX=-11.49 EndY=20 EndZ=0
    g42: LineSegment StartX=-49.19 StartY=17.25 StartZ=0 EndX=-1.5 EndY=17.25 EndZ=0
    g43: LineSegment StartX=-49.19 StartY=14.25 StartZ=0 EndX=-1.5 EndY=14.25 EndZ=0
    g44: LineSegment StartX=-49.19 StartY=11.5 StartZ=0 EndX=-1.5 EndY=11.5 EndZ=0
    g45: LineSegment StartX=-49.19 StartY=8.5 StartZ=0 EndX=-1.5 EndY=8.5 EndZ=0
    g46: LineSegment StartX=-49.19 StartY=5.75 StartZ=0 EndX=-1.5 EndY=5.75 EndZ=0
    g47: LineSegment StartX=-49.19 StartY=2.75 StartZ=0 EndX=-1.5 EndY=2.75 EndZ=0
  constraints (120):
    c: Vertical(g0)
    c: Distance(g0) = 3
    c: Block(g0)
    c: Vertical(g1)
    c: Distance(g1) = 3
    c: Vertical(g2)
    c: Equal(g0,g2) = 3
    c: Block(g2)
    c: Vertical(g3)
    c: Equal(g1,g3) = 3
    c: Vertical(g4)
    c: Equal(g0,g4) = 3
    c: Block(g4)
    c: Vertical(g5)
    c: Equal(g1,g5) = 3
    c: Vertical(g6)
    c: Equal(g0,g6) = 3
    c: Block(g6)
    c: Vertical(g7)
    c: Equal(g1,g7) = 3
    c: Vertical(g8)
    c: Equal(g0,g8) = 3
    c: Block(g8)
    c: Vertical(g9)
    c: Equal(g1,g9) = 3
    c: Vertical(g10)
    c: Equal(g0,g10) = 3
    c: Block(g10)
    c: Vertical(g11)
    c: Equal(g1,g11) = 3
    c: Block(g12)
    c: Block(g13)
    c: Block(g14)
    c: Block(g15)
    c: Block(g16)
    c: Block(g17)
    c: Block(g18)
    c: Block(g19)
    c: Block(g20)
    c: Block(g21)
    c: Block(g22)
    c: Block(g23)
    c: Block(g11)
    c: Block(g9)
    c: Block(g7)
    c: Block(g5)
    c: Block(g3)
    c: Block(g1)
    c: Coincident(g24,g0)
    c: Coincident(g24,g12)
    c: Horizontal(g24)
    c: Coincident(g25,g0)
    c: Coincident(g25,g12)
    c: Horizontal(g25)
    c: Coincident(g26,g1)
    c: Coincident(g26,g13)
    c: Horizontal(g26)
    c: Coincident(g27,g1)
    c: Coincident(g27,g13)
    c: Horizontal(g27)
    c: Coincident(g28,g2)
    c: Coincident(g28,g14)
    c: Horizontal(g28)
    c: Coincident(g29,g2)
    c: Coincident(g29,g14)
    c: Horizontal(g29)
    c: Coincident(g30,g3)
    c: Coincident(g30,g15)
    c: Horizontal(g30)
    c: Coincident(g31,g3)
    c: Coincident(g31,g15)
    c: Horizontal(g31)
    c: Coincident(g32,g4)
    c: Coincident(g32,g16)
    c: Horizontal(g32)
    c: Coincident(g33,g4)
    c: Coincident(g33,g16)
    c: Horizontal(g33)
    c: Coincident(g34,g5)
    c: Coincident(g34,g17)
    c: Horizontal(g34)
    c: Coincident(g35,g5)
    c: Coincident(g35,g17)
    c: Horizontal(g35)
    c: Coincident(g36,g6)
    c: Coincident(g36,g19)
    c: Horizontal(g36)
    c: Coincident(g37,g6)
    c: Coincident(g37,g19)
    c: Horizontal(g37)
    c: Coincident(g38,g7)
    c: Coincident(g38,g18)
    c: Horizontal(g38)
    c: Coincident(g39,g7)
    c: Coincident(g39,g18)
    c: Horizontal(g39)
    c: Coincident(g40,g8)
    c: Coincident(g40,g20)
    c: Horizontal(g40)
    c: Coincident(g41,g8)
    c: Coincident(g41,g20)
    c: Horizontal(g41)
    c: Coincident(g42,g9)
    c: Coincident(g42,g23)
    c: Horizontal(g42)
    c: Coincident(g43,g9)
    c: Coincident(g43,g23)
    c: Horizontal(g43)
    c: Coincident(g44,g10)
    c: Coincident(g44,g22)
    c: Horizontal(g44)
    c: Coincident(g45,g10)
    c: Coincident(g45,g22)
    c: Horizontal(g45)
    c: Coincident(g46,g11)
    c: Coincident(g46,g21)
    c: Horizontal(g46)
    c: Coincident(g47,g11)
    c: Coincident(g47,g21)
    c: Horizontal(g47)
FEATURE [Part::Extrusion] Extrude061
  Base = -> Sketch070
  Dir = (1,0,0)
  DirMode = 2
  FaceMakerClass = Part::FaceMakerBullseye
  LengthFwd = 23
  LengthRev = 0
  Placement = pos=(-19,0,0) rot=(0,0,1;0rad)
  Solid = true
  Symmetric = false
FEATURE [Part::Fillet] Fillet052  label="removeToCreateVentalationHoles002"
  Base = -> Extrude061
  Edges = <same value as first occurrence — deduplicated (x6 in doc)>
  Placement = pos=(7,0.02,0) rot=(0,0,1;0rad)
FEATURE [Part::MultiFuse] Fusion130  label="bottom013"
  Shapes = -> [Cut054,Cut034]
FEATURE [Part::Cut] Cut055
  Base = -> Fusion130
  Tool = -> Fillet052
FEATURE [Part::Cylinder] Cylinder054
  Angle = 360
  AttacherType = Attacher::AttachEngine3D
  Height = 20
  Placement = pos=(0,0,36.15) rot=(0,0,1;0rad)
  Radius = 4
FEATURE [Sketcher::SketchObject] Sketch071  label="bottomSketch002"
  FullyConstrained = true
  sketch-geometry (32):
    g0: LineSegment StartX=3.3 StartY=-6.03275e-07 StartZ=0 EndX=98 EndY=-6.03275e-07 EndZ=0
    g1: ArcOfCircle CenterX=98 CenterY=19 CenterZ=0 NormalX=0 NormalY=0 NormalZ=1 AngleXU=0 Radius=19 StartAngle=4.71239 EndAngle=5.71103
    g2: LineSegment StartX=6.3 StartY=8 StartZ=0 EndX=3.3 EndY=8 EndZ=0
    g3: LineSegment StartX=3.3 StartY=8 StartZ=0 EndX=3.3 EndY=-6.03275e-07 EndZ=0
    g4: ArcOfCircle CenterX=8.3 CenterY=5 CenterZ=0 NormalX=0 NormalY=0 NormalZ=1 AngleXU=0 Radius=2 StartAngle=3.14159 EndAngle=4.71239
    g5: LineSegment StartX=6.3 StartY=8 StartZ=0 EndX=6.3 EndY=5 EndZ=0
    g6: ArcOfCircle CenterX=98 CenterY=19 CenterZ=0 NormalX=0 NormalY=0 NormalZ=1 AngleXU=0 Radius=12.7 StartAngle=4.71239 EndAngle=6.28319
    g7: LineSegment StartX=94.7 StartY=3 StartZ=0 EndX=8.3 EndY=3 EndZ=0
    g8-g12: Circle x5 (B-spline internal-alignment scaffolding for g13; pole/knot coordinates omitted)
    g13: BSplineCurve PolesCount=5 KnotsCount=3 Degree=3 IsPeriodic=0
    g14: GeomPoint X=98 Y=6.3 Z=0
    g15: GeomPoint X=96.3938 Y=4.71946 Z=0
    g16: GeomPoint X=94.7 Y=3 Z=0
    g17-g23: Circle x7 (B-spline internal-alignment scaffolding for g24; pole/knot coordinates omitted)
    g24: BSplineCurve PolesCount=7 KnotsCount=5 Degree=3 IsPeriodic=0
    g25-g29: GeomPoint x5 (B-spline internal-alignment scaffolding for g24; pole/knot coordinates omitted)
    g30: ArcOfCircle CenterX=98 CenterY=19 CenterZ=0 NormalX=0 NormalY=0 NormalZ=1 AngleXU=0 Radius=15.7 StartAngle=5.81226 EndAngle=6.28319
    g31: LineSegment StartX=110.7 StartY=19 StartZ=0 EndX=113.7 EndY=19 EndZ=0
  constraints (41):
    c: Horizontal(g0)
    c: Coincident(g1,g0)
    c: Block(g1)
    c: Horizontal(g2)
    c: Distance(g2) = 3
    c: Coincident(g3,g2)
    c: Vertical(g3)
    c: Coincident(g3,g0)
    c: Block(g4)
    c: Block(g2)
    c: Coincident(g5,g2)
    c: Coincident(g5,g4)
    c: Vertical(g5)
    c: Coincident(g6,g1)
    c: Block(g6)
    c: Coincident(g7,g4)
    c: Horizontal(g7)
    c: Block(g0)
    c: Block(g7)
    c: Block(g3)
    c: Coincident(g13,g6)
    c: Weight(g8) = 1
    c: Equal(g8, g9-g12) x4
    c: Coincident(g13,g7)
    c: InternalAlignment(g8-g12 -> g13) x5
    c: InternalAlignment(g14,g13)
    c: InternalAlignment(g15,g13)
    c: InternalAlignment(g16,g13)
    c: Block(g13)
    c: Weight(g17) = 1
    c: Equal(g17, g18-g23) x6
    c: Coincident(g24,g1)
    c: InternalAlignment(g17-g23 -> g24) x7
    c: InternalAlignment(g25-g29 -> g24) x5
    c: Block(g24)
    c: Coincident(g30,g24)
    c: Coincident(g31,g6)
    c: Coincident(g31,g30)
    c: Horizontal(g31)
    c: Block(g31)
    c: Block(g30)
FEATURE [Part::Extrusion] Extrude062  label="bottom014"
  Base = -> Sketch071
  Dir = (0,0,1)
  DirMode = 2
  FaceMakerClass = Part::FaceMakerBullseye
  LengthFwd = 71.4
  LengthRev = 0
  Placement = pos=(0,0,0.3) rot=(0,0,1;0rad)
  Solid = true
  Symmetric = false
FEATURE [Part::Fillet] Fillet054
  Base = -> Extrude062
  Edges = 1 edges r=2.4: [Edge17]
FEATURE [Part::Fillet] Fillet055  label="bottom015"
  Base = -> Fillet054
  Edges = 1 edges r=2.4: [Edge36]
FEATURE [Part::Cylinder] Cylinder055
  Angle = 360
  AttacherType = Attacher::AttachEngine3D
  Height = 10
  Placement = pos=(0,0,36.15) rot=(0,0,1;0rad)
  Radius = 4
FEATURE [Part::MultiFuse] Fusion131  label="removeToCreateHoleForPlugHousing002"
  Placement = pos=(70,19,36.15) rot=(0,1,0;1.5708rad)
  Shapes = -> [Cylinder054,Cylinder055]
FEATURE [Part::Cut] Cut056  label="Bottom001"
  Base = -> Fillet055
  Placement = pos=(9,0,0) rot=(0,0,1;0rad)
  Tool = -> Fusion131
FEATURE [Part::Cut] Cut057
  Base = -> Cut055
  Tool = -> Cut056
FEATURE [Sketcher::SketchObject] Sketch072  label="topSketch021"
  FullyConstrained = true
  sketch-geometry (4):
    g0: ArcOfCircle CenterX=105 CenterY=19 CenterZ=0 NormalX=0 NormalY=0 NormalZ=1 AngleXU=0 Radius=20.6155 StartAngle=5.54125 EndAngle=6.28319
    g1: ArcOfCircle CenterX=105 CenterY=19 CenterZ=0 NormalX=0 NormalY=0 NormalZ=1 AngleXU=0 Radius=13 StartAngle=5.54125 EndAngle=6.28319
    g2: LineSegment StartX=118 StartY=19 StartZ=0 EndX=125.616 EndY=19 EndZ=0
    g3: LineSegment StartX=114.583 StartY=10.2157 StartZ=0 EndX=120.197 EndY=5.06982 EndZ=0
  constraints (7):
    c: Block(g0)
    c: Block(g1)
    c: Coincident(g2,g1)
    c: Coincident(g2,g0)
    c: Horizontal(g2)
    c: Coincident(g3,g1)
    c: Coincident(g3,g0)
FEATURE [Part::Extrusion] Extrude063  label="bottomPlugHousingBit003"
  Base = -> Sketch072
  Dir = (0,0,1)
  DirMode = 2
  FaceMakerClass = Part::FaceMakerBullseye
  LengthFwd = 72
  LengthRev = 0
  Solid = true
  Symmetric = false
FEATURE [Part::Cylinder] Cylinder056
  Angle = 360
  AttacherType = Attacher::AttachEngine3D
  Height = 20
  Placement = pos=(0,0,36.15) rot=(0,0,1;0rad)
  Radius = 14.3
FEATURE [Part::Cylinder] Cylinder057
  Angle = 360
  AttacherType = Attacher::AttachEngine3D
  Height = 10
  Placement = pos=(0,0,36.15) rot=(0,0,1;0rad)
  Radius = 4
FEATURE [Part::Box] Box034  label="removeToCreteHoleForPlugHousing047"
  AttacherType = Attacher::AttachEngine3D
  Height = 28.6
  Length = 20
  Placement = pos=(106.15,0,21.7) rot=(0,0,1;0rad)
  Width = 19
FEATURE [Part::Cylinder] Cylinder058
  Angle = 360
  AttacherType = Attacher::AttachEngine3D
  Height = 20
  Placement = pos=(0,0,36.15) rot=(0,0,1;0rad)
  Radius = 14.3
FEATURE [Part::Cylinder] Cylinder059
  Angle = 360
  AttacherType = Attacher::AttachEngine3D
  Height = 10
  Placement = pos=(0,0,36.15) rot=(0,0,1;0rad)
  Radius = 4
FEATURE [Part::MultiFuse] Fusion134  label="removeToCreteHoleForPlugHousing046"
  Placement = pos=(70,19,36) rot=(0,1,0;1.5708rad)
  Shapes = -> [Cylinder058,Cylinder059]
FEATURE [Part::Cylinder] Cylinder060
  Angle = 360
  AttacherType = Attacher::AttachEngine3D
  Height = 20
  Placement = pos=(0,0,36.15) rot=(0,0,1;0rad)
  Radius = 14
FEATURE [Part::Cylinder] Cylinder061
  Angle = 360
  AttacherType = Attacher::AttachEngine3D
  Height = 10
  Placement = pos=(0,0,36.15) rot=(0,0,1;0rad)
  Radius = 4
FEATURE [Part::MultiFuse] Fusion135  label="removeToCreteHoleForPlugHousing048"
  Placement = pos=(70,19,36) rot=(0,1,0;1.5708rad)
  Shapes = -> [Cylinder060,Cylinder061]
FEATURE [Part::Box] Box035  label="removeToCreteHoleForPlugHousing049"
  AttacherType = Attacher::AttachEngine3D
  Height = 28.6
  Length = 20
  Placement = pos=(106.15,0,21.7) rot=(0,0,1;0rad)
  Width = 19
FEATURE [Part::MultiFuse] Fusion133  label="removeToCreteHoleForPlugHousing045"
  Placement = pos=(0,0,-28.3) rot=(0,0,1;0rad)
  Shapes = -> [Box035,Fusion134]
FEATURE [Part::MultiFuse] Fusion138  label="removeToCreteHoleForPlugHousing051"
  Placement = pos=(70,19,36) rot=(0,1,0;1.5708rad)
  Shapes = -> [Cylinder056,Cylinder057]
FEATURE [Part::MultiFuse] Fusion137  label="removeToCreteHoleForPlugHousing050"
  Placement = pos=(0,0,28.3) rot=(0,0,1;0rad)
  Shapes = -> [Box034,Fusion138]
FEATURE [Part::MultiFuse] Fusion132  label="removeToCreatePlugHousingBottomBit002"
  Shapes = -> [Fusion133,Fusion137]
FEATURE [Part::MultiFuse] Fusion136  label="removeToCreatePlugHousingBottomBit003"
  Shapes = -> [Fusion135,Fusion132]
FEATURE [Part::Cut] Cut058  label="bottomPlugHousingBit002"
  Base = -> Extrude063
  Placement = pos=(-0.09,0,0) rot=(0,0,1;0rad)
  Tool = -> Fusion136
FEATURE [Sketcher::SketchObject] Sketch073  label="bottomSketch003"
  FullyConstrained = true
  sketch-geometry (45):
    g0: LineSegment StartX=6.29999 StartY=8 StartZ=0 EndX=3.29999 EndY=8 EndZ=0
    g1: LineSegment StartX=3.29999 StartY=8 StartZ=0 EndX=3.29999 EndY=-6.03275e-07 EndZ=0
    g2: ArcOfCircle CenterX=8.29999 CenterY=5 CenterZ=0 NormalX=0 NormalY=0 NormalZ=1 AngleXU=0 Radius=2 StartAngle=3.14159 EndAngle=4.71239
    g3: LineSegment StartX=6.29999 StartY=8 StartZ=0 EndX=6.29999 EndY=5 EndZ=0
    g4: ArcOfCircle CenterX=105 CenterY=19 CenterZ=0 NormalX=0 NormalY=0 NormalZ=1 AngleXU=0 Radius=12.7 StartAngle=4.71239 EndAngle=5.94289
    g5-g11: Circle x7 (B-spline internal-alignment scaffolding for g12; pole/knot coordinates omitted)
    g12: BSplineCurve PolesCount=7 KnotsCount=5 Degree=3 IsPeriodic=0
    g13-g17: GeomPoint x5 (B-spline internal-alignment scaffolding for g12; pole/knot coordinates omitted)
    g18: ArcOfCircle CenterX=105 CenterY=19 CenterZ=0 NormalX=0 NormalY=0 NormalZ=1 AngleXU=0 Radius=15.7 StartAngle=5.81226 EndAngle=6.28319
    g19: BSplineCurve PolesCount=5 KnotsCount=3 Degree=3 IsPeriodic=0
    g20: LineSegment StartX=8.29999 StartY=3 StartZ=0 EndX=101.7 EndY=3 EndZ=0
    g21: LineSegment StartX=3.29999 StartY=-6.03275e-07 StartZ=0 EndX=105 EndY=-6.03275e-07 EndZ=0
    g22: LineSegment StartX=120.974 StartY=8.71251 StartZ=0 EndX=122.332 EndY=7.83778 EndZ=0
    g23: LineSegment StartX=105 StartY=-6.03274e-07 StartZ=0 EndX=113 EndY=-6.03274e-07 EndZ=0
    g24: ArcOfCircle CenterX=105 CenterY=19 CenterZ=0 NormalX=0 NormalY=0 NormalZ=1 AngleXU=0 Radius=20.6155 StartAngle=5.11091 EndAngle=5.71103
    g25: ArcOfCircle CenterX=117.7 CenterY=19 CenterZ=0 NormalX=0 NormalY=0 NormalZ=1 AngleXU=0 Radius=3 StartAngle=1.2e-15 EndAngle=2.10468
    g26: Circle CenterX=116.345 CenterY=16.3232 CenterZ=0 NormalX=0 NormalY=0 NormalZ=1 AngleXU=0 Radius=1
    g27: Circle CenterX=117.24 CenterY=15.7584 CenterZ=0 NormalX=0 NormalY=0 NormalZ=1 AngleXU=0 Radius=1
    g28: Circle CenterX=116.972 CenterY=14.7612 CenterZ=0 NormalX=0 NormalY=0 NormalZ=1 AngleXU=0 Radius=1
    g29: BSplineCurve PolesCount=3 KnotsCount=2 Degree=2 IsPeriodic=0
    g30: GeomPoint X=116.345 Y=16.3232 Z=0
    g31: GeomPoint X=116.972 Y=14.7612 Z=0
    g32: Circle CenterX=115.828 CenterY=17.157 CenterZ=0 NormalX=0 NormalY=0 NormalZ=1 AngleXU=0 Radius=1
    g33: Circle CenterX=115.841 CenterY=16.639 CenterZ=0 NormalX=0 NormalY=0 NormalZ=1 AngleXU=0 Radius=1
    g34: Circle CenterX=116.345 CenterY=16.3232 CenterZ=0 NormalX=0 NormalY=0 NormalZ=1 AngleXU=0 Radius=1
    g35: BSplineCurve PolesCount=3 KnotsCount=2 Degree=2 IsPeriodic=0
    g36: GeomPoint X=115.828 Y=17.157 Z=0
    g37: GeomPoint X=116.345 Y=16.3232 Z=0
    g38: LineSegment StartX=115.828 StartY=17.157 StartZ=0 EndX=115.828 EndY=20.8307 EndZ=0
    g39: Circle CenterX=115.828 CenterY=20.8307 CenterZ=0 NormalX=0 NormalY=0 NormalZ=1 AngleXU=0 Radius=1
    g40: Circle CenterX=115.831 CenterY=21.3396 CenterZ=0 NormalX=0 NormalY=0 NormalZ=1 AngleXU=0 Radius=1
    g41: Circle CenterX=116.173 CenterY=21.5825 CenterZ=0 NormalX=0 NormalY=0 NormalZ=1 AngleXU=0 Radius=1
    g42: BSplineCurve PolesCount=3 KnotsCount=2 Degree=2 IsPeriodic=0
    g43: GeomPoint X=115.828 Y=20.8307 Z=0
    g44: GeomPoint X=116.173 Y=21.5825 Z=0
  constraints (70):
    c: Horizontal(g0)
    c: Distance(g0) = 3
    c: Coincident(g1,g0)
    c: Vertical(g1)
    c: Block(g2)
    c: Block(g0)
    c: Coincident(g3,g0)
    c: Coincident(g3,g2)
    c: Vertical(g3)
    c: Block(g1)
    c: Block(g4)
    c: Coincident(g19,g4)
    c: Block(g19)
    c: Equal(g5, g6-g11) x6
    c: InternalAlignment(g5-g11 -> g12) x7
    c: InternalAlignment(g13-g17 -> g12) x5
    c: Block(g12)
    c: Coincident(g18,g12)
    c: Block(g18)
    c: Coincident(g20,g2)
    c: Coincident(g20,g19)
    c: Horizontal(g20)
    c: Distance(g20) = 93.4
    c: Coincident(g21,g1)
    c: Horizontal(g21)
    c: Distance(g21) = 101.7
    c: Horizontal(g23)
    c: Distance(g23) = 8
    c: Coincident(g24,g23)
    c: Block(g23)
    c: Coincident(g22,g24)
    c: Block(g24)
    c: Block(g22)
    c: Distance(g22) = 1.61553
    c: Coincident(g25,g18)
    c: Block(g25)
    c: Weight(g26) = 1
    c: Equal(g26,g27)
    c: Equal(g26,g28)
    c: Coincident(g29,g4)
    c: InternalAlignment(g26,g29)
    c: InternalAlignment(g27,g29)
    c: InternalAlignment(g28,g29)
    c: InternalAlignment(g30,g29)
    c: InternalAlignment(g31,g29)
    c: Block(g29)
    c: Weight(g32) = 1
    c: Equal(g32,g33)
    c: Equal(g32,g34)
    c: Coincident(g35,g29)
    c: InternalAlignment(g32,g35)
    c: InternalAlignment(g33,g35)
    c: InternalAlignment(g34,g35)
    c: InternalAlignment(g36,g35)
    c: InternalAlignment(g37,g35)
    c: Block(g35)
    c: Coincident(g38,g35)
    c: Vertical(g38)
    c: Block(g38)
    c: Coincident(g42,g38)
    c: Weight(g39) = 1
    c: Equal(g39,g40)
    c: Equal(g39,g41)
    c: Coincident(g42,g25)
    c: InternalAlignment(g39,g42)
    c: InternalAlignment(g40,g42)
    c: InternalAlignment(g41,g42)
    c: InternalAlignment(g43,g42)
    c: InternalAlignment(g44,g42)
    c: Block(g42)
FEATURE [Part::Extrusion] Extrude064  label="bottom016"
  Base = -> Sketch073
  Dir = (0,0,1)
  DirMode = 2
  FaceMakerClass = Part::FaceMakerBullseye
  LengthFwd = 71.4
  LengthRev = 0
  Placement = pos=(0,0,0.3) rot=(0,0,1;0rad)
  Solid = true
  Symmetric = false
FEATURE [Part::Revolution] Revolve157  label="removeToCreateScrewAndThreadedInsertHole063"
  Angle = 360
  Axis = (0,1,0)
  Base = (0,0,0)
  FaceMakerClass = Part::FaceMakerBullseye
  Placement = pos=(12.5,0,10) rot=(0,0,1;0rad)
  Solid = false
  Source = -> Face141
  Symmetric = false
FEATURE [Sketcher::SketchObject] Sketch074
  FullyConstrained = true
  Placement = pos=(117,19,0) rot=(0.57735,0.57735,0.57735;2.0944rad)
  sketch-geometry (48):
    g0: LineSegment StartX=-49.19 StartY=69.25 StartZ=0 EndX=-49.19 EndY=66.25 EndZ=0
    g1: LineSegment StartX=-49.19 StartY=63.5 StartZ=0 EndX=-49.19 EndY=60.5 EndZ=0
    g2: LineSegment StartX=-49.19 StartY=57.75 StartZ=0 EndX=-49.19 EndY=54.75 EndZ=0
    g3: LineSegment StartX=-49.19 StartY=52 StartZ=0 EndX=-49.19 EndY=49 EndZ=0
    g4: LineSegment StartX=-49.19 StartY=46.25 StartZ=0 EndX=-49.19 EndY=43.25 EndZ=0
    g5: LineSegment StartX=-49.19 StartY=40.5 StartZ=0 EndX=-49.19 EndY=37.5 EndZ=0
    g6: LineSegment StartX=-49.19 StartY=34.5 StartZ=0 EndX=-49.19 EndY=31.5 EndZ=0
    g7: LineSegment StartX=-49.19 StartY=28.75 StartZ=0 EndX=-49.19 EndY=25.75 EndZ=0
    g8: LineSegment StartX=-49.19 StartY=23 StartZ=0 EndX=-49.19 EndY=20 EndZ=0
    g9: LineSegment StartX=-49.19 StartY=17.25 StartZ=0 EndX=-49.19 EndY=14.25 EndZ=0
    g10: LineSegment StartX=-49.19 StartY=11.5 StartZ=0 EndX=-49.19 EndY=8.5 EndZ=0
    g11: LineSegment StartX=-49.19 StartY=5.75 StartZ=0 EndX=-49.19 EndY=2.75 EndZ=0
    g12: ArcOfCircle CenterX=-1.5 CenterY=67.75 CenterZ=0 NormalX=0 NormalY=0 NormalZ=1 AngleXU=0 Radius=1.5 StartAngle=4.71239 EndAngle=7.85398
    g13: ArcOfCircle CenterX=-1.5 CenterY=62 CenterZ=0 NormalX=0 NormalY=0 NormalZ=1 AngleXU=0 Radius=1.5 StartAngle=4.71239 EndAngle=7.85398
    g14: ArcOfCircle CenterX=-1.5 CenterY=56.25 CenterZ=0 NormalX=0 NormalY=0 NormalZ=1 AngleXU=0 Radius=1.5 StartAngle=4.71239 EndAngle=7.85398
    g15: ArcOfCircle CenterX=-11.49 CenterY=50.5 CenterZ=0 NormalX=0 NormalY=0 NormalZ=1 AngleXU=0 Radius=1.5 StartAngle=4.71239 EndAngle=7.85398
    g16: ArcOfCircle CenterX=-16.28 CenterY=44.75 CenterZ=0 NormalX=0 NormalY=0 NormalZ=1 AngleXU=0 Radius=1.5 StartAngle=4.71239 EndAngle=7.85398
    g17: ArcOfCircle CenterX=-18.2337 CenterY=39 CenterZ=0 NormalX=0 NormalY=0 NormalZ=1 AngleXU=0 Radius=1.5 StartAngle=4.71485 EndAngle=7.85398
    g18: ArcOfCircle CenterX=-16.2837 CenterY=27.25 CenterZ=0 NormalX=0 NormalY=0 NormalZ=1 AngleXU=0 Radius=1.5 StartAngle=4.71485 EndAngle=7.85398
    g19: ArcOfCircle CenterX=-18.2337 CenterY=33 CenterZ=0 NormalX=0 NormalY=0 NormalZ=1 AngleXU=0 Radius=1.5 StartAngle=4.71485 EndAngle=7.85398
    g20: ArcOfCircle CenterX=-11.49 CenterY=21.5 CenterZ=0 NormalX=0 NormalY=0 NormalZ=1 AngleXU=0 Radius=1.5 StartAngle=4.71239 EndAngle=7.85398
    g21: ArcOfCircle CenterX=-1.5 CenterY=4.25 CenterZ=0 NormalX=0 NormalY=0 NormalZ=1 AngleXU=0 Radius=1.5 StartAngle=4.71239 EndAngle=7.85398
    g22: ArcOfCircle CenterX=-1.5 CenterY=10 CenterZ=0 NormalX=0 NormalY=0 NormalZ=1 AngleXU=0 Radius=1.5 StartAngle=4.71239 EndAngle=7.85398
    g23: ArcOfCircle CenterX=-1.5 CenterY=15.75 CenterZ=0 NormalX=0 NormalY=0 NormalZ=1 AngleXU=0 Radius=1.5 StartAngle=4.71239 EndAngle=7.85398
    g24: LineSegment StartX=-49.19 StartY=69.25 StartZ=0 EndX=-1.5 EndY=69.25 EndZ=0
    g25: LineSegment StartX=-49.19 StartY=66.25 StartZ=0 EndX=-1.5 EndY=66.25 EndZ=0
    g26: LineSegment StartX=-49.19 StartY=63.5 StartZ=0 EndX=-1.5 EndY=63.5 EndZ=0
    g27: LineSegment StartX=-49.19 StartY=60.5 StartZ=0 EndX=-1.5 EndY=60.5 EndZ=0
    g28: LineSegment StartX=-49.19 StartY=57.75 StartZ=0 EndX=-1.5 EndY=57.75 EndZ=0
    g29: LineSegment StartX=-49.19 StartY=54.75 StartZ=0 EndX=-1.5 EndY=54.75 EndZ=0
    g30: LineSegment StartX=-49.19 StartY=52 StartZ=0 EndX=-11.49 EndY=52 EndZ=0
    g31: LineSegment StartX=-49.19 StartY=49 StartZ=0 EndX=-11.49 EndY=49 EndZ=0
    g32: LineSegment StartX=-49.19 StartY=46.25 StartZ=0 EndX=-16.28 EndY=46.25 EndZ=0
    g33: LineSegment StartX=-49.19 StartY=43.25 StartZ=0 EndX=-16.28 EndY=43.25 EndZ=0
    g34: LineSegment StartX=-49.19 StartY=40.5 StartZ=0 EndX=-18.2337 EndY=40.5 EndZ=0
    g35: LineSegment StartX=-49.19 StartY=37.5 StartZ=0 EndX=-18.23 EndY=37.5 EndZ=0
    g36: LineSegment StartX=-49.19 StartY=34.5 StartZ=0 EndX=-18.2337 EndY=34.5 EndZ=0
    g37: LineSegment StartX=-49.19 StartY=31.5 StartZ=0 EndX=-18.23 EndY=31.5 EndZ=0
    g38: LineSegment StartX=-49.19 StartY=28.75 StartZ=0 EndX=-16.2837 EndY=28.75 EndZ=0
    g39: LineSegment StartX=-49.19 StartY=25.75 StartZ=0 EndX=-16.28 EndY=25.75 EndZ=0
    g40: LineSegment StartX=-49.19 StartY=23 StartZ=0 EndX=-11.49 EndY=23 EndZ=0
    g41: LineSegment StartX=-49.19 StartY=20 StartZ=0 EndX=-11.49 EndY=20 EndZ=0
    g42: LineSegment StartX=-49.19 StartY=17.25 StartZ=0 EndX=-1.5 EndY=17.25 EndZ=0
    g43: LineSegment StartX=-49.19 StartY=14.25 StartZ=0 EndX=-1.5 EndY=14.25 EndZ=0
    g44: LineSegment StartX=-49.19 StartY=11.5 StartZ=0 EndX=-1.5 EndY=11.5 EndZ=0
    g45: LineSegment StartX=-49.19 StartY=8.5 StartZ=0 EndX=-1.5 EndY=8.5 EndZ=0
    g46: LineSegment StartX=-49.19 StartY=5.75 StartZ=0 EndX=-1.5 EndY=5.75 EndZ=0
    g47: LineSegment StartX=-49.19 StartY=2.75 StartZ=0 EndX=-1.5 EndY=2.75 EndZ=0
  constraints (120):
    c: Vertical(g0)
    c: Distance(g0) = 3
    c: Block(g0)
    c: Vertical(g1)
    c: Distance(g1) = 3
    c: Vertical(g2)
    c: Equal(g0,g2) = 3
    c: Block(g2)
    c: Vertical(g3)
    c: Equal(g1,g3) = 3
    c: Vertical(g4)
    c: Equal(g0,g4) = 3
    c: Block(g4)
    c: Vertical(g5)
    c: Equal(g1,g5) = 3
    c: Vertical(g6)
    c: Equal(g0,g6) = 3
    c: Block(g6)
    c: Vertical(g7)
    c: Equal(g1,g7) = 3
    c: Vertical(g8)
    c: Equal(g0,g8) = 3
    c: Block(g8)
    c: Vertical(g9)
    c: Equal(g1,g9) = 3
    c: Vertical(g10)
    c: Equal(g0,g10) = 3
    c: Block(g10)
    c: Vertical(g11)
    c: Equal(g1,g11) = 3
    c: Block(g12)
    c: Block(g13)
    c: Block(g14)
    c: Block(g15)
    c: Block(g16)
    c: Block(g17)
    c: Block(g18)
    c: Block(g19)
    c: Block(g20)
    c: Block(g21)
    c: Block(g22)
    c: Block(g23)
    c: Block(g11)
    c: Block(g9)
    c: Block(g7)
    c: Block(g5)
    c: Block(g3)
    c: Block(g1)
    c: Coincident(g24,g0)
    c: Coincident(g24,g12)
    c: Horizontal(g24)
    c: Coincident(g25,g0)
    c: Coincident(g25,g12)
    c: Horizontal(g25)
    c: Coincident(g26,g1)
    c: Coincident(g26,g13)
    c: Horizontal(g26)
    c: Coincident(g27,g1)
    c: Coincident(g27,g13)
    c: Horizontal(g27)
    c: Coincident(g28,g2)
    c: Coincident(g28,g14)
    c: Horizontal(g28)
    c: Coincident(g29,g2)
    c: Coincident(g29,g14)
    c: Horizontal(g29)
    c: Coincident(g30,g3)
    c: Coincident(g30,g15)
    c: Horizontal(g30)
    c: Coincident(g31,g3)
    c: Coincident(g31,g15)
    c: Horizontal(g31)
    c: Coincident(g32,g4)
    c: Coincident(g32,g16)
    c: Horizontal(g32)
    c: Coincident(g33,g4)
    c: Coincident(g33,g16)
    c: Horizontal(g33)
    c: Coincident(g34,g5)
    c: Coincident(g34,g17)
    c: Horizontal(g34)
    c: Coincident(g35,g5)
    c: Coincident(g35,g17)
    c: Horizontal(g35)
    c: Coincident(g36,g6)
    c: Coincident(g36,g19)
    c: Horizontal(g36)
    c: Coincident(g37,g6)
    c: Coincident(g37,g19)
    c: Horizontal(g37)
    c: Coincident(g38,g7)
    c: Coincident(g38,g18)
    c: Horizontal(g38)
    c: Coincident(g39,g7)
    c: Coincident(g39,g18)
    c: Horizontal(g39)
    c: Coincident(g40,g8)
    c: Coincident(g40,g20)
    c: Horizontal(g40)
    c: Coincident(g41,g8)
    c: Coincident(g41,g20)
    c: Horizontal(g41)
    c: Coincident(g42,g9)
    c: Coincident(g42,g23)
    c: Horizontal(g42)
    c: Coincident(g43,g9)
    c: Coincident(g43,g23)
    c: Horizontal(g43)
    c: Coincident(g44,g10)
    c: Coincident(g44,g22)
    c: Horizontal(g44)
    c: Coincident(g45,g10)
    c: Coincident(g45,g22)
    c: Horizontal(g45)
    c: Coincident(g46,g11)
    c: Coincident(g46,g21)
    c: Horizontal(g46)
    c: Coincident(g47,g11)
    c: Coincident(g47,g21)
    c: Horizontal(g47)
FEATURE [Part::Extrusion] Extrude065
  Base = -> Sketch074
  Dir = (1,0,0)
  DirMode = 2
  FaceMakerClass = Part::FaceMakerBullseye
  LengthFwd = 23
  LengthRev = 0
  Placement = pos=(-19,0,0) rot=(0,0,1;0rad)
  Solid = true
  Symmetric = false
FEATURE [Part::Fillet] Fillet056  label="removeToCreateVentalationHoles003"
  Base = -> Extrude065
  Edges = <same value as first occurrence — deduplicated (x6 in doc)>
  Placement = pos=(7,0.02,0) rot=(0,0,1;0rad)
FEATURE [Part::Revolution] Revolve158  label="removeToCreateScrewAndThreadedInsertHole065"
  Angle = 360
  Axis = (0,1,0)
  Base = (0,0,0)
  FaceMakerClass = Part::FaceMakerBullseye
  Placement = pos=(12.5,0,62) rot=(0,0,1;0rad)
  Solid = false
  Source = -> Face146
  Symmetric = false
FEATURE [Part::Revolution] Revolve159  label="removeToCreateScrewAndThreadedInsertHole066"
  Angle = 360
  Axis = (0,1,0)
  Base = (0,0,0)
  FaceMakerClass = Part::FaceMakerBullseye
  Placement = pos=(89.5,0,68.5) rot=(0,0,1;0rad)
  Solid = false
  Source = -> Face143
  Symmetric = false
FEATURE [Part::Revolution] Revolve160  label="removeToCreateScrewAndThreadedInsertHole067"
  Angle = 360
  Axis = (0,1,0)
  Base = (0,0,0)
  FaceMakerClass = Part::FaceMakerBullseye
  Placement = pos=(89.5,0,3.5) rot=(0,0,1;0rad)
  Solid = false
  Source = -> Face142
  Symmetric = false
FEATURE [Part::Revolution] Revolve161  label="removeToCreateScrewAndThreadedInsertHole068"
  Angle = 360
  Axis = (0,1,0)
  Base = (0,0,0)
  FaceMakerClass = Part::FaceMakerBullseye
  Placement = pos=(109.5,4.7,3.5) rot=(0,0,1;0rad)
  Solid = false
  Source = -> Face145
  Symmetric = false
FEATURE [Part::Revolution] Revolve162  label="removeToCreateScrewAndThreadedInsertHole069"
  Angle = 360
  Axis = (0,1,0)
  Base = (0,0,0)
  FaceMakerClass = Part::FaceMakerBullseye
  Placement = pos=(109.5,4.7,68.5) rot=(0,0,1;0rad)
  Solid = false
  Source = -> Face144
  Symmetric = false
FEATURE [Part::MultiFuse] Fusion141  label="removeToCreateScrewAndThreadedInsertHole064"
  Shapes = -> [Revolve162,Revolve161,Revolve160,Revolve159,Revolve158,Revolve157]
FEATURE [Part::Cylinder] Cylinder062
  Angle = 360
  AttacherType = Attacher::AttachEngine3D
  Height = 20
  Placement = pos=(0,0,36.15) rot=(0,0,1;0rad)
  Radius = 14
FEATURE [Part::Cylinder] Cylinder063
  Angle = 360
  AttacherType = Attacher::AttachEngine3D
  Height = 10
  Placement = pos=(0,0,36.15) rot=(0,0,1;0rad)
  Radius = 4
FEATURE [Part::MultiFuse] Fusion139  label="removeToCreteHoleForPlugHousing052"
  Placement = pos=(70,19,36) rot=(0,1,0;1.5708rad)
  Shapes = -> [Cylinder062,Cylinder063]
FEATURE [Part::Cut] Cut060  label="bottom017"
  Base = -> Extrude064
  Tool = -> Fusion139
FEATURE [Part::Cut] Cut061  label="bottom019"
  Base = -> Cut060
  Tool = -> Fusion141
FEATURE [Part::MultiFuse] Fusion140  label="bottom018"
  Shapes = -> [Cut061,Cut058]
FEATURE [Part::Cut] Cut059  label="bottom020"
  Base = -> Fusion140
  Tool = -> Fillet056
FEATURE [Part::Box] Box036  label="Cube021"
  AttacherType = Attacher::AttachEngine3D
  Height = 80
  Length = 26
  Placement = pos=(0,-1,-5) rot=(0,0,1;0rad)
  Width = 11
FEATURE [Part::Cut] Cut062  label="removeFromBottom002"
  Base = -> Cut057
  Tool = -> Box036
FEATURE [Part::Cut] Cut063
  Base = -> Cut059
  Tool = -> Cut062
FEATURE [Part::Cut] Cut064  label="pcbStands"
  Base = -> Fusion095
  Tool = -> Fusion127
FEATURE [Sketcher::SketchObject] Sketch075  label="topSketch022"
  FullyConstrained = true
  sketch-geometry (6):
    g0: LineSegment StartX=19 StartY=38 StartZ=0 EndX=117 EndY=38 EndZ=0
    g1: ArcOfCircle CenterX=19 CenterY=19 CenterZ=0 NormalX=0 NormalY=0 NormalZ=1 AngleXU=0 Radius=19 StartAngle=1.5708 EndAngle=3.14159
    g2: LineSegment StartX=117 StartY=38 StartZ=0 EndX=117 EndY=19 EndZ=0
    g3: LineSegment StartX=98 StartY=1.0161e-12 StartZ=0 EndX=5.22862e-06 EndY=1.0161e-12 EndZ=0
    g4: LineSegment StartX=5.22862e-06 StartY=19 StartZ=0 EndX=5.22862e-06 EndY=1.0161e-12 EndZ=0
    g5: ArcOfCircle CenterX=98 CenterY=19 CenterZ=0 NormalX=0 NormalY=0 NormalZ=1 AngleXU=0 Radius=19 StartAngle=4.71239 EndAngle=6.28319
  constraints (16):
    c: Horizontal(g0)
    c: Distance(g0) = 98
    c: Coincident(g1,g0)
    c: Block(g1)
    c: Coincident(g2,g0)
    c: Vertical(g2)
    c: Distance(g2) = 19
    c: Horizontal(g3)
    c: Coincident(g4,g1)
    c: Vertical(g4)
    c: Coincident(g3,g4)
    c: Block(g3)
    c: Coincident(g5,g2)
    c: Coincident(g5,g3)
    c: Block(g0)
    c: Block(g5)
FEATURE [Part::Extrusion] Extrude067  label="sideB003"
  Base = -> Sketch075
  Dir = (0,0,1)
  DirMode = 2
  FaceMakerClass = Part::FaceMakerBullseye
  LengthFwd = 3
  LengthRev = 0
  Placement = pos=(0,0,71.7) rot=(0,0,1;0rad)
  Solid = true
  Symmetric = false
FEATURE [Sketcher::SketchObject] Sketch076  label="topSketch023"
  FullyConstrained = true
  sketch-geometry (6):
    g0: LineSegment StartX=19 StartY=38 StartZ=0 EndX=117 EndY=38 EndZ=0
    g1: ArcOfCircle CenterX=19 CenterY=19 CenterZ=0 NormalX=0 NormalY=0 NormalZ=1 AngleXU=0 Radius=19 StartAngle=1.5708 EndAngle=3.14159
    g2: LineSegment StartX=117 StartY=38 StartZ=0 EndX=117 EndY=19 EndZ=0
    g3: LineSegment StartX=98 StartY=1.0161e-12 StartZ=0 EndX=5.22862e-06 EndY=1.0161e-12 EndZ=0
    g4: LineSegment StartX=5.22862e-06 StartY=19 StartZ=0 EndX=5.22862e-06 EndY=1.0161e-12 EndZ=0
    g5: ArcOfCircle CenterX=98 CenterY=19 CenterZ=0 NormalX=0 NormalY=0 NormalZ=1 AngleXU=0 Radius=19 StartAngle=4.71239 EndAngle=6.28319
  constraints (16):
    c: Horizontal(g0)
    c: Distance(g0) = 98
    c: Coincident(g1,g0)
    c: Block(g1)
    c: Coincident(g2,g0)
    c: Vertical(g2)
    c: Distance(g2) = 19
    c: Horizontal(g3)
    c: Coincident(g4,g1)
    c: Vertical(g4)
    c: Coincident(g3,g4)
    c: Block(g3)
    c: Coincident(g5,g2)
    c: Coincident(g5,g3)
    c: Block(g0)
    c: Block(g5)
FEATURE [Part::Extrusion] Extrude066  label="sideA003"
  Base = -> Sketch076
  Dir = (0,0,1)
  DirMode = 2
  FaceMakerClass = Part::FaceMakerBullseye
  LengthFwd = 3
  LengthRev = 0
  Placement = pos=(0,0,-2.7) rot=(0,0,1;0rad)
  Solid = true
  Symmetric = false
FEATURE [Part::MultiFuse] Fusion142  label="removeFromBottom003"
  Placement = pos=(2,0,0) rot=(0,0,1;0rad)
  Shapes = -> [Extrude066,Extrude067]
FEATURE [Part::Cut] Cut065  label="screwRetainers002"
  Base = -> Fusion096
  Tool = -> Fusion142
FEATURE [Sketcher::SketchObject] Sketch077
  FullyConstrained = true
  Placement = pos=(117,19,0) rot=(0.57735,0.57735,0.57735;2.0944rad)
  sketch-geometry (8):
    g0: LineSegment StartX=-49.19 StartY=63.5 StartZ=0 EndX=-49.19 EndY=60.5 EndZ=0
    g1: LineSegment StartX=-49.19 StartY=11.5 StartZ=0 EndX=-49.19 EndY=8.5 EndZ=0
    g2: ArcOfCircle CenterX=-1.5 CenterY=62 CenterZ=0 NormalX=0 NormalY=0 NormalZ=1 AngleXU=0 Radius=1.5 StartAngle=4.71239 EndAngle=7.85398
    g3: ArcOfCircle CenterX=-1.5 CenterY=10 CenterZ=0 NormalX=0 NormalY=0 NormalZ=1 AngleXU=0 Radius=1.5 StartAngle=4.71239 EndAngle=7.85398
    g4: LineSegment StartX=-49.19 StartY=63.5 StartZ=0 EndX=-1.5 EndY=63.5 EndZ=0
    g5: LineSegment StartX=-49.19 StartY=60.5 StartZ=0 EndX=-1.5 EndY=60.5 EndZ=0
    g6: LineSegment StartX=-49.19 StartY=11.5 StartZ=0 EndX=-1.5 EndY=11.5 EndZ=0
    g7: LineSegment StartX=-49.19 StartY=8.5 StartZ=0 EndX=-1.5 EndY=8.5 EndZ=0
  constraints (19):
    c: Vertical(g0)
    c: Distance(g0) = 3
    c: Vertical(g1)
    c: Block(g1)
    c: Block(g2)
    c: Block(g3)
    c: Block(g0)
    c: Coincident(g4,g0)
    c: Coincident(g4,g2)
    c: Horizontal(g4)
    c: Coincident(g5,g0)
    c: Coincident(g5,g2)
    c: Horizontal(g5)
    c: Coincident(g6,g1)
    c: Coincident(g6,g3)
    c: Horizontal(g6)
    c: Coincident(g7,g1)
    c: Coincident(g7,g3)
    c: Horizontal(g7)
FEATURE [Part::Extrusion] Extrude068
  Base = -> Sketch077
  Dir = (1,0,0)
  DirMode = 2
  FaceMakerClass = Part::FaceMakerBullseye
  LengthFwd = 10
  LengthRev = 0
  Solid = true
  Symmetric = false
FEATURE [Part::Fillet] Fillet057  label="removeFromtMoreFrontCaseScrewRetainers002"
  Base = -> Extrude068
  Edges = 4 edges r=1.49: [Edge6,Edge11,Edge18,Edge23]
  Placement = pos=(-12,0,0) rot=(0,0,1;0rad)
FEATURE [Sketcher::SketchObject] Sketch078
  FullyConstrained = true
  Placement = pos=(117,19,0) rot=(0.57735,0.57735,0.57735;2.0944rad)
  sketch-geometry (8):
    g0: LineSegment StartX=-49.19 StartY=69.25 StartZ=0 EndX=-49.19 EndY=66.25 EndZ=0
    g1: LineSegment StartX=-49.19 StartY=5.75 StartZ=0 EndX=-49.19 EndY=2.75 EndZ=0
    g2: ArcOfCircle CenterX=-1.5 CenterY=67.75 CenterZ=0 NormalX=0 NormalY=0 NormalZ=1 AngleXU=0 Radius=1.5 StartAngle=4.71239 EndAngle=7.85398
    g3: ArcOfCircle CenterX=-1.5 CenterY=4.25 CenterZ=0 NormalX=0 NormalY=0 NormalZ=1 AngleXU=0 Radius=1.5 StartAngle=4.71239 EndAngle=7.85398
    g4: LineSegment StartX=-49.19 StartY=69.25 StartZ=0 EndX=-1.5 EndY=69.25 EndZ=0
    g5: LineSegment StartX=-49.19 StartY=66.25 StartZ=0 EndX=-1.5 EndY=66.25 EndZ=0
    g6: LineSegment StartX=-49.19 StartY=5.75 StartZ=0 EndX=-1.5 EndY=5.75 EndZ=0
    g7: LineSegment StartX=-49.19 StartY=2.75 StartZ=0 EndX=-1.5 EndY=2.75 EndZ=0
  constraints (19):
    c: Vertical(g0)
    c: Distance(g0) = 3
    c: Block(g0)
    c: Vertical(g1)
    c: Block(g2)
    c: Block(g3)
    c: Block(g1)
    c: Coincident(g4,g0)
    c: Coincident(g4,g2)
    c: Horizontal(g4)
    c: Coincident(g5,g0)
    c: Coincident(g5,g2)
    c: Horizontal(g5)
    c: Coincident(g6,g1)
    c: Coincident(g6,g3)
    c: Horizontal(g6)
    c: Coincident(g7,g1)
    c: Coincident(g7,g3)
    c: Horizontal(g7)
FEATURE [Part::Extrusion] Extrude069
  Base = -> Sketch078
  Dir = (1,0,0)
  DirMode = 2
  FaceMakerClass = Part::FaceMakerBullseye
  LengthFwd = 10
  LengthRev = 0
  Solid = true
  Symmetric = false
FEATURE [Part::Fillet] Fillet058  label="removeFromtMoreFrontCaseScrewRetainers003"
  Base = -> Extrude069
  Edges = 4 edges r=1.49: [Edge6,Edge11,Edge18,Edge23]
  Placement = pos=(-4,0,0) rot=(0,0,1;0rad)
FEATURE [Part::Cut] Cut066
  Base = -> Cut065
  Tool = -> Fillet058
FEATURE [Part::Cut] Cut067  label="screwPillars"
  Base = -> Cut066
  Tool = -> Fillet057
FEATURE [Part::MultiFuse] Fusion143  label="bottom021"
  Shapes = -> [Cut031,Cut063]
FEATURE [Part::Cylinder] Cylinder
  Angle = 360
  AttacherType = Attacher::AttachEngine3D
  Height = 10
  Placement = pos=(20.65,12,4.68) rot=(1,0,0;1.5708rad)
  Radius = 2
FEATURE [Part::Cylinder] Cylinder064
  Angle = 360
  AttacherType = Attacher::AttachEngine3D
  Height = 10
  Placement = pos=(20.65,12,67.38) rot=(1,0,0;1.5708rad)
  Radius = 2
FEATURE [Part::Cylinder] Cylinder065
  Angle = 360
  AttacherType = Attacher::AttachEngine3D
  Height = 10
  Placement = pos=(77.15,12,67.38) rot=(1,0,0;1.5708rad)
  Radius = 2
FEATURE [Part::Cylinder] Cylinder066
  Angle = 360
  AttacherType = Attacher::AttachEngine3D
  Height = 10
  Placement = pos=(77.15,12,4.68) rot=(1,0,0;1.5708rad)
  Radius = 2
FEATURE [Part::MultiFuse] Fusion144  label="removeFromThreadedInsertHousing"
  Shapes = -> [Cylinder065,Cylinder064,Cylinder,Cylinder066]
FEATURE [Part::Cut] Cut068  label="pcbStands001"
  Base = -> Cut064
  Tool = -> Fusion144
FEATURE [Part::MultiFuse] Fusion145
  Shapes = -> [Cut068,Fusion143]
FEATURE [Part::MultiFuse] Fusion146
  Shapes = -> [Fusion145]
FEATURE [Part::MultiFuse] Fusion147  label="bottom022"
  Shapes = -> [Cut067,Fusion146]
FEATURE [Part::MultiFuse] Fusion148  label="casePillars005"
  Shapes = -> [Cut047,Fusion092]
FEATURE [Part::MultiFuse] Fusion149  label="bottom023"
  Shapes = -> [Fusion124,Fusion113,Fusion147]
FEATURE [Part::MultiFuse] Fusion150  label="topBits"
  Shapes = -> [Cut025,Fusion148,Cut030,Fillet034]
FEATURE [Part::Feature] Face149 .. Face152  x4 (patterned run collapsed; names and placements below)
  shape: bbox 3.2 x 1.5 x 2e-07 mm, 1 faces, 0 solids (baked)
FEATURE [Part::Feature] Face153
  shape: bbox 3.6 x 3.2 x 2e-07 mm, 1 faces, 0 solids (baked)
FEATURE [Part::Feature] Face154
  shape: bbox 3.6 x 3.2 x 2e-07 mm, 1 faces, 0 solids (baked)
FEATURE [Sketcher::SketchObject] Sketch079  label="topSketch024"
  FullyConstrained = true
  sketch-geometry (6):
    g0: LineSegment StartX=19 StartY=38 StartZ=0 EndX=117 EndY=38 EndZ=0
    g1: ArcOfCircle CenterX=19 CenterY=19 CenterZ=0 NormalX=0 NormalY=0 NormalZ=1 AngleXU=0 Radius=19 StartAngle=1.5708 EndAngle=3.14159
    g2: LineSegment StartX=117 StartY=38 StartZ=0 EndX=117 EndY=19 EndZ=0
    g3: LineSegment StartX=98 StartY=1.0161e-12 StartZ=0 EndX=5.22862e-06 EndY=1.0161e-12 EndZ=0
    g4: LineSegment StartX=5.22862e-06 StartY=19 StartZ=0 EndX=5.22862e-06 EndY=1.0161e-12 EndZ=0
    g5: ArcOfCircle CenterX=98 CenterY=19 CenterZ=0 NormalX=0 NormalY=0 NormalZ=1 AngleXU=0 Radius=19 StartAngle=4.71239 EndAngle=6.28319
  constraints (16):
    c: Horizontal(g0)
    c: Distance(g0) = 98
    c: Coincident(g1,g0)
    c: Block(g1)
    c: Coincident(g2,g0)
    c: Vertical(g2)
    c: Distance(g2) = 19
    c: Horizontal(g3)
    c: Coincident(g4,g1)
    c: Vertical(g4)
    c: Coincident(g3,g4)
    c: Block(g3)
    c: Coincident(g5,g2)
    c: Coincident(g5,g3)
    c: Block(g0)
    c: Block(g5)
FEATURE [Sketcher::SketchObject] Sketch080  label="topSketch025"
  FullyConstrained = true
  sketch-geometry (6):
    g0: LineSegment StartX=19 StartY=38 StartZ=0 EndX=117 EndY=38 EndZ=0
    g1: ArcOfCircle CenterX=19 CenterY=19 CenterZ=0 NormalX=0 NormalY=0 NormalZ=1 AngleXU=0 Radius=19 StartAngle=1.5708 EndAngle=3.14159
    g2: LineSegment StartX=117 StartY=38 StartZ=0 EndX=117 EndY=19 EndZ=0
    g3: LineSegment StartX=98 StartY=1.0161e-12 StartZ=0 EndX=5.22862e-06 EndY=1.0161e-12 EndZ=0
    g4: LineSegment StartX=5.22862e-06 StartY=19 StartZ=0 EndX=5.22862e-06 EndY=1.0161e-12 EndZ=0
    g5: ArcOfCircle CenterX=98 CenterY=19 CenterZ=0 NormalX=0 NormalY=0 NormalZ=1 AngleXU=0 Radius=19 StartAngle=4.71239 EndAngle=6.28319
  constraints (16):
    c: Horizontal(g0)
    c: Distance(g0) = 98
    c: Coincident(g1,g0)
    c: Block(g1)
    c: Coincident(g2,g0)
    c: Vertical(g2)
    c: Distance(g2) = 19
    c: Horizontal(g3)
    c: Coincident(g4,g1)
    c: Vertical(g4)
    c: Coincident(g3,g4)
    c: Block(g3)
    c: Coincident(g5,g2)
    c: Coincident(g5,g3)
    c: Block(g0)
    c: Block(g5)
FEATURE [Part::Extrusion] Extrude070  label="sideA004"
  Base = -> Sketch080
  Dir = (0,0,1)
  DirMode = 2
  FaceMakerClass = Part::FaceMakerBullseye
  LengthFwd = 3
  LengthRev = 0
  Placement = pos=(0,0,-2.7) rot=(0,0,1;0rad)
  Solid = true
  Symmetric = false
FEATURE [Sketcher::SketchObject] Sketch081
  FullyConstrained = true
  Placement = pos=(117,19,0) rot=(0.57735,0.57735,0.57735;2.0944rad)
  sketch-geometry (8):
    g0: LineSegment StartX=-49.19 StartY=63.5 StartZ=0 EndX=-49.19 EndY=60.5 EndZ=0
    g1: LineSegment StartX=-49.19 StartY=11.5 StartZ=0 EndX=-49.19 EndY=8.5 EndZ=0
    g2: ArcOfCircle CenterX=-1.5 CenterY=62 CenterZ=0 NormalX=0 NormalY=0 NormalZ=1 AngleXU=0 Radius=1.5 StartAngle=4.71239 EndAngle=7.85398
    g3: ArcOfCircle CenterX=-1.5 CenterY=10 CenterZ=0 NormalX=0 NormalY=0 NormalZ=1 AngleXU=0 Radius=1.5 StartAngle=4.71239 EndAngle=7.85398
    g4: LineSegment StartX=-49.19 StartY=63.5 StartZ=0 EndX=-1.5 EndY=63.5 EndZ=0
    g5: LineSegment StartX=-49.19 StartY=60.5 StartZ=0 EndX=-1.5 EndY=60.5 EndZ=0
    g6: LineSegment StartX=-49.19 StartY=11.5 StartZ=0 EndX=-1.5 EndY=11.5 EndZ=0
    g7: LineSegment StartX=-49.19 StartY=8.5 StartZ=0 EndX=-1.5 EndY=8.5 EndZ=0
  constraints (19):
    c: Vertical(g0)
    c: Distance(g0) = 3
    c: Vertical(g1)
    c: Block(g1)
    c: Block(g2)
    c: Block(g3)
    c: Block(g0)
    c: Coincident(g4,g0)
    c: Coincident(g4,g2)
    c: Horizontal(g4)
    c: Coincident(g5,g0)
    c: Coincident(g5,g2)
    c: Horizontal(g5)
    c: Coincident(g6,g1)
    c: Coincident(g6,g3)
    c: Horizontal(g6)
    c: Coincident(g7,g1)
    c: Coincident(g7,g3)
    c: Horizontal(g7)
FEATURE [Part::Extrusion] Extrude071  label="sideB004"
  Base = -> Sketch079
  Dir = (0,0,1)
  DirMode = 2
  FaceMakerClass = Part::FaceMakerBullseye
  LengthFwd = 3
  LengthRev = 0
  Placement = pos=(0,0,71.7) rot=(0,0,1;0rad)
  Solid = true
  Symmetric = false
FEATURE [Part::MultiFuse] Fusion152  label="removeFromBottom004"
  Placement = pos=(2,0,0) rot=(0,0,1;0rad)
  Shapes = -> [Extrude070,Extrude071]
FEATURE [Part::Extrusion] Extrude072
  Base = -> Sketch081
  Dir = (1,0,0)
  DirMode = 2
  FaceMakerClass = Part::FaceMakerBullseye
  LengthFwd = 10
  LengthRev = 0
  Solid = true
  Symmetric = false
FEATURE [Part::Fillet] Fillet059  label="removeFromtMoreFrontCaseScrewRetainers004"
  Base = -> Extrude072
  Edges = 4 edges r=1.49: [Edge6,Edge11,Edge18,Edge23]
  Placement = pos=(-12,0,0) rot=(0,0,1;0rad)
FEATURE [Sketcher::SketchObject] Sketch082
  FullyConstrained = true
  Placement = pos=(117,19,0) rot=(0.57735,0.57735,0.57735;2.0944rad)
  sketch-geometry (8):
    g0: LineSegment StartX=-49.19 StartY=69.25 StartZ=0 EndX=-49.19 EndY=66.25 EndZ=0
    g1: LineSegment StartX=-49.19 StartY=5.75 StartZ=0 EndX=-49.19 EndY=2.75 EndZ=0
    g2: ArcOfCircle CenterX=-1.5 CenterY=67.75 CenterZ=0 NormalX=0 NormalY=0 NormalZ=1 AngleXU=0 Radius=1.5 StartAngle=4.71239 EndAngle=7.85398
    g3: ArcOfCircle CenterX=-1.5 CenterY=4.25 CenterZ=0 NormalX=0 NormalY=0 NormalZ=1 AngleXU=0 Radius=1.5 StartAngle=4.71239 EndAngle=7.85398
    g4: LineSegment StartX=-49.19 StartY=69.25 StartZ=0 EndX=-1.5 EndY=69.25 EndZ=0
    g5: LineSegment StartX=-49.19 StartY=66.25 StartZ=0 EndX=-1.5 EndY=66.25 EndZ=0
    g6: LineSegment StartX=-49.19 StartY=5.75 StartZ=0 EndX=-1.5 EndY=5.75 EndZ=0
    g7: LineSegment StartX=-49.19 StartY=2.75 StartZ=0 EndX=-1.5 EndY=2.75 EndZ=0
  constraints (19):
    c: Vertical(g0)
    c: Distance(g0) = 3
    c: Block(g0)
    c: Vertical(g1)
    c: Block(g2)
    c: Block(g3)
    c: Block(g1)
    c: Coincident(g4,g0)
    c: Coincident(g4,g2)
    c: Horizontal(g4)
    c: Coincident(g5,g0)
    c: Coincident(g5,g2)
    c: Horizontal(g5)
    c: Coincident(g6,g1)
    c: Coincident(g6,g3)
    c: Horizontal(g6)
    c: Coincident(g7,g1)
    c: Coincident(g7,g3)
    c: Horizontal(g7)
FEATURE [Part::Extrusion] Extrude073
  Base = -> Sketch082
  Dir = (1,0,0)
  DirMode = 2
  FaceMakerClass = Part::FaceMakerBullseye
  LengthFwd = 10
  LengthRev = 0
  Solid = true
  Symmetric = false
FEATURE [Part::Fillet] Fillet060  label="removeFromtMoreFrontCaseScrewRetainers005"
  Base = -> Extrude073
  Edges = 4 edges r=1.49: [Edge6,Edge11,Edge18,Edge23]
  Placement = pos=(-4,0,0) rot=(0,0,1;0rad)
FEATURE [Part::Revolution] Revolve163  label="backCaseScrewRetainer004"
  Angle = 360
  Axis = (0,1,0)
  Base = (0,0,0)
  FaceMakerClass = Part::FaceMakerBullseye
  Placement = pos=(12.5,3,62) rot=(0,0,1;0rad)
  Solid = false
  Source = -> Face149
  Symmetric = false
FEATURE [Part::Revolution] Revolve164  label="frontCaseScrewRetainer006"
  Angle = 360
  Axis = (0,1,0)
  Base = (0,0,0)
  FaceMakerClass = Part::FaceMakerBullseye
  Placement = pos=(89.5,3,68.5) rot=(0,0,1;0rad)
  Solid = false
  Source = -> Face151
  Symmetric = false
FEATURE [Part::Revolution] Revolve165  label="frontCaseScrewRetainer007"
  Angle = 360
  Axis = (0,1,0)
  Base = (0,0,0)
  FaceMakerClass = Part::FaceMakerBullseye
  Placement = pos=(89.5,3,3.5) rot=(0,0,1;0rad)
  Solid = false
  Source = -> Face152
  Symmetric = false
FEATURE [Part::Revolution] Revolve166  label="backCaseScrewRetainer005"
  Angle = 360
  Axis = (0,1,0)
  Base = (0,0,0)
  FaceMakerClass = Part::FaceMakerBullseye
  Placement = pos=(12.5,3,10) rot=(0,0,1;0rad)
  Solid = false
  Source = -> Face150
  Symmetric = false
FEATURE [Part::Revolution] Revolve167  label="moreFrontCaseScrewRetainer006"
  Angle = 360
  Axis = (0,1,0)
  Base = (0,0,0)
  FaceMakerClass = Part::FaceMakerBullseye
  Placement = pos=(109.5,4.5,68.5) rot=(0,0,1;0rad)
  Solid = false
  Source = -> Face153
  Symmetric = false
FEATURE [Part::Revolution] Revolve168  label="moreFrontCaseScrewRetainer007"
  Angle = 360
  Axis = (0,1,0)
  Base = (0,0,0)
  FaceMakerClass = Part::FaceMakerBullseye
  Placement = pos=(109.5,4.5,3.5) rot=(0,0,1;0rad)
  Solid = false
  Source = -> Face154
  Symmetric = false
FEATURE [Part::MultiFuse] Fusion151  label="screwRetainers003"
  Shapes = -> [Revolve168,Revolve167,Revolve166,Revolve165,Revolve164,Revolve163]
FEATURE [Part::Cut] Cut069  label="screwRetainers004"
  Base = -> Fusion151
  Tool = -> Fusion152
FEATURE [Part::Cut] Cut070
  Base = -> Cut069
  Tool = -> Fillet060
FEATURE [Part::Cut] Cut071  label="screwPillars001"
  Base = -> Cut070
  Tool = -> Fillet059
FEATURE [Part::MultiFuse] Fusion153  label="bottom024"
  Shapes = -> [Fusion149,Cut071]
FEATURE [Part::Cylinder] Cylinder067
  Angle = 360
  AttacherType = Attacher::AttachEngine3D
  Height = 10
  Placement = pos=(20.65,12,4.68) rot=(1,0,0;1.5708rad)
  Radius = 2
FEATURE [Part::Cylinder] Cylinder068
  Angle = 360
  AttacherType = Attacher::AttachEngine3D
  Height = 10
  Placement = pos=(20.65,12,67.38) rot=(1,0,0;1.5708rad)
  Radius = 2
FEATURE [Part::Cylinder] Cylinder069
  Angle = 360
  AttacherType = Attacher::AttachEngine3D
  Height = 10
  Placement = pos=(77.15,12,67.38) rot=(1,0,0;1.5708rad)
  Radius = 2
FEATURE [Part::Cylinder] Cylinder070
  Angle = 360
  AttacherType = Attacher::AttachEngine3D
  Height = 10
  Placement = pos=(77.15,12,4.68) rot=(1,0,0;1.5708rad)
  Radius = 2
FEATURE [Part::MultiFuse] Fusion154  label="removeFromThreadedInsertHousing001"
  Shapes = -> [Cylinder069,Cylinder068,Cylinder067,Cylinder070]
FEATURE [Part::Cut] Cut072  label="bottom025"
  Base = -> Fusion153
  Tool = -> Fusion154
FEATURE [Image::ImagePlane] ImagePlane
  XSize = 339
  YSize = 72
FEATURE [Sketcher::SketchObject] Sketch083
  FullyConstrained = false
  MapMode = 5
  Support = -> [XY_Plane]
  sketch-geometry (205):
    g0: LineSegment StartX=-151.619 StartY=28.8932 StartZ=0 EndX=-140.819 EndY=28.8932 EndZ=0
    g1: LineSegment StartX=-151.619 StartY=24.0313 StartZ=0 EndX=-151.619 EndY=28.8932 EndZ=0
    g2: LineSegment StartX=-140.819 StartY=17.7713 StartZ=0 EndX=-151.619 EndY=17.7713 EndZ=0
    g3: LineSegment StartX=-151.619 StartY=17.7713 StartZ=0 EndX=-151.619 EndY=22.6313 EndZ=0
    g4: LineSegment StartX=-151.619 StartY=22.6313 StartZ=0 EndX=-145.128 EndY=22.6313 EndZ=0
    g5: LineSegment StartX=-145.128 StartY=24.0313 StartZ=0 EndX=-140.819 EndY=28.8932 EndZ=0
    g6: LineSegment StartX=-145.128 StartY=22.6313 StartZ=0 EndX=-140.819 EndY=17.7713 EndZ=0
    g7: ArcOfCircle CenterX=-155.157 CenterY=23.3323 CenterZ=0 NormalX=0 NormalY=0 NormalZ=1 AngleXU=0 Radius=6.92354 StartAngle=1.03434 EndAngle=5.24885
    g8: ArcOfCircle CenterX=-155.157 CenterY=23.3323 CenterZ=0 NormalX=0 NormalY=0 NormalZ=1 AngleXU=0 Radius=12.6269 StartAngle=1.28675 EndAngle=4.99643
    g9: LineSegment StartX=-151.619 StartY=35.4532 StartZ=0 EndX=-151.619 EndY=29.2832 EndZ=0
    g10: LineSegment StartX=-151.619 StartY=17.3813 StartZ=0 EndX=-151.619 EndY=11.2113 EndZ=0
    g11-g21: Circle x11 (B-spline internal-alignment scaffolding for g22; pole/knot coordinates omitted)
    g22: BSplineCurve PolesCount=11 KnotsCount=9 Degree=3 IsPeriodic=0
    g23-g31: GeomPoint x9 (B-spline internal-alignment scaffolding for g22; pole/knot coordinates omitted)
    g32-g49: Circle x18 (B-spline internal-alignment scaffolding for g50; pole/knot coordinates omitted)
    g50: BSplineCurve PolesCount=18 KnotsCount=16 Degree=3 IsPeriodic=0
    g51-g66: GeomPoint x16 (B-spline internal-alignment scaffolding for g50; pole/knot coordinates omitted)
    g67: LineSegment StartX=-117.124 StartY=30.093 StartZ=0 EndX=-117.603 EndY=26.5272 EndZ=0
    g68: LineSegment StartX=-117.603 StartY=17.8472 StartZ=0 EndX=-117.124 EndY=14.2659 EndZ=0
    g69: Ellipse CenterX=-109.671 CenterY=20.025 CenterZ=0 NormalX=0 NormalY=0 NormalZ=1 MajorRadius=3.34798 MinorRadius=2.71052 AngleXU=-1.56793
    g70: GeomPoint X=-109.666 Y=18.0598 Z=0
    g71: GeomPoint X=-109.677 Y=21.9902 Z=0
    g72: Ellipse CenterX=-109.671 CenterY=20.0123 CenterZ=0 NormalX=0 NormalY=0 NormalZ=1 MajorRadius=6.93002 MinorRadius=6.36273 AngleXU=-3.13976
    g73: GeomPoint X=-112.417 Y=20.0073 Z=0
    g74: GeomPoint X=-106.925 Y=20.0173 Z=0
    g75: Ellipse CenterX=-51.7682 CenterY=20.1463 CenterZ=0 NormalX=0 NormalY=0 NormalZ=1 MajorRadius=3.19279 MinorRadius=2.71052 AngleXU=-1.52774
    g76: GeomPoint X=-51.6955 Y=18.4606 Z=0
    g77: GeomPoint X=-51.8408 Y=21.832 Z=0
    g78: GeomPoint X=-54.5142 Y=20.1413 Z=0
    g79: GeomPoint X=-49.0221 Y=20.1513 Z=0
    g80: Ellipse CenterX=-51.7682 CenterY=20.1463 CenterZ=0 NormalX=0 NormalY=0 NormalZ=1 MajorRadius=6.93002 MinorRadius=6.36273 AngleXU=-3.13976
    g81: Ellipse CenterX=-22.8436 CenterY=20.1783 CenterZ=0 NormalX=0 NormalY=0 NormalZ=1 MajorRadius=3.31512 MinorRadius=2.71052 AngleXU=-1.60214
    g82: GeomPoint X=-22.9034 Y=18.2706 Z=0
    g83: GeomPoint X=-22.7838 Y=22.0861 Z=0
    g84: GeomPoint X=-25.5897 Y=20.1733 Z=0
    g85: GeomPoint X=-20.0976 Y=20.1833 Z=0
    g86: Ellipse CenterX=-22.8436 CenterY=20.1783 CenterZ=0 NormalX=0 NormalY=0 NormalZ=1 MajorRadius=6.93002 MinorRadius=6.36273 AngleXU=-3.13976
    g87: LineSegment StartX=-101.889 StartY=14.1107 StartZ=0 EndX=-97.7455 EndY=14.1107 EndZ=0
    g88: LineSegment StartX=-93.8155 StartY=14.1107 StartZ=0 EndX=-89.6755 EndY=14.1107 EndZ=0
    g89: LineSegment StartX=-85.7455 StartY=14.1107 StartZ=0 EndX=-81.6055 EndY=14.1107 EndZ=0
    g90: LineSegment StartX=-101.889 StartY=14.1107 StartZ=0 EndX=-101.889 EndY=25.9907 EndZ=0
    g91: LineSegment StartX=-101.889 StartY=25.9907 StartZ=0 EndX=-97.8594 EndY=25.9907 EndZ=0
    g92: LineSegment StartX=-97.8594 StartY=25.9907 StartZ=0 EndX=-97.8594 EndY=24.0907 EndZ=0
    g93: LineSegment StartX=-97.7455 StartY=14.1107 StartZ=0 EndX=-97.7455 EndY=19.9107 EndZ=0
    g94: LineSegment StartX=-89.6755 StartY=14.1107 StartZ=0 EndX=-89.6755 EndY=19.9107 EndZ=0
    g95: LineSegment StartX=-93.8155 StartY=14.1107 StartZ=0 EndX=-93.8155 EndY=21.0107 EndZ=0
    g96-g106: Circle x11 (B-spline internal-alignment scaffolding for g107; pole/knot coordinates omitted)
    g107: BSplineCurve PolesCount=11 KnotsCount=9 Degree=3 IsPeriodic=0
    g108-g116: GeomPoint x9 (B-spline internal-alignment scaffolding for g107; pole/knot coordinates omitted)
    g117: BSplineCurve PolesCount=11 KnotsCount=9 Degree=3 IsPeriodic=0
    g118-g125: Circle x8 (B-spline internal-alignment scaffolding for g126; pole/knot coordinates omitted)
    g126: BSplineCurve PolesCount=8 KnotsCount=6 Degree=3 IsPeriodic=0
    g127-g132: GeomPoint x6 (B-spline internal-alignment scaffolding for g126; pole/knot coordinates omitted)
    g133: BSplineCurve PolesCount=8 KnotsCount=6 Degree=3 IsPeriodic=0
    g134: LineSegment StartX=-85.7455 StartY=21.0107 StartZ=0 EndX=-85.7455 EndY=14.1107 EndZ=0
    g135: LineSegment StartX=-80.0879 StartY=14.1107 StartZ=0 EndX=-75.944 EndY=14.1107 EndZ=0
    g136: LineSegment StartX=-72.014 StartY=14.1107 StartZ=0 EndX=-67.874 EndY=14.1107 EndZ=0
    g137: LineSegment StartX=-63.944 StartY=14.1107 StartZ=0 EndX=-59.804 EndY=14.1107 EndZ=0
    g138: LineSegment StartX=-80.0879 StartY=14.1107 StartZ=0 EndX=-80.0879 EndY=25.9907 EndZ=0
    g139: LineSegment StartX=-80.0879 StartY=25.9907 StartZ=0 EndX=-76.0579 EndY=25.9907 EndZ=0
    g140: LineSegment StartX=-76.0579 StartY=25.9907 StartZ=0 EndX=-76.0579 EndY=24.0907 EndZ=0
    g141: LineSegment StartX=-75.944 StartY=14.1107 StartZ=0 EndX=-75.944 EndY=19.9107 EndZ=0
    g142: LineSegment StartX=-67.874 StartY=14.1107 StartZ=0 EndX=-67.874 EndY=19.9107 EndZ=0
    g143: LineSegment StartX=-72.014 StartY=14.1107 StartZ=0 EndX=-72.014 EndY=21.0107 EndZ=0
    g144-g148: Circle x5 (B-spline internal-alignment scaffolding for g149; pole/knot coordinates omitted)
    g149: BSplineCurve PolesCount=11 KnotsCount=9 Degree=3 IsPeriodic=0
    g150-g158: GeomPoint x9 (B-spline internal-alignment scaffolding for g149; pole/knot coordinates omitted)
    g159: BSplineCurve PolesCount=11 KnotsCount=9 Degree=3 IsPeriodic=0
    g160-g167: Circle x8 (B-spline internal-alignment scaffolding for g168; pole/knot coordinates omitted)
    g168: BSplineCurve PolesCount=8 KnotsCount=6 Degree=3 IsPeriodic=0
    g169-g174: GeomPoint x6 (B-spline internal-alignment scaffolding for g168; pole/knot coordinates omitted)
    g175: BSplineCurve PolesCount=8 KnotsCount=6 Degree=3 IsPeriodic=0
    g176: LineSegment StartX=-63.944 StartY=21.0107 StartZ=0 EndX=-63.944 EndY=14.1107 EndZ=0
    g177: LineSegment StartX=-59.804 StartY=14.1107 StartZ=0 EndX=-59.804 EndY=21.5868 EndZ=0
    g178: BSplineCurve PolesCount=4 KnotsCount=2 Degree=3 IsPeriodic=0
    g179: GeomPoint X=-59.804 Y=21.5868 Z=0
    g180: GeomPoint X=-60.2379 Y=24.0907 Z=0
    g181: LineSegment StartX=-81.6055 StartY=14.1107 StartZ=0 EndX=-81.6055 EndY=21.5868 EndZ=0
    g182: LineSegment StartX=-151.619 StartY=24.0313 StartZ=0 EndX=-145.128 EndY=24.0313 EndZ=0
    g183: Circle CenterX=-82.0394 CenterY=24.0907 CenterZ=0 NormalX=0 NormalY=0 NormalZ=1 AngleXU=0 Radius=1
    g184: Circle CenterX=-81.7131 CenterY=23.2736 CenterZ=0 NormalX=0 NormalY=0 NormalZ=1 AngleXU=0 Radius=1
    g185: Circle CenterX=-81.6055 CenterY=21.5868 CenterZ=0 NormalX=0 NormalY=0 NormalZ=1 AngleXU=0 Radius=1
    g186: BSplineCurve PolesCount=3 KnotsCount=2 Degree=2 IsPeriodic=0
    g187: GeomPoint X=-82.0394 Y=24.0907 Z=0
    g188: GeomPoint X=-81.6055 Y=21.5868 Z=0
    g189: Ellipse CenterX=-37.3522 CenterY=19.9515 CenterZ=0 NormalX=0 NormalY=0 NormalZ=1 MajorRadius=2.99755 MinorRadius=2.49 AngleXU=1.5708
    g190: GeomPoint X=-37.3522 Y=21.6203 Z=0
    g191: GeomPoint X=-37.3522 Y=18.2826 Z=0
    g192: LineSegment StartX=-38.8121 StartY=26.36 StartZ=0 EndX=-38.8121 EndY=13.76 EndZ=0
    g193: LineSegment StartX=-38.8121 StartY=26.36 StartZ=0 EndX=-38.8121 EndY=20.06 EndZ=0
    g194: LineSegment StartX=-38.8121 StartY=20.06 StartZ=0 EndX=-44.1496 EndY=20.06 EndZ=0
    g195: Ellipse CenterX=-38.7647 CenterY=20.06 CenterZ=0 NormalX=0 NormalY=0 NormalZ=1 MajorRadius=6.30025 MinorRadius=5.3849 AngleXU=1.57276
    g196: LineSegment StartX=-38.777 StartY=26.3602 StartZ=0 EndX=-38.7523 EndY=13.7597 EndZ=0
    g197: LineSegment StartX=-44.1496 StartY=20.0494 StartZ=0 EndX=-33.3798 EndY=20.0705 EndZ=0
    g198: GeomPoint X=-38.7711 Y=23.3304 Z=0
    g199: GeomPoint X=-38.7583 Y=16.7895 Z=0
    g200: LineSegment StartX=-34.6109 StartY=14.0378 StartZ=0 EndX=-30.8984 EndY=14.0378 EndZ=0
    g201: LineSegment StartX=-34.6109 StartY=14.0378 StartZ=0 EndX=-34.6109 EndY=16.0476 EndZ=0
    g202: LineSegment StartX=-30.8984 StartY=14.0378 StartZ=0 EndX=-30.8984 EndY=31.1784 EndZ=0
    g203: LineSegment StartX=-30.8984 StartY=31.1784 StartZ=0 EndX=-34.9984 EndY=31.1784 EndZ=0
    g204: LineSegment StartX=-34.9984 StartY=31.1784 StartZ=0 EndX=-34.9984 EndY=23.9368 EndZ=0
  constraints (203):
    c: Coincident(g1,g0)
    c: Horizontal(g0)
    c: Vertical(g1)
    c: Coincident(g2,g3)
    c: Coincident(g3,g4)
    c: Horizontal(g4)
    c: Horizontal(g2)
    c: Vertical(g3)
    c: Block(g1)
    c: Distance(g3) = 4.86
    c: Block(g4)
    c: Distance(g0) = 10.8
    c: Distance(g2) = 10.8
    c: Coincident(g5,g0)
    c: Coincident(g6,g4)
    c: Coincident(g6,g2)
    c: Block(g8)
    c: Block(g7)
    c: Coincident(g9,g8)
    c: Coincident(g9,g7)
    c: Vertical(g9)
    c: Coincident(g10,g7)
    c: Coincident(g10,g8)
    c: Vertical(g10)
    c: Weight(g11) = 1
    c: Equal(g11, g12-g21) x10
    c: InternalAlignment(g11-g21 -> g22) x11
    c: InternalAlignment(g23-g31 -> g22) x9
    c: Block(g22)
    c: Weight(g32) = 1
    c: Equal(g32, g33-g49) x17
    c: InternalAlignment(g32-g49 -> g50) x18
    c: InternalAlignment(g51-g66 -> g50) x16
    c: Block(g50)
    c: Coincident(g67,g50)
    c: Coincident(g67,g22)
    c: Coincident(g68,g22)
    c: Coincident(g68,g50)
    c: InternalAlignment(g70,g69)
    c: InternalAlignment(g71,g69)
    c: Block(g69)
    c: InternalAlignment(g73,g72)
    c: InternalAlignment(g74,g72)
    c: Block(g72)
    c: InternalAlignment(g76,g75)
    c: InternalAlignment(g77,g75)
    c: InternalAlignment(g78,g80)
    c: InternalAlignment(g79,g80)
    c: Block(g80)
    c: Coincident(g75,g80)
    c: Block(g75)
    c: InternalAlignment(g82,g81)
    c: InternalAlignment(g83,g81)
    c: InternalAlignment(g84,g86)
    c: InternalAlignment(g85,g86)
    c: Block(g86)
    c: Coincident(g81,g86)
    c: Block(g81)
    c: Horizontal(g87)
    c: Block(g87)
    c: Horizontal(g88)
    c: Distance(g88) = 4.14
    c: Horizontal(g89)
    c: Equal(g88,g89) = 4.14
    c: Block(g89)
    c: Block(g88)
    c: Coincident(g90,g87)
    c: Vertical(g90)
    c: Distance(g90) = 11.88
    c: Coincident(g91,g90)
    c: Horizontal(g91)
    c: Coincident(g92,g91)
    c: Vertical(g92)
    c: Distance(g91) = 4.03
    c: Distance(g92) = 1.9
    c: Coincident(g93,g87)
    c: Vertical(g93)
    c: Vertical(g94)
    c: Coincident(g94,g88)
    c: Distance(g93) = 5.8
    c: Distance(g94) = 5.8
    c: Vertical(g95)
    c: Coincident(g95,g88)
    c: Distance(g95) = 6.9
    c: Coincident(g107,g92)
    c: Weight(g96) = 1
    c: Equal(g96, g97-g106) x10
    c: InternalAlignment(g96-g106 -> g107) x11
    c: InternalAlignment(g108-g116 -> g107) x9
    c: Block(g107)
    c: Block(g117)
    c: Coincident(g126,g93)
    c: Weight(g118) = 1
    c: Equal(g118, g119-g125) x7
    c: Coincident(g126,g95)
    c: InternalAlignment(g118-g125 -> g126) x8
    c: InternalAlignment(g127-g132 -> g126) x6
    c: Coincident(g133,g94)
    c: Block(g126)
    c: Block(g133)
    c: Coincident(g134,g133)
    c: Coincident(g134,g89)
    c: Vertical(g134)
    c: Horizontal(g135)
    c: Block(g135)
    c: Horizontal(g136)
    c: Equal(g88,g136) = 4.14
    c: Horizontal(g137)
    c: Equal(g136,g137) = 4.14
    c: Block(g137)
    c: Block(g136)
    c: Coincident(g138,g135)
    c: Vertical(g138)
    c: Equal(g90,g138) = 11.88
    c: Coincident(g139,g138)
    c: Horizontal(g139)
    c: Coincident(g140,g139)
    c: Vertical(g140)
    c: Equal(g91,g139) = 4.03
    c: Equal(g92,g140) = 1.9
    c: Coincident(g141,g135)
    c: Vertical(g141)
    c: Vertical(g142)
    c: Coincident(g142,g136)
    c: Equal(g93,g141) = 5.8
    c: Equal(g94,g142) = 5.8
    c: Vertical(g143)
    c: Coincident(g143,g136)
    c: Equal(g95,g143) = 6.9
    c: Coincident(g149,g140)
    c: Equal(g96,g144) = 1
    c: Equal(g144, g145-g148) x4
    c: InternalAlignment(g144-g148 -> g149) x5
    c: InternalAlignment(g150-g158 -> g149) x9
    c: Block(g149)
    c: Block(g159)
    c: Coincident(g168,g141)
    c: Equal(g118,g160) = 1
    c: Equal(g160, g161-g167) x7
    c: Coincident(g168,g143)
    c: InternalAlignment(g160-g167 -> g168) x8
    c: InternalAlignment(g169-g174 -> g168) x6
    c: Coincident(g175,g142)
    c: Block(g168)
    c: Block(g175)
    c: Coincident(g176,g175)
    c: Coincident(g176,g137)
    c: Vertical(g176)
    c: Coincident(g177,g137)
    c: Vertical(g177)
    c: Coincident(g178,g177)
    c: Coincident(g178,g159)
    c: InternalAlignment(g179,g178)
    c: InternalAlignment(g180,g178)
    c: Block(g178)
    c: Vertical(g181)
    c: Coincident(g181,g89)
    c: Block(g5)
    c: Coincident(g182,g1)
    c: Coincident(g182,g5)
    c: Horizontal(g182)
    c: Coincident(g186,g117)
    c: Weight(g183) = 1
    c: Equal(g183,g184)
    c: Equal(g183,g185)
    c: Coincident(g186,g181)
    c: InternalAlignment(g183,g186)
    c: InternalAlignment(g184,g186)
    c: InternalAlignment(g185,g186)
    c: InternalAlignment(g187,g186)
    c: InternalAlignment(g188,g186)
    c: Block(g186)
    c: InternalAlignment(g190,g189)
    c: InternalAlignment(g191,g189)
    c: Block(g189)
    c: Vertical(g192)
    c: Distance(g192) = 12.6
    c: Block(g192)
    c: Vertical(g193)
    c: Distance(g193) = 6.3
    c: Coincident(g193,g192)
    c: Coincident(g194,g193)
    c: Horizontal(g194)
    c: Block(g194)
    c: InternalAlignment(g196-g199 -> g195) x4
    c: PointOnObject(g192,g195)
    c: PointOnObject(g192,g195)
    c: PointOnObject(g194,g195)
    c: Block(g195)
    c: Horizontal(g200)
    c: Block(g200)
    c: Coincident(g201,g200)
    c: Vertical(g201)
    c: PointOnObject(g201,g195)
    c: Coincident(g202,g200)
    c: Vertical(g202)
    c: Block(g202)
    c: Distance(g200) = 3.71244
    c: Coincident(g203,g202)
    c: Horizontal(g203)
    c: Distance(g203) = 4.1
    c: Coincident(g204,g203)
    c: Vertical(g204)
FEATURE [PartDesign::Body] Body
  Group = -> [Sketch083]
  Origin = -> Origin
FEATURE [Sketcher::SketchObject] Sketch084
  FullyConstrained = true
  MapMode = 5
  Support = -> [XY_Plane001]
FEATURE [PartDesign::Body] Body001
  Group = -> [Sketch084]
  Origin = -> Origin001
